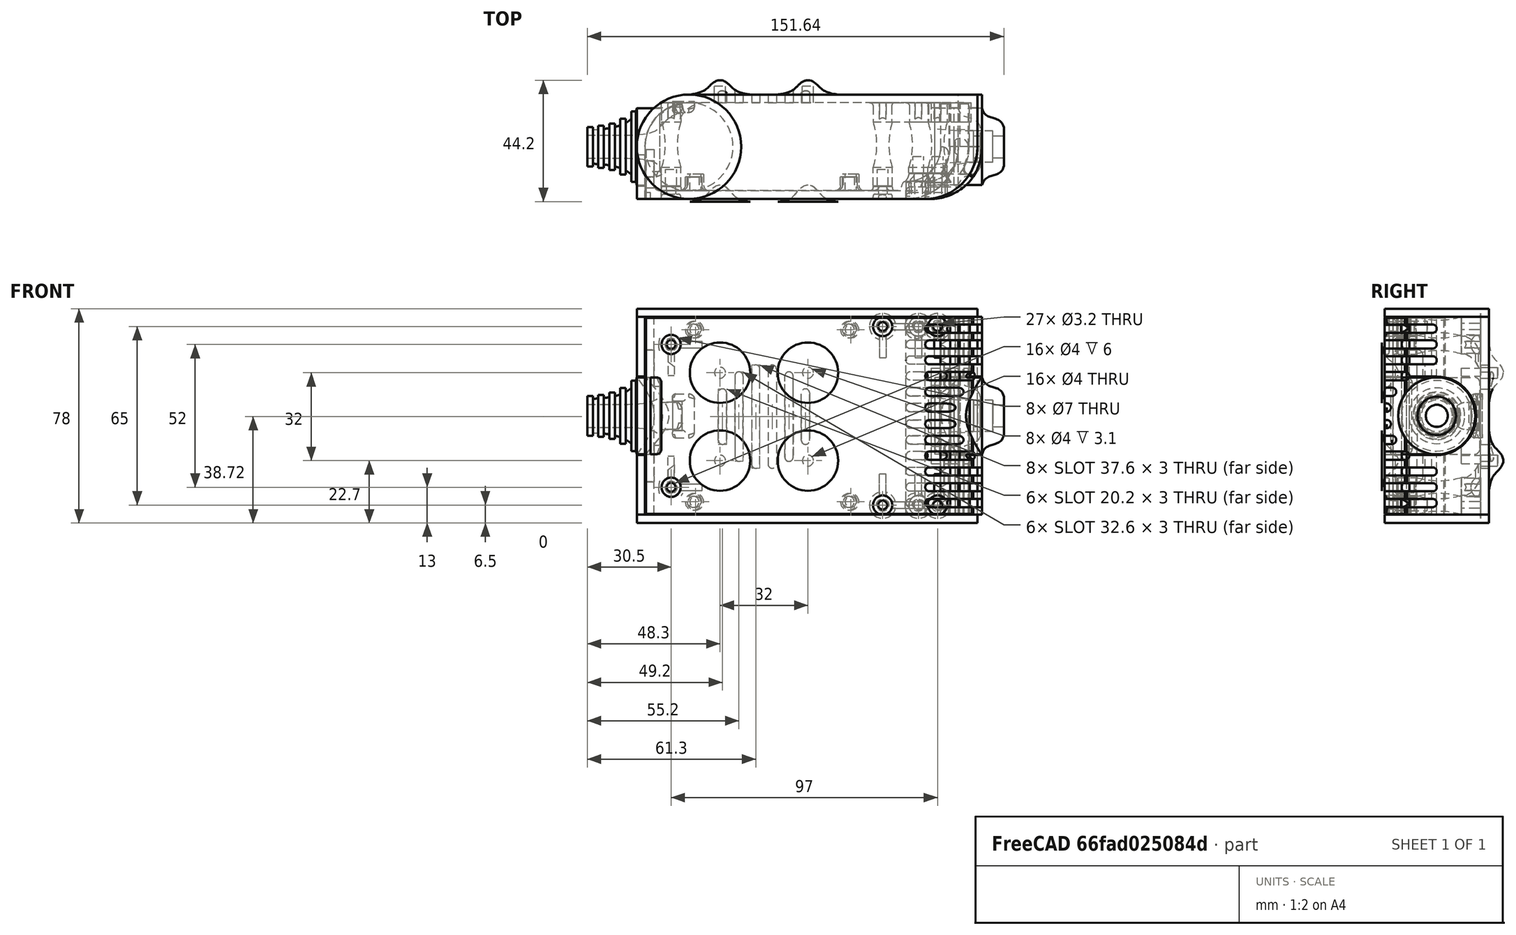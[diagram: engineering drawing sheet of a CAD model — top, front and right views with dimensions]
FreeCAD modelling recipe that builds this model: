
FCSTD DOCUMENT  (FreeCAD 0.19R0.19.2)
Label: enclosure_171FCStd
License: All rights reserved
LicenseURL: http://en.wikipedia.org/wiki/All_rights_reserved
objects: Part::Revolution×146, Part::MultiFuse×140, Part::Feature×140, Sketcher::SketchObject×78, Part::Cut×66, Part::Cylinder×66, Part::Extrusion×63, Part::Fillet×56, Part::Box×36, App::MeasureDistance×4
note: 791 computed .brp shape members not serialized (recipe doc carries the construction recipe); baked Part::Feature solids carry a one-line shape summary decoded from their .brp

FEATURE [Sketcher::SketchObject] Sketch  label="topSketch"
  FullyConstrained = true
  sketch-geometry (20):
    g0: LineSegment StartX=5.21097e-06 StartY=3 StartZ=0 EndX=5.21097e-06 EndY=19 EndZ=0
    g1: ArcOfCircle CenterX=19 CenterY=19 CenterZ=0 NormalX=0 NormalY=0 NormalZ=1 AngleXU=0 Radius=19 StartAngle=1.5708 EndAngle=3.14159
    g2: ArcOfCircle CenterX=19 CenterY=19 CenterZ=0 NormalX=0 NormalY=0 NormalZ=1 AngleXU=0 Radius=16 StartAngle=1.5708 EndAngle=3.14159
    g3: LineSegment StartX=114 StartY=35 StartZ=0 EndX=19 EndY=35 EndZ=0
    g4: LineSegment StartX=5.21097e-06 StartY=3 StartZ=0 EndX=5.21097e-06 EndY=0 EndZ=0
    g5: LineSegment StartX=3 StartY=0 StartZ=0 EndX=5.21097e-06 EndY=0 EndZ=0
    g6: LineSegment StartX=3 StartY=19 StartZ=0 EndX=3 EndY=0 EndZ=0
    g7: LineSegment StartX=19 StartY=38 StartZ=0 EndX=124 EndY=38 EndZ=0
    g8: Circle CenterX=119 CenterY=35 CenterZ=0 NormalX=0 NormalY=0 NormalZ=1 AngleXU=0 Radius=1
    g9: Circle CenterX=121 CenterY=35 CenterZ=0 NormalX=0 NormalY=0 NormalZ=1 AngleXU=0 Radius=1
    g10: Circle CenterX=121 CenterY=33 CenterZ=0 NormalX=0 NormalY=0 NormalZ=1 AngleXU=0 Radius=1
    g11: BSplineCurve PolesCount=3 KnotsCount=2 Degree=2 IsPeriodic=0
    g12: GeomPoint X=119 Y=35 Z=0
    g13: GeomPoint X=121 Y=33 Z=0
    g14: LineSegment StartX=119 StartY=35 StartZ=0 EndX=114 EndY=35 EndZ=0
    g15: ArcOfCircle CenterX=105 CenterY=19 CenterZ=0 NormalX=0 NormalY=0 NormalZ=1 AngleXU=0 Radius=19 StartAngle=5.7297 EndAngle=6.28319
    g16: ArcOfCircle CenterX=105 CenterY=19 CenterZ=0 NormalX=0 NormalY=0 NormalZ=1 AngleXU=0 Radius=16 StartAngle=5.60905 EndAngle=6.28319
    g17: LineSegment StartX=121 StartY=33 StartZ=0 EndX=121 EndY=19 EndZ=0
    g18: LineSegment StartX=124 StartY=38 StartZ=0 EndX=124 EndY=19 EndZ=0
    g19: LineSegment StartX=117.5 StartY=9.01251 StartZ=0 EndX=121.163 EndY=9.0125 EndZ=0
  constraints (46):
    c: Vertical(g0)
    c: Block(g0)
    c: Coincident(g1,g0)
    c: Block(g1)
    c: Coincident(g2,g1)
    c: Block(g2)
    c: Coincident(g3,g2)
    c: Horizontal(g3)
    c: Tangent(g3,g2)
    c: Coincident(g4,g0)
    c: Distance(g4) = 3
    c: Vertical(g4)
    c: Coincident(g5,g4)
    c: Horizontal(g5)
    c: Coincident(g6,g2)
    c: Coincident(g6,g5)
    c: Vertical(g6)
    c: Horizontal(g7)
    c: Distance(g7) = 105
    c: Coincident(g7,g1)
    c: Block(g3)
    c: Weight(g8) = 1
    c: Equal(g8,g9)
    c: Equal(g8,g10)
    c: InternalAlignment(g8,g11)
    c: InternalAlignment(g9,g11)
    c: InternalAlignment(g10,g11)
    c: InternalAlignment(g12,g11)
    c: InternalAlignment(g13,g11)
    c: Block(g11)
    c: Coincident(g14,g11)
    c: Coincident(g14,g3)
    c: Horizontal(g14)
    c: Block(g15)
    c: Coincident(g16,g15)
    c: Block(g16)
    c: Coincident(g17,g11)
    c: Coincident(g17,g16)
    c: Vertical(g17)
    c: Distance(g17) = 14
    c: Coincident(g18,g7)
    c: Coincident(g18,g15)
    c: Vertical(g18)
    c: Distance(g18) = 19
    c: Coincident(g19,g16)
    c: Coincident(g19,g15)
FEATURE [Sketcher::SketchObject] Sketch001  label="bottomSketch"
  FullyConstrained = true
  sketch-geometry (32):
    g0: LineSegment StartX=3.3 StartY=-6.03275e-07 StartZ=0 EndX=98 EndY=-6.03275e-07 EndZ=0
    g1: ArcOfCircle CenterX=98 CenterY=19 CenterZ=0 NormalX=0 NormalY=0 NormalZ=1 AngleXU=0 Radius=19 StartAngle=4.71239 EndAngle=5.71103
    g2: LineSegment StartX=6.3 StartY=8 StartZ=0 EndX=3.3 EndY=8 EndZ=0
    g3: LineSegment StartX=3.3 StartY=8 StartZ=0 EndX=3.3 EndY=-6.03275e-07 EndZ=0
    g4: ArcOfCircle CenterX=8.3 CenterY=5 CenterZ=0 NormalX=0 NormalY=0 NormalZ=1 AngleXU=0 Radius=2 StartAngle=3.14159 EndAngle=4.71239
    g5: LineSegment StartX=6.3 StartY=8 StartZ=0 EndX=6.3 EndY=5 EndZ=0
    g6: ArcOfCircle CenterX=98 CenterY=19 CenterZ=0 NormalX=0 NormalY=0 NormalZ=1 AngleXU=0 Radius=12.7 StartAngle=4.71239 EndAngle=6.28319
    g7: LineSegment StartX=94.7 StartY=3 StartZ=0 EndX=8.3 EndY=3 EndZ=0
    g8-g12: Circle x5 (B-spline internal-alignment scaffolding for g13; pole/knot coordinates omitted)
    g13: BSplineCurve PolesCount=5 KnotsCount=3 Degree=3 IsPeriodic=0
    g14: GeomPoint X=98 Y=6.3 Z=0
    g15: GeomPoint X=96.3938 Y=4.71946 Z=0
    g16: GeomPoint X=94.7 Y=3 Z=0
    g17-g23: Circle x7 (B-spline internal-alignment scaffolding for g24; pole/knot coordinates omitted)
    g24: BSplineCurve PolesCount=7 KnotsCount=5 Degree=3 IsPeriodic=0
    g25-g29: GeomPoint x5 (B-spline internal-alignment scaffolding for g24; pole/knot coordinates omitted)
    g30: ArcOfCircle CenterX=98 CenterY=19 CenterZ=0 NormalX=0 NormalY=0 NormalZ=1 AngleXU=0 Radius=15.7 StartAngle=5.81226 EndAngle=6.28319
    g31: LineSegment StartX=110.7 StartY=19 StartZ=0 EndX=113.7 EndY=19 EndZ=0
  constraints (41):
    c: Horizontal(g0)
    c: Coincident(g1,g0)
    c: Block(g1)
    c: Horizontal(g2)
    c: Distance(g2) = 3
    c: Coincident(g3,g2)
    c: Vertical(g3)
    c: Coincident(g3,g0)
    c: Block(g4)
    c: Block(g2)
    c: Coincident(g5,g2)
    c: Coincident(g5,g4)
    c: Vertical(g5)
    c: Coincident(g6,g1)
    c: Block(g6)
    c: Coincident(g7,g4)
    c: Horizontal(g7)
    c: Block(g0)
    c: Block(g7)
    c: Block(g3)
    c: Coincident(g13,g6)
    c: Weight(g8) = 1
    c: Equal(g8, g9-g12) x4
    c: Coincident(g13,g7)
    c: InternalAlignment(g8-g12 -> g13) x5
    c: InternalAlignment(g14,g13)
    c: InternalAlignment(g15,g13)
    c: InternalAlignment(g16,g13)
    c: Block(g13)
    c: Weight(g17) = 1
    c: Equal(g17, g18-g23) x6
    c: Coincident(g24,g1)
    c: InternalAlignment(g17-g23 -> g24) x7
    c: InternalAlignment(g25-g29 -> g24) x5
    c: Block(g24)
    c: Coincident(g30,g24)
    c: Coincident(g31,g6)
    c: Coincident(g31,g30)
    c: Horizontal(g31)
    c: Block(g31)
    c: Block(g30)
FEATURE [Part::Extrusion] Extrude  label="top"
  Base = -> Sketch
  Dir = (0,0,1)
  DirMode = 2
  FaceMakerClass = Part::FaceMakerBullseye
  LengthFwd = 72
  LengthRev = 0
  Solid = true
  Symmetric = false
FEATURE [Part::Extrusion] Extrude001  label="bottom"
  Base = -> Sketch001
  Dir = (0,0,1)
  DirMode = 2
  FaceMakerClass = Part::FaceMakerBullseye
  LengthFwd = 71.4
  LengthRev = 0
  Placement = pos=(0,0,0.3) rot=(0,0,1;0rad)
  Solid = true
  Symmetric = false
FEATURE [Sketcher::SketchObject] Sketch002  label="topSketch001"
  FullyConstrained = true
  sketch-geometry (6):
    g0: ArcOfCircle CenterX=19 CenterY=19 CenterZ=0 NormalX=0 NormalY=0 NormalZ=1 AngleXU=0 Radius=19 StartAngle=1.5708 EndAngle=3.14159
    g1: LineSegment StartX=5.22862e-06 StartY=19 StartZ=0 EndX=5.22862e-06 EndY=1.19904e-11 EndZ=0
    g2: LineSegment StartX=19 StartY=38 StartZ=0 EndX=124 EndY=38 EndZ=0
    g3: LineSegment StartX=5.22862e-06 StartY=1.19904e-11 StartZ=0 EndX=105 EndY=1.19904e-11 EndZ=0
    g4: ArcOfCircle CenterX=105 CenterY=19 CenterZ=0 NormalX=0 NormalY=0 NormalZ=1 AngleXU=0 Radius=19 StartAngle=4.71239 EndAngle=6.28319
    g5: LineSegment StartX=124 StartY=38 StartZ=0 EndX=124 EndY=19 EndZ=0
  constraints (16):
    c: Block(g0)
    c: Coincident(g1,g0)
    c: Vertical(g1)
    c: Horizontal(g2)
    c: Distance(g2) = 105
    c: Coincident(g2,g0)
    c: Distance(g1) = 19
    c: Coincident(g3,g1)
    c: Horizontal(g3)
    c: Distance(g3) = 105
    c: Block(g4)
    c: Coincident(g4,g3)
    c: Coincident(g5,g2)
    c: Coincident(g5,g4)
    c: Vertical(g5)
    c: Distance(g5) = 19
FEATURE [Part::Extrusion] Extrude002  label="sideA"
  Base = -> Sketch002
  Dir = (0,0,1)
  DirMode = 2
  FaceMakerClass = Part::FaceMakerBullseye
  LengthFwd = 3
  LengthRev = 0
  Placement = pos=(0,0,-3) rot=(0,0,1;0rad)
  Solid = true
  Symmetric = false
FEATURE [Sketcher::SketchObject] Sketch003  label="topSketch002"
  FullyConstrained = true
  sketch-geometry (6):
    g0: LineSegment StartX=19 StartY=38 StartZ=0 EndX=117 EndY=38 EndZ=0
    g1: ArcOfCircle CenterX=19 CenterY=19 CenterZ=0 NormalX=0 NormalY=0 NormalZ=1 AngleXU=0 Radius=19 StartAngle=1.5708 EndAngle=3.14159
    g2: LineSegment StartX=117 StartY=38 StartZ=0 EndX=117 EndY=19 EndZ=0
    g3: LineSegment StartX=98 StartY=1.0161e-12 StartZ=0 EndX=5.22862e-06 EndY=1.0161e-12 EndZ=0
    g4: LineSegment StartX=5.22862e-06 StartY=19 StartZ=0 EndX=5.22862e-06 EndY=1.0161e-12 EndZ=0
    g5: ArcOfCircle CenterX=98 CenterY=19 CenterZ=0 NormalX=0 NormalY=0 NormalZ=1 AngleXU=0 Radius=19 StartAngle=4.71239 EndAngle=6.28319
  constraints (16):
    c: Horizontal(g0)
    c: Distance(g0) = 98
    c: Coincident(g1,g0)
    c: Block(g1)
    c: Coincident(g2,g0)
    c: Vertical(g2)
    c: Distance(g2) = 19
    c: Horizontal(g3)
    c: Coincident(g4,g1)
    c: Vertical(g4)
    c: Coincident(g3,g4)
    c: Block(g3)
    c: Coincident(g5,g2)
    c: Coincident(g5,g3)
    c: Block(g0)
    c: Block(g5)
FEATURE [Sketcher::SketchObject] Sketch004
  FullyConstrained = true
  MapMode = 3
  Placement = pos=(0,0,0) rot=(1,0,0;1.5708rad)
  Support = -> [Extrude]
  sketch-geometry (8):
    g0: Circle CenterX=80.351 CenterY=-67.6202 CenterZ=0 NormalX=0 NormalY=0 NormalZ=1 AngleXU=0 Radius=2
    g1: Circle CenterX=80.351 CenterY=-67.6202 CenterZ=0 NormalX=0 NormalY=0 NormalZ=1 AngleXU=0 Radius=3
    g2: Circle CenterX=80.351 CenterY=-4.92017 CenterZ=0 NormalX=0 NormalY=0 NormalZ=1 AngleXU=0 Radius=2
    g3: Circle CenterX=80.351 CenterY=-4.92017 CenterZ=0 NormalX=0 NormalY=0 NormalZ=1 AngleXU=0 Radius=3
    g4: Circle CenterX=23.851 CenterY=-4.92017 CenterZ=0 NormalX=0 NormalY=0 NormalZ=1 AngleXU=0 Radius=2
    g5: Circle CenterX=23.851 CenterY=-4.92017 CenterZ=0 NormalX=0 NormalY=0 NormalZ=1 AngleXU=0 Radius=3
    g6: Circle CenterX=23.851 CenterY=-67.6202 CenterZ=0 NormalX=0 NormalY=0 NormalZ=1 AngleXU=0 Radius=2
    g7: Circle CenterX=23.851 CenterY=-67.6202 CenterZ=0 NormalX=0 NormalY=0 NormalZ=1 AngleXU=0 Radius=3
  constraints (8):
    c: Block(g3)
    c: Block(g2)
    c: Block(g1)
    c: Block(g0)
    c: Block(g6)
    c: Block(g7)
    c: Block(g4)
    c: Block(g5)
FEATURE [Part::Extrusion] Extrude004
  Base = -> Sketch004
  Dir = (0,-1,2e-16)
  DirMode = 2
  FaceMakerClass = Part::FaceMakerBullseye
  LengthFwd = 6
  LengthRev = 0
  Placement = pos=(0,9,0) rot=(0,0,1;0rad)
  Solid = true
  Symmetric = false
FEATURE [Sketcher::SketchObject] Sketch005
  FullyConstrained = true
  MapMode = 3
  Placement = pos=(0,0,0) rot=(1,0,0;1.5708rad)
  Support = -> [Extrude]
  sketch-geometry (8):
    g0: Circle CenterX=80.351 CenterY=-67.6202 CenterZ=0 NormalX=0 NormalY=0 NormalZ=1 AngleXU=0 Radius=3
    g1: Circle CenterX=80.351 CenterY=-4.92017 CenterZ=0 NormalX=0 NormalY=0 NormalZ=1 AngleXU=0 Radius=3
    g2: Circle CenterX=23.851 CenterY=-4.92017 CenterZ=0 NormalX=0 NormalY=0 NormalZ=1 AngleXU=0 Radius=3
    g3: Circle CenterX=23.851 CenterY=-67.6202 CenterZ=0 NormalX=0 NormalY=0 NormalZ=1 AngleXU=0 Radius=3
    g4: Circle CenterX=23.851 CenterY=-67.6202 CenterZ=0 NormalX=0 NormalY=0 NormalZ=1 AngleXU=0 Radius=5
    g5: Circle CenterX=80.351 CenterY=-67.6202 CenterZ=0 NormalX=0 NormalY=0 NormalZ=1 AngleXU=0 Radius=5
    g6: Circle CenterX=23.851 CenterY=-4.92017 CenterZ=0 NormalX=0 NormalY=0 NormalZ=1 AngleXU=0 Radius=5
    g7: Circle CenterX=80.351 CenterY=-4.92017 CenterZ=0 NormalX=0 NormalY=0 NormalZ=1 AngleXU=0 Radius=5
  constraints (8):
    c: Block(g1)
    c: Block(g0)
    c: Block(g3)
    c: Block(g2)
    c: Block(g5)
    c: Block(g4)
    c: Block(g6)
    c: Block(g7)
FEATURE [Part::Extrusion] Extrude005
  Base = -> Sketch005
  Dir = (0,-1,2e-16)
  DirMode = 2
  FaceMakerClass = Part::FaceMakerBullseye
  LengthFwd = 2
  LengthRev = 0
  Solid = true
  Symmetric = false
FEATURE [Sketcher::SketchObject] Sketch006
  FullyConstrained = true
  MapMode = 3
  Placement = pos=(0,0,0) rot=(1,0,0;1.5708rad)
  sketch-geometry (8):
    g0: Circle CenterX=80.351 CenterY=-67.6202 CenterZ=0 NormalX=0 NormalY=0 NormalZ=1 AngleXU=0 Radius=3
    g1: Circle CenterX=80.351 CenterY=-4.92017 CenterZ=0 NormalX=0 NormalY=0 NormalZ=1 AngleXU=0 Radius=3
    g2: Circle CenterX=23.851 CenterY=-4.92017 CenterZ=0 NormalX=0 NormalY=0 NormalZ=1 AngleXU=0 Radius=3
    g3: Circle CenterX=23.851 CenterY=-67.6202 CenterZ=0 NormalX=0 NormalY=0 NormalZ=1 AngleXU=0 Radius=3
    g4: Circle CenterX=23.851 CenterY=-67.6202 CenterZ=0 NormalX=0 NormalY=0 NormalZ=1 AngleXU=0 Radius=5
    g5: Circle CenterX=80.351 CenterY=-67.6202 CenterZ=0 NormalX=0 NormalY=0 NormalZ=1 AngleXU=0 Radius=5
    g6: Circle CenterX=23.851 CenterY=-4.92017 CenterZ=0 NormalX=0 NormalY=0 NormalZ=1 AngleXU=0 Radius=5
    g7: Circle CenterX=80.351 CenterY=-4.92017 CenterZ=0 NormalX=0 NormalY=0 NormalZ=1 AngleXU=0 Radius=5
  constraints (8):
    c: Block(g1)
    c: Block(g0)
    c: Block(g3)
    c: Block(g2)
    c: Block(g5)
    c: Block(g4)
    c: Block(g6)
    c: Block(g7)
FEATURE [Part::Extrusion] Extrude007
  Base = -> Sketch006
  Dir = (0,-1,2e-16)
  DirMode = 2
  FaceMakerClass = Part::FaceMakerBullseye
  LengthFwd = 2
  LengthRev = 0
  Solid = true
  Symmetric = false
FEATURE [Part::Fillet] Fillet
  Base = -> Extrude007
  Edges = 4 edges r=1.99: [Edge6,Edge12,Edge18,Edge24]
FEATURE [Part::Cut] Cut
  Base = -> Extrude005
  Placement = pos=(0,5,0) rot=(0,0,1;0rad)
  Tool = -> Fillet
FEATURE [Part::MultiFuse] Fusion  label="pCBScrews"
  Placement = pos=(-2.5,0,72.3) rot=(0,0,1;0rad)
  Shapes = -> [Extrude004,Cut]
FEATURE [App::MeasureDistance] Distance  label="Distance: 0.69 mm"
  Distance = 0.685967
  P1 = (24.0138,2.9647,0.3)
  P2 = (23.8901,3,-0.373787)
FEATURE [App::MeasureDistance] Distance001  label="Distance: 0.53 mm"
  Distance = 0.533607
  P1 = (80.2939,3,72.2334)
  P2 = (80.281,2.99661,71.7)
FEATURE [Part::Fillet] Fillet001
  Base = -> Extrude001
  Edges = 1 edges r=2.4: [Edge17]
FEATURE [Part::Fillet] Fillet002  label="bottom001"
  Base = -> Fillet001
  Edges = 1 edges r=2.4: [Edge36]
FEATURE [Part::Fillet] Fillet003  label="top001"
  Base = -> Extrude
  Edges = 1 edges r=2: [Edge1]
FEATURE [Sketcher::SketchObject] Sketch007
  FullyConstrained = true
  sketch-geometry (16):
    g0: LineSegment StartX=4 StartY=0 StartZ=0 EndX=4 EndY=2.4 EndZ=0
    g1: LineSegment StartX=4 StartY=2.4 StartZ=0 EndX=7 EndY=2.4 EndZ=0
    g2: LineSegment StartX=4 StartY=0 StartZ=0 EndX=5.7 EndY=0 EndZ=0
    g3: LineSegment StartX=5.7 StartY=0 StartZ=0 EndX=5.7 EndY=-5.6 EndZ=0
    g4-g8: Circle x5 (B-spline internal-alignment scaffolding for g9; pole/knot coordinates omitted)
    g9: BSplineCurve PolesCount=5 KnotsCount=3 Degree=3 IsPeriodic=0
    g10: GeomPoint X=7 Y=2.4 Z=0
    g11: GeomPoint X=10.4582 Y=-1.55472 Z=0
    g12: GeomPoint X=14 Y=-5.6 Z=0
    g13: LineSegment StartX=14 StartY=-5.6 StartZ=0 EndX=14 EndY=-14.1 EndZ=0
    g14: LineSegment StartX=14 StartY=-14.1 StartZ=0 EndX=6.5 EndY=-14.1 EndZ=0
    g15: LineSegment StartX=5.7 StartY=-5.6 StartZ=0 EndX=6.5 EndY=-14.1 EndZ=0
  constraints (28):
    c: Distance(g0) = 2.4
    c: Vertical(g0)
    c: Block(g0)
    c: Coincident(g1,g0)
    c: Horizontal(g1)
    c: Distance(g1) = 3
    c: Coincident(g2,g0)
    c: Horizontal(g2)
    c: Distance(g2) = 1.7
    c: Coincident(g3,g2)
    c: Vertical(g3)
    c: Distance(g3) = 5.6
    c: Coincident(g9,g1)
    c: Weight(g4) = 1
    c: Equal(g4, g5-g8) x4
    c: InternalAlignment(g4-g8 -> g9) x5
    c: InternalAlignment(g10,g9)
    c: InternalAlignment(g11,g9)
    c: InternalAlignment(g12,g9)
    c: Block(g9)
    c: Coincident(g13,g9)
    c: Vertical(g13)
    c: Distance(g13) = 8.5
    c: Coincident(g14,g13)
    c: Horizontal(g14)
    c: Distance(g14) = 7.5
    c: Coincident(g15,g3)
    c: Coincident(g15,g14)
FEATURE [Part::Feature] Face
  shape: bbox 10 x 16.5 x 2e-07 mm, 1 faces, 0 solids (baked)
FEATURE [Part::Revolution] Revolve  label="plugHousing"
  Angle = 360
  Axis = (0,1,0)
  Base = (0,0,0)
  FaceMakerClass = Part::FaceMakerBullseye
  Placement = pos=(0,0,36.15) rot=(0,0,1;0rad)
  Solid = false
  Source = -> Face
  Symmetric = false
FEATURE [Part::Feature] Face001
  shape: bbox 10 x 16.5 x 2e-07 mm, 1 faces, 0 solids (baked)
FEATURE [Part::Revolution] Revolve001  label="plugHousing001"
  Angle = 360
  Axis = (0,1,0)
  Base = (0,0,0)
  FaceMakerClass = Part::FaceMakerBullseye
  Placement = pos=(0,0,36.15) rot=(0,0,1;0rad)
  Solid = false
  Source = -> Face001
  Symmetric = false
FEATURE [Part::MultiFuse] Fusion001  label="plugHousing002"
  Placement = pos=(0,0,0) rot=(0,0,1;1.5708rad)
  Shapes = -> [Revolve001,Revolve]
FEATURE [Part::Feature] Face002
  shape: bbox 10 x 16.5 x 2e-07 mm, 1 faces, 0 solids (baked)
FEATURE [Part::Revolution] Revolve003  label="plugHousing005"
  Angle = 360
  Axis = (0,1,0)
  Base = (0,0,0)
  FaceMakerClass = Part::FaceMakerBullseye
  Placement = pos=(0,0,36.15) rot=(0,0,1;0rad)
  Solid = false
  Source = -> Face002
  Symmetric = false
FEATURE [Part::Feature] Face003
  shape: bbox 10 x 16.5 x 2e-07 mm, 1 faces, 0 solids (baked)
FEATURE [Part::Revolution] Revolve002  label="plugHousing003"
  Angle = 360
  Axis = (0,1,0)
  Base = (0,0,0)
  FaceMakerClass = Part::FaceMakerBullseye
  Placement = pos=(0,0,36.15) rot=(0,0,1;0rad)
  Solid = false
  Source = -> Face003
  Symmetric = false
FEATURE [Part::MultiFuse] Fusion002  label="plugHousing004"
  Placement = pos=(0,0,0) rot=(0,0,1;1.5708rad)
  Shapes = -> [Revolve002,Revolve003]
FEATURE [Part::MultiFuse] Fusion003  label="plugHousing006"
  Placement = pos=(0,19,0) rot=(0,0,1;3.14159rad)
  Shapes = -> [Fusion002,Fusion001]
FEATURE [Part::Feature] Face004
  shape: bbox 10 x 16.5 x 2e-07 mm, 1 faces, 0 solids (baked)
FEATURE [Part::Revolution] Revolve006  label="plugHousing010"
  Angle = 360
  Axis = (0,1,0)
  Base = (0,0,0)
  FaceMakerClass = Part::FaceMakerBullseye
  Placement = pos=(0,0,36.15) rot=(0,0,1;0rad)
  Solid = false
  Source = -> Face004
  Symmetric = false
FEATURE [Part::Feature] Face005
  shape: bbox 10 x 16.5 x 2e-07 mm, 1 faces, 0 solids (baked)
FEATURE [Part::Revolution] Revolve007  label="plugHousing011"
  Angle = 360
  Axis = (0,1,0)
  Base = (0,0,0)
  FaceMakerClass = Part::FaceMakerBullseye
  Placement = pos=(0,0,36.15) rot=(0,0,1;0rad)
  Solid = false
  Source = -> Face005
  Symmetric = false
FEATURE [Part::Feature] Face006
  shape: bbox 10 x 16.5 x 2e-07 mm, 1 faces, 0 solids (baked)
FEATURE [Part::Revolution] Revolve004  label="plugHousing007"
  Angle = 360
  Axis = (0,1,0)
  Base = (0,0,0)
  FaceMakerClass = Part::FaceMakerBullseye
  Placement = pos=(0,0,36.15) rot=(0,0,1;0rad)
  Solid = false
  Source = -> Face006
  Symmetric = false
FEATURE [Part::MultiFuse] Fusion004  label="plugHousing009"
  Placement = pos=(0,0,0) rot=(0,0,1;1.5708rad)
  Shapes = -> [Revolve004,Revolve007]
FEATURE [Part::Feature] Face007
  shape: bbox 10 x 16.5 x 2e-07 mm, 1 faces, 0 solids (baked)
FEATURE [Part::Revolution] Revolve005  label="plugHousing008"
  Angle = 360
  Axis = (0,1,0)
  Base = (0,0,0)
  FaceMakerClass = Part::FaceMakerBullseye
  Placement = pos=(0,0,36.15) rot=(0,0,1;0rad)
  Solid = false
  Source = -> Face007
  Symmetric = false
FEATURE [Part::MultiFuse] Fusion005  label="plugHousing012"
  Placement = pos=(0,0,0) rot=(0,0,1;1.5708rad)
  Shapes = -> [Revolve006,Revolve005]
FEATURE [Part::MultiFuse] Fusion006  label="plugHousing013"
  Placement = pos=(0,19,0) rot=(0,0,1;3.14159rad)
  Shapes = -> [Fusion005,Fusion004]
FEATURE [Part::MultiFuse] Fusion007  label="plugHousing014"
  Placement = pos=(122.621,0,-0.15) rot=(0,0,1;0rad)
  Shapes = -> [Fusion003,Fusion006]
FEATURE [Part::Cylinder] Cylinder002
  Angle = 360
  AttacherType = Attacher::AttachEngine3D
  Height = 20
  Placement = pos=(0,0,36.15) rot=(0,0,1;0rad)
  Radius = 4
FEATURE [Part::Cylinder] Cylinder003
  Angle = 360
  AttacherType = Attacher::AttachEngine3D
  Height = 10
  Placement = pos=(0,0,36.15) rot=(0,0,1;0rad)
  Radius = 4
FEATURE [Part::MultiFuse] Fusion009  label="removeToCreateHoleForPlugHousing"
  Placement = pos=(70,19,36.15) rot=(0,1,0;1.5708rad)
  Shapes = -> [Cylinder002,Cylinder003]
FEATURE [Part::Cylinder] Cylinder004
  Angle = 360
  AttacherType = Attacher::AttachEngine3D
  Height = 20
  Placement = pos=(0,0,36.15) rot=(0,0,1;0rad)
  Radius = 4
FEATURE [Part::Cylinder] Cylinder005
  Angle = 360
  AttacherType = Attacher::AttachEngine3D
  Height = 10
  Placement = pos=(0,0,36.15) rot=(0,0,1;0rad)
  Radius = 4
FEATURE [Part::MultiFuse] Fusion010  label="removeToCreateHoleForPlugHousing001"
  Placement = pos=(70,19,36.15) rot=(0,1,0;1.5708rad)
  Shapes = -> [Cylinder004,Cylinder005]
FEATURE [Part::Cut] Cut001
  Base = -> Fillet003
  Tool = -> Fusion010
FEATURE [Part::Cut] Cut002  label="Bottom"
  Base = -> Fillet002
  Tool = -> Fusion009
FEATURE [Part::Feature] Face008
  shape: bbox 10 x 16.5 x 2e-07 mm, 1 faces, 0 solids (baked)
FEATURE [Part::Revolution] Revolve011  label="plugHousing021"
  Angle = 360
  Axis = (0,1,0)
  Base = (0,0,0)
  FaceMakerClass = Part::FaceMakerBullseye
  Placement = pos=(0,0,36.15) rot=(0,0,1;0rad)
  Solid = false
  Source = -> Face008
  Symmetric = false
FEATURE [Part::Feature] Face009
  shape: bbox 10 x 16.5 x 2e-07 mm, 1 faces, 0 solids (baked)
FEATURE [Part::Revolution] Revolve012  label="plugHousing022"
  Angle = 360
  Axis = (0,1,0)
  Base = (0,0,0)
  FaceMakerClass = Part::FaceMakerBullseye
  Placement = pos=(0,0,36.15) rot=(0,0,1;0rad)
  Solid = false
  Source = -> Face009
  Symmetric = false
FEATURE [Part::Feature] Face010 .. Face013  x4 (patterned run collapsed; names and placements below)
  shape: bbox 10 x 16.5 x 2e-07 mm, 1 faces, 0 solids (baked)
FEATURE [Part::Revolution] Revolve015  label="plugHousing027"
  Angle = 360
  Axis = (0,1,0)
  Base = (0,0,0)
  FaceMakerClass = Part::FaceMakerBullseye
  Placement = pos=(0,0,36.15) rot=(0,0,1;0rad)
  Solid = false
  Source = -> Face013
  Symmetric = false
FEATURE [Part::Feature] Face014
  shape: bbox 10 x 16.5 x 2e-07 mm, 1 faces, 0 solids (baked)
FEATURE [Part::Feature] Face015
  shape: bbox 10 x 16.5 x 2e-07 mm, 1 faces, 0 solids (baked)
FEATURE [Part::Feature] Face016
  shape: bbox 10 x 16.5 x 2e-07 mm, 1 faces, 0 solids (baked)
FEATURE [Part::Revolution] Revolve019  label="plugHousing033"
  Angle = 360
  Axis = (0,1,0)
  Base = (0,0,0)
  FaceMakerClass = Part::FaceMakerBullseye
  Placement = pos=(0,0,36.15) rot=(0,0,1;0rad)
  Solid = false
  Source = -> Face016
  Symmetric = false
FEATURE [Part::Feature] Face017
  shape: bbox 10 x 16.5 x 2e-07 mm, 1 faces, 0 solids (baked)
FEATURE [Part::Revolution] Revolve020  label="plugHousing034"
  Angle = 360
  Axis = (0,1,0)
  Base = (0,0,0)
  FaceMakerClass = Part::FaceMakerBullseye
  Placement = pos=(0,0,36.15) rot=(0,0,1;0rad)
  Solid = false
  Source = -> Face017
  Symmetric = false
FEATURE [Part::Feature] Face018
  shape: bbox 10 x 16.5 x 2e-07 mm, 1 faces, 0 solids (baked)
FEATURE [Part::Revolution] Revolve016  label="plugHousing030"
  Angle = 360
  Axis = (0,1,0)
  Base = (0,0,0)
  FaceMakerClass = Part::FaceMakerBullseye
  Placement = pos=(0,0,36.15) rot=(0,0,1;0rad)
  Solid = false
  Source = -> Face018
  Symmetric = false
FEATURE [Part::MultiFuse] Fusion020  label="plugHousing038"
  Placement = pos=(0,0,0) rot=(0,0,1;1.5708rad)
  Shapes = -> [Revolve016,Revolve020]
FEATURE [Part::Feature] Face019
  shape: bbox 10 x 16.5 x 2e-07 mm, 1 faces, 0 solids (baked)
FEATURE [Part::Feature] Face020
  shape: bbox 10 x 16.5 x 2e-07 mm, 1 faces, 0 solids (baked)
FEATURE [Part::Revolution] Revolve017  label="plugHousing031"
  Angle = 360
  Axis = (0,1,0)
  Base = (0,0,0)
  FaceMakerClass = Part::FaceMakerBullseye
  Placement = pos=(0,0,36.15) rot=(0,0,1;0rad)
  Solid = false
  Source = -> Face020
  Symmetric = false
FEATURE [Part::MultiFuse] Fusion021  label="plugHousing039"
  Placement = pos=(0,0,0) rot=(0,0,1;1.5708rad)
  Shapes = -> [Revolve019,Revolve017]
FEATURE [Part::MultiFuse] Fusion023  label="plugHousing041"
  Placement = pos=(0,19,0) rot=(0,0,1;3.14159rad)
  Shapes = -> [Fusion021,Fusion020]
FEATURE [Part::Revolution] Revolve022  label="plugHousing043"
  Angle = 360
  Axis = (0,1,0)
  Base = (0,0,0)
  FaceMakerClass = Part::FaceMakerBullseye
  Placement = pos=(0,0,36.15) rot=(0,0,1;0rad)
  Solid = false
  Source = -> Face019
  Symmetric = false
FEATURE [Part::Feature] Face021
  shape: bbox 10 x 16.5 x 2e-07 mm, 1 faces, 0 solids (baked)
FEATURE [Part::Revolution] Revolve023  label="plugHousing044"
  Angle = 360
  Axis = (0,1,0)
  Base = (0,0,0)
  FaceMakerClass = Part::FaceMakerBullseye
  Placement = pos=(0,0,36.15) rot=(0,0,1;0rad)
  Solid = false
  Source = -> Face021
  Symmetric = false
FEATURE [Part::Feature] Face022
  shape: bbox 10 x 16.5 x 2e-07 mm, 1 faces, 0 solids (baked)
FEATURE [Part::Revolution] Revolve018  label="plugHousing032"
  Angle = 360
  Axis = (0,1,0)
  Base = (0,0,0)
  FaceMakerClass = Part::FaceMakerBullseye
  Placement = pos=(0,0,36.15) rot=(0,0,1;0rad)
  Solid = false
  Source = -> Face022
  Symmetric = false
FEATURE [Part::MultiFuse] Fusion022  label="plugHousing040"
  Placement = pos=(0,0,0) rot=(0,0,1;1.5708rad)
  Shapes = -> [Revolve018,Revolve023]
FEATURE [Part::Feature] Face023
  shape: bbox 10 x 16.5 x 2e-07 mm, 1 faces, 0 solids (baked)
FEATURE [Part::Revolution] Revolve021  label="plugHousing035"
  Angle = 360
  Axis = (0,1,0)
  Base = (0,0,0)
  FaceMakerClass = Part::FaceMakerBullseye
  Placement = pos=(0,0,36.15) rot=(0,0,1;0rad)
  Solid = false
  Source = -> Face023
  Symmetric = false
FEATURE [Part::MultiFuse] Fusion018  label="plugHousing036"
  Placement = pos=(0,0,0) rot=(0,0,1;1.5708rad)
  Shapes = -> [Revolve022,Revolve021]
FEATURE [Part::MultiFuse] Fusion019  label="plugHousing037"
  Placement = pos=(0,19,0) rot=(0,0,1;3.14159rad)
  Shapes = -> [Fusion018,Fusion022]
FEATURE [Part::MultiFuse] Fusion024  label="plugHousing042"
  Placement = pos=(122.621,0,-0.15) rot=(0,0,1;0rad)
  Shapes = -> [Fusion023,Fusion019]
FEATURE [Part::Cylinder] Cylinder006
  Angle = 360
  AttacherType = Attacher::AttachEngine3D
  Height = 20
  Placement = pos=(0,0,36.15) rot=(0,0,1;0rad)
  Radius = 14.3
FEATURE [Part::Cylinder] Cylinder007
  Angle = 360
  AttacherType = Attacher::AttachEngine3D
  Height = 10
  Placement = pos=(0,0,36.15) rot=(0,0,1;0rad)
  Radius = 4
FEATURE [Part::MultiFuse] Fusion026  label="removeToCreteHoleForPlugHousing"
  Placement = pos=(70,19,36) rot=(0,1,0;1.5708rad)
  Shapes = -> [Cylinder006,Cylinder007]
FEATURE [Part::Box] Box001  label="Cube001"
  AttacherType = Attacher::AttachEngine3D
  Height = 28
  Length = 3
  Placement = pos=(110.7,19,22) rot=(0,0,1;0rad)
  Width = 15.7
FEATURE [Part::Cut] Cut003  label="top002"
  Base = -> Cut001
  Tool = -> Fusion007
FEATURE [Part::Revolution] Revolve008  label="plugHousing015"
  Angle = 360
  Axis = (0,1,0)
  Base = (0,0,0)
  FaceMakerClass = Part::FaceMakerBullseye
  Placement = pos=(0,0,36.15) rot=(0,0,1;0rad)
  Solid = false
  Source = -> Face010
  Symmetric = false
FEATURE [Part::MultiFuse] Fusion013  label="plugHousing020"
  Placement = pos=(0,0,0) rot=(0,0,1;1.5708rad)
  Shapes = -> [Revolve008,Revolve012]
FEATURE [Part::Cut] Cut004  label="top003"
  Base = -> Cut003
  Placement = pos=(1,0,0) rot=(0,0,1;0rad)
  Tool = -> Fusion026
FEATURE [Part::Cylinder] Cylinder008
  Angle = 360
  AttacherType = Attacher::AttachEngine3D
  Height = 20
  Placement = pos=(0,0,36.15) rot=(0,0,1;0rad)
  Radius = 10.3
FEATURE [Part::Cylinder] Cylinder009
  Angle = 360
  AttacherType = Attacher::AttachEngine3D
  Height = 10
  Placement = pos=(0,0,36.15) rot=(0,0,1;0rad)
  Radius = 4
FEATURE [Part::MultiFuse] Fusion027  label="removeToCreteHoleForPlugHousing001"
  Placement = pos=(70,19,36) rot=(0,1,0;1.5708rad)
  Shapes = -> [Cylinder008,Cylinder009]
FEATURE [Part::Cut] Cut005  label="plugHousingTab"
  Base = -> Box001
  Tool = -> Fusion027
FEATURE [Part::MultiFuse] Fusion028  label="plugHousing045"
  Shapes = -> [Fusion024,Cut005]
FEATURE [Part::Box] Box002  label="Cube002"
  AttacherType = Attacher::AttachEngine3D
  Height = 28.8
  Length = 3
  Placement = pos=(107.3,28,21.6) rot=(0,0,1;0rad)
  Width = 7
FEATURE [Part::Box] Box003  label="Cube003"
  AttacherType = Attacher::AttachEngine3D
  Height = 3
  Length = 6.4
  Placement = pos=(107.3,28,18.6) rot=(0,0,1;0rad)
  Width = 7
FEATURE [Part::Box] Box004  label="Cube004"
  AttacherType = Attacher::AttachEngine3D
  Height = 3
  Length = 6.4
  Placement = pos=(107.3,28,50.4) rot=(0,0,1;0rad)
  Width = 7
FEATURE [Part::MultiFuse] Fusion029  label="plugHousingBracketHolder"
  Shapes = -> [Box004,Box002,Box003]
FEATURE [Part::Cylinder] Cylinder010
  Angle = 360
  AttacherType = Attacher::AttachEngine3D
  Height = 20
  Placement = pos=(0,0,36.15) rot=(0,0,1;0rad)
  Radius = 14.3
FEATURE [Part::Cylinder] Cylinder011
  Angle = 360
  AttacherType = Attacher::AttachEngine3D
  Height = 10
  Placement = pos=(0,0,36.15) rot=(0,0,1;0rad)
  Radius = 4
FEATURE [Part::MultiFuse] Fusion030  label="removeToCreteHoleForPlugHousing002"
  Placement = pos=(70,19,36) rot=(0,1,0;1.5708rad)
  Shapes = -> [Cylinder010,Cylinder011]
FEATURE [Part::Cut] Cut006  label="plugHousingBracketHolder001"
  Base = -> Fusion029
  Tool = -> Fusion030
FEATURE [Part::Cylinder] Cylinder012
  Angle = 360
  AttacherType = Attacher::AttachEngine3D
  Height = 20
  Placement = pos=(0,0,36.15) rot=(0,0,1;0rad)
  Radius = 7
FEATURE [Part::Cylinder] Cylinder013
  Angle = 360
  AttacherType = Attacher::AttachEngine3D
  Height = 10
  Placement = pos=(0,0,36.15) rot=(0,0,1;0rad)
  Radius = 4
FEATURE [Part::MultiFuse] Fusion032  label="removeToCreteHoleForPlugHousing003"
  Placement = pos=(70,19,36) rot=(0,1,0;1.5708rad)
  Shapes = -> [Cylinder012,Cylinder013]
FEATURE [Part::Cut] Cut007  label="bottom002"
  Base = -> Cut002
  Tool = -> Fusion032
FEATURE [Sketcher::SketchObject] Sketch008
  FullyConstrained = true
  sketch-geometry (54):
    g0: LineSegment StartX=-4.2 StartY=0 StartZ=0 EndX=-6.2 EndY=0 EndZ=0
    g1: LineSegment StartX=-14 StartY=-18 StartZ=0 EndX=-14 EndY=-26.5 EndZ=0
    g2: LineSegment StartX=-4.2 StartY=0 StartZ=0 EndX=-4.2 EndY=-13.4877 EndZ=0
    g3: Circle CenterX=-4.2 CenterY=-13.4877 CenterZ=0 NormalX=0 NormalY=0 NormalZ=1 AngleXU=0 Radius=1
    g4: Circle CenterX=-4.2 CenterY=-26.5 CenterZ=0 NormalX=0 NormalY=0 NormalZ=1 AngleXU=0 Radius=1
    g5: Circle CenterX=-8.2 CenterY=-26.5 CenterZ=0 NormalX=0 NormalY=0 NormalZ=1 AngleXU=0 Radius=1
    g6: BSplineCurve PolesCount=3 KnotsCount=2 Degree=2 IsPeriodic=0
    g7: GeomPoint X=-4.2 Y=-13.4877 Z=0
    g8: GeomPoint X=-8.2 Y=-26.5 Z=0
    g9: LineSegment StartX=-14 StartY=-26.5 StartZ=0 EndX=-8.2 EndY=-26.5 EndZ=0
    g10: LineSegment StartX=-10.15 StartY=-12 StartZ=0 EndX=-10.15 EndY=-14 EndZ=0
    g11: LineSegment StartX=-12.8401 StartY=-16 StartZ=0 EndX=-10.1571 EndY=-16 EndZ=0
    g12: LineSegment StartX=-10.15 StartY=-14 StartZ=0 EndX=-8.70761 EndY=-14 EndZ=0
    g13: LineSegment StartX=-12.8401 StartY=-16 StartZ=0 EndX=-12.8401 EndY=-17.6958 EndZ=0
    g14: LineSegment StartX=-10.15 StartY=-12 StartZ=0 EndX=-7.79258 EndY=-12 EndZ=0
    g15: Circle CenterX=-6.2215 CenterY=-2 CenterZ=0 NormalX=0 NormalY=0 NormalZ=1 AngleXU=0 Radius=1
    g16: Circle CenterX=-6.22762 CenterY=-2.58724 CenterZ=0 NormalX=0 NormalY=0 NormalZ=1 AngleXU=0 Radius=1
    g17: Circle CenterX=-6.32538 CenterY=-4 CenterZ=0 NormalX=0 NormalY=0 NormalZ=1 AngleXU=0 Radius=1
    g18: BSplineCurve PolesCount=3 KnotsCount=2 Degree=2 IsPeriodic=0
    g19: GeomPoint X=-6.2215 Y=-2 Z=0
    g20: GeomPoint X=-6.32538 Y=-4 Z=0
    g21: Circle CenterX=-6.48644 CenterY=-5.99526 CenterZ=0 NormalX=0 NormalY=0 NormalZ=1 AngleXU=0 Radius=1
    g22: Circle CenterX=-6.58486 CenterY=-6.99526 CenterZ=0 NormalX=0 NormalY=0 NormalZ=1 AngleXU=0 Radius=1
    g23: Circle CenterX=-6.77343 CenterY=-8 CenterZ=0 NormalX=0 NormalY=0 NormalZ=1 AngleXU=0 Radius=1
    g24: BSplineCurve PolesCount=3 KnotsCount=2 Degree=2 IsPeriodic=0
    g25: GeomPoint X=-6.48644 Y=-5.99526 Z=0
    g26: GeomPoint X=-6.77343 Y=-8 Z=0
    g27: Circle CenterX=-7.19003 CenterY=-10 CenterZ=0 NormalX=0 NormalY=0 NormalZ=1 AngleXU=0 Radius=1
    g28: Circle CenterX=-7.44407 CenterY=-11.0915 CenterZ=0 NormalX=0 NormalY=0 NormalZ=1 AngleXU=0 Radius=1
    g29: Circle CenterX=-7.79258 CenterY=-12 CenterZ=0 NormalX=0 NormalY=0 NormalZ=1 AngleXU=0 Radius=1
    g30: BSplineCurve PolesCount=3 KnotsCount=2 Degree=2 IsPeriodic=0
    g31: GeomPoint X=-7.19003 Y=-10 Z=0
    g32: GeomPoint X=-7.79258 Y=-12 Z=0
    g33: Circle CenterX=-8.70761 CenterY=-14 CenterZ=0 NormalX=0 NormalY=0 NormalZ=1 AngleXU=0 Radius=1
    g34: Circle CenterX=-9.33087 CenterY=-15.1837 CenterZ=0 NormalX=0 NormalY=0 NormalZ=1 AngleXU=0 Radius=1
    g35: Circle CenterX=-10.1571 CenterY=-16 CenterZ=0 NormalX=0 NormalY=0 NormalZ=1 AngleXU=0 Radius=1
    g36: BSplineCurve PolesCount=3 KnotsCount=2 Degree=2 IsPeriodic=0
    g37: GeomPoint X=-8.70761 Y=-14 Z=0
    g38: GeomPoint X=-10.1571 Y=-16 Z=0
    g39: Circle CenterX=-12.8401 CenterY=-17.6958 CenterZ=0 NormalX=0 NormalY=0 NormalZ=1 AngleXU=0 Radius=1
    g40: Circle CenterX=-13.3521 CenterY=-17.9027 CenterZ=0 NormalX=0 NormalY=0 NormalZ=1 AngleXU=0 Radius=1
    g41: Circle CenterX=-14 CenterY=-18 CenterZ=0 NormalX=0 NormalY=0 NormalZ=1 AngleXU=0 Radius=1
    g42: BSplineCurve PolesCount=3 KnotsCount=2 Degree=2 IsPeriodic=0
    g43: GeomPoint X=-12.8401 Y=-17.6958 Z=0
    g44: GeomPoint X=-14 Y=-18 Z=0
    g45: LineSegment StartX=-6.2 StartY=0 StartZ=0 EndX=-7.2 EndY=0 EndZ=0
    g46: LineSegment StartX=-7.2 StartY=0 StartZ=0 EndX=-7.2 EndY=-2 EndZ=0
    g47: LineSegment StartX=-7.2 StartY=-2 StartZ=0 EndX=-6.2215 EndY=-2 EndZ=0
    g48: LineSegment StartX=-6.32538 StartY=-4 StartZ=0 EndX=-7.65538 EndY=-4 EndZ=0
    g49: LineSegment StartX=-7.65538 StartY=-4 StartZ=0 EndX=-7.65538 EndY=-5.99526 EndZ=0
    g50: LineSegment StartX=-7.65538 StartY=-5.99526 StartZ=0 EndX=-6.48644 EndY=-5.99526 EndZ=0
    g51: LineSegment StartX=-6.77343 StartY=-8 StartZ=0 EndX=-8.43343 EndY=-8 EndZ=0
    g52: LineSegment StartX=-8.43343 StartY=-8 StartZ=0 EndX=-8.43343 EndY=-10 EndZ=0
    g53: LineSegment StartX=-8.43343 StartY=-10 StartZ=0 EndX=-7.19003 EndY=-10 EndZ=0
  constraints (112):
    c: Horizontal(g0)
    c: Distance(g0) = 2
    c: Block(g0)
    c: Vertical(g1)
    c: Coincident(g2,g0)
    c: Vertical(g2)
    c: Block(g2)
    c: Coincident(g6,g2)
    c: Weight(g3) = 1
    c: Equal(g3,g4)
    c: Equal(g3,g5)
    c: InternalAlignment(g3,g6)
    c: InternalAlignment(g4,g6)
    c: InternalAlignment(g5,g6)
    c: InternalAlignment(g7,g6)
    c: InternalAlignment(g8,g6)
    c: Block(g6)
    c: Coincident(g9,g1)
    c: Coincident(g9,g6)
    c: Horizontal(g9)
    c: Vertical(g10)
    c: Block(g10)
    c: Horizontal(g11)
    c: Block(g11)
    c: Coincident(g12,g10)
    c: Horizontal(g12)
    c: Block(g12)
    c: Coincident(g13,g11)
    c: Vertical(g13)
    c: Block(g13)
    c: Coincident(g14,g10)
    c: Horizontal(g14)
    c: Block(g14)
    c: Block(g9)
    c: Block(g1)
    c: Weight(g15) = 1
    c: Equal(g15,g16)
    c: Equal(g15,g17)
    c: InternalAlignment(g15,g18)
    c: InternalAlignment(g16,g18)
    c: InternalAlignment(g17,g18)
    c: InternalAlignment(g19,g18)
    c: InternalAlignment(g20,g18)
    c: Weight(g21) = 1
    c: Equal(g21,g22)
    c: Equal(g21,g23)
    c: InternalAlignment(g21,g24)
    c: InternalAlignment(g22,g24)
    c: InternalAlignment(g23,g24)
    c: InternalAlignment(g25,g24)
    c: InternalAlignment(g26,g24)
    c: Weight(g27) = 1
    c: Equal(g27,g28)
    c: Equal(g27,g29)
    c: Coincident(g30,g14)
    c: InternalAlignment(g27,g30)
    c: InternalAlignment(g28,g30)
    c: InternalAlignment(g29,g30)
    c: InternalAlignment(g31,g30)
    c: InternalAlignment(g32,g30)
    c: Coincident(g36,g12)
    c: Weight(g33) = 1
    c: Equal(g33,g34)
    c: Equal(g33,g35)
    c: Coincident(g36,g11)
    c: InternalAlignment(g33,g36)
    c: InternalAlignment(g34,g36)
    c: InternalAlignment(g35,g36)
    c: InternalAlignment(g37,g36)
    c: InternalAlignment(g38,g36)
    c: Coincident(g42,g13)
    c: Weight(g39) = 1
    c: Equal(g39,g40)
    c: Equal(g39,g41)
    c: Coincident(g42,g1)
    c: InternalAlignment(g39,g42)
    c: InternalAlignment(g40,g42)
    c: InternalAlignment(g41,g42)
    c: InternalAlignment(g43,g42)
    c: InternalAlignment(g44,g42)
    c: Block(g18)
    c: Block(g24)
    c: Block(g30)
    c: Block(g36)
    c: Block(g42)
    c: Horizontal(g45)
    c: Coincident(g45,g0)
    c: Vertical(g46)
    c: Coincident(g46,g45)
    c: Coincident(g47,g46)
    c: Coincident(g47,g18)
    c: Horizontal(g47)
    c: Block(g46)
    c: Coincident(g48,g18)
    c: Horizontal(g48)
    c: Distance(g48) = 1.33
    c: Vertical(g49)
    c: Coincident(g49,g48)
    c: Coincident(g50,g49)
    c: Coincident(g50,g24)
    c: Horizontal(g50)
    c: Tangent(g50,g22)
    c: Horizontal(g51)
    c: Coincident(g51,g24)
    c: Block(g51)
    c: Vertical(g52)
    c: Block(g52)
    c: Coincident(g52,g51)
    c: Coincident(g53,g52)
    c: Coincident(g53,g30)
    c: Horizontal(g53)
    c: Distance(g1) = 8.5
FEATURE [Part::Feature] Face024
  shape: bbox 9.8 x 26.5 x 2e-07 mm, 1 faces, 0 solids (baked)
FEATURE [Part::Revolution] Revolve024
  Angle = 360
  Axis = (0,1,0)
  Base = (0,0,0)
  FaceMakerClass = Part::FaceMakerBullseye
  Placement = pos=(0,0,0) rot=(0,0,1;1.5708rad)
  Solid = false
  Source = -> Face024
  Symmetric = false
FEATURE [Part::Feature] Face025
  shape: bbox 9.8 x 26.5 x 2e-07 mm, 1 faces, 0 solids (baked)
FEATURE [Part::Revolution] Revolve025
  Angle = 360
  Axis = (0,1,0)
  Base = (0,0,0)
  FaceMakerClass = Part::FaceMakerBullseye
  Placement = pos=(0,0,0) rot=(0,0,1;1.5708rad)
  Solid = false
  Source = -> Face025
  Symmetric = false
FEATURE [Part::MultiFuse] Fusion033
  Placement = pos=(-18,19,36) rot=(0,0,1;0rad)
  Shapes = -> [Revolve025,Revolve024]
FEATURE [Part::Cylinder] Cylinder014
  Angle = 360
  AttacherType = Attacher::AttachEngine3D
  Height = 20
  Placement = pos=(0,0,36.15) rot=(0,0,1;0rad)
  Radius = 14.3
FEATURE [Part::Cylinder] Cylinder015
  Angle = 360
  AttacherType = Attacher::AttachEngine3D
  Height = 10
  Placement = pos=(0,0,36.15) rot=(0,0,1;0rad)
  Radius = 4
FEATURE [Part::MultiFuse] Fusion034  label="removeToCreteHoleForPlugHousing004"
  Placement = pos=(-42,19,36) rot=(0,1,0;1.5708rad)
  Shapes = -> [Cylinder014,Cylinder015]
FEATURE [Part::Cut] Cut008  label="top004"
  Base = -> Cut004
  Placement = pos=(-1,0,0) rot=(0,0,1;0rad)
  Tool = -> Fusion034
FEATURE [Part::Box] Box005  label="Cube005"
  AttacherType = Attacher::AttachEngine3D
  Height = 28
  Length = 3
  Placement = pos=(110.7,19,22) rot=(0,0,1;0rad)
  Width = 15.7
FEATURE [Part::Cylinder] Cylinder016
  Angle = 360
  AttacherType = Attacher::AttachEngine3D
  Height = 10
  Placement = pos=(0,0,36.15) rot=(0,0,1;0rad)
  Radius = 4
FEATURE [Part::Cylinder] Cylinder017
  Angle = 360
  AttacherType = Attacher::AttachEngine3D
  Height = 20
  Placement = pos=(0,0,36.15) rot=(0,0,1;0rad)
  Radius = 10.3
FEATURE [Part::MultiFuse] Fusion035  label="removeToCreteHoleForPlugHousing005"
  Placement = pos=(70,19,36) rot=(0,1,0;1.5708rad)
  Shapes = -> [Cylinder017,Cylinder016]
FEATURE [Part::Cut] Cut009  label="plugHousingTab001"
  Base = -> Box005
  Placement = pos=(-107.4,-14,0) rot=(0,0,1;0rad)
  Tool = -> Fusion035
FEATURE [Part::Box] Box006  label="Cube006"
  AttacherType = Attacher::AttachEngine3D
  Height = 28
  Length = 3
  Placement = pos=(110.7,19,22) rot=(0,0,1;0rad)
  Width = 15.7
FEATURE [Part::Cylinder] Cylinder018
  Angle = 360
  AttacherType = Attacher::AttachEngine3D
  Height = 10
  Placement = pos=(0,0,36.15) rot=(0,0,1;0rad)
  Radius = 4
FEATURE [Part::Cylinder] Cylinder019
  Angle = 360
  AttacherType = Attacher::AttachEngine3D
  Height = 20
  Placement = pos=(0,0,36.15) rot=(0,0,1;0rad)
  Radius = 10.3
FEATURE [Part::MultiFuse] Fusion036  label="removeToCreteHoleForPlugHousing006"
  Placement = pos=(70,19,36) rot=(0,1,0;1.5708rad)
  Shapes = -> [Cylinder019,Cylinder018]
FEATURE [Part::Cut] Cut010  label="plugHousingTab002"
  Base = -> Box006
  Placement = pos=(-107.4,-14,0) rot=(0,0,1;0rad)
  Tool = -> Fusion036
FEATURE [Part::MultiFuse] Fusion037
  Placement = pos=(9.6,23,0) rot=(0,0,1;3.14159rad)
  Shapes = -> [Cut009,Cut010]
FEATURE [Part::Box] Box  label="Cube"
  AttacherType = Attacher::AttachEngine3D
  Height = 10
  Length = 3
  Placement = pos=(3.3,4,12) rot=(0,0,1;0rad)
  Width = 10
FEATURE [Part::Fillet] Fillet004
  Base = -> Fusion028
  Edges = 1 edges r=2: [Edge25]
FEATURE [Part::Fillet] Fillet005  label="plugHousing046"
  Base = -> Fillet004
  Edges = 1 edges r=2: [Edge8]
FEATURE [Part::Fillet] Fillet006
  Base = -> Box
  Edges = 1 edges r=2: [Edge11]
FEATURE [Part::Box] Box007  label="Cube007"
  AttacherType = Attacher::AttachEngine3D
  Height = 10
  Length = 3
  Placement = pos=(3.3,4,50) rot=(0,0,1;0rad)
  Width = 10
FEATURE [Part::Fillet] Fillet007
  Base = -> Box007
  Edges = 1 edges r=2: [Edge12]
FEATURE [Part::Box] Box008  label="Cube008"
  AttacherType = Attacher::AttachEngine3D
  Height = 28
  Length = 4
  Placement = pos=(5,0,22) rot=(0,0,1;0rad)
  Width = 10
FEATURE [Part::Fillet] Fillet008
  Base = -> Box008
  Edges = 1 edges r=1: [Edge7]
FEATURE [Part::Fillet] Fillet009
  Base = -> Fillet008
  Edges = 1 edges r=2: [Edge5]
FEATURE [Part::Fillet] Fillet010
  Base = -> Fillet009
  Edges = 1 edges r=2: [Edge2]
FEATURE [Sketcher::SketchObject] Sketch009  label="topSketch003"
  FullyConstrained = true
  sketch-geometry (4):
    g0: LineSegment StartX=16.8446 StartY=31.512 StartZ=0 EndX=16.3251 EndY=34.4666 EndZ=0
    g1: ArcOfCircle CenterX=19 CenterY=19.2524 CenterZ=0 NormalX=0 NormalY=0 NormalZ=1 AngleXU=0 Radius=15.4476 StartAngle=1.74483 EndAngle=2.72717
    g2: ArcOfCircle CenterX=19 CenterY=19.2524 CenterZ=0 NormalX=0 NormalY=0 NormalZ=1 AngleXU=0 Radius=12.4476 StartAngle=1.74483 EndAngle=2.73189
    g3: LineSegment StartX=4.86004 StartY=25.4725 StartZ=0 EndX=7.58253 EndY=24.2107 EndZ=0
  constraints (7):
    c: Block(g0)
    c: Coincident(g1,g0)
    c: Coincident(g2,g0)
    c: Coincident(g3,g1)
    c: Coincident(g3,g2)
    c: Block(g1)
    c: Block(g2)
FEATURE [Part::Extrusion] Extrude008
  Base = -> Sketch009
  Dir = (0,0,1)
  DirMode = 2
  FaceMakerClass = Part::FaceMakerBullseye
  LengthFwd = 10
  LengthRev = 0
  Placement = pos=(0,0,31) rot=(0,0,1;0rad)
  Solid = true
  Symmetric = false
FEATURE [Part::Cylinder] Cylinder020
  Angle = 360
  AttacherType = Attacher::AttachEngine3D
  Height = 20
  Placement = pos=(0,0,36.15) rot=(0,0,1;0rad)
  Radius = 8.2
FEATURE [Part::Cylinder] Cylinder021
  Angle = 360
  AttacherType = Attacher::AttachEngine3D
  Height = 10
  Placement = pos=(0,0,36.15) rot=(0,0,1;0rad)
  Radius = 4
FEATURE [Part::MultiFuse] Fusion038  label="removeToCreteHoleForPlugHousing007"
  Placement = pos=(-42,19,36) rot=(0,1,0;1.5708rad)
  Shapes = -> [Cylinder020,Cylinder021]
FEATURE [Part::Cut] Cut011
  Base = -> Extrude008
  Tool = -> Fusion038
FEATURE [Part::Fillet] Fillet011
  Base = -> Cut011
  Edges = 1 edges r=2: [Edge1]
FEATURE [Part::Fillet] Fillet012
  Base = -> Fillet011
  Edges = 1 edges r=2.5: [Edge1]
FEATURE [Part::Fillet] Fillet013
  Base = -> Fillet012
  Edges = 1 edges r=2.5: [Edge2]
FEATURE [Part::Box] Box010  label="Cube010"
  AttacherType = Attacher::AttachEngine3D
  Height = 16
  Length = 8
  Placement = pos=(12.7,31.52,28) rot=(0,0,1;0rad)
  Width = 4
FEATURE [Sketcher::SketchObject] Sketch010  label="topSketch004"
  FullyConstrained = true
  sketch-geometry (4):
    g0: LineSegment StartX=16.8446 StartY=31.512 StartZ=0 EndX=16.3251 EndY=34.4666 EndZ=0
    g1: ArcOfCircle CenterX=19 CenterY=19.2524 CenterZ=0 NormalX=0 NormalY=0 NormalZ=1 AngleXU=0 Radius=15.4476 StartAngle=1.74483 EndAngle=2.72717
    g2: ArcOfCircle CenterX=19 CenterY=19.2524 CenterZ=0 NormalX=0 NormalY=0 NormalZ=1 AngleXU=0 Radius=12.4476 StartAngle=1.74483 EndAngle=2.73189
    g3: LineSegment StartX=4.86004 StartY=25.4725 StartZ=0 EndX=7.58253 EndY=24.2107 EndZ=0
  constraints (7):
    c: Block(g0)
    c: Coincident(g1,g0)
    c: Coincident(g2,g0)
    c: Coincident(g3,g1)
    c: Coincident(g3,g2)
    c: Block(g1)
    c: Block(g2)
FEATURE [Part::Cylinder] Cylinder022
  Angle = 360
  AttacherType = Attacher::AttachEngine3D
  Height = 10
  Placement = pos=(0,0,36.15) rot=(0,0,1;0rad)
  Radius = 4
FEATURE [Sketcher::SketchObject] Sketch011  label="topSketch005"
  FullyConstrained = true
  sketch-geometry (4):
    g0: LineSegment StartX=16.8446 StartY=31.512 StartZ=0 EndX=16.3251 EndY=34.4666 EndZ=0
    g1: ArcOfCircle CenterX=19 CenterY=19.2524 CenterZ=0 NormalX=0 NormalY=0 NormalZ=1 AngleXU=0 Radius=15.4476 StartAngle=1.74483 EndAngle=2.72717
    g2: ArcOfCircle CenterX=19 CenterY=19.2524 CenterZ=0 NormalX=0 NormalY=0 NormalZ=1 AngleXU=0 Radius=12.4476 StartAngle=1.74483 EndAngle=2.73189
    g3: LineSegment StartX=4.86004 StartY=25.4725 StartZ=0 EndX=7.58253 EndY=24.2107 EndZ=0
  constraints (7):
    c: Block(g0)
    c: Coincident(g1,g0)
    c: Coincident(g2,g0)
    c: Coincident(g3,g1)
    c: Coincident(g3,g2)
    c: Block(g1)
    c: Block(g2)
FEATURE [Part::Extrusion] Extrude010
  Base = -> Sketch011
  Dir = (0,0,1)
  DirMode = 2
  FaceMakerClass = Part::FaceMakerBullseye
  LengthFwd = 10.6
  LengthRev = 0
  Placement = pos=(0,0,31) rot=(0,0,1;0rad)
  Solid = true
  Symmetric = false
FEATURE [Part::Cylinder] Cylinder023
  Angle = 360
  AttacherType = Attacher::AttachEngine3D
  Height = 20
  Placement = pos=(0,0,36.15) rot=(0,0,1;0rad)
  Radius = 8.2
FEATURE [Part::MultiFuse] Fusion039  label="removeToCreteHoleForPlugHousing008"
  Placement = pos=(-42,19,36) rot=(0,1,0;1.5708rad)
  Shapes = -> [Cylinder023,Cylinder022]
FEATURE [Part::Cut] Cut012
  Base = -> Extrude010
  Placement = pos=(0,0,-0.3) rot=(0,0,1;0rad)
  Tool = -> Fusion039
FEATURE [Part::Cut] Cut013
  Base = -> Box010
  Tool = -> Cut012
FEATURE [Part::Fillet] Fillet014
  Base = -> Cut013
  Edges = 1 edges r=0.7: [Edge13]
FEATURE [Part::Fillet] Fillet015
  Base = -> Fillet014
  Edges = 1 edges r=0.7: [Edge13]
FEATURE [Part::Fillet] Fillet016
  Base = -> Fillet015
  Edges = 1 edges r=0.7: [Edge16]
FEATURE [Part::Fillet] Fillet017
  Base = -> Fillet016
  Edges = 1 edges r=0.7: [Edge11]
FEATURE [Part::Fillet] Fillet018
  Base = -> Fillet017
  Edges = 1 edges r=0.7: [Edge10]
FEATURE [Part::Fillet] Fillet019
  Base = -> Fillet018
  Edges = 1 edges r=1.2: [Edge5]
FEATURE [Part::Fillet] Fillet020
  Base = -> Fillet019
  Edges = 1 edges r=1.2: [Edge12]
FEATURE [Part::Fillet] Fillet021
  Base = -> Fillet020
  Edges = 1 edges r=2: [Edge1]
  Placement = pos=(0.3,0,0) rot=(0,0,1;0rad)
FEATURE [Part::MultiFuse] Fusion040  label="top005"
  Shapes = -> [Cut008,Fillet021]
FEATURE [Part::MultiFuse] Fusion041  label="wireHolder"
  Shapes = -> [Fusion033,Fillet013]
FEATURE [Part::MultiFuse] Fusion042
  Shapes = -> [Fillet007,Fusion041]
FEATURE [Part::MultiFuse] Fusion043  label="wireHolder001"
  Shapes = -> [Fusion042,Fillet010]
FEATURE [Part::MultiFuse] Fusion044  label="wireHolder002"
  Shapes = -> [Fillet006,Fusion037,Fusion043]
FEATURE [Part::Feature] Face026
  shape: bbox 11 x 6 x 2e-07 mm, 1 faces, 0 solids (baked)
FEATURE [Part::Revolution] Revolve026
  Angle = 360
  Axis = (0,1,0)
  Base = (0,0,0)
  FaceMakerClass = Part::FaceMakerBullseye
  Placement = pos=(30.3,-1,19.7) rot=(0,0,1;0rad)
  Solid = false
  Source = -> Face026
  Symmetric = false
FEATURE [Sketcher::SketchObject] Sketch013  label="topSketch006"
  FullyConstrained = true
  sketch-geometry (13):
    g0: LineSegment StartX=117 StartY=19 StartZ=0 EndX=117 EndY=38 EndZ=0
    g1: ArcOfCircle CenterX=98 CenterY=19 CenterZ=0 NormalX=0 NormalY=0 NormalZ=1 AngleXU=0 Radius=19 StartAngle=5.7297 EndAngle=6.28319
    g2: LineSegment StartX=0 StartY=3 StartZ=0 EndX=0 EndY=19 EndZ=0
    g3: LineSegment StartX=19 StartY=38 StartZ=0 EndX=117 EndY=38 EndZ=0
    g4: ArcOfCircle CenterX=19 CenterY=19 CenterZ=0 NormalX=0 NormalY=0 NormalZ=1 AngleXU=0 Radius=19 StartAngle=1.5708 EndAngle=3.14159
    g5: ArcOfCircle CenterX=19 CenterY=19 CenterZ=0 NormalX=0 NormalY=0 NormalZ=1 AngleXU=0 Radius=16 StartAngle=1.5708 EndAngle=3.14159
    g6: ArcOfCircle CenterX=98 CenterY=19 CenterZ=0 NormalX=0 NormalY=0 NormalZ=1 AngleXU=0 Radius=16 StartAngle=5.60905 EndAngle=6.28319
    g7: LineSegment StartX=114 StartY=19 StartZ=0 EndX=114 EndY=35 EndZ=0
    g8: LineSegment StartX=110.5 StartY=9.01251 StartZ=0 EndX=114.163 EndY=9.01251 EndZ=0
    g9: LineSegment StartX=114 StartY=35 StartZ=0 EndX=19 EndY=35 EndZ=0
    g10: LineSegment StartX=0 StartY=3 StartZ=0 EndX=0 EndY=0 EndZ=0
    g11: LineSegment StartX=3 StartY=0 StartZ=0 EndX=0 EndY=0 EndZ=0
    g12: LineSegment StartX=3 StartY=19 StartZ=0 EndX=3 EndY=0 EndZ=0
  constraints (33):
    c: Vertical(g0)
    c: Distance(g0) = 19
    c: Block(g0)
    c: Coincident(g1,g0)
    c: Block(g1)
    c: Vertical(g2)
    c: Block(g2)
    c: Coincident(g3,g0)
    c: Horizontal(g3)
    c: Distance(g3) = 98
    c: Coincident(g4,g3)
    c: Coincident(g4,g2)
    c: Block(g4)
    c: Coincident(g5,g4)
    c: Coincident(g6,g1)
    c: Block(g6)
    c: Block(g5)
    c: Coincident(g7,g6)
    c: Vertical(g7)
    c: Coincident(g8,g6)
    c: Coincident(g8,g1)
    c: Coincident(g9,g7)
    c: Coincident(g9,g5)
    c: Horizontal(g9)
    c: Tangent(g9,g5)
    c: Coincident(g10,g2)
    c: Distance(g10) = 3
    c: Vertical(g10)
    c: Coincident(g11,g10)
    c: Horizontal(g11)
    c: Coincident(g12,g5)
    c: Coincident(g12,g11)
    c: Vertical(g12)
FEATURE [Part::Extrusion] Extrude011  label="top006"
  Base = -> Sketch013
  Dir = (0,0,1)
  DirMode = 2
  FaceMakerClass = Part::FaceMakerBullseye
  LengthFwd = 72
  LengthRev = 0
  Solid = true
  Symmetric = false
FEATURE [Sketcher::SketchObject] Sketch014
  FullyConstrained = true
  MapMode = 3
  Placement = pos=(0,0,0) rot=(1,0,0;1.5708rad)
  Support = -> [Extrude011]
  sketch-geometry (8):
    g0: Circle CenterX=80.351 CenterY=-67.6202 CenterZ=0 NormalX=0 NormalY=0 NormalZ=1 AngleXU=0 Radius=2
    g1: Circle CenterX=80.351 CenterY=-67.6202 CenterZ=0 NormalX=0 NormalY=0 NormalZ=1 AngleXU=0 Radius=3
    g2: Circle CenterX=80.351 CenterY=-4.92017 CenterZ=0 NormalX=0 NormalY=0 NormalZ=1 AngleXU=0 Radius=2
    g3: Circle CenterX=80.351 CenterY=-4.92017 CenterZ=0 NormalX=0 NormalY=0 NormalZ=1 AngleXU=0 Radius=3
    g4: Circle CenterX=23.851 CenterY=-4.92017 CenterZ=0 NormalX=0 NormalY=0 NormalZ=1 AngleXU=0 Radius=2
    g5: Circle CenterX=23.851 CenterY=-4.92017 CenterZ=0 NormalX=0 NormalY=0 NormalZ=1 AngleXU=0 Radius=3
    g6: Circle CenterX=23.851 CenterY=-67.6202 CenterZ=0 NormalX=0 NormalY=0 NormalZ=1 AngleXU=0 Radius=2
    g7: Circle CenterX=23.851 CenterY=-67.6202 CenterZ=0 NormalX=0 NormalY=0 NormalZ=1 AngleXU=0 Radius=3
  constraints (8):
    c: Block(g3)
    c: Block(g2)
    c: Block(g1)
    c: Block(g0)
    c: Block(g6)
    c: Block(g7)
    c: Block(g4)
    c: Block(g5)
FEATURE [Part::Feature] Face027
  shape: bbox 11 x 6 x 2e-07 mm, 1 faces, 0 solids (baked)
FEATURE [Part::Revolution] Revolve027
  Angle = 360
  Axis = (0,1,0)
  Base = (0,0,0)
  FaceMakerClass = Part::FaceMakerBullseye
  Placement = pos=(30.3,-1,51.7) rot=(0,0,1;0rad)
  Solid = false
  Source = -> Face027
  Symmetric = false
FEATURE [Part::Feature] Face028
  shape: bbox 11 x 6 x 2e-07 mm, 1 faces, 0 solids (baked)
FEATURE [Part::Revolution] Revolve028
  Angle = 360
  Axis = (0,1,0)
  Base = (0,0,0)
  FaceMakerClass = Part::FaceMakerBullseye
  Placement = pos=(62.3,-1,19.7) rot=(0,0,1;0rad)
  Solid = false
  Source = -> Face028
  Symmetric = false
FEATURE [Part::Feature] Face029
  shape: bbox 11 x 6 x 2e-07 mm, 1 faces, 0 solids (baked)
FEATURE [Part::Revolution] Revolve029
  Angle = 360
  Axis = (0,1,0)
  Base = (0,0,0)
  FaceMakerClass = Part::FaceMakerBullseye
  Placement = pos=(62.3,-1,51.7) rot=(0,0,1;0rad)
  Solid = false
  Source = -> Face029
  Symmetric = false
FEATURE [Part::Feature] Wire
  shape: bbox 11 x 5.2 x 2e-07 mm, 0 faces, 0 solids (baked)
FEATURE [Part::Revolution] Revolve030
  Angle = 360
  Axis = (0,1,0)
  Base = (0,0,0)
  FaceMakerClass = Part::FaceMakerBullseye
  Placement = pos=(30.3,38,19.7) rot=(0,0,1;0rad)
  Solid = true
  Source = -> Wire
  Symmetric = false
FEATURE [Part::Feature] Wire001
  shape: bbox 11 x 5.2 x 2e-07 mm, 0 faces, 0 solids (baked)
FEATURE [Part::Revolution] Revolve031
  Angle = 360
  Axis = (0,1,0)
  Base = (0,0,0)
  FaceMakerClass = Part::FaceMakerBullseye
  Placement = pos=(30.3,38,51.7) rot=(0,0,1;0rad)
  Solid = true
  Source = -> Wire001
  Symmetric = false
FEATURE [Part::Feature] Wire002
  shape: bbox 11 x 5.2 x 2e-07 mm, 0 faces, 0 solids (baked)
FEATURE [Part::Revolution] Revolve032
  Angle = 360
  Axis = (0,1,0)
  Base = (0,0,0)
  FaceMakerClass = Part::FaceMakerBullseye
  Placement = pos=(62.3,38,51.7) rot=(0,0,1;0rad)
  Solid = true
  Source = -> Wire002
  Symmetric = false
FEATURE [Part::Feature] Wire003
  shape: bbox 11 x 5.2 x 2e-07 mm, 0 faces, 0 solids (baked)
FEATURE [Part::Revolution] Revolve033
  Angle = 360
  Axis = (0,1,0)
  Base = (0,0,0)
  FaceMakerClass = Part::FaceMakerBullseye
  Placement = pos=(62.3,38,19.7) rot=(0,0,1;0rad)
  Solid = true
  Source = -> Wire003
  Symmetric = false
FEATURE [Part::MultiFuse] Fusion045  label="altRandScrewHousing"
  Shapes = -> [Revolve029,Revolve027,Revolve028,Revolve026]
FEATURE [Part::MultiFuse] Fusion046  label="fanScrewHousing"
  Shapes = -> [Revolve033,Revolve032,Revolve031,Revolve030]
FEATURE [Sketcher::SketchObject] Sketch015
  FullyConstrained = true
  sketch-geometry (17):
    g0: Circle CenterX=-3.5 CenterY=23.5 CenterZ=0 NormalX=0 NormalY=0 NormalZ=1 AngleXU=0 Radius=1
    g1: Circle CenterX=-1 CenterY=15.25 CenterZ=0 NormalX=0 NormalY=0 NormalZ=1 AngleXU=0 Radius=1
    g2: Circle CenterX=-3.5 CenterY=7 CenterZ=0 NormalX=0 NormalY=0 NormalZ=1 AngleXU=0 Radius=1
    g3: BSplineCurve PolesCount=3 KnotsCount=2 Degree=2 IsPeriodic=0
    g4: GeomPoint X=-3.5 Y=23.5 Z=0
    g5: GeomPoint X=-3.5 Y=7 Z=0
    g6: Circle CenterX=-4.8 CenterY=30.5 CenterZ=0 NormalX=0 NormalY=0 NormalZ=1 AngleXU=0 Radius=1
    g7: Circle CenterX=-3.5 CenterY=30.5 CenterZ=0 NormalX=0 NormalY=0 NormalZ=1 AngleXU=0 Radius=1
    g8: Circle CenterX=-3.5 CenterY=29.2 CenterZ=0 NormalX=0 NormalY=0 NormalZ=1 AngleXU=0 Radius=1
    g9: BSplineCurve PolesCount=3 KnotsCount=2 Degree=2 IsPeriodic=0
    g10: GeomPoint X=-4.8 Y=30.5 Z=0
    g11: GeomPoint X=-3.5 Y=29.2 Z=0
    g12: LineSegment StartX=-3.5 StartY=29.2 StartZ=0 EndX=-3.5 EndY=23.5 EndZ=0
    g13: LineSegment StartX=-4.8 StartY=30.5 StartZ=0 EndX=0 EndY=30.5 EndZ=0
    g14: LineSegment StartX=-3.5 StartY=0.3 StartZ=0 EndX=0 EndY=0.3 EndZ=0
    g15: LineSegment StartX=-3.5 StartY=0.3 StartZ=0 EndX=-3.5 EndY=7 EndZ=0
    g16: LineSegment StartX=0 StartY=0.3 StartZ=0 EndX=0 EndY=30.5 EndZ=0
  constraints (33):
    c: Weight(g0) = 1
    c: Equal(g0,g1)
    c: Equal(g0,g2)
    c: InternalAlignment(g0,g3)
    c: InternalAlignment(g1,g3)
    c: InternalAlignment(g2,g3)
    c: InternalAlignment(g4,g3)
    c: InternalAlignment(g5,g3)
    c: Block(g3)
    c: Weight(g6) = 1
    c: Equal(g6,g7)
    c: Equal(g6,g8)
    c: InternalAlignment(g6,g9)
    c: InternalAlignment(g7,g9)
    c: InternalAlignment(g8,g9)
    c: InternalAlignment(g10,g9)
    c: InternalAlignment(g11,g9)
    c: Block(g9)
    c: Coincident(g12,g9)
    c: Coincident(g12,g3)
    c: Vertical(g12)
    c: Coincident(g13,g9)
    c: Horizontal(g13)
    c: Distance(g13) = 4.8
    c: Horizontal(g14)
    c: Block(g14)
    c: Coincident(g15,g14)
    c: Coincident(g15,g3)
    c: Vertical(g15)
    c: Coincident(g16,g14)
    c: Coincident(g16,g13)
    c: Vertical(g16)
    c: Tangent(g16,g1)
FEATURE [Sketcher::SketchObject] Sketch016
  FullyConstrained = true
  sketch-geometry (16):
    g0: Circle CenterX=-3.5 CenterY=23.5 CenterZ=0 NormalX=0 NormalY=0 NormalZ=1 AngleXU=0 Radius=1
    g1: Circle CenterX=-1 CenterY=15.25 CenterZ=0 NormalX=0 NormalY=0 NormalZ=1 AngleXU=0 Radius=1
    g2: Circle CenterX=-3.5 CenterY=7 CenterZ=0 NormalX=0 NormalY=0 NormalZ=1 AngleXU=0 Radius=1
    g3: BSplineCurve PolesCount=3 KnotsCount=2 Degree=2 IsPeriodic=0
    g4: GeomPoint X=-3.5 Y=23.5 Z=0
    g5: GeomPoint X=-3.5 Y=7 Z=0
    g6: LineSegment StartX=-3.5 StartY=28.2 StartZ=0 EndX=-3.5 EndY=23.5 EndZ=0
    g7: LineSegment StartX=0 StartY=29.5 StartZ=0 EndX=0 EndY=30 EndZ=0
    g8: LineSegment StartX=-3.5 StartY=28.2 StartZ=0 EndX=-3.5 EndY=30 EndZ=0
    g9: LineSegment StartX=0 StartY=30 StartZ=0 EndX=0 EndY=30.5 EndZ=0
    g10: LineSegment StartX=0 StartY=30.5 StartZ=0 EndX=-3.5 EndY=30.5 EndZ=0
    g11: LineSegment StartX=-3.5 StartY=30.5 StartZ=0 EndX=-3.5 EndY=30 EndZ=0
    g12: LineSegment StartX=0 StartY=29.5 StartZ=0 EndX=0 EndY=5 EndZ=0
    g13: LineSegment StartX=-3.5 StartY=0.3 StartZ=0 EndX=-3.5 EndY=7 EndZ=0
    g14: LineSegment StartX=-3.5 StartY=0.3 StartZ=0 EndX=0 EndY=0.3 EndZ=0
    g15: LineSegment StartX=0 StartY=5 StartZ=0 EndX=0 EndY=0.3 EndZ=0
  constraints (39):
    c: Weight(g0) = 1
    c: Equal(g0,g1)
    c: Equal(g0,g2)
    c: InternalAlignment(g0,g3)
    c: InternalAlignment(g1,g3)
    c: InternalAlignment(g2,g3)
    c: InternalAlignment(g4,g3)
    c: InternalAlignment(g5,g3)
    c: Block(g3)
    c: Coincident(g6,g3)
    c: Vertical(g6)
    c: Vertical(g7)
    c: Distance(g7) = 0.5
    c: Coincident(g8,g6)
    c: Vertical(g8)
    c: Block(g6)
    c: Block(g7)
    c: Vertical(g9)
    c: Equal(g7,g9) = 0.5
    c: Block(g9)
    c: Coincident(g9,g7)
    c: Horizontal(g10)
    c: Coincident(g10,g9)
    c: Coincident(g11,g10)
    c: Coincident(g11,g8)
    c: Vertical(g11)
    c: Block(g11)
    c: Coincident(g12,g7)
    c: Vertical(g12)
    c: Coincident(g13,g3)
    c: Vertical(g13)
    c: Distance(g13) = 6.7
    c: Coincident(g14,g13)
    c: Horizontal(g14)
    c: Block(g14)
    c: Coincident(g15,g12)
    c: Coincident(g15,g14)
    c: Vertical(g15)
    c: Block(g15)
FEATURE [Sketcher::SketchObject] Sketch017
  FullyConstrained = true
  sketch-geometry (11):
    g0: LineSegment StartX=-3.5 StartY=1e-16 StartZ=0 EndX=-1.6 EndY=1e-16 EndZ=0
    g1: LineSegment StartX=-1.6 StartY=1e-16 StartZ=0 EndX=-1.6 EndY=1.5 EndZ=0
    g2: LineSegment StartX=-3.5 StartY=1.5 StartZ=0 EndX=-1.6 EndY=1.5 EndZ=0
    g3: LineSegment StartX=-3.5 StartY=1e-16 StartZ=0 EndX=-4.8 EndY=1e-16 EndZ=0
    g4: Circle CenterX=-3.5 CenterY=1.3 CenterZ=0 NormalX=0 NormalY=0 NormalZ=1 AngleXU=0 Radius=1
    g5: Circle CenterX=-3.5 CenterY=1e-16 CenterZ=0 NormalX=0 NormalY=0 NormalZ=1 AngleXU=0 Radius=1
    g6: Circle CenterX=-4.8 CenterY=1e-16 CenterZ=0 NormalX=0 NormalY=0 NormalZ=1 AngleXU=0 Radius=1
    g7: BSplineCurve PolesCount=3 KnotsCount=2 Degree=2 IsPeriodic=0
    g8: GeomPoint X=-3.5 Y=1.3 Z=0
    g9: GeomPoint X=-4.8 Y=1e-16 Z=0
    g10: LineSegment StartX=-3.5 StartY=1.3 StartZ=0 EndX=-3.5 EndY=1.5 EndZ=0
  constraints (24):
    c: Horizontal(g0)
    c: Distance(g0) = 1.9
    c: Block(g0)
    c: Coincident(g1,g0)
    c: Vertical(g1)
    c: Coincident(g2,g1)
    c: Horizontal(g2)
    c: Coincident(g3,g0)
    c: Horizontal(g3)
    c: Distance(g3) = 1.3
    c: Weight(g4) = 1
    c: Equal(g4,g5)
    c: Coincident(g5,g0)
    c: Equal(g4,g6)
    c: Coincident(g7,g3)
    c: InternalAlignment(g4,g7)
    c: InternalAlignment(g5,g7)
    c: InternalAlignment(g6,g7)
    c: InternalAlignment(g8,g7)
    c: InternalAlignment(g9,g7)
    c: Coincident(g10,g7)
    c: Coincident(g10,g2)
    c: Vertical(g10)
    c: Block(g10)
FEATURE [Part::Feature] Face035
  shape: bbox 3.2 x 1.5 x 2e-07 mm, 1 faces, 0 solids (baked)
FEATURE [Part::Revolution] Revolve039  label="backCaseScrewRetainer"
  Angle = 360
  Axis = (0,1,0)
  Base = (0,0,0)
  FaceMakerClass = Part::FaceMakerBullseye
  Placement = pos=(12.5,3,62) rot=(0,0,1;0rad)
  Solid = false
  Source = -> Face035
  Symmetric = false
FEATURE [Part::Feature] Face036
  shape: bbox 3.2 x 1.5 x 2e-07 mm, 1 faces, 0 solids (baked)
FEATURE [Part::Feature] Face039
  shape: bbox 4.8 x 30.2 x 2e-07 mm, 1 faces, 0 solids (baked)
FEATURE [Part::Revolution] Revolve043  label="frontCaseScrewPost002"
  Angle = 360
  Axis = (0,1,0)
  Base = (0,0,0)
  FaceMakerClass = Part::FaceMakerBullseye
  Placement = pos=(89.5,4.5,3.5) rot=(0,0,1;0rad)
  Solid = false
  Source = -> Face039
  Symmetric = false
FEATURE [Part::Feature] Face042
  shape: bbox 4.8 x 30.2 x 2e-07 mm, 1 faces, 0 solids (baked)
FEATURE [Part::Revolution] Revolve046  label="frontCaseScrewPost003"
  Angle = 360
  Axis = (0,1,0)
  Base = (0,0,0)
  FaceMakerClass = Part::FaceMakerBullseye
  Placement = pos=(89.5,4.5,68.5) rot=(0,0,1;0rad)
  Solid = false
  Source = -> Face042
  Symmetric = false
FEATURE [Part::Feature] Face043
  shape: bbox 3.2 x 1.5 x 2e-07 mm, 1 faces, 0 solids (baked)
FEATURE [Part::Revolution] Revolve047  label="frontCaseScrewRetainer002"
  Angle = 360
  Axis = (0,1,0)
  Base = (0,0,0)
  FaceMakerClass = Part::FaceMakerBullseye
  Placement = pos=(89.5,3,68.5) rot=(0,0,1;0rad)
  Solid = false
  Source = -> Face043
  Symmetric = false
FEATURE [Part::Feature] Face044
  shape: bbox 3.2 x 1.5 x 2e-07 mm, 1 faces, 0 solids (baked)
FEATURE [Part::Revolution] Revolve048  label="frontCaseScrewRetainer003"
  Angle = 360
  Axis = (0,1,0)
  Base = (0,0,0)
  FaceMakerClass = Part::FaceMakerBullseye
  Placement = pos=(89.5,3,3.5) rot=(0,0,1;0rad)
  Solid = false
  Source = -> Face044
  Symmetric = false
FEATURE [App::MeasureDistance] Distance002  label="Distance: 1.67 mm"
  Distance = 1.66921
  P1 = (99.2361,4.7524,71.7)
  P2 = (99.2347,6.42161,71.7)
FEATURE [Sketcher::SketchObject] Sketch018
  FullyConstrained = true
  sketch-geometry (7):
    g0: LineSegment StartX=0 StartY=0 StartZ=0 EndX=0 EndY=6 EndZ=0
    g1: Circle CenterX=0 CenterY=0 CenterZ=0 NormalX=0 NormalY=0 NormalZ=1 AngleXU=0 Radius=1
    g2: Circle CenterX=8 CenterY=6 CenterZ=0 NormalX=0 NormalY=0 NormalZ=1 AngleXU=0 Radius=1
    g3: BSplineCurve PolesCount=3 KnotsCount=2 Degree=2 IsPeriodic=0
    g4: GeomPoint X=0 Y=0 Z=0
    g5: GeomPoint X=8 Y=6 Z=0
    g6: LineSegment StartX=0 StartY=6 StartZ=0 EndX=8 EndY=6 EndZ=0
  constraints (14):
    c: Coincident(g0,g-1)
    c: Distance(g0) = 6
    c: Vertical(g0)
    c: Coincident(g3,g0)
    c: Weight(g1) = 1
    c: Equal(g1,g2)
    c: InternalAlignment(g1,g3)
    c: InternalAlignment(g2,g3)
    c: InternalAlignment(g4,g3)
    c: InternalAlignment(g5,g3)
    c: Block(g3)
    c: Coincident(g6,g0)
    c: Coincident(g6,g3)
    c: Horizontal(g6)
FEATURE [Part::Extrusion] Extrude012  label="caseScrewPillarBracket"
  Base = -> Sketch018
  Dir = (0,0,1)
  DirMode = 2
  FaceMakerClass = Part::FaceMakerBullseye
  LengthFwd = 2.4
  LengthRev = 0
  Placement = pos=(15.76,29,8.8) rot=(0,1,0;0rad)
  Solid = true
  Symmetric = false
FEATURE [Sketcher::SketchObject] Sketch019
  FullyConstrained = true
  sketch-geometry (7):
    g0: LineSegment StartX=0 StartY=0 StartZ=0 EndX=0 EndY=6 EndZ=0
    g1: Circle CenterX=0 CenterY=0 CenterZ=0 NormalX=0 NormalY=0 NormalZ=1 AngleXU=0 Radius=1
    g2: Circle CenterX=8 CenterY=6 CenterZ=0 NormalX=0 NormalY=0 NormalZ=1 AngleXU=0 Radius=1
    g3: BSplineCurve PolesCount=3 KnotsCount=2 Degree=2 IsPeriodic=0
    g4: GeomPoint X=0 Y=0 Z=0
    g5: GeomPoint X=8 Y=6 Z=0
    g6: LineSegment StartX=0 StartY=6 StartZ=0 EndX=8 EndY=6 EndZ=0
  constraints (14):
    c: Coincident(g0,g-1)
    c: Distance(g0) = 6
    c: Vertical(g0)
    c: Coincident(g3,g0)
    c: Weight(g1) = 1
    c: Equal(g1,g2)
    c: InternalAlignment(g1,g3)
    c: InternalAlignment(g2,g3)
    c: InternalAlignment(g4,g3)
    c: InternalAlignment(g5,g3)
    c: Block(g3)
    c: Coincident(g6,g0)
    c: Coincident(g6,g3)
    c: Horizontal(g6)
FEATURE [Part::Extrusion] Extrude013  label="caseScrewPillarBracket001"
  Base = -> Sketch019
  Dir = (0,0,1)
  DirMode = 2
  FaceMakerClass = Part::FaceMakerBullseye
  LengthFwd = 2.4
  LengthRev = 0
  Placement = pos=(15.76,29,60.8) rot=(0,0,1;0rad)
  Solid = true
  Symmetric = false
FEATURE [Sketcher::SketchObject] Sketch020
  FullyConstrained = true
  sketch-geometry (7):
    g0: LineSegment StartX=0 StartY=0 StartZ=0 EndX=0 EndY=6 EndZ=0
    g1: Circle CenterX=0 CenterY=0 CenterZ=0 NormalX=0 NormalY=0 NormalZ=1 AngleXU=0 Radius=1
    g2: Circle CenterX=8 CenterY=6 CenterZ=0 NormalX=0 NormalY=0 NormalZ=1 AngleXU=0 Radius=1
    g3: BSplineCurve PolesCount=3 KnotsCount=2 Degree=2 IsPeriodic=0
    g4: GeomPoint X=0 Y=0 Z=0
    g5: GeomPoint X=8 Y=6 Z=0
    g6: LineSegment StartX=0 StartY=6 StartZ=0 EndX=8 EndY=6 EndZ=0
  constraints (14):
    c: Coincident(g0,g-1)
    c: Distance(g0) = 6
    c: Vertical(g0)
    c: Coincident(g3,g0)
    c: Weight(g1) = 1
    c: Equal(g1,g2)
    c: InternalAlignment(g1,g3)
    c: InternalAlignment(g2,g3)
    c: InternalAlignment(g4,g3)
    c: InternalAlignment(g5,g3)
    c: Block(g3)
    c: Coincident(g6,g0)
    c: Coincident(g6,g3)
    c: Horizontal(g6)
FEATURE [Part::Extrusion] Extrude014  label="caseScrewPillarBracket002"
  Base = -> Sketch020
  Dir = (0,0,1)
  DirMode = 2
  FaceMakerClass = Part::FaceMakerBullseye
  LengthFwd = 2.4
  LengthRev = 0
  Placement = pos=(13.7,29,13.26) rot=(0,-1,0;1.5708rad)
  Solid = true
  Symmetric = false
FEATURE [Sketcher::SketchObject] Sketch021
  FullyConstrained = true
  sketch-geometry (7):
    g0: LineSegment StartX=0 StartY=0 StartZ=0 EndX=0 EndY=6 EndZ=0
    g1: Circle CenterX=0 CenterY=0 CenterZ=0 NormalX=0 NormalY=0 NormalZ=1 AngleXU=0 Radius=1
    g2: Circle CenterX=8 CenterY=6 CenterZ=0 NormalX=0 NormalY=0 NormalZ=1 AngleXU=0 Radius=1
    g3: BSplineCurve PolesCount=3 KnotsCount=2 Degree=2 IsPeriodic=0
    g4: GeomPoint X=0 Y=0 Z=0
    g5: GeomPoint X=8 Y=6 Z=0
    g6: LineSegment StartX=0 StartY=6 StartZ=0 EndX=8 EndY=6 EndZ=0
  constraints (14):
    c: Coincident(g0,g-1)
    c: Distance(g0) = 6
    c: Vertical(g0)
    c: Coincident(g3,g0)
    c: Weight(g1) = 1
    c: Equal(g1,g2)
    c: InternalAlignment(g1,g3)
    c: InternalAlignment(g2,g3)
    c: InternalAlignment(g4,g3)
    c: InternalAlignment(g5,g3)
    c: Block(g3)
    c: Coincident(g6,g0)
    c: Coincident(g6,g3)
    c: Horizontal(g6)
FEATURE [Part::Extrusion] Extrude015  label="caseScrewPillarBracket003"
  Base = -> Sketch021
  Dir = (0,0,1)
  DirMode = 2
  FaceMakerClass = Part::FaceMakerBullseye
  LengthFwd = 2.4
  LengthRev = 0
  Placement = pos=(11.3,29,58.74) rot=(0,1,0;1.5708rad)
  Solid = true
  Symmetric = false
FEATURE [Sketcher::SketchObject] Sketch022
  FullyConstrained = true
  sketch-geometry (7):
    g0: LineSegment StartX=0 StartY=0 StartZ=0 EndX=0 EndY=6 EndZ=0
    g1: Circle CenterX=0 CenterY=0 CenterZ=0 NormalX=0 NormalY=0 NormalZ=1 AngleXU=0 Radius=1
    g2: Circle CenterX=8 CenterY=6 CenterZ=0 NormalX=0 NormalY=0 NormalZ=1 AngleXU=0 Radius=1
    g3: BSplineCurve PolesCount=3 KnotsCount=2 Degree=2 IsPeriodic=0
    g4: GeomPoint X=0 Y=0 Z=0
    g5: GeomPoint X=8 Y=6 Z=0
    g6: LineSegment StartX=0 StartY=6 StartZ=0 EndX=8 EndY=6 EndZ=0
  constraints (14):
    c: Coincident(g0,g-1)
    c: Distance(g0) = 6
    c: Vertical(g0)
    c: Coincident(g3,g0)
    c: Weight(g1) = 1
    c: Equal(g1,g2)
    c: InternalAlignment(g1,g3)
    c: InternalAlignment(g2,g3)
    c: InternalAlignment(g4,g3)
    c: InternalAlignment(g5,g3)
    c: Block(g3)
    c: Coincident(g6,g0)
    c: Coincident(g6,g3)
    c: Horizontal(g6)
FEATURE [Part::Extrusion] Extrude016  label="caseScrewPillarBracket004"
  Base = -> Sketch022
  Dir = (0,0,1)
  DirMode = 2
  FaceMakerClass = Part::FaceMakerBullseye
  LengthFwd = 2.4
  LengthRev = 0
  Placement = pos=(88.3,29,65.23) rot=(0,1,0;1.5708rad)
  Solid = true
  Symmetric = false
FEATURE [Sketcher::SketchObject] Sketch023
  FullyConstrained = true
  sketch-geometry (7):
    g0: LineSegment StartX=0 StartY=0 StartZ=0 EndX=0 EndY=6 EndZ=0
    g1: Circle CenterX=0 CenterY=0 CenterZ=0 NormalX=0 NormalY=0 NormalZ=1 AngleXU=0 Radius=1
    g2: Circle CenterX=8 CenterY=6 CenterZ=0 NormalX=0 NormalY=0 NormalZ=1 AngleXU=0 Radius=1
    g3: BSplineCurve PolesCount=3 KnotsCount=2 Degree=2 IsPeriodic=0
    g4: GeomPoint X=0 Y=0 Z=0
    g5: GeomPoint X=8 Y=6 Z=0
    g6: LineSegment StartX=0 StartY=6 StartZ=0 EndX=8 EndY=6 EndZ=0
  constraints (14):
    c: Coincident(g0,g-1)
    c: Distance(g0) = 6
    c: Vertical(g0)
    c: Coincident(g3,g0)
    c: Weight(g1) = 1
    c: Equal(g1,g2)
    c: InternalAlignment(g1,g3)
    c: InternalAlignment(g2,g3)
    c: InternalAlignment(g4,g3)
    c: InternalAlignment(g5,g3)
    c: Block(g3)
    c: Coincident(g6,g0)
    c: Coincident(g6,g3)
    c: Horizontal(g6)
FEATURE [Part::Extrusion] Extrude017  label="caseScrewPillarBracket005"
  Base = -> Sketch023
  Dir = (0,0,1)
  DirMode = 2
  FaceMakerClass = Part::FaceMakerBullseye
  LengthFwd = 2.4
  LengthRev = 0
  Placement = pos=(90.7,29,6.77) rot=(0,-1,0;1.5708rad)
  Solid = true
  Symmetric = false
FEATURE [Sketcher::SketchObject] Sketch024
  FullyConstrained = true
  sketch-geometry (7):
    g0: LineSegment StartX=0 StartY=0 StartZ=0 EndX=0 EndY=6 EndZ=0
    g1: Circle CenterX=0 CenterY=0 CenterZ=0 NormalX=0 NormalY=0 NormalZ=1 AngleXU=0 Radius=1
    g2: Circle CenterX=8 CenterY=6 CenterZ=0 NormalX=0 NormalY=0 NormalZ=1 AngleXU=0 Radius=1
    g3: BSplineCurve PolesCount=3 KnotsCount=2 Degree=2 IsPeriodic=0
    g4: GeomPoint X=0 Y=0 Z=0
    g5: GeomPoint X=8 Y=6 Z=0
    g6: LineSegment StartX=0 StartY=6 StartZ=0 EndX=8 EndY=6 EndZ=0
  constraints (14):
    c: Coincident(g0,g-1)
    c: Distance(g0) = 6
    c: Vertical(g0)
    c: Coincident(g3,g0)
    c: Weight(g1) = 1
    c: Equal(g1,g2)
    c: InternalAlignment(g1,g3)
    c: InternalAlignment(g2,g3)
    c: InternalAlignment(g4,g3)
    c: InternalAlignment(g5,g3)
    c: Block(g3)
    c: Coincident(g6,g0)
    c: Coincident(g6,g3)
    c: Horizontal(g6)
FEATURE [Part::Extrusion] Extrude018  label="caseScrewPillarBracket006"
  Base = -> Sketch024
  Dir = (0,0,1)
  DirMode = 2
  FaceMakerClass = Part::FaceMakerBullseye
  LengthFwd = 2.4
  LengthRev = 0
  Placement = pos=(103.7,29,6.77) rot=(0,-1,0;1.5708rad)
  Solid = true
  Symmetric = false
FEATURE [Sketcher::SketchObject] Sketch025
  FullyConstrained = true
  sketch-geometry (7):
    g0: LineSegment StartX=0 StartY=0 StartZ=0 EndX=0 EndY=6 EndZ=0
    g1: Circle CenterX=0 CenterY=0 CenterZ=0 NormalX=0 NormalY=0 NormalZ=1 AngleXU=0 Radius=1
    g2: Circle CenterX=8 CenterY=6 CenterZ=0 NormalX=0 NormalY=0 NormalZ=1 AngleXU=0 Radius=1
    g3: BSplineCurve PolesCount=3 KnotsCount=2 Degree=2 IsPeriodic=0
    g4: GeomPoint X=0 Y=0 Z=0
    g5: GeomPoint X=8 Y=6 Z=0
    g6: LineSegment StartX=0 StartY=6 StartZ=0 EndX=8 EndY=6 EndZ=0
  constraints (14):
    c: Coincident(g0,g-1)
    c: Distance(g0) = 6
    c: Vertical(g0)
    c: Coincident(g3,g0)
    c: Weight(g1) = 1
    c: Equal(g1,g2)
    c: InternalAlignment(g1,g3)
    c: InternalAlignment(g2,g3)
    c: InternalAlignment(g4,g3)
    c: InternalAlignment(g5,g3)
    c: Block(g3)
    c: Coincident(g6,g0)
    c: Coincident(g6,g3)
    c: Horizontal(g6)
FEATURE [Part::Extrusion] Extrude019  label="caseScrewPillarBracket007"
  Base = -> Sketch025
  Dir = (0,0,1)
  DirMode = 2
  FaceMakerClass = Part::FaceMakerBullseye
  LengthFwd = 2.4
  LengthRev = 0
  Placement = pos=(101.3,29,65.23) rot=(0,1,0;1.5708rad)
  Solid = true
  Symmetric = false
FEATURE [Part::Box] Box011  label="frontCaseScrewPillarBracket"
  AttacherType = Attacher::AttachEngine3D
  Height = 2.4
  Length = 16
  Placement = pos=(87,28,2.3) rot=(0,0,1;0rad)
  Width = 7
FEATURE [Part::Box] Box012  label="frontCaseScrewPillarBracket001"
  AttacherType = Attacher::AttachEngine3D
  Height = 2.4
  Length = 16
  Placement = pos=(87,28,67.3) rot=(0,0,1;0rad)
  Width = 7
FEATURE [Sketcher::SketchObject] Sketch026
  FullyConstrained = true
  sketch-geometry (17):
    g0: Circle CenterX=-3.5 CenterY=23.5 CenterZ=0 NormalX=0 NormalY=0 NormalZ=1 AngleXU=0 Radius=1
    g1: Circle CenterX=-1 CenterY=15.25 CenterZ=0 NormalX=0 NormalY=0 NormalZ=1 AngleXU=0 Radius=1
    g2: Circle CenterX=-3.5 CenterY=7 CenterZ=0 NormalX=0 NormalY=0 NormalZ=1 AngleXU=0 Radius=1
    g3: BSplineCurve PolesCount=3 KnotsCount=2 Degree=2 IsPeriodic=0
    g4: GeomPoint X=-3.5 Y=23.5 Z=0
    g5: GeomPoint X=-3.5 Y=7 Z=0
    g6: Circle CenterX=-4.8 CenterY=30.5 CenterZ=0 NormalX=0 NormalY=0 NormalZ=1 AngleXU=0 Radius=1
    g7: Circle CenterX=-3.5 CenterY=30.5 CenterZ=0 NormalX=0 NormalY=0 NormalZ=1 AngleXU=0 Radius=1
    g8: Circle CenterX=-3.5 CenterY=29.2 CenterZ=0 NormalX=0 NormalY=0 NormalZ=1 AngleXU=0 Radius=1
    g9: BSplineCurve PolesCount=3 KnotsCount=2 Degree=2 IsPeriodic=0
    g10: GeomPoint X=-4.8 Y=30.5 Z=0
    g11: GeomPoint X=-3.5 Y=29.2 Z=0
    g12: LineSegment StartX=-3.5 StartY=29.2 StartZ=0 EndX=-3.5 EndY=23.5 EndZ=0
    g13: LineSegment StartX=-4.8 StartY=30.5 StartZ=0 EndX=0 EndY=30.5 EndZ=0
    g14: LineSegment StartX=-3.5 StartY=5 StartZ=0 EndX=-3.5 EndY=7 EndZ=0
    g15: LineSegment StartX=0 StartY=5 StartZ=0 EndX=0 EndY=30.5 EndZ=0
    g16: LineSegment StartX=-3.5 StartY=5 StartZ=0 EndX=0 EndY=5 EndZ=0
  constraints (33):
    c: Weight(g0) = 1
    c: Equal(g0,g1)
    c: Equal(g0,g2)
    c: InternalAlignment(g0,g3)
    c: InternalAlignment(g1,g3)
    c: InternalAlignment(g2,g3)
    c: InternalAlignment(g4,g3)
    c: InternalAlignment(g5,g3)
    c: Block(g3)
    c: Weight(g6) = 1
    c: Equal(g6,g7)
    c: Equal(g6,g8)
    c: InternalAlignment(g6,g9)
    c: InternalAlignment(g7,g9)
    c: InternalAlignment(g8,g9)
    c: InternalAlignment(g10,g9)
    c: InternalAlignment(g11,g9)
    c: Block(g9)
    c: Coincident(g12,g9)
    c: Coincident(g12,g3)
    c: Vertical(g12)
    c: Coincident(g13,g9)
    c: Horizontal(g13)
    c: Distance(g13) = 4.8
    c: Coincident(g14,g3)
    c: Vertical(g14)
    c: Coincident(g15,g13)
    c: Vertical(g15)
    c: Tangent(g15,g1)
    c: Distance(g14) = 2
    c: Coincident(g16,g14)
    c: Horizontal(g16)
    c: Coincident(g15,g16)
FEATURE [Part::Feature] Face050
  shape: bbox 4.8 x 25.5 x 2e-07 mm, 1 faces, 0 solids (baked)
FEATURE [Part::Revolution] Revolve054  label="moreFrontCaseScrewPost001"
  Angle = 360
  Axis = (0,1,0)
  Base = (0,0,0)
  FaceMakerClass = Part::FaceMakerBullseye
  Placement = pos=(102.5,4.5,3.5) rot=(0,0,1;0rad)
  Solid = false
  Source = -> Face050
  Symmetric = false
FEATURE [Part::Feature] Face051
  shape: bbox 4.8 x 25.5 x 2e-07 mm, 1 faces, 0 solids (baked)
FEATURE [Part::Revolution] Revolve055  label="moreFrontCaseScrewPost002"
  Angle = 360
  Axis = (0,1,0)
  Base = (0,0,0)
  FaceMakerClass = Part::FaceMakerBullseye
  Placement = pos=(102.5,4.5,68.5) rot=(0,0,1;0rad)
  Solid = false
  Source = -> Face051
  Symmetric = false
FEATURE [Sketcher::SketchObject] Sketch027
  FullyConstrained = true
  sketch-geometry (10):
    g0: LineSegment StartX=-1.6 StartY=4.7 StartZ=0 EndX=-1.6 EndY=1.7 EndZ=0
    g1: LineSegment StartX=-3.5 StartY=4.7 StartZ=0 EndX=-1.6 EndY=4.7 EndZ=0
    g2: LineSegment StartX=-1.6 StartY=1.7 StartZ=0 EndX=-1.6 EndY=1.5 EndZ=0
    g3: LineSegment StartX=-1.6 StartY=1.5 StartZ=0 EndX=-5.2 EndY=1.5 EndZ=0
    g4: Circle CenterX=-3.5 CenterY=4.7 CenterZ=0 NormalX=0 NormalY=0 NormalZ=1 AngleXU=0 Radius=1
    g5: Circle CenterX=-3.59627 CenterY=2.99743 CenterZ=0 NormalX=0 NormalY=0 NormalZ=1 AngleXU=0 Radius=1
    g6: Circle CenterX=-5.2 CenterY=1.5 CenterZ=0 NormalX=0 NormalY=0 NormalZ=1 AngleXU=0 Radius=1
    g7: BSplineCurve PolesCount=3 KnotsCount=2 Degree=2 IsPeriodic=0
    g8: GeomPoint X=-3.5 Y=4.7 Z=0
    g9: GeomPoint X=-5.2 Y=1.5 Z=0
  constraints (23):
    c: Vertical(g0)
    c: Distance(g0) = 3
    c: Coincident(g1,g0)
    c: Horizontal(g1)
    c: Block(g0)
    c: Block(g1)
    c: Coincident(g2,g0)
    c: Vertical(g2)
    c: Distance(g2) = 0.2
    c: Coincident(g3,g2)
    c: Horizontal(g3)
    c: Block(g3)
    c: Coincident(g7,g1)
    c: Weight(g4) = 1
    c: Equal(g4,g5)
    c: Equal(g4,g6)
    c: Coincident(g7,g3)
    c: InternalAlignment(g4,g7)
    c: InternalAlignment(g5,g7)
    c: InternalAlignment(g6,g7)
    c: InternalAlignment(g8,g7)
    c: InternalAlignment(g9,g7)
    c: Block(g7)
FEATURE [Sketcher::SketchObject] Sketch028
  FullyConstrained = true
  sketch-geometry (18):
    g0: LineSegment StartX=0 StartY=3e-16 StartZ=0 EndX=0 EndY=1.7 EndZ=0
    g1: LineSegment StartX=-3.5 StartY=0 StartZ=0 EndX=-3.5 EndY=0.9 EndZ=0
    g2: Circle CenterX=-2.7 CenterY=1.7 CenterZ=0 NormalX=0 NormalY=0 NormalZ=1 AngleXU=0 Radius=1
    g3: Circle CenterX=-3.5 CenterY=1.7 CenterZ=0 NormalX=0 NormalY=0 NormalZ=1 AngleXU=0 Radius=1
    g4: Circle CenterX=-3.5 CenterY=0.9 CenterZ=0 NormalX=0 NormalY=0 NormalZ=1 AngleXU=0 Radius=1
    g5: BSplineCurve PolesCount=3 KnotsCount=2 Degree=2 IsPeriodic=0
    g6: GeomPoint X=-2.7 Y=1.7 Z=0
    g7: GeomPoint X=-3.5 Y=0.9 Z=0
    g8: LineSegment StartX=-3.5 StartY=0 StartZ=0 EndX=-3.5 EndY=-7 EndZ=0
    g9: LineSegment StartX=0 StartY=3e-16 StartZ=0 EndX=0 EndY=-7 EndZ=0
    g10: LineSegment StartX=-3.5 StartY=-7 StartZ=0 EndX=0 EndY=-7 EndZ=0
    g11: LineSegment StartX=-2.7 StartY=1.7 StartZ=0 EndX=-1.6 EndY=1.7 EndZ=0
    g12: LineSegment StartX=0 StartY=1.7 StartZ=0 EndX=0 EndY=4.5 EndZ=0
    g13: LineSegment StartX=0 StartY=4.5 StartZ=0 EndX=0 EndY=10.8 EndZ=0
    g14: LineSegment StartX=0 StartY=10.8 StartZ=0 EndX=-2 EndY=10.8 EndZ=0
    g15: LineSegment StartX=-1.6 StartY=4.7 StartZ=0 EndX=-1.6 EndY=1.7 EndZ=0
    g16: LineSegment StartX=-1.6 StartY=4.7 StartZ=0 EndX=-2 EndY=4.7 EndZ=0
    g17: LineSegment StartX=-2 StartY=4.7 StartZ=0 EndX=-2 EndY=10.8 EndZ=0
  constraints (44):
    c: Vertical(g0)
    c: Vertical(g1)
    c: Distance(g1) = 0.9
    c: Block(g0)
    c: Distance(g0) = 1.7
    c: Weight(g2) = 1
    c: Equal(g2,g3)
    c: Equal(g2,g4)
    c: Coincident(g5,g1)
    c: InternalAlignment(g2,g5)
    c: InternalAlignment(g3,g5)
    c: InternalAlignment(g4,g5)
    c: InternalAlignment(g6,g5)
    c: InternalAlignment(g7,g5)
    c: Block(g5)
    c: Coincident(g8,g1)
    c: Vertical(g8)
    c: Distance(g8) = 7
    c: Vertical(g9)
    c: Equal(g8,g9) = 7
    c: Coincident(g9,g0)
    c: Coincident(g10,g8)
    c: Coincident(g10,g9)
    c: Horizontal(g10)
    c: Coincident(g11,g5)
    c: Horizontal(g11)
    c: Coincident(g12,g0)
    c: Vertical(g12)
    c: Distance(g12) = 2.8
    c: Coincident(g13,g12)
    c: Vertical(g13)
    c: Distance(g13) = 6.3
    c: Coincident(g14,g13)
    c: Horizontal(g14)
    c: Distance(g14) = 2
    c: Vertical(g15)
    c: Distance(g15) = 3
    c: Block(g11)
    c: Coincident(g15,g11)
    c: Coincident(g16,g15)
    c: Horizontal(g16)
    c: Coincident(g17,g16)
    c: Coincident(g17,g14)
    c: Vertical(g17)
FEATURE [Part::Revolution] Revolve040  label="backCaseScrewRetainer001"
  Angle = 360
  Axis = (0,1,0)
  Base = (0,0,0)
  FaceMakerClass = Part::FaceMakerBullseye
  Placement = pos=(12.5,3,10) rot=(0,0,1;0rad)
  Solid = false
  Source = -> Face036
  Symmetric = false
FEATURE [Part::Feature] Face055
  shape: bbox 3.5 x 30.2 x 2e-07 mm, 1 faces, 0 solids (baked)
FEATURE [Part::Revolution] Revolve059  label="backCaseScrewPost"
  Angle = 360
  Axis = (0,1,0)
  Base = (0,0,0)
  FaceMakerClass = Part::FaceMakerBullseye
  Placement = pos=(12.5,4.5,10) rot=(0,0,1;0rad)
  Solid = false
  Source = -> Face055
  Symmetric = false
FEATURE [Part::Feature] Face056
  shape: bbox 3.5 x 30.2 x 2e-07 mm, 1 faces, 0 solids (baked)
FEATURE [Part::Revolution] Revolve060  label="backCaseScrewPost001"
  Angle = 360
  Axis = (0,1,0)
  Base = (0,0,0)
  FaceMakerClass = Part::FaceMakerBullseye
  Placement = pos=(12.5,4.5,62) rot=(0,0,1;0rad)
  Solid = false
  Source = -> Face056
  Symmetric = false
FEATURE [Part::Feature] Face057
  shape: bbox 3.5 x 17.8 x 2e-07 mm, 1 faces, 0 solids (baked)
FEATURE [Part::Revolution] Revolve061  label="removeToCreateScrewAndThreadedInsertHole"
  Angle = 360
  Axis = (0,1,0)
  Base = (0,0,0)
  FaceMakerClass = Part::FaceMakerBullseye
  Placement = pos=(12.5,0,10) rot=(0,0,1;0rad)
  Solid = false
  Source = -> Face057
  Symmetric = false
FEATURE [Part::Feature] Face058
  shape: bbox 3.5 x 17.8 x 2e-07 mm, 1 faces, 0 solids (baked)
FEATURE [Part::Revolution] Revolve062  label="removeToCreateScrewAndThreadedInsertHole001"
  Angle = 360
  Axis = (0,1,0)
  Base = (0,0,0)
  FaceMakerClass = Part::FaceMakerBullseye
  Placement = pos=(12.5,0,62) rot=(0,0,1;0rad)
  Solid = false
  Source = -> Face058
  Symmetric = false
FEATURE [Part::Feature] Face059
  shape: bbox 3.5 x 17.8 x 2e-07 mm, 1 faces, 0 solids (baked)
FEATURE [Part::Revolution] Revolve063  label="removeToCreateScrewAndThreadedInsertHole002"
  Angle = 360
  Axis = (0,1,0)
  Base = (0,0,0)
  FaceMakerClass = Part::FaceMakerBullseye
  Placement = pos=(89.5,0,68.5) rot=(0,0,1;0rad)
  Solid = false
  Source = -> Face059
  Symmetric = false
FEATURE [Part::Feature] Face060
  shape: bbox 3.5 x 17.8 x 2e-07 mm, 1 faces, 0 solids (baked)
FEATURE [Part::Revolution] Revolve064  label="removeToCreateScrewAndThreadedInsertHole003"
  Angle = 360
  Axis = (0,1,0)
  Base = (0,0,0)
  FaceMakerClass = Part::FaceMakerBullseye
  Placement = pos=(89.5,0,3.5) rot=(0,0,1;0rad)
  Solid = false
  Source = -> Face060
  Symmetric = false
FEATURE [Part::Feature] Face061
  shape: bbox 3.5 x 17.8 x 2e-07 mm, 1 faces, 0 solids (baked)
FEATURE [Part::Revolution] Revolve065  label="removeToCreateScrewAndThreadedInsertHole004"
  Angle = 360
  Axis = (0,1,0)
  Base = (0,0,0)
  FaceMakerClass = Part::FaceMakerBullseye
  Placement = pos=(102.5,4.7,3.5) rot=(0,0,1;0rad)
  Solid = false
  Source = -> Face061
  Symmetric = false
FEATURE [Part::Feature] Face062
  shape: bbox 3.5 x 17.8 x 2e-07 mm, 1 faces, 0 solids (baked)
FEATURE [Part::Revolution] Revolve066  label="removeToCreateScrewAndThreadedInsertHole005"
  Angle = 360
  Axis = (0,1,0)
  Base = (0,0,0)
  FaceMakerClass = Part::FaceMakerBullseye
  Placement = pos=(102.5,4.7,68.5) rot=(0,0,1;0rad)
  Solid = false
  Source = -> Face062
  Symmetric = false
FEATURE [Part::MultiFuse] Fusion047  label="makeHoles"
  Shapes = -> [Revolve066,Revolve065,Revolve064,Revolve063,Revolve062,Revolve061]
FEATURE [Part::Feature] Face063
  shape: bbox 3.6 x 3.2 x 2e-07 mm, 1 faces, 0 solids (baked)
FEATURE [Part::Revolution] Revolve067  label="moreFrontCaseScrewRetainer002"
  Angle = 360
  Axis = (0,1,0)
  Base = (0,0,0)
  FaceMakerClass = Part::FaceMakerBullseye
  Placement = pos=(102.5,4.5,68.5) rot=(0,0,1;0rad)
  Solid = false
  Source = -> Face063
  Symmetric = false
FEATURE [Part::Feature] Face064
  shape: bbox 3.6 x 3.2 x 2e-07 mm, 1 faces, 0 solids (baked)
FEATURE [Part::Revolution] Revolve068  label="moreFrontCaseScrewRetainer003"
  Angle = 360
  Axis = (0,1,0)
  Base = (0,0,0)
  FaceMakerClass = Part::FaceMakerBullseye
  Placement = pos=(102.5,4.5,3.5) rot=(0,0,1;0rad)
  Solid = false
  Source = -> Face064
  Symmetric = false
FEATURE [Part::Feature] Face065
  shape: bbox 3.5 x 17.8 x 2e-07 mm, 1 faces, 0 solids (baked)
FEATURE [Part::Revolution] Revolve069  label="removeToCreateScrewAndThreadedInsertHole006"
  Angle = 360
  Axis = (0,1,0)
  Base = (0,0,0)
  FaceMakerClass = Part::FaceMakerBullseye
  Placement = pos=(12.5,0,10) rot=(0,0,1;0rad)
  Solid = false
  Source = -> Face065
  Symmetric = false
FEATURE [Part::Feature] Face066
  shape: bbox 3.5 x 17.8 x 2e-07 mm, 1 faces, 0 solids (baked)
FEATURE [Part::Revolution] Revolve070  label="removeToCreateScrewAndThreadedInsertHole007"
  Angle = 360
  Axis = (0,1,0)
  Base = (0,0,0)
  FaceMakerClass = Part::FaceMakerBullseye
  Placement = pos=(12.5,0,62) rot=(0,0,1;0rad)
  Solid = false
  Source = -> Face066
  Symmetric = false
FEATURE [Part::Feature] Face067
  shape: bbox 3.5 x 17.8 x 2e-07 mm, 1 faces, 0 solids (baked)
FEATURE [Part::Revolution] Revolve071  label="removeToCreateScrewAndThreadedInsertHole008"
  Angle = 360
  Axis = (0,1,0)
  Base = (0,0,0)
  FaceMakerClass = Part::FaceMakerBullseye
  Placement = pos=(89.5,0,68.5) rot=(0,0,1;0rad)
  Solid = false
  Source = -> Face067
  Symmetric = false
FEATURE [Part::Feature] Face068
  shape: bbox 3.5 x 17.8 x 2e-07 mm, 1 faces, 0 solids (baked)
FEATURE [Part::Revolution] Revolve072  label="removeToCreateScrewAndThreadedInsertHole009"
  Angle = 360
  Axis = (0,1,0)
  Base = (0,0,0)
  FaceMakerClass = Part::FaceMakerBullseye
  Placement = pos=(89.5,0,3.5) rot=(0,0,1;0rad)
  Solid = false
  Source = -> Face068
  Symmetric = false
FEATURE [Part::Feature] Face069
  shape: bbox 3.5 x 17.8 x 2e-07 mm, 1 faces, 0 solids (baked)
FEATURE [Part::Feature] Face070
  shape: bbox 3.5 x 17.8 x 2e-07 mm, 1 faces, 0 solids (baked)
FEATURE [Part::Revolution] Revolve073  label="removeToCreateScrewAndThreadedInsertHole010"
  Angle = 360
  Axis = (0,1,0)
  Base = (0,0,0)
  FaceMakerClass = Part::FaceMakerBullseye
  Placement = pos=(102.5,4.7,3.5) rot=(0,0,1;0rad)
  Solid = false
  Source = -> Face069
  Symmetric = false
FEATURE [Part::Revolution] Revolve074  label="removeToCreateScrewAndThreadedInsertHole011"
  Angle = 360
  Axis = (0,1,0)
  Base = (0,0,0)
  FaceMakerClass = Part::FaceMakerBullseye
  Placement = pos=(102.5,4.7,68.5) rot=(0,0,1;0rad)
  Solid = false
  Source = -> Face070
  Symmetric = false
FEATURE [Part::MultiFuse] Fusion048  label="makeHoles001"
  Shapes = -> [Revolve074,Revolve073,Revolve072,Revolve071,Revolve070,Revolve069]
FEATURE [Part::MultiFuse] Fusion049  label="caseScrewRetainers"
  Shapes = -> [Revolve067,Revolve068,Revolve048,Revolve047,Revolve039,Revolve040]
FEATURE [Part::Cut] Cut015  label="caseScrewRetainers001"
  Base = -> Fusion049
  Tool = -> Fusion048
FEATURE [Part::MultiFuse] Fusion050  label="casePillars"
  Shapes = -> [Revolve055,Revolve054,Revolve043,Revolve046,Revolve059,Revolve060]
FEATURE [Part::Feature] Face071 .. Face076  x6 (patterned run collapsed; names and placements below)
  shape: bbox 3.5 x 17.8 x 2e-07 mm, 1 faces, 0 solids (baked)
FEATURE [Part::Revolution] Revolve075  label="removeToCreateScrewAndThreadedInsertHole012"
  Angle = 360
  Axis = (0,1,0)
  Base = (0,0,0)
  FaceMakerClass = Part::FaceMakerBullseye
  Placement = pos=(12.5,0,10) rot=(0,0,1;0rad)
  Solid = false
  Source = -> Face071
  Symmetric = false
FEATURE [Part::Revolution] Revolve076  label="removeToCreateScrewAndThreadedInsertHole013"
  Angle = 360
  Axis = (0,1,0)
  Base = (0,0,0)
  FaceMakerClass = Part::FaceMakerBullseye
  Placement = pos=(12.5,0,62) rot=(0,0,1;0rad)
  Solid = false
  Source = -> Face072
  Symmetric = false
FEATURE [Part::Revolution] Revolve077  label="removeToCreateScrewAndThreadedInsertHole014"
  Angle = 360
  Axis = (0,1,0)
  Base = (0,0,0)
  FaceMakerClass = Part::FaceMakerBullseye
  Placement = pos=(89.5,0,68.5) rot=(0,0,1;0rad)
  Solid = false
  Source = -> Face073
  Symmetric = false
FEATURE [Part::Revolution] Revolve078  label="removeToCreateScrewAndThreadedInsertHole015"
  Angle = 360
  Axis = (0,1,0)
  Base = (0,0,0)
  FaceMakerClass = Part::FaceMakerBullseye
  Placement = pos=(89.5,0,3.5) rot=(0,0,1;0rad)
  Solid = false
  Source = -> Face074
  Symmetric = false
FEATURE [Part::Revolution] Revolve079  label="removeToCreateScrewAndThreadedInsertHole016"
  Angle = 360
  Axis = (0,1,0)
  Base = (0,0,0)
  FaceMakerClass = Part::FaceMakerBullseye
  Placement = pos=(102.5,4.7,3.5) rot=(0,0,1;0rad)
  Solid = false
  Source = -> Face075
  Symmetric = false
FEATURE [Part::Revolution] Revolve080  label="removeToCreateScrewAndThreadedInsertHole017"
  Angle = 360
  Axis = (0,1,0)
  Base = (0,0,0)
  FaceMakerClass = Part::FaceMakerBullseye
  Placement = pos=(102.5,4.7,68.5) rot=(0,0,1;0rad)
  Solid = false
  Source = -> Face076
  Symmetric = false
FEATURE [Part::MultiFuse] Fusion051  label="makeHoles002"
  Shapes = -> [Revolve080,Revolve079,Revolve078,Revolve077,Revolve076,Revolve075]
FEATURE [Part::Cut] Cut016  label="caesPillars"
  Base = -> Fusion050
  Tool = -> Fusion051
FEATURE [Part::Revolution] Revolve009  label="plugHousing016"
  Angle = 360
  Axis = (0,1,0)
  Base = (0,0,0)
  FaceMakerClass = Part::FaceMakerBullseye
  Placement = pos=(0,0,36.15) rot=(0,0,1;0rad)
  Solid = false
  Source = -> Face012
  Symmetric = false
FEATURE [Part::MultiFuse] Fusion014  label="plugHousing023"
  Placement = pos=(0,0,0) rot=(0,0,1;1.5708rad)
  Shapes = -> [Revolve011,Revolve009]
FEATURE [Part::Revolution] Revolve010  label="plugHousing017"
  Angle = 360
  Axis = (0,1,0)
  Base = (0,0,0)
  FaceMakerClass = Part::FaceMakerBullseye
  Placement = pos=(0,0,36.15) rot=(0,0,1;0rad)
  Solid = false
  Source = -> Face014
  Symmetric = false
FEATURE [Part::MultiFuse] Fusion015  label="plugHousing024"
  Placement = pos=(0,0,0) rot=(0,0,1;1.5708rad)
  Shapes = -> [Revolve010,Revolve015]
FEATURE [Part::Revolution] Revolve014  label="plugHousing026"
  Angle = 360
  Axis = (0,1,0)
  Base = (0,0,0)
  FaceMakerClass = Part::FaceMakerBullseye
  Placement = pos=(0,0,36.15) rot=(0,0,1;0rad)
  Solid = false
  Source = -> Face011
  Symmetric = false
FEATURE [Part::Revolution] Revolve013  label="plugHousing025"
  Angle = 360
  Axis = (0,1,0)
  Base = (0,0,0)
  FaceMakerClass = Part::FaceMakerBullseye
  Placement = pos=(0,0,36.15) rot=(0,0,1;0rad)
  Solid = false
  Source = -> Face015
  Symmetric = false
FEATURE [Part::MultiFuse] Fusion016  label="plugHousing028"
  Placement = pos=(0,19,0) rot=(0,0,1;3.14159rad)
  Shapes = -> [Fusion014,Fusion013]
FEATURE [Part::MultiFuse] Fusion011  label="plugHousing018"
  Placement = pos=(0,0,0) rot=(0,0,1;1.5708rad)
  Shapes = -> [Revolve014,Revolve013]
FEATURE [Part::MultiFuse] Fusion012  label="plugHousing019"
  Placement = pos=(0,19,0) rot=(0,0,1;3.14159rad)
  Shapes = -> [Fusion011,Fusion015]
FEATURE [Part::MultiFuse] Fusion017  label="plugHousing029"
  Placement = pos=(122.621,0,-0.15) rot=(0,0,1;0rad)
  Shapes = -> [Fusion016,Fusion012]
FEATURE [Part::MultiFuse] Fusion052  label="casePillarRetainers"
  Shapes = -> [Extrude012,Extrude013,Extrude014,Extrude015,Extrude016,Extrude017,Extrude018,Extrude019,Box011,Box012]
FEATURE [Part::Feature] Face077
  shape: bbox 3.5 x 17.8 x 2e-07 mm, 1 faces, 0 solids (baked)
FEATURE [Part::Revolution] Revolve081  label="removeToCreateScrewAndThreadedInsertHole018"
  Angle = 360
  Axis = (0,1,0)
  Base = (0,0,0)
  FaceMakerClass = Part::FaceMakerBullseye
  Placement = pos=(62.3,30.3,19.7) rot=(0,0,1;0rad)
  Solid = false
  Source = -> Face077
  Symmetric = false
FEATURE [Part::Feature] Face078
  shape: bbox 3.5 x 17.8 x 2e-07 mm, 1 faces, 0 solids (baked)
FEATURE [Part::Revolution] Revolve082  label="removeToCreateScrewAndThreadedInsertHole019"
  Angle = 360
  Axis = (0,1,0)
  Base = (0,0,0)
  FaceMakerClass = Part::FaceMakerBullseye
  Placement = pos=(62.3,30.3,51.7) rot=(0,0,1;0rad)
  Solid = false
  Source = -> Face078
  Symmetric = false
FEATURE [Part::Feature] Face079
  shape: bbox 3.5 x 17.8 x 2e-07 mm, 1 faces, 0 solids (baked)
FEATURE [Part::Revolution] Revolve083  label="removeToCreateScrewAndThreadedInsertHole020"
  Angle = 360
  Axis = (0,1,0)
  Base = (0,0,0)
  FaceMakerClass = Part::FaceMakerBullseye
  Placement = pos=(30.3,30.3,19.7) rot=(0,0,1;0rad)
  Solid = false
  Source = -> Face079
  Symmetric = false
FEATURE [Part::Feature] Face080
  shape: bbox 3.5 x 17.8 x 2e-07 mm, 1 faces, 0 solids (baked)
FEATURE [Part::Revolution] Revolve084  label="removeToCreateScrewAndThreadedInsertHole021"
  Angle = 360
  Axis = (0,1,0)
  Base = (0,0,0)
  FaceMakerClass = Part::FaceMakerBullseye
  Placement = pos=(30.3,30.3,51.7) rot=(0,0,1;0rad)
  Solid = false
  Source = -> Face080
  Symmetric = false
FEATURE [Part::MultiFuse] Fusion053  label="createThreadedInsertHolesForFan"
  Shapes = -> [Revolve081,Revolve082,Revolve083,Revolve084]
FEATURE [Part::Cut] Cut017  label="fanScrewHousing001"
  Base = -> Fusion046
  Tool = -> Fusion053
FEATURE [Part::Feature] Face081
  shape: bbox 3.5 x 17.8 x 2e-07 mm, 1 faces, 0 solids (baked)
FEATURE [Part::Revolution] Revolve085  label="removeToCreateScrewAndThreadedInsertHole022"
  Angle = 360
  Axis = (0,1,0)
  Base = (0,0,0)
  FaceMakerClass = Part::FaceMakerBullseye
  Placement = pos=(62.3,30.3,19.7) rot=(0,0,1;0rad)
  Solid = false
  Source = -> Face081
  Symmetric = false
FEATURE [Part::Feature] Face082
  shape: bbox 3.5 x 17.8 x 2e-07 mm, 1 faces, 0 solids (baked)
FEATURE [Part::Revolution] Revolve086  label="removeToCreateScrewAndThreadedInsertHole023"
  Angle = 360
  Axis = (0,1,0)
  Base = (0,0,0)
  FaceMakerClass = Part::FaceMakerBullseye
  Placement = pos=(62.3,30.3,51.7) rot=(0,0,1;0rad)
  Solid = false
  Source = -> Face082
  Symmetric = false
FEATURE [Part::Feature] Face083
  shape: bbox 3.5 x 17.8 x 2e-07 mm, 1 faces, 0 solids (baked)
FEATURE [Part::Revolution] Revolve087  label="removeToCreateScrewAndThreadedInsertHole024"
  Angle = 360
  Axis = (0,1,0)
  Base = (0,0,0)
  FaceMakerClass = Part::FaceMakerBullseye
  Placement = pos=(30.3,30.3,19.7) rot=(0,0,1;0rad)
  Solid = false
  Source = -> Face083
  Symmetric = false
FEATURE [Part::Feature] Face084
  shape: bbox 3.5 x 17.8 x 2e-07 mm, 1 faces, 0 solids (baked)
FEATURE [Part::Revolution] Revolve088  label="removeToCreateScrewAndThreadedInsertHole025"
  Angle = 360
  Axis = (0,1,0)
  Base = (0,0,0)
  FaceMakerClass = Part::FaceMakerBullseye
  Placement = pos=(30.3,30.3,51.7) rot=(0,0,1;0rad)
  Solid = false
  Source = -> Face084
  Symmetric = false
FEATURE [Part::MultiFuse] Fusion054  label="createThreadedInsertHolesForFan001"
  Shapes = -> [Revolve085,Revolve086,Revolve087,Revolve088]
FEATURE [Part::Cut] Cut018  label="top007"
  Base = -> Fusion040
  Tool = -> Fusion054
FEATURE [Sketcher::SketchObject] Sketch029
  FullyConstrained = false
  Placement = pos=(0,0,0) rot=(1,0,0;1.5708rad)
  sketch-geometry (24):
    g0: ArcOfCircle CenterX=-4 CenterY=-10.5 CenterZ=0 NormalX=0 NormalY=0 NormalZ=1 AngleXU=0 Radius=1.5 StartAngle=6e-16 EndAngle=3.14159
    g1: ArcOfCircle CenterX=-34.2 CenterY=-10.5 CenterZ=0 NormalX=0 NormalY=0 NormalZ=1 AngleXU=0 Radius=1.5 StartAngle=0 EndAngle=3.14159
    g2: ArcOfCircle CenterX=-34.2 CenterY=-27.7 CenterZ=0 NormalX=0 NormalY=0 NormalZ=1 AngleXU=0 Radius=1.5 StartAngle=3.14159 EndAngle=6.28319
    g3: ArcOfCircle CenterX=-4 CenterY=-27.7 CenterZ=0 NormalX=0 NormalY=0 NormalZ=1 AngleXU=0 Radius=1.5 StartAngle=3.1416 EndAngle=6.28319
    g4: ArcOfCircle CenterX=-10 CenterY=-4.3 CenterZ=0 NormalX=0 NormalY=0 NormalZ=1 AngleXU=0 Radius=1.5 StartAngle=2e-16 EndAngle=3.14159
    g5: ArcOfCircle CenterX=-16.1 CenterY=-1.8 CenterZ=0 NormalX=0 NormalY=0 NormalZ=1 AngleXU=0 Radius=1.5 StartAngle=5e-16 EndAngle=3.14159
    g6: ArcOfCircle CenterX=-22.1 CenterY=-1.8 CenterZ=0 NormalX=0 NormalY=0 NormalZ=1 AngleXU=0 Radius=1.5 StartAngle=5e-16 EndAngle=3.14159
    g7: ArcOfCircle CenterX=-28.2 CenterY=-4.3 CenterZ=0 NormalX=0 NormalY=0 NormalZ=1 AngleXU=0 Radius=1.5 StartAngle=2e-16 EndAngle=3.14159
    g8: ArcOfCircle CenterX=-10 CenterY=-33.9 CenterZ=0 NormalX=0 NormalY=0 NormalZ=1 AngleXU=0 Radius=1.5 StartAngle=3.14159 EndAngle=6.28319
    g9: ArcOfCircle CenterX=-16.1 CenterY=-36.4 CenterZ=0 NormalX=0 NormalY=0 NormalZ=1 AngleXU=0 Radius=1.5 StartAngle=3.14159 EndAngle=6.28319
    g10: ArcOfCircle CenterX=-22.1 CenterY=-36.4 CenterZ=0 NormalX=0 NormalY=0 NormalZ=1 AngleXU=0 Radius=1.5 StartAngle=3.14159 EndAngle=6.28319
    g11: ArcOfCircle CenterX=-28.2 CenterY=-33.9 CenterZ=0 NormalX=0 NormalY=0 NormalZ=1 AngleXU=0 Radius=1.5 StartAngle=3.14159 EndAngle=6.28319
    g12: LineSegment StartX=-35.7 StartY=-10.5 StartZ=0 EndX=-35.7 EndY=-27.7 EndZ=0
    g13: LineSegment StartX=-32.7 StartY=-10.5 StartZ=0 EndX=-32.7 EndY=-27.7 EndZ=0
    g14: LineSegment StartX=-29.7 StartY=-33.9 StartZ=0 EndX=-29.7 EndY=-4.3 EndZ=0
    g15: LineSegment StartX=-26.7 StartY=-33.9 StartZ=0 EndX=-26.7 EndY=-4.3 EndZ=0
    g16: LineSegment StartX=-2.5 StartY=-10.5 StartZ=0 EndX=-2.5 EndY=-27.7 EndZ=0
    g17: LineSegment StartX=-8.5 StartY=-4.3 StartZ=0 EndX=-8.5 EndY=-33.9 EndZ=0
    g18: LineSegment StartX=-5.5 StartY=-10.5 StartZ=0 EndX=-5.5 EndY=-27.7 EndZ=0
    g19: LineSegment StartX=-11.5 StartY=-4.3 StartZ=0 EndX=-11.5 EndY=-33.9 EndZ=0
    g20: LineSegment StartX=-14.6 StartY=-1.8 StartZ=0 EndX=-14.6 EndY=-36.4 EndZ=0
    g21: LineSegment StartX=-17.6 StartY=-1.8 StartZ=0 EndX=-17.6 EndY=-36.4 EndZ=0
    g22: LineSegment StartX=-20.6 StartY=-36.4 StartZ=0 EndX=-20.6 EndY=-1.8 EndZ=0
    g23: LineSegment StartX=-23.6 StartY=-1.8 StartZ=0 EndX=-23.6 EndY=-36.4 EndZ=0
  constraints (48):
    c: Block(g0)
    c: Block(g1)
    c: Block(g2)
    c: Block(g3)
    c: Block(g4)
    c: Block(g5)
    c: Block(g6)
    c: Block(g7)
    c: Block(g8)
    c: Block(g9)
    c: Block(g10)
    c: Block(g11)
    c: Coincident(g12,g1)
    c: Coincident(g12,g2)
    c: Vertical(g12)
    c: Coincident(g13,g1)
    c: Coincident(g13,g2)
    c: Vertical(g13)
    c: Coincident(g14,g11)
    c: Coincident(g14,g7)
    c: Vertical(g14)
    c: Coincident(g15,g11)
    c: Coincident(g15,g7)
    c: Vertical(g15)
    c: Coincident(g16,g0)
    c: Coincident(g16,g3)
    c: Vertical(g16)
    c: Coincident(g17,g4)
    c: Coincident(g17,g8)
    c: Vertical(g17)
    c: Coincident(g18,g0)
    c: Coincident(g18,g3)
    c: Vertical(g18)
    c: Coincident(g19,g4)
    c: Coincident(g19,g8)
    c: Vertical(g19)
    c: Coincident(g20,g5)
    c: Coincident(g20,g9)
    c: Vertical(g20)
    c: Coincident(g21,g5)
    c: Coincident(g21,g9)
    c: Vertical(g21)
    c: Coincident(g22,g10)
    c: Coincident(g22,g6)
    c: Vertical(g22)
    c: Coincident(g23,g6)
    c: Coincident(g23,g10)
    c: Vertical(g23)
FEATURE [Part::Extrusion] Extrude020  label="removeToCreateFanGrillHoles"
  Base = -> Sketch029
  Dir = (0,-1,6e-16)
  DirMode = 2
  FaceMakerClass = Part::FaceMakerBullseye
  LengthFwd = 10
  LengthRev = 0
  Placement = pos=(65.4,44,54.82) rot=(0,0,1;0rad)
  Solid = true
  Symmetric = false
FEATURE [Part::MultiFuse] Fusion055  label="top008"
  Shapes = -> [Cut017,Cut018]
FEATURE [Part::Cut] Cut019  label="top009"
  Base = -> Fusion055
  Tool = -> Extrude020
FEATURE [App::MeasureDistance] Distance003  label="Distance: 71.95 mm"
  Distance = 71.9513
  P1 = (117,38,72)
  P2 = (117,38,0.0487319)
FEATURE [Sketcher::SketchObject] Sketch030
  FullyConstrained = true
  Placement = pos=(117,19,0) rot=(0.57735,0.57735,0.57735;2.0944rad)
  sketch-geometry (48):
    g0: LineSegment StartX=-49.19 StartY=69.25 StartZ=0 EndX=-49.19 EndY=66.25 EndZ=0
    g1: LineSegment StartX=-49.19 StartY=63.5 StartZ=0 EndX=-49.19 EndY=60.5 EndZ=0
    g2: LineSegment StartX=-49.19 StartY=57.75 StartZ=0 EndX=-49.19 EndY=54.75 EndZ=0
    g3: LineSegment StartX=-49.19 StartY=52 StartZ=0 EndX=-49.19 EndY=49 EndZ=0
    g4: LineSegment StartX=-49.19 StartY=46.25 StartZ=0 EndX=-49.19 EndY=43.25 EndZ=0
    g5: LineSegment StartX=-49.19 StartY=40.5 StartZ=0 EndX=-49.19 EndY=37.5 EndZ=0
    g6: LineSegment StartX=-49.19 StartY=34.5 StartZ=0 EndX=-49.19 EndY=31.5 EndZ=0
    g7: LineSegment StartX=-49.19 StartY=28.75 StartZ=0 EndX=-49.19 EndY=25.75 EndZ=0
    g8: LineSegment StartX=-49.19 StartY=23 StartZ=0 EndX=-49.19 EndY=20 EndZ=0
    g9: LineSegment StartX=-49.19 StartY=17.25 StartZ=0 EndX=-49.19 EndY=14.25 EndZ=0
    g10: LineSegment StartX=-49.19 StartY=11.5 StartZ=0 EndX=-49.19 EndY=8.5 EndZ=0
    g11: LineSegment StartX=-49.19 StartY=5.75 StartZ=0 EndX=-49.19 EndY=2.75 EndZ=0
    g12: ArcOfCircle CenterX=-1.5 CenterY=67.75 CenterZ=0 NormalX=0 NormalY=0 NormalZ=1 AngleXU=0 Radius=1.5 StartAngle=4.71239 EndAngle=7.85398
    g13: ArcOfCircle CenterX=-1.5 CenterY=62 CenterZ=0 NormalX=0 NormalY=0 NormalZ=1 AngleXU=0 Radius=1.5 StartAngle=4.71239 EndAngle=7.85398
    g14: ArcOfCircle CenterX=-1.5 CenterY=56.25 CenterZ=0 NormalX=0 NormalY=0 NormalZ=1 AngleXU=0 Radius=1.5 StartAngle=4.71239 EndAngle=7.85398
    g15: ArcOfCircle CenterX=-11.49 CenterY=50.5 CenterZ=0 NormalX=0 NormalY=0 NormalZ=1 AngleXU=0 Radius=1.5 StartAngle=4.71239 EndAngle=7.85398
    g16: ArcOfCircle CenterX=-16.28 CenterY=44.75 CenterZ=0 NormalX=0 NormalY=0 NormalZ=1 AngleXU=0 Radius=1.5 StartAngle=4.71239 EndAngle=7.85398
    g17: ArcOfCircle CenterX=-18.2337 CenterY=39 CenterZ=0 NormalX=0 NormalY=0 NormalZ=1 AngleXU=0 Radius=1.5 StartAngle=4.71485 EndAngle=7.85398
    g18: ArcOfCircle CenterX=-16.2837 CenterY=27.25 CenterZ=0 NormalX=0 NormalY=0 NormalZ=1 AngleXU=0 Radius=1.5 StartAngle=4.71485 EndAngle=7.85398
    g19: ArcOfCircle CenterX=-18.2337 CenterY=33 CenterZ=0 NormalX=0 NormalY=0 NormalZ=1 AngleXU=0 Radius=1.5 StartAngle=4.71485 EndAngle=7.85398
    g20: ArcOfCircle CenterX=-11.49 CenterY=21.5 CenterZ=0 NormalX=0 NormalY=0 NormalZ=1 AngleXU=0 Radius=1.5 StartAngle=4.71239 EndAngle=7.85398
    g21: ArcOfCircle CenterX=-1.5 CenterY=4.25 CenterZ=0 NormalX=0 NormalY=0 NormalZ=1 AngleXU=0 Radius=1.5 StartAngle=4.71239 EndAngle=7.85398
    g22: ArcOfCircle CenterX=-1.5 CenterY=10 CenterZ=0 NormalX=0 NormalY=0 NormalZ=1 AngleXU=0 Radius=1.5 StartAngle=4.71239 EndAngle=7.85398
    g23: ArcOfCircle CenterX=-1.5 CenterY=15.75 CenterZ=0 NormalX=0 NormalY=0 NormalZ=1 AngleXU=0 Radius=1.5 StartAngle=4.71239 EndAngle=7.85398
    g24: LineSegment StartX=-49.19 StartY=69.25 StartZ=0 EndX=-1.5 EndY=69.25 EndZ=0
    g25: LineSegment StartX=-49.19 StartY=66.25 StartZ=0 EndX=-1.5 EndY=66.25 EndZ=0
    g26: LineSegment StartX=-49.19 StartY=63.5 StartZ=0 EndX=-1.5 EndY=63.5 EndZ=0
    g27: LineSegment StartX=-49.19 StartY=60.5 StartZ=0 EndX=-1.5 EndY=60.5 EndZ=0
    g28: LineSegment StartX=-49.19 StartY=57.75 StartZ=0 EndX=-1.5 EndY=57.75 EndZ=0
    g29: LineSegment StartX=-49.19 StartY=54.75 StartZ=0 EndX=-1.5 EndY=54.75 EndZ=0
    g30: LineSegment StartX=-49.19 StartY=52 StartZ=0 EndX=-11.49 EndY=52 EndZ=0
    g31: LineSegment StartX=-49.19 StartY=49 StartZ=0 EndX=-11.49 EndY=49 EndZ=0
    g32: LineSegment StartX=-49.19 StartY=46.25 StartZ=0 EndX=-16.28 EndY=46.25 EndZ=0
    g33: LineSegment StartX=-49.19 StartY=43.25 StartZ=0 EndX=-16.28 EndY=43.25 EndZ=0
    g34: LineSegment StartX=-49.19 StartY=40.5 StartZ=0 EndX=-18.2337 EndY=40.5 EndZ=0
    g35: LineSegment StartX=-49.19 StartY=37.5 StartZ=0 EndX=-18.23 EndY=37.5 EndZ=0
    g36: LineSegment StartX=-49.19 StartY=34.5 StartZ=0 EndX=-18.2337 EndY=34.5 EndZ=0
    g37: LineSegment StartX=-49.19 StartY=31.5 StartZ=0 EndX=-18.23 EndY=31.5 EndZ=0
    g38: LineSegment StartX=-49.19 StartY=28.75 StartZ=0 EndX=-16.2837 EndY=28.75 EndZ=0
    g39: LineSegment StartX=-49.19 StartY=25.75 StartZ=0 EndX=-16.28 EndY=25.75 EndZ=0
    g40: LineSegment StartX=-49.19 StartY=23 StartZ=0 EndX=-11.49 EndY=23 EndZ=0
    g41: LineSegment StartX=-49.19 StartY=20 StartZ=0 EndX=-11.49 EndY=20 EndZ=0
    g42: LineSegment StartX=-49.19 StartY=17.25 StartZ=0 EndX=-1.5 EndY=17.25 EndZ=0
    g43: LineSegment StartX=-49.19 StartY=14.25 StartZ=0 EndX=-1.5 EndY=14.25 EndZ=0
    g44: LineSegment StartX=-49.19 StartY=11.5 StartZ=0 EndX=-1.5 EndY=11.5 EndZ=0
    g45: LineSegment StartX=-49.19 StartY=8.5 StartZ=0 EndX=-1.5 EndY=8.5 EndZ=0
    g46: LineSegment StartX=-49.19 StartY=5.75 StartZ=0 EndX=-1.5 EndY=5.75 EndZ=0
    g47: LineSegment StartX=-49.19 StartY=2.75 StartZ=0 EndX=-1.5 EndY=2.75 EndZ=0
  constraints (120):
    c: Vertical(g0)
    c: Distance(g0) = 3
    c: Block(g0)
    c: Vertical(g1)
    c: Distance(g1) = 3
    c: Vertical(g2)
    c: Equal(g0,g2) = 3
    c: Block(g2)
    c: Vertical(g3)
    c: Equal(g1,g3) = 3
    c: Vertical(g4)
    c: Equal(g0,g4) = 3
    c: Block(g4)
    c: Vertical(g5)
    c: Equal(g1,g5) = 3
    c: Vertical(g6)
    c: Equal(g0,g6) = 3
    c: Block(g6)
    c: Vertical(g7)
    c: Equal(g1,g7) = 3
    c: Vertical(g8)
    c: Equal(g0,g8) = 3
    c: Block(g8)
    c: Vertical(g9)
    c: Equal(g1,g9) = 3
    c: Vertical(g10)
    c: Equal(g0,g10) = 3
    c: Block(g10)
    c: Vertical(g11)
    c: Equal(g1,g11) = 3
    c: Block(g12)
    c: Block(g13)
    c: Block(g14)
    c: Block(g15)
    c: Block(g16)
    c: Block(g17)
    c: Block(g18)
    c: Block(g19)
    c: Block(g20)
    c: Block(g21)
    c: Block(g22)
    c: Block(g23)
    c: Block(g11)
    c: Block(g9)
    c: Block(g7)
    c: Block(g5)
    c: Block(g3)
    c: Block(g1)
    c: Coincident(g24,g0)
    c: Coincident(g24,g12)
    c: Horizontal(g24)
    c: Coincident(g25,g0)
    c: Coincident(g25,g12)
    c: Horizontal(g25)
    c: Coincident(g26,g1)
    c: Coincident(g26,g13)
    c: Horizontal(g26)
    c: Coincident(g27,g1)
    c: Coincident(g27,g13)
    c: Horizontal(g27)
    c: Coincident(g28,g2)
    c: Coincident(g28,g14)
    c: Horizontal(g28)
    c: Coincident(g29,g2)
    c: Coincident(g29,g14)
    c: Horizontal(g29)
    c: Coincident(g30,g3)
    c: Coincident(g30,g15)
    c: Horizontal(g30)
    c: Coincident(g31,g3)
    c: Coincident(g31,g15)
    c: Horizontal(g31)
    c: Coincident(g32,g4)
    c: Coincident(g32,g16)
    c: Horizontal(g32)
    c: Coincident(g33,g4)
    c: Coincident(g33,g16)
    c: Horizontal(g33)
    c: Coincident(g34,g5)
    c: Coincident(g34,g17)
    c: Horizontal(g34)
    c: Coincident(g35,g5)
    c: Coincident(g35,g17)
    c: Horizontal(g35)
    c: Coincident(g36,g6)
    c: Coincident(g36,g19)
    c: Horizontal(g36)
    c: Coincident(g37,g6)
    c: Coincident(g37,g19)
    c: Horizontal(g37)
    c: Coincident(g38,g7)
    c: Coincident(g38,g18)
    c: Horizontal(g38)
    c: Coincident(g39,g7)
    c: Coincident(g39,g18)
    c: Horizontal(g39)
    c: Coincident(g40,g8)
    c: Coincident(g40,g20)
    c: Horizontal(g40)
    c: Coincident(g41,g8)
    c: Coincident(g41,g20)
    c: Horizontal(g41)
    c: Coincident(g42,g9)
    c: Coincident(g42,g23)
    c: Horizontal(g42)
    c: Coincident(g43,g9)
    c: Coincident(g43,g23)
    c: Horizontal(g43)
    c: Coincident(g44,g10)
    c: Coincident(g44,g22)
    c: Horizontal(g44)
    c: Coincident(g45,g10)
    c: Coincident(g45,g22)
    c: Horizontal(g45)
    c: Coincident(g46,g11)
    c: Coincident(g46,g21)
    c: Horizontal(g46)
    c: Coincident(g47,g11)
    c: Coincident(g47,g21)
    c: Horizontal(g47)
FEATURE [Sketcher::SketchObject] Sketch031
  FullyConstrained = true
  Placement = pos=(117,19,0) rot=(0.57735,0.57735,0.57735;2.0944rad)
  sketch-geometry (24):
    g0: ArcOfCircle CenterX=-49.19 CenterY=67.75 CenterZ=0 NormalX=0 NormalY=0 NormalZ=1 AngleXU=0 Radius=1.5 StartAngle=1.5708 EndAngle=4.71239
    g1: ArcOfCircle CenterX=-49.19 CenterY=62 CenterZ=0 NormalX=0 NormalY=0 NormalZ=1 AngleXU=0 Radius=1.5 StartAngle=1.5708 EndAngle=4.71239
    g2: ArcOfCircle CenterX=-49.19 CenterY=56.25 CenterZ=0 NormalX=0 NormalY=0 NormalZ=1 AngleXU=0 Radius=1.5 StartAngle=1.5708 EndAngle=4.71239
    g3: ArcOfCircle CenterX=-49.19 CenterY=50.5 CenterZ=0 NormalX=0 NormalY=0 NormalZ=1 AngleXU=0 Radius=1.5 StartAngle=1.5708 EndAngle=4.71239
    g4: ArcOfCircle CenterX=-49.19 CenterY=44.75 CenterZ=0 NormalX=0 NormalY=0 NormalZ=1 AngleXU=0 Radius=1.5 StartAngle=1.5708 EndAngle=4.71239
    g5: ArcOfCircle CenterX=-49.19 CenterY=39 CenterZ=0 NormalX=0 NormalY=0 NormalZ=1 AngleXU=0 Radius=1.5 StartAngle=1.5708 EndAngle=4.71239
    g6: ArcOfCircle CenterX=-49.19 CenterY=33 CenterZ=0 NormalX=0 NormalY=0 NormalZ=1 AngleXU=0 Radius=1.5 StartAngle=1.5708 EndAngle=4.71239
    g7: ArcOfCircle CenterX=-49.19 CenterY=27.25 CenterZ=0 NormalX=0 NormalY=0 NormalZ=1 AngleXU=0 Radius=1.5 StartAngle=1.5708 EndAngle=4.71239
    g8: ArcOfCircle CenterX=-49.19 CenterY=21.5 CenterZ=0 NormalX=0 NormalY=0 NormalZ=1 AngleXU=0 Radius=1.5 StartAngle=1.5708 EndAngle=4.71239
    g9: ArcOfCircle CenterX=-49.19 CenterY=15.75 CenterZ=0 NormalX=0 NormalY=0 NormalZ=1 AngleXU=0 Radius=1.5 StartAngle=1.5708 EndAngle=4.71239
    g10: ArcOfCircle CenterX=-49.19 CenterY=10 CenterZ=0 NormalX=0 NormalY=0 NormalZ=1 AngleXU=0 Radius=1.5 StartAngle=1.5708 EndAngle=4.71239
    g11: ArcOfCircle CenterX=-49.19 CenterY=4.25 CenterZ=0 NormalX=0 NormalY=0 NormalZ=1 AngleXU=0 Radius=1.5 StartAngle=1.5708 EndAngle=4.71239
    g12: LineSegment StartX=-49.19 StartY=69.25 StartZ=0 EndX=-49.19 EndY=66.25 EndZ=0
    g13: LineSegment StartX=-49.19 StartY=63.5 StartZ=0 EndX=-49.19 EndY=60.5 EndZ=0
    g14: LineSegment StartX=-49.19 StartY=57.75 StartZ=0 EndX=-49.19 EndY=54.75 EndZ=0
    g15: LineSegment StartX=-49.19 StartY=52 StartZ=0 EndX=-49.19 EndY=49 EndZ=0
    g16: LineSegment StartX=-49.19 StartY=46.25 StartZ=0 EndX=-49.19 EndY=43.25 EndZ=0
    g17: LineSegment StartX=-49.19 StartY=40.5 StartZ=0 EndX=-49.19 EndY=37.5 EndZ=0
    g18: LineSegment StartX=-49.19 StartY=34.5 StartZ=0 EndX=-49.19 EndY=31.5 EndZ=0
    g19: LineSegment StartX=-49.19 StartY=28.75 StartZ=0 EndX=-49.19 EndY=25.75 EndZ=0
    g20: LineSegment StartX=-49.19 StartY=23 StartZ=0 EndX=-49.19 EndY=20 EndZ=0
    g21: LineSegment StartX=-49.19 StartY=17.25 StartZ=0 EndX=-49.19 EndY=14.25 EndZ=0
    g22: LineSegment StartX=-49.19 StartY=11.5 StartZ=0 EndX=-49.19 EndY=8.5 EndZ=0
    g23: LineSegment StartX=-49.19 StartY=5.75 StartZ=0 EndX=-49.19 EndY=2.75 EndZ=0
  constraints (48):
    c: Block(g0)
    c: Block(g1)
    c: Block(g2)
    c: Block(g3)
    c: Block(g4)
    c: Block(g5)
    c: Block(g6)
    c: Block(g7)
    c: Block(g8)
    c: Block(g9)
    c: Block(g10)
    c: Block(g11)
    c: Coincident(g12,g0)
    c: Coincident(g12,g0)
    c: Vertical(g12)
    c: Vertical(g13)
    c: Coincident(g13,g1)
    c: Vertical(g14)
    c: Coincident(g14,g2)
    c: Vertical(g15)
    c: Coincident(g15,g3)
    c: Vertical(g16)
    c: Coincident(g16,g4)
    c: Vertical(g17)
    c: Coincident(g17,g5)
    c: Vertical(g18)
    c: Coincident(g18,g6)
    c: Vertical(g19)
    c: Coincident(g19,g7)
    c: Vertical(g20)
    c: Coincident(g20,g8)
    c: Vertical(g21)
    c: Coincident(g21,g9)
    c: Vertical(g22)
    c: Coincident(g22,g10)
    c: Vertical(g23)
    c: Coincident(g23,g11)
    c: Block(g23)
    c: Block(g22)
    c: Block(g21)
    c: Block(g20)
    c: Block(g13)
    c: Block(g14)
    c: Block(g15)
    c: Block(g16)
    c: Block(g17)
    c: Block(g18)
    c: Block(g19)
FEATURE [Part::Extrusion] Extrude022
  Base = -> Sketch030
  Dir = (1,-2e-16,2e-16)
  DirMode = 2
  FaceMakerClass = Part::FaceMakerBullseye
  LengthFwd = 19
  LengthRev = 0
  Placement = pos=(-19,0,0) rot=(0,0,1;0rad)
  Solid = true
  Symmetric = false
FEATURE [Part::Fillet] Fillet022
  Base = -> Extrude022
  Edges = 24 edges r=1.49: [Edge6,Edge11,Edge18,Edge23,Edge30,Edge35,Edge42,Edge47,Edge54,Edge59,Edge66,Edge71,Edge78,Edge83,Edge90,Edge95,Edge102,Edge107,Edge114,Edge119,Edge126,Edge131,Edge138,Edge143]
FEATURE [Part::Cut] Cut020  label="top010"
  Base = -> Cut019
  Tool = -> Fillet022
FEATURE [Sketcher::SketchObject] Sketch032
  FullyConstrained = true
  Placement = pos=(117,19,0) rot=(0.57735,0.57735,0.57735;2.0944rad)
  sketch-geometry (48):
    g0: LineSegment StartX=-49.19 StartY=69.25 StartZ=0 EndX=-49.19 EndY=66.25 EndZ=0
    g1: LineSegment StartX=-49.19 StartY=63.5 StartZ=0 EndX=-49.19 EndY=60.5 EndZ=0
    g2: LineSegment StartX=-49.19 StartY=57.75 StartZ=0 EndX=-49.19 EndY=54.75 EndZ=0
    g3: LineSegment StartX=-49.19 StartY=52 StartZ=0 EndX=-49.19 EndY=49 EndZ=0
    g4: LineSegment StartX=-49.19 StartY=46.25 StartZ=0 EndX=-49.19 EndY=43.25 EndZ=0
    g5: LineSegment StartX=-49.19 StartY=40.5 StartZ=0 EndX=-49.19 EndY=37.5 EndZ=0
    g6: LineSegment StartX=-49.19 StartY=34.5 StartZ=0 EndX=-49.19 EndY=31.5 EndZ=0
    g7: LineSegment StartX=-49.19 StartY=28.75 StartZ=0 EndX=-49.19 EndY=25.75 EndZ=0
    g8: LineSegment StartX=-49.19 StartY=23 StartZ=0 EndX=-49.19 EndY=20 EndZ=0
    g9: LineSegment StartX=-49.19 StartY=17.25 StartZ=0 EndX=-49.19 EndY=14.25 EndZ=0
    g10: LineSegment StartX=-49.19 StartY=11.5 StartZ=0 EndX=-49.19 EndY=8.5 EndZ=0
    g11: LineSegment StartX=-49.19 StartY=5.75 StartZ=0 EndX=-49.19 EndY=2.75 EndZ=0
    g12: ArcOfCircle CenterX=-1.5 CenterY=67.75 CenterZ=0 NormalX=0 NormalY=0 NormalZ=1 AngleXU=0 Radius=1.5 StartAngle=4.71239 EndAngle=7.85398
    g13: ArcOfCircle CenterX=-1.5 CenterY=62 CenterZ=0 NormalX=0 NormalY=0 NormalZ=1 AngleXU=0 Radius=1.5 StartAngle=4.71239 EndAngle=7.85398
    g14: ArcOfCircle CenterX=-1.5 CenterY=56.25 CenterZ=0 NormalX=0 NormalY=0 NormalZ=1 AngleXU=0 Radius=1.5 StartAngle=4.71239 EndAngle=7.85398
    g15: ArcOfCircle CenterX=-11.49 CenterY=50.5 CenterZ=0 NormalX=0 NormalY=0 NormalZ=1 AngleXU=0 Radius=1.5 StartAngle=4.71239 EndAngle=7.85398
    g16: ArcOfCircle CenterX=-16.28 CenterY=44.75 CenterZ=0 NormalX=0 NormalY=0 NormalZ=1 AngleXU=0 Radius=1.5 StartAngle=4.71239 EndAngle=7.85398
    g17: ArcOfCircle CenterX=-18.2337 CenterY=39 CenterZ=0 NormalX=0 NormalY=0 NormalZ=1 AngleXU=0 Radius=1.5 StartAngle=4.71485 EndAngle=7.85398
    g18: ArcOfCircle CenterX=-16.2837 CenterY=27.25 CenterZ=0 NormalX=0 NormalY=0 NormalZ=1 AngleXU=0 Radius=1.5 StartAngle=4.71485 EndAngle=7.85398
    g19: ArcOfCircle CenterX=-18.2337 CenterY=33 CenterZ=0 NormalX=0 NormalY=0 NormalZ=1 AngleXU=0 Radius=1.5 StartAngle=4.71485 EndAngle=7.85398
    g20: ArcOfCircle CenterX=-11.49 CenterY=21.5 CenterZ=0 NormalX=0 NormalY=0 NormalZ=1 AngleXU=0 Radius=1.5 StartAngle=4.71239 EndAngle=7.85398
    g21: ArcOfCircle CenterX=-1.5 CenterY=4.25 CenterZ=0 NormalX=0 NormalY=0 NormalZ=1 AngleXU=0 Radius=1.5 StartAngle=4.71239 EndAngle=7.85398
    g22: ArcOfCircle CenterX=-1.5 CenterY=10 CenterZ=0 NormalX=0 NormalY=0 NormalZ=1 AngleXU=0 Radius=1.5 StartAngle=4.71239 EndAngle=7.85398
    g23: ArcOfCircle CenterX=-1.5 CenterY=15.75 CenterZ=0 NormalX=0 NormalY=0 NormalZ=1 AngleXU=0 Radius=1.5 StartAngle=4.71239 EndAngle=7.85398
    g24: LineSegment StartX=-49.19 StartY=69.25 StartZ=0 EndX=-1.5 EndY=69.25 EndZ=0
    g25: LineSegment StartX=-49.19 StartY=66.25 StartZ=0 EndX=-1.5 EndY=66.25 EndZ=0
    g26: LineSegment StartX=-49.19 StartY=63.5 StartZ=0 EndX=-1.5 EndY=63.5 EndZ=0
    g27: LineSegment StartX=-49.19 StartY=60.5 StartZ=0 EndX=-1.5 EndY=60.5 EndZ=0
    g28: LineSegment StartX=-49.19 StartY=57.75 StartZ=0 EndX=-1.5 EndY=57.75 EndZ=0
    g29: LineSegment StartX=-49.19 StartY=54.75 StartZ=0 EndX=-1.5 EndY=54.75 EndZ=0
    g30: LineSegment StartX=-49.19 StartY=52 StartZ=0 EndX=-11.49 EndY=52 EndZ=0
    g31: LineSegment StartX=-49.19 StartY=49 StartZ=0 EndX=-11.49 EndY=49 EndZ=0
    g32: LineSegment StartX=-49.19 StartY=46.25 StartZ=0 EndX=-16.28 EndY=46.25 EndZ=0
    g33: LineSegment StartX=-49.19 StartY=43.25 StartZ=0 EndX=-16.28 EndY=43.25 EndZ=0
    g34: LineSegment StartX=-49.19 StartY=40.5 StartZ=0 EndX=-18.2337 EndY=40.5 EndZ=0
    g35: LineSegment StartX=-49.19 StartY=37.5 StartZ=0 EndX=-18.23 EndY=37.5 EndZ=0
    g36: LineSegment StartX=-49.19 StartY=34.5 StartZ=0 EndX=-18.2337 EndY=34.5 EndZ=0
    g37: LineSegment StartX=-49.19 StartY=31.5 StartZ=0 EndX=-18.23 EndY=31.5 EndZ=0
    g38: LineSegment StartX=-49.19 StartY=28.75 StartZ=0 EndX=-16.2837 EndY=28.75 EndZ=0
    g39: LineSegment StartX=-49.19 StartY=25.75 StartZ=0 EndX=-16.28 EndY=25.75 EndZ=0
    g40: LineSegment StartX=-49.19 StartY=23 StartZ=0 EndX=-11.49 EndY=23 EndZ=0
    g41: LineSegment StartX=-49.19 StartY=20 StartZ=0 EndX=-11.49 EndY=20 EndZ=0
    g42: LineSegment StartX=-49.19 StartY=17.25 StartZ=0 EndX=-1.5 EndY=17.25 EndZ=0
    g43: LineSegment StartX=-49.19 StartY=14.25 StartZ=0 EndX=-1.5 EndY=14.25 EndZ=0
    g44: LineSegment StartX=-49.19 StartY=11.5 StartZ=0 EndX=-1.5 EndY=11.5 EndZ=0
    g45: LineSegment StartX=-49.19 StartY=8.5 StartZ=0 EndX=-1.5 EndY=8.5 EndZ=0
    g46: LineSegment StartX=-49.19 StartY=5.75 StartZ=0 EndX=-1.5 EndY=5.75 EndZ=0
    g47: LineSegment StartX=-49.19 StartY=2.75 StartZ=0 EndX=-1.5 EndY=2.75 EndZ=0
  constraints (120):
    c: Vertical(g0)
    c: Distance(g0) = 3
    c: Block(g0)
    c: Vertical(g1)
    c: Distance(g1) = 3
    c: Vertical(g2)
    c: Equal(g0,g2) = 3
    c: Block(g2)
    c: Vertical(g3)
    c: Equal(g1,g3) = 3
    c: Vertical(g4)
    c: Equal(g0,g4) = 3
    c: Block(g4)
    c: Vertical(g5)
    c: Equal(g1,g5) = 3
    c: Vertical(g6)
    c: Equal(g0,g6) = 3
    c: Block(g6)
    c: Vertical(g7)
    c: Equal(g1,g7) = 3
    c: Vertical(g8)
    c: Equal(g0,g8) = 3
    c: Block(g8)
    c: Vertical(g9)
    c: Equal(g1,g9) = 3
    c: Vertical(g10)
    c: Equal(g0,g10) = 3
    c: Block(g10)
    c: Vertical(g11)
    c: Equal(g1,g11) = 3
    c: Block(g12)
    c: Block(g13)
    c: Block(g14)
    c: Block(g15)
    c: Block(g16)
    c: Block(g17)
    c: Block(g18)
    c: Block(g19)
    c: Block(g20)
    c: Block(g21)
    c: Block(g22)
    c: Block(g23)
    c: Block(g11)
    c: Block(g9)
    c: Block(g7)
    c: Block(g5)
    c: Block(g3)
    c: Block(g1)
    c: Coincident(g24,g0)
    c: Coincident(g24,g12)
    c: Horizontal(g24)
    c: Coincident(g25,g0)
    c: Coincident(g25,g12)
    c: Horizontal(g25)
    c: Coincident(g26,g1)
    c: Coincident(g26,g13)
    c: Horizontal(g26)
    c: Coincident(g27,g1)
    c: Coincident(g27,g13)
    c: Horizontal(g27)
    c: Coincident(g28,g2)
    c: Coincident(g28,g14)
    c: Horizontal(g28)
    c: Coincident(g29,g2)
    c: Coincident(g29,g14)
    c: Horizontal(g29)
    c: Coincident(g30,g3)
    c: Coincident(g30,g15)
    c: Horizontal(g30)
    c: Coincident(g31,g3)
    c: Coincident(g31,g15)
    c: Horizontal(g31)
    c: Coincident(g32,g4)
    c: Coincident(g32,g16)
    c: Horizontal(g32)
    c: Coincident(g33,g4)
    c: Coincident(g33,g16)
    c: Horizontal(g33)
    c: Coincident(g34,g5)
    c: Coincident(g34,g17)
    c: Horizontal(g34)
    c: Coincident(g35,g5)
    c: Coincident(g35,g17)
    c: Horizontal(g35)
    c: Coincident(g36,g6)
    c: Coincident(g36,g19)
    c: Horizontal(g36)
    c: Coincident(g37,g6)
    c: Coincident(g37,g19)
    c: Horizontal(g37)
    c: Coincident(g38,g7)
    c: Coincident(g38,g18)
    c: Horizontal(g38)
    c: Coincident(g39,g7)
    c: Coincident(g39,g18)
    c: Horizontal(g39)
    c: Coincident(g40,g8)
    c: Coincident(g40,g20)
    c: Horizontal(g40)
    c: Coincident(g41,g8)
    c: Coincident(g41,g20)
    c: Horizontal(g41)
    c: Coincident(g42,g9)
    c: Coincident(g42,g23)
    c: Horizontal(g42)
    c: Coincident(g43,g9)
    c: Coincident(g43,g23)
    c: Horizontal(g43)
    c: Coincident(g44,g10)
    c: Coincident(g44,g22)
    c: Horizontal(g44)
    c: Coincident(g45,g10)
    c: Coincident(g45,g22)
    c: Horizontal(g45)
    c: Coincident(g46,g11)
    c: Coincident(g46,g21)
    c: Horizontal(g46)
    c: Coincident(g47,g11)
    c: Coincident(g47,g21)
    c: Horizontal(g47)
FEATURE [Part::Extrusion] Extrude023
  Base = -> Sketch032
  Dir = (1,-2e-16,2e-16)
  DirMode = 2
  FaceMakerClass = Part::FaceMakerBullseye
  LengthFwd = 19
  LengthRev = 0
  Placement = pos=(-19,0,0) rot=(0,0,1;0rad)
  Solid = true
  Symmetric = false
FEATURE [Part::Fillet] Fillet023
  Base = -> Extrude023
  Edges = <same value as first occurrence — deduplicated (x6 in doc)>
  Placement = pos=(0,0.05,0) rot=(0,0,1;0rad)
FEATURE [Part::Cut] Cut014  label="bottom003"
  Base = -> Cut007
  Tool = -> Fusion047
FEATURE [Part::Cut] Cut021  label="bottom004"
  Base = -> Cut014
  Tool = -> Fillet023
FEATURE [Sketcher::SketchObject] Sketch033
  FullyConstrained = true
  Placement = pos=(117,19,0) rot=(0.57735,0.57735,0.57735;2.0944rad)
  sketch-geometry (8):
    g0: LineSegment StartX=-49.19 StartY=69.25 StartZ=0 EndX=-49.19 EndY=66.25 EndZ=0
    g1: LineSegment StartX=-49.19 StartY=5.75 StartZ=0 EndX=-49.19 EndY=2.75 EndZ=0
    g2: ArcOfCircle CenterX=-1.5 CenterY=67.75 CenterZ=0 NormalX=0 NormalY=0 NormalZ=1 AngleXU=0 Radius=1.5 StartAngle=4.71239 EndAngle=7.85398
    g3: ArcOfCircle CenterX=-1.5 CenterY=4.25 CenterZ=0 NormalX=0 NormalY=0 NormalZ=1 AngleXU=0 Radius=1.5 StartAngle=4.71239 EndAngle=7.85398
    g4: LineSegment StartX=-49.19 StartY=69.25 StartZ=0 EndX=-1.5 EndY=69.25 EndZ=0
    g5: LineSegment StartX=-49.19 StartY=66.25 StartZ=0 EndX=-1.5 EndY=66.25 EndZ=0
    g6: LineSegment StartX=-49.19 StartY=5.75 StartZ=0 EndX=-1.5 EndY=5.75 EndZ=0
    g7: LineSegment StartX=-49.19 StartY=2.75 StartZ=0 EndX=-1.5 EndY=2.75 EndZ=0
  constraints (19):
    c: Vertical(g0)
    c: Distance(g0) = 3
    c: Block(g0)
    c: Vertical(g1)
    c: Block(g2)
    c: Block(g3)
    c: Block(g1)
    c: Coincident(g4,g0)
    c: Coincident(g4,g2)
    c: Horizontal(g4)
    c: Coincident(g5,g0)
    c: Coincident(g5,g2)
    c: Horizontal(g5)
    c: Coincident(g6,g1)
    c: Coincident(g6,g3)
    c: Horizontal(g6)
    c: Coincident(g7,g1)
    c: Coincident(g7,g3)
    c: Horizontal(g7)
FEATURE [Sketcher::SketchObject] Sketch034
  FullyConstrained = true
  Placement = pos=(117,19,0) rot=(0.57735,0.57735,0.57735;2.0944rad)
  sketch-geometry (8):
    g0: LineSegment StartX=-49.19 StartY=63.5 StartZ=0 EndX=-49.19 EndY=60.5 EndZ=0
    g1: LineSegment StartX=-49.19 StartY=11.5 StartZ=0 EndX=-49.19 EndY=8.5 EndZ=0
    g2: ArcOfCircle CenterX=-1.5 CenterY=62 CenterZ=0 NormalX=0 NormalY=0 NormalZ=1 AngleXU=0 Radius=1.5 StartAngle=4.71239 EndAngle=7.85398
    g3: ArcOfCircle CenterX=-1.5 CenterY=10 CenterZ=0 NormalX=0 NormalY=0 NormalZ=1 AngleXU=0 Radius=1.5 StartAngle=4.71239 EndAngle=7.85398
    g4: LineSegment StartX=-49.19 StartY=63.5 StartZ=0 EndX=-1.5 EndY=63.5 EndZ=0
    g5: LineSegment StartX=-49.19 StartY=60.5 StartZ=0 EndX=-1.5 EndY=60.5 EndZ=0
    g6: LineSegment StartX=-49.19 StartY=11.5 StartZ=0 EndX=-1.5 EndY=11.5 EndZ=0
    g7: LineSegment StartX=-49.19 StartY=8.5 StartZ=0 EndX=-1.5 EndY=8.5 EndZ=0
  constraints (19):
    c: Vertical(g0)
    c: Distance(g0) = 3
    c: Vertical(g1)
    c: Block(g1)
    c: Block(g2)
    c: Block(g3)
    c: Block(g0)
    c: Coincident(g4,g0)
    c: Coincident(g4,g2)
    c: Horizontal(g4)
    c: Coincident(g5,g0)
    c: Coincident(g5,g2)
    c: Horizontal(g5)
    c: Coincident(g6,g1)
    c: Coincident(g6,g3)
    c: Horizontal(g6)
    c: Coincident(g7,g1)
    c: Coincident(g7,g3)
    c: Horizontal(g7)
FEATURE [Part::Extrusion] Extrude024
  Base = -> Sketch033
  Dir = (1,0,0)
  DirMode = 2
  FaceMakerClass = Part::FaceMakerBullseye
  LengthFwd = 10
  LengthRev = 0
  Solid = true
  Symmetric = false
FEATURE [Part::Extrusion] Extrude025
  Base = -> Sketch034
  Dir = (1,0,0)
  DirMode = 2
  FaceMakerClass = Part::FaceMakerBullseye
  LengthFwd = 10
  LengthRev = 0
  Solid = true
  Symmetric = false
FEATURE [Part::Fillet] Fillet024  label="removeFromtMoreFrontCaseScrewRetainers"
  Base = -> Extrude024
  Edges = 4 edges r=1.49: [Edge6,Edge11,Edge18,Edge23]
  Placement = pos=(-11,0,0) rot=(0,0,1;0rad)
FEATURE [Part::Fillet] Fillet025  label="removeFromtMoreFrontCaseScrewRetainers001"
  Base = -> Extrude025
  Edges = 4 edges r=1.49: [Edge6,Edge11,Edge18,Edge23]
  Placement = pos=(-19,0,0) rot=(0,0,1;0rad)
FEATURE [Part::Cut] Cut022
  Base = -> Cut015
  Tool = -> Fillet025
FEATURE [Part::Cut] Cut023  label="screwRetainers"
  Base = -> Cut022
  Tool = -> Fillet024
FEATURE [Part::MultiFuse] Fusion056  label="bottom005"
  Shapes = -> [Fusion044,Cut021]
FEATURE [Part::MultiFuse] Fusion057  label="casePillars001"
  Shapes = -> [Cut016,Fusion052]
FEATURE [Part::MultiFuse] Fusion058  label="bottom006"
  Shapes = -> [Fusion056,Cut023]
FEATURE [Part::MultiFuse] Fusion059  label="bottom007"
  Shapes = -> [Fusion058,Fillet005]
FEATURE [Part::MultiFuse] Fusion060  label="bottom008"
  Shapes = -> [Fusion059,Fusion]
FEATURE [Part::MultiFuse] Fusion061  label="top011"
  Shapes = -> [Cut006,Cut020]
FEATURE [Part::MultiFuse] Fusion062  label="top012"
  Shapes = -> [Fusion057,Fusion061]
FEATURE [Sketcher::SketchObject] Sketch035  label="topSketch007"
  FullyConstrained = true
  sketch-geometry (6):
    g0: LineSegment StartX=19 StartY=38 StartZ=0 EndX=117 EndY=38 EndZ=0
    g1: ArcOfCircle CenterX=19 CenterY=19 CenterZ=0 NormalX=0 NormalY=0 NormalZ=1 AngleXU=0 Radius=19 StartAngle=1.5708 EndAngle=3.14159
    g2: LineSegment StartX=117 StartY=38 StartZ=0 EndX=117 EndY=19 EndZ=0
    g3: LineSegment StartX=98 StartY=1.0161e-12 StartZ=0 EndX=5.22862e-06 EndY=1.0161e-12 EndZ=0
    g4: LineSegment StartX=5.22862e-06 StartY=19 StartZ=0 EndX=5.22862e-06 EndY=1.0161e-12 EndZ=0
    g5: ArcOfCircle CenterX=98 CenterY=19 CenterZ=0 NormalX=0 NormalY=0 NormalZ=1 AngleXU=0 Radius=19 StartAngle=4.71239 EndAngle=6.28319
  constraints (16):
    c: Horizontal(g0)
    c: Distance(g0) = 98
    c: Coincident(g1,g0)
    c: Block(g1)
    c: Coincident(g2,g0)
    c: Vertical(g2)
    c: Distance(g2) = 19
    c: Horizontal(g3)
    c: Coincident(g4,g1)
    c: Vertical(g4)
    c: Coincident(g3,g4)
    c: Block(g3)
    c: Coincident(g5,g2)
    c: Coincident(g5,g3)
    c: Block(g0)
    c: Block(g5)
FEATURE [Part::Extrusion] Extrude026  label="sideA001"
  Base = -> Sketch035
  Dir = (0,0,1)
  DirMode = 2
  FaceMakerClass = Part::FaceMakerBullseye
  LengthFwd = 3
  LengthRev = 0
  Placement = pos=(0,0,-2.7) rot=(0,0,1;0rad)
  Solid = true
  Symmetric = false
FEATURE [Sketcher::SketchObject] Sketch036  label="topSketch008"
  FullyConstrained = true
  sketch-geometry (6):
    g0: LineSegment StartX=19 StartY=38 StartZ=0 EndX=117 EndY=38 EndZ=0
    g1: ArcOfCircle CenterX=19 CenterY=19 CenterZ=0 NormalX=0 NormalY=0 NormalZ=1 AngleXU=0 Radius=19 StartAngle=1.5708 EndAngle=3.14159
    g2: LineSegment StartX=117 StartY=38 StartZ=0 EndX=117 EndY=19 EndZ=0
    g3: LineSegment StartX=98 StartY=1.0161e-12 StartZ=0 EndX=5.22862e-06 EndY=1.0161e-12 EndZ=0
    g4: LineSegment StartX=5.22862e-06 StartY=19 StartZ=0 EndX=5.22862e-06 EndY=1.0161e-12 EndZ=0
    g5: ArcOfCircle CenterX=98 CenterY=19 CenterZ=0 NormalX=0 NormalY=0 NormalZ=1 AngleXU=0 Radius=19 StartAngle=4.71239 EndAngle=6.28319
  constraints (16):
    c: Horizontal(g0)
    c: Distance(g0) = 98
    c: Coincident(g1,g0)
    c: Block(g1)
    c: Coincident(g2,g0)
    c: Vertical(g2)
    c: Distance(g2) = 19
    c: Horizontal(g3)
    c: Coincident(g4,g1)
    c: Vertical(g4)
    c: Coincident(g3,g4)
    c: Block(g3)
    c: Coincident(g5,g2)
    c: Coincident(g5,g3)
    c: Block(g0)
    c: Block(g5)
FEATURE [Part::Extrusion] Extrude027  label="sideB001"
  Base = -> Sketch036
  Dir = (0,0,1)
  DirMode = 2
  FaceMakerClass = Part::FaceMakerBullseye
  LengthFwd = 3
  LengthRev = 0
  Placement = pos=(0,0,71.7) rot=(0,0,1;0rad)
  Solid = true
  Symmetric = false
FEATURE [Part::MultiFuse] Fusion064  label="removeFromBottom"
  Shapes = -> [Extrude026,Extrude027]
FEATURE [Part::Cut] Cut024  label="bottom009"
  Base = -> Fusion060
  Tool = -> Fusion064
FEATURE [Sketcher::SketchObject] Sketch037  label="topSketch009"
  FullyConstrained = true
  sketch-geometry (6):
    g0: ArcOfCircle CenterX=19 CenterY=19 CenterZ=0 NormalX=0 NormalY=0 NormalZ=1 AngleXU=0 Radius=19 StartAngle=1.5708 EndAngle=3.14159
    g1: LineSegment StartX=5.22862e-06 StartY=19 StartZ=0 EndX=5.22862e-06 EndY=1.19904e-11 EndZ=0
    g2: LineSegment StartX=19 StartY=38 StartZ=0 EndX=124 EndY=38 EndZ=0
    g3: LineSegment StartX=5.22862e-06 StartY=1.19904e-11 StartZ=0 EndX=105 EndY=1.19904e-11 EndZ=0
    g4: ArcOfCircle CenterX=105 CenterY=19 CenterZ=0 NormalX=0 NormalY=0 NormalZ=1 AngleXU=0 Radius=19 StartAngle=4.71239 EndAngle=6.28319
    g5: LineSegment StartX=124 StartY=38 StartZ=0 EndX=124 EndY=19 EndZ=0
  constraints (16):
    c: Block(g0)
    c: Coincident(g1,g0)
    c: Vertical(g1)
    c: Horizontal(g2)
    c: Distance(g2) = 105
    c: Coincident(g2,g0)
    c: Distance(g1) = 19
    c: Coincident(g3,g1)
    c: Horizontal(g3)
    c: Distance(g3) = 105
    c: Block(g4)
    c: Coincident(g4,g3)
    c: Coincident(g5,g2)
    c: Coincident(g5,g4)
    c: Vertical(g5)
    c: Distance(g5) = 19
FEATURE [Part::Extrusion] Extrude028  label="sideB"
  Base = -> Sketch037
  Dir = (0,0,1)
  DirMode = 2
  FaceMakerClass = Part::FaceMakerBullseye
  LengthFwd = 3
  LengthRev = 0
  Placement = pos=(0,0,72) rot=(0,0,1;0rad)
  Solid = true
  Symmetric = false
FEATURE [Sketcher::SketchObject] Sketch038  label="topSketch010"
  FullyConstrained = true
  sketch-geometry (22):
    g0: LineSegment StartX=5.21097e-06 StartY=3 StartZ=0 EndX=5.21097e-06 EndY=19 EndZ=0
    g1: ArcOfCircle CenterX=19 CenterY=19 CenterZ=0 NormalX=0 NormalY=0 NormalZ=1 AngleXU=0 Radius=19 StartAngle=1.5708 EndAngle=3.14159
    g2: ArcOfCircle CenterX=19 CenterY=19 CenterZ=0 NormalX=0 NormalY=0 NormalZ=1 AngleXU=0 Radius=16 StartAngle=1.5708 EndAngle=3.14159
    g3: LineSegment StartX=114 StartY=35 StartZ=0 EndX=19 EndY=35 EndZ=0
    g4: LineSegment StartX=5.21097e-06 StartY=3 StartZ=0 EndX=5.21097e-06 EndY=0 EndZ=0
    g5: LineSegment StartX=3 StartY=0 StartZ=0 EndX=5.21097e-06 EndY=0 EndZ=0
    g6: LineSegment StartX=3 StartY=19 StartZ=0 EndX=3 EndY=0 EndZ=0
    g7: LineSegment StartX=19 StartY=38 StartZ=0 EndX=124 EndY=38 EndZ=0
    g8: Circle CenterX=119 CenterY=35 CenterZ=0 NormalX=0 NormalY=0 NormalZ=1 AngleXU=0 Radius=1
    g9: Circle CenterX=121 CenterY=35 CenterZ=0 NormalX=0 NormalY=0 NormalZ=1 AngleXU=0 Radius=1
    g10: Circle CenterX=121 CenterY=33 CenterZ=0 NormalX=0 NormalY=0 NormalZ=1 AngleXU=0 Radius=1
    g11: BSplineCurve PolesCount=3 KnotsCount=2 Degree=2 IsPeriodic=0
    g12: GeomPoint X=119 Y=35 Z=0
    g13: GeomPoint X=121 Y=33 Z=0
    g14: LineSegment StartX=119 StartY=35 StartZ=0 EndX=114 EndY=35 EndZ=0
    g15: ArcOfCircle CenterX=105 CenterY=19 CenterZ=0 NormalX=0 NormalY=0 NormalZ=1 AngleXU=0 Radius=16 StartAngle=5.60905 EndAngle=6.28319
    g16: LineSegment StartX=121 StartY=33 StartZ=0 EndX=121 EndY=19 EndZ=0
    g17: LineSegment StartX=117.5 StartY=9.01251 StartZ=0 EndX=121.163 EndY=9.0125 EndZ=0
    g18: ArcOfCircle CenterX=105 CenterY=19 CenterZ=0 NormalX=0 NormalY=0 NormalZ=1 AngleXU=0 Radius=20.6155 StartAngle=5.7297 EndAngle=6.28319
    g19: LineSegment StartX=121.163 StartY=9.0125 StartZ=0 EndX=122.538 EndY=8.16329 EndZ=0
    g20: LineSegment StartX=124 StartY=38 StartZ=0 EndX=125.616 EndY=38 EndZ=0
    g21: LineSegment StartX=125.616 StartY=19 StartZ=0 EndX=125.616 EndY=38 EndZ=0
  constraints (49):
    c: Vertical(g0)
    c: Block(g0)
    c: Coincident(g1,g0)
    c: Block(g1)
    c: Coincident(g2,g1)
    c: Block(g2)
    c: Coincident(g3,g2)
    c: Horizontal(g3)
    c: Tangent(g3,g2)
    c: Coincident(g4,g0)
    c: Distance(g4) = 3
    c: Vertical(g4)
    c: Coincident(g5,g4)
    c: Horizontal(g5)
    c: Coincident(g6,g2)
    c: Coincident(g6,g5)
    c: Vertical(g6)
    c: Horizontal(g7)
    c: Distance(g7) = 105
    c: Coincident(g7,g1)
    c: Block(g3)
    c: Weight(g8) = 1
    c: Equal(g8,g9)
    c: Equal(g8,g10)
    c: InternalAlignment(g8,g11)
    c: InternalAlignment(g9,g11)
    c: InternalAlignment(g10,g11)
    c: InternalAlignment(g12,g11)
    c: InternalAlignment(g13,g11)
    c: Block(g11)
    c: Coincident(g14,g11)
    c: Coincident(g14,g3)
    c: Horizontal(g14)
    c: Block(g15)
    c: Coincident(g16,g11)
    c: Coincident(g16,g15)
    c: Vertical(g16)
    c: Distance(g16) = 14
    c: Coincident(g17,g15)
    c: Block(g18)
    c: Coincident(g19,g18)
    c: Coincident(g20,g7)
    c: Horizontal(g20)
    c: Vertical(g21)
    c: Coincident(g20,g21)
    c: Block(g20)
    c: Block(g21)
    c: Block(g19)
    c: Block(g17)
FEATURE [Part::Extrusion] Extrude029
  Base = -> Sketch038
  Dir = (0,0,1)
  DirMode = 2
  FaceMakerClass = Part::FaceMakerBullseye
  LengthFwd = 72
  LengthRev = 0
  Solid = true
  Symmetric = false
FEATURE [Part::Feature] Face085
  shape: bbox 4.8 x 25.5 x 2e-07 mm, 1 faces, 0 solids (baked)
FEATURE [Part::Revolution] Revolve089  label="moreFrontCaseScrewPost003"
  Angle = 360
  Axis = (0,1,0)
  Base = (0,0,0)
  FaceMakerClass = Part::FaceMakerBullseye
  Placement = pos=(109.5,4.5,3.5) rot=(0,0,1;0rad)
  Solid = false
  Source = -> Face085
  Symmetric = false
FEATURE [Part::Feature] Face086
  shape: bbox 4.8 x 25.5 x 2e-07 mm, 1 faces, 0 solids (baked)
FEATURE [Part::Revolution] Revolve090  label="moreFrontCaseScrewPost004"
  Angle = 360
  Axis = (0,1,0)
  Base = (0,0,0)
  FaceMakerClass = Part::FaceMakerBullseye
  Placement = pos=(109.5,4.5,68.5) rot=(0,0,1;0rad)
  Solid = false
  Source = -> Face086
  Symmetric = false
FEATURE [Part::Fillet] Fillet026  label="top013"
  Base = -> Extrude029
  Edges = 1 edges r=2: [Edge35]
FEATURE [Sketcher::SketchObject] Sketch039
  FullyConstrained = true
  sketch-geometry (7):
    g0: LineSegment StartX=0 StartY=0 StartZ=0 EndX=0 EndY=6 EndZ=0
    g1: Circle CenterX=0 CenterY=0 CenterZ=0 NormalX=0 NormalY=0 NormalZ=1 AngleXU=0 Radius=1
    g2: Circle CenterX=8 CenterY=6 CenterZ=0 NormalX=0 NormalY=0 NormalZ=1 AngleXU=0 Radius=1
    g3: BSplineCurve PolesCount=3 KnotsCount=2 Degree=2 IsPeriodic=0
    g4: GeomPoint X=0 Y=0 Z=0
    g5: GeomPoint X=8 Y=6 Z=0
    g6: LineSegment StartX=0 StartY=6 StartZ=0 EndX=8 EndY=6 EndZ=0
  constraints (14):
    c: Coincident(g0,g-1)
    c: Distance(g0) = 6
    c: Vertical(g0)
    c: Coincident(g3,g0)
    c: Weight(g1) = 1
    c: Equal(g1,g2)
    c: InternalAlignment(g1,g3)
    c: InternalAlignment(g2,g3)
    c: InternalAlignment(g4,g3)
    c: InternalAlignment(g5,g3)
    c: Block(g3)
    c: Coincident(g6,g0)
    c: Coincident(g6,g3)
    c: Horizontal(g6)
FEATURE [Sketcher::SketchObject] Sketch040
  FullyConstrained = true
  sketch-geometry (7):
    g0: LineSegment StartX=0 StartY=0 StartZ=0 EndX=0 EndY=6 EndZ=0
    g1: Circle CenterX=0 CenterY=0 CenterZ=0 NormalX=0 NormalY=0 NormalZ=1 AngleXU=0 Radius=1
    g2: Circle CenterX=8 CenterY=6 CenterZ=0 NormalX=0 NormalY=0 NormalZ=1 AngleXU=0 Radius=1
    g3: BSplineCurve PolesCount=3 KnotsCount=2 Degree=2 IsPeriodic=0
    g4: GeomPoint X=0 Y=0 Z=0
    g5: GeomPoint X=8 Y=6 Z=0
    g6: LineSegment StartX=0 StartY=6 StartZ=0 EndX=8 EndY=6 EndZ=0
  constraints (14):
    c: Coincident(g0,g-1)
    c: Distance(g0) = 6
    c: Vertical(g0)
    c: Coincident(g3,g0)
    c: Weight(g1) = 1
    c: Equal(g1,g2)
    c: InternalAlignment(g1,g3)
    c: InternalAlignment(g2,g3)
    c: InternalAlignment(g4,g3)
    c: InternalAlignment(g5,g3)
    c: Block(g3)
    c: Coincident(g6,g0)
    c: Coincident(g6,g3)
    c: Horizontal(g6)
FEATURE [Sketcher::SketchObject] Sketch041
  FullyConstrained = true
  sketch-geometry (7):
    g0: LineSegment StartX=0 StartY=0 StartZ=0 EndX=0 EndY=6 EndZ=0
    g1: Circle CenterX=0 CenterY=0 CenterZ=0 NormalX=0 NormalY=0 NormalZ=1 AngleXU=0 Radius=1
    g2: Circle CenterX=8 CenterY=6 CenterZ=0 NormalX=0 NormalY=0 NormalZ=1 AngleXU=0 Radius=1
    g3: BSplineCurve PolesCount=3 KnotsCount=2 Degree=2 IsPeriodic=0
    g4: GeomPoint X=0 Y=0 Z=0
    g5: GeomPoint X=8 Y=6 Z=0
    g6: LineSegment StartX=0 StartY=6 StartZ=0 EndX=8 EndY=6 EndZ=0
  constraints (14):
    c: Coincident(g0,g-1)
    c: Distance(g0) = 6
    c: Vertical(g0)
    c: Coincident(g3,g0)
    c: Weight(g1) = 1
    c: Equal(g1,g2)
    c: InternalAlignment(g1,g3)
    c: InternalAlignment(g2,g3)
    c: InternalAlignment(g4,g3)
    c: InternalAlignment(g5,g3)
    c: Block(g3)
    c: Coincident(g6,g0)
    c: Coincident(g6,g3)
    c: Horizontal(g6)
FEATURE [Sketcher::SketchObject] Sketch042
  FullyConstrained = true
  sketch-geometry (7):
    g0: LineSegment StartX=0 StartY=0 StartZ=0 EndX=0 EndY=6 EndZ=0
    g1: Circle CenterX=0 CenterY=0 CenterZ=0 NormalX=0 NormalY=0 NormalZ=1 AngleXU=0 Radius=1
    g2: Circle CenterX=8 CenterY=6 CenterZ=0 NormalX=0 NormalY=0 NormalZ=1 AngleXU=0 Radius=1
    g3: BSplineCurve PolesCount=3 KnotsCount=2 Degree=2 IsPeriodic=0
    g4: GeomPoint X=0 Y=0 Z=0
    g5: GeomPoint X=8 Y=6 Z=0
    g6: LineSegment StartX=0 StartY=6 StartZ=0 EndX=8 EndY=6 EndZ=0
  constraints (14):
    c: Coincident(g0,g-1)
    c: Distance(g0) = 6
    c: Vertical(g0)
    c: Coincident(g3,g0)
    c: Weight(g1) = 1
    c: Equal(g1,g2)
    c: InternalAlignment(g1,g3)
    c: InternalAlignment(g2,g3)
    c: InternalAlignment(g4,g3)
    c: InternalAlignment(g5,g3)
    c: Block(g3)
    c: Coincident(g6,g0)
    c: Coincident(g6,g3)
    c: Horizontal(g6)
FEATURE [Part::Extrusion] Extrude030  label="caseScrewPillarBracket008"
  Base = -> Sketch039
  Dir = (0,0,1)
  DirMode = 2
  FaceMakerClass = Part::FaceMakerBullseye
  LengthFwd = 2.4
  LengthRev = 0
  Placement = pos=(15.76,29,8.8) rot=(0,1,0;0rad)
  Solid = true
  Symmetric = false
FEATURE [Part::Extrusion] Extrude031  label="caseScrewPillarBracket009"
  Base = -> Sketch040
  Dir = (0,0,1)
  DirMode = 2
  FaceMakerClass = Part::FaceMakerBullseye
  LengthFwd = 2.4
  LengthRev = 0
  Placement = pos=(15.76,29,60.8) rot=(0,0,1;0rad)
  Solid = true
  Symmetric = false
FEATURE [Part::Extrusion] Extrude032  label="caseScrewPillarBracket010"
  Base = -> Sketch041
  Dir = (0,0,1)
  DirMode = 2
  FaceMakerClass = Part::FaceMakerBullseye
  LengthFwd = 2.4
  LengthRev = 0
  Placement = pos=(13.7,29,13.26) rot=(0,-1,0;1.5708rad)
  Solid = true
  Symmetric = false
FEATURE [Part::Extrusion] Extrude033  label="caseScrewPillarBracket011"
  Base = -> Sketch042
  Dir = (0,0,1)
  DirMode = 2
  FaceMakerClass = Part::FaceMakerBullseye
  LengthFwd = 2.4
  LengthRev = 0
  Placement = pos=(11.3,29,58.74) rot=(0,1,0;1.5708rad)
  Solid = true
  Symmetric = false
FEATURE [Sketcher::SketchObject] Sketch043
  FullyConstrained = true
  sketch-geometry (7):
    g0: LineSegment StartX=0 StartY=0 StartZ=0 EndX=0 EndY=6 EndZ=0
    g1: Circle CenterX=0 CenterY=0 CenterZ=0 NormalX=0 NormalY=0 NormalZ=1 AngleXU=0 Radius=1
    g2: Circle CenterX=8 CenterY=6 CenterZ=0 NormalX=0 NormalY=0 NormalZ=1 AngleXU=0 Radius=1
    g3: BSplineCurve PolesCount=3 KnotsCount=2 Degree=2 IsPeriodic=0
    g4: GeomPoint X=0 Y=0 Z=0
    g5: GeomPoint X=8 Y=6 Z=0
    g6: LineSegment StartX=0 StartY=6 StartZ=0 EndX=8 EndY=6 EndZ=0
  constraints (14):
    c: Coincident(g0,g-1)
    c: Distance(g0) = 6
    c: Vertical(g0)
    c: Coincident(g3,g0)
    c: Weight(g1) = 1
    c: Equal(g1,g2)
    c: InternalAlignment(g1,g3)
    c: InternalAlignment(g2,g3)
    c: InternalAlignment(g4,g3)
    c: InternalAlignment(g5,g3)
    c: Block(g3)
    c: Coincident(g6,g0)
    c: Coincident(g6,g3)
    c: Horizontal(g6)
FEATURE [Part::Extrusion] Extrude034  label="caseScrewPillarBracket012"
  Base = -> Sketch043
  Dir = (0,0,1)
  DirMode = 2
  FaceMakerClass = Part::FaceMakerBullseye
  LengthFwd = 2.4
  LengthRev = 0
  Placement = pos=(88.3,29,65.23) rot=(0,1,0;1.5708rad)
  Solid = true
  Symmetric = false
FEATURE [Sketcher::SketchObject] Sketch044
  FullyConstrained = true
  sketch-geometry (7):
    g0: LineSegment StartX=0 StartY=0 StartZ=0 EndX=0 EndY=6 EndZ=0
    g1: Circle CenterX=0 CenterY=0 CenterZ=0 NormalX=0 NormalY=0 NormalZ=1 AngleXU=0 Radius=1
    g2: Circle CenterX=8 CenterY=6 CenterZ=0 NormalX=0 NormalY=0 NormalZ=1 AngleXU=0 Radius=1
    g3: BSplineCurve PolesCount=3 KnotsCount=2 Degree=2 IsPeriodic=0
    g4: GeomPoint X=0 Y=0 Z=0
    g5: GeomPoint X=8 Y=6 Z=0
    g6: LineSegment StartX=0 StartY=6 StartZ=0 EndX=8 EndY=6 EndZ=0
  constraints (14):
    c: Coincident(g0,g-1)
    c: Distance(g0) = 6
    c: Vertical(g0)
    c: Coincident(g3,g0)
    c: Weight(g1) = 1
    c: Equal(g1,g2)
    c: InternalAlignment(g1,g3)
    c: InternalAlignment(g2,g3)
    c: InternalAlignment(g4,g3)
    c: InternalAlignment(g5,g3)
    c: Block(g3)
    c: Coincident(g6,g0)
    c: Coincident(g6,g3)
    c: Horizontal(g6)
FEATURE [Part::Extrusion] Extrude035  label="caseScrewPillarBracket013"
  Base = -> Sketch044
  Dir = (0,0,1)
  DirMode = 2
  FaceMakerClass = Part::FaceMakerBullseye
  LengthFwd = 2.4
  LengthRev = 0
  Placement = pos=(90.7,29,6.77) rot=(0,-1,0;1.5708rad)
  Solid = true
  Symmetric = false
FEATURE [Sketcher::SketchObject] Sketch045
  FullyConstrained = true
  sketch-geometry (7):
    g0: LineSegment StartX=0 StartY=0 StartZ=0 EndX=0 EndY=6 EndZ=0
    g1: Circle CenterX=0 CenterY=0 CenterZ=0 NormalX=0 NormalY=0 NormalZ=1 AngleXU=0 Radius=1
    g2: Circle CenterX=8 CenterY=6 CenterZ=0 NormalX=0 NormalY=0 NormalZ=1 AngleXU=0 Radius=1
    g3: BSplineCurve PolesCount=3 KnotsCount=2 Degree=2 IsPeriodic=0
    g4: GeomPoint X=0 Y=0 Z=0
    g5: GeomPoint X=8 Y=6 Z=0
    g6: LineSegment StartX=0 StartY=6 StartZ=0 EndX=8 EndY=6 EndZ=0
  constraints (14):
    c: Coincident(g0,g-1)
    c: Distance(g0) = 6
    c: Vertical(g0)
    c: Coincident(g3,g0)
    c: Weight(g1) = 1
    c: Equal(g1,g2)
    c: InternalAlignment(g1,g3)
    c: InternalAlignment(g2,g3)
    c: InternalAlignment(g4,g3)
    c: InternalAlignment(g5,g3)
    c: Block(g3)
    c: Coincident(g6,g0)
    c: Coincident(g6,g3)
    c: Horizontal(g6)
FEATURE [Sketcher::SketchObject] Sketch046
  FullyConstrained = true
  sketch-geometry (7):
    g0: LineSegment StartX=0 StartY=0 StartZ=0 EndX=0 EndY=6 EndZ=0
    g1: Circle CenterX=0 CenterY=0 CenterZ=0 NormalX=0 NormalY=0 NormalZ=1 AngleXU=0 Radius=1
    g2: Circle CenterX=8 CenterY=6 CenterZ=0 NormalX=0 NormalY=0 NormalZ=1 AngleXU=0 Radius=1
    g3: BSplineCurve PolesCount=3 KnotsCount=2 Degree=2 IsPeriodic=0
    g4: GeomPoint X=0 Y=0 Z=0
    g5: GeomPoint X=8 Y=6 Z=0
    g6: LineSegment StartX=0 StartY=6 StartZ=0 EndX=8 EndY=6 EndZ=0
  constraints (14):
    c: Coincident(g0,g-1)
    c: Distance(g0) = 6
    c: Vertical(g0)
    c: Coincident(g3,g0)
    c: Weight(g1) = 1
    c: Equal(g1,g2)
    c: InternalAlignment(g1,g3)
    c: InternalAlignment(g2,g3)
    c: InternalAlignment(g4,g3)
    c: InternalAlignment(g5,g3)
    c: Block(g3)
    c: Coincident(g6,g0)
    c: Coincident(g6,g3)
    c: Horizontal(g6)
FEATURE [Part::Extrusion] Extrude036  label="caseScrewPillarBracket014"
  Base = -> Sketch045
  Dir = (0,0,1)
  DirMode = 2
  FaceMakerClass = Part::FaceMakerBullseye
  LengthFwd = 2.4
  LengthRev = 0
  Placement = pos=(110.7,29,6.77) rot=(0,-1,0;1.5708rad)
  Solid = true
  Symmetric = false
FEATURE [Part::Extrusion] Extrude037  label="caseScrewPillarBracket015"
  Base = -> Sketch046
  Dir = (0,0,1)
  DirMode = 2
  FaceMakerClass = Part::FaceMakerBullseye
  LengthFwd = 2.4
  LengthRev = 0
  Placement = pos=(108.3,29,65.23) rot=(0,1,0;1.5708rad)
  Solid = true
  Symmetric = false
FEATURE [Part::Box] Box013  label="frontCaseScrewPillarBracket002"
  AttacherType = Attacher::AttachEngine3D
  Height = 2.4
  Length = 22
  Placement = pos=(87,28,2.3) rot=(0,0,1;0rad)
  Width = 7
FEATURE [Part::Box] Box014  label="frontCaseScrewPillarBracket003"
  AttacherType = Attacher::AttachEngine3D
  Height = 2.4
  Length = 22
  Placement = pos=(87,28,67.3) rot=(0,0,1;0rad)
  Width = 7
FEATURE [Part::Feature] Face087
  shape: bbox 4.8 x 30.2 x 2e-07 mm, 1 faces, 0 solids (baked)
FEATURE [Part::Revolution] Revolve091  label="frontCaseScrewPost004"
  Angle = 360
  Axis = (0,1,0)
  Base = (0,0,0)
  FaceMakerClass = Part::FaceMakerBullseye
  Placement = pos=(89.5,4.5,3.5) rot=(0,0,1;0rad)
  Solid = false
  Source = -> Face087
  Symmetric = false
FEATURE [Part::Feature] Face088
  shape: bbox 4.8 x 30.2 x 2e-07 mm, 1 faces, 0 solids (baked)
FEATURE [Part::Revolution] Revolve092  label="frontCaseScrewPost005"
  Angle = 360
  Axis = (0,1,0)
  Base = (0,0,0)
  FaceMakerClass = Part::FaceMakerBullseye
  Placement = pos=(89.5,4.5,68.5) rot=(0,0,1;0rad)
  Solid = false
  Source = -> Face088
  Symmetric = false
FEATURE [Part::Feature] Face089
  shape: bbox 3.5 x 30.2 x 2e-07 mm, 1 faces, 0 solids (baked)
FEATURE [Part::Revolution] Revolve093  label="backCaseScrewPost002"
  Angle = 360
  Axis = (0,1,0)
  Base = (0,0,0)
  FaceMakerClass = Part::FaceMakerBullseye
  Placement = pos=(12.5,4.5,10) rot=(0,0,1;0rad)
  Solid = false
  Source = -> Face089
  Symmetric = false
FEATURE [Part::Feature] Face090
  shape: bbox 3.5 x 30.2 x 2e-07 mm, 1 faces, 0 solids (baked)
FEATURE [Part::Revolution] Revolve094  label="backCaseScrewPost003"
  Angle = 360
  Axis = (0,1,0)
  Base = (0,0,0)
  FaceMakerClass = Part::FaceMakerBullseye
  Placement = pos=(12.5,4.5,62) rot=(0,0,1;0rad)
  Solid = false
  Source = -> Face090
  Symmetric = false
FEATURE [Part::Box] Box015  label="Cube011"
  AttacherType = Attacher::AttachEngine3D
  Height = 28.8
  Length = 3
  Placement = pos=(107.3,28,21.6) rot=(0,0,1;0rad)
  Width = 7
FEATURE [Part::Box] Box016  label="Cube012"
  AttacherType = Attacher::AttachEngine3D
  Height = 3
  Length = 7.4
  Placement = pos=(107.3,28,18.6) rot=(0,0,1;0rad)
  Width = 7
FEATURE [Part::Box] Box017  label="Cube013"
  AttacherType = Attacher::AttachEngine3D
  Height = 3
  Length = 7.4
  Placement = pos=(107.3,28,50.4) rot=(0,0,1;0rad)
  Width = 7
FEATURE [Part::Cylinder] Cylinder024
  Angle = 360
  AttacherType = Attacher::AttachEngine3D
  Height = 20
  Placement = pos=(0,0,36.15) rot=(0,0,1;0rad)
  Radius = 14.3
FEATURE [Part::Cylinder] Cylinder025
  Angle = 360
  AttacherType = Attacher::AttachEngine3D
  Height = 10
  Placement = pos=(0,0,36.15) rot=(0,0,1;0rad)
  Radius = 4
FEATURE [Part::MultiFuse] Fusion066  label="removeToCreteHoleForPlugHousing009"
  Placement = pos=(70,19,36) rot=(0,1,0;1.5708rad)
  Shapes = -> [Cylinder024,Cylinder025]
FEATURE [Part::MultiFuse] Fusion065  label="plugHousingBracketHolder002"
  Shapes = -> [Box017,Box015,Box016]
FEATURE [Part::Cut] Cut025  label="plugHousingBracketHolder003"
  Base = -> Fusion065
  Placement = pos=(7,0,0) rot=(0,0,1;0rad)
  Tool = -> Fusion066
FEATURE [Sketcher::SketchObject] Sketch047
  FullyConstrained = false
  Placement = pos=(0,0,0) rot=(1,0,0;1.5708rad)
  sketch-geometry (24):
    g0: ArcOfCircle CenterX=-4 CenterY=-10.5 CenterZ=0 NormalX=0 NormalY=0 NormalZ=1 AngleXU=0 Radius=1.5 StartAngle=6e-16 EndAngle=3.14159
    g1: ArcOfCircle CenterX=-34.2 CenterY=-10.5 CenterZ=0 NormalX=0 NormalY=0 NormalZ=1 AngleXU=0 Radius=1.5 StartAngle=0 EndAngle=3.14159
    g2: ArcOfCircle CenterX=-34.2 CenterY=-27.7 CenterZ=0 NormalX=0 NormalY=0 NormalZ=1 AngleXU=0 Radius=1.5 StartAngle=3.14159 EndAngle=6.28319
    g3: ArcOfCircle CenterX=-4 CenterY=-27.7 CenterZ=0 NormalX=0 NormalY=0 NormalZ=1 AngleXU=0 Radius=1.5 StartAngle=3.1416 EndAngle=6.28319
    g4: ArcOfCircle CenterX=-10 CenterY=-4.3 CenterZ=0 NormalX=0 NormalY=0 NormalZ=1 AngleXU=0 Radius=1.5 StartAngle=2e-16 EndAngle=3.14159
    g5: ArcOfCircle CenterX=-16.1 CenterY=-1.8 CenterZ=0 NormalX=0 NormalY=0 NormalZ=1 AngleXU=0 Radius=1.5 StartAngle=5e-16 EndAngle=3.14159
    g6: ArcOfCircle CenterX=-22.1 CenterY=-1.8 CenterZ=0 NormalX=0 NormalY=0 NormalZ=1 AngleXU=0 Radius=1.5 StartAngle=5e-16 EndAngle=3.14159
    g7: ArcOfCircle CenterX=-28.2 CenterY=-4.3 CenterZ=0 NormalX=0 NormalY=0 NormalZ=1 AngleXU=0 Radius=1.5 StartAngle=2e-16 EndAngle=3.14159
    g8: ArcOfCircle CenterX=-10 CenterY=-33.9 CenterZ=0 NormalX=0 NormalY=0 NormalZ=1 AngleXU=0 Radius=1.5 StartAngle=3.14159 EndAngle=6.28319
    g9: ArcOfCircle CenterX=-16.1 CenterY=-36.4 CenterZ=0 NormalX=0 NormalY=0 NormalZ=1 AngleXU=0 Radius=1.5 StartAngle=3.14159 EndAngle=6.28319
    g10: ArcOfCircle CenterX=-22.1 CenterY=-36.4 CenterZ=0 NormalX=0 NormalY=0 NormalZ=1 AngleXU=0 Radius=1.5 StartAngle=3.14159 EndAngle=6.28319
    g11: ArcOfCircle CenterX=-28.2 CenterY=-33.9 CenterZ=0 NormalX=0 NormalY=0 NormalZ=1 AngleXU=0 Radius=1.5 StartAngle=3.14159 EndAngle=6.28319
    g12: LineSegment StartX=-35.7 StartY=-10.5 StartZ=0 EndX=-35.7 EndY=-27.7 EndZ=0
    g13: LineSegment StartX=-32.7 StartY=-10.5 StartZ=0 EndX=-32.7 EndY=-27.7 EndZ=0
    g14: LineSegment StartX=-29.7 StartY=-33.9 StartZ=0 EndX=-29.7 EndY=-4.3 EndZ=0
    g15: LineSegment StartX=-26.7 StartY=-33.9 StartZ=0 EndX=-26.7 EndY=-4.3 EndZ=0
    g16: LineSegment StartX=-2.5 StartY=-10.5 StartZ=0 EndX=-2.5 EndY=-27.7 EndZ=0
    g17: LineSegment StartX=-8.5 StartY=-4.3 StartZ=0 EndX=-8.5 EndY=-33.9 EndZ=0
    g18: LineSegment StartX=-5.5 StartY=-10.5 StartZ=0 EndX=-5.5 EndY=-27.7 EndZ=0
    g19: LineSegment StartX=-11.5 StartY=-4.3 StartZ=0 EndX=-11.5 EndY=-33.9 EndZ=0
    g20: LineSegment StartX=-14.6 StartY=-1.8 StartZ=0 EndX=-14.6 EndY=-36.4 EndZ=0
    g21: LineSegment StartX=-17.6 StartY=-1.8 StartZ=0 EndX=-17.6 EndY=-36.4 EndZ=0
    g22: LineSegment StartX=-20.6 StartY=-36.4 StartZ=0 EndX=-20.6 EndY=-1.8 EndZ=0
    g23: LineSegment StartX=-23.6 StartY=-1.8 StartZ=0 EndX=-23.6 EndY=-36.4 EndZ=0
  constraints (48):
    c: Block(g0)
    c: Block(g1)
    c: Block(g2)
    c: Block(g3)
    c: Block(g4)
    c: Block(g5)
    c: Block(g6)
    c: Block(g7)
    c: Block(g8)
    c: Block(g9)
    c: Block(g10)
    c: Block(g11)
    c: Coincident(g12,g1)
    c: Coincident(g12,g2)
    c: Vertical(g12)
    c: Coincident(g13,g1)
    c: Coincident(g13,g2)
    c: Vertical(g13)
    c: Coincident(g14,g11)
    c: Coincident(g14,g7)
    c: Vertical(g14)
    c: Coincident(g15,g11)
    c: Coincident(g15,g7)
    c: Vertical(g15)
    c: Coincident(g16,g0)
    c: Coincident(g16,g3)
    c: Vertical(g16)
    c: Coincident(g17,g4)
    c: Coincident(g17,g8)
    c: Vertical(g17)
    c: Coincident(g18,g0)
    c: Coincident(g18,g3)
    c: Vertical(g18)
    c: Coincident(g19,g4)
    c: Coincident(g19,g8)
    c: Vertical(g19)
    c: Coincident(g20,g5)
    c: Coincident(g20,g9)
    c: Vertical(g20)
    c: Coincident(g21,g5)
    c: Coincident(g21,g9)
    c: Vertical(g21)
    c: Coincident(g22,g10)
    c: Coincident(g22,g6)
    c: Vertical(g22)
    c: Coincident(g23,g6)
    c: Coincident(g23,g10)
    c: Vertical(g23)
FEATURE [Part::Extrusion] Extrude038  label="removeToCreateFanGrillHoles001"
  Base = -> Sketch047
  Dir = (0,-1,6e-16)
  DirMode = 2
  FaceMakerClass = Part::FaceMakerBullseye
  LengthFwd = 10
  LengthRev = 0
  Placement = pos=(65.4,44,54.82) rot=(0,0,1;0rad)
  Solid = true
  Symmetric = false
FEATURE [Part::Feature] Wire004
  shape: bbox 11 x 5.2 x 2e-07 mm, 0 faces, 0 solids (baked)
FEATURE [Part::Revolution] Revolve095
  Angle = 360
  Axis = (0,1,0)
  Base = (0,0,0)
  FaceMakerClass = Part::FaceMakerBullseye
  Placement = pos=(30.3,38,19.7) rot=(0,0,1;0rad)
  Solid = true
  Source = -> Wire004
  Symmetric = false
FEATURE [Part::Feature] Wire005
  shape: bbox 11 x 5.2 x 2e-07 mm, 0 faces, 0 solids (baked)
FEATURE [Part::Revolution] Revolve096
  Angle = 360
  Axis = (0,1,0)
  Base = (0,0,0)
  FaceMakerClass = Part::FaceMakerBullseye
  Placement = pos=(30.3,38,51.7) rot=(0,0,1;0rad)
  Solid = true
  Source = -> Wire005
  Symmetric = false
FEATURE [Part::Feature] Wire006
  shape: bbox 11 x 5.2 x 2e-07 mm, 0 faces, 0 solids (baked)
FEATURE [Part::Revolution] Revolve097
  Angle = 360
  Axis = (0,1,0)
  Base = (0,0,0)
  FaceMakerClass = Part::FaceMakerBullseye
  Placement = pos=(62.3,38,51.7) rot=(0,0,1;0rad)
  Solid = true
  Source = -> Wire006
  Symmetric = false
FEATURE [Part::Feature] Wire007
  shape: bbox 11 x 5.2 x 2e-07 mm, 0 faces, 0 solids (baked)
FEATURE [Part::Revolution] Revolve098
  Angle = 360
  Axis = (0,1,0)
  Base = (0,0,0)
  FaceMakerClass = Part::FaceMakerBullseye
  Placement = pos=(62.3,38,19.7) rot=(0,0,1;0rad)
  Solid = true
  Source = -> Wire007
  Symmetric = false
FEATURE [Part::MultiFuse] Fusion067  label="fanScrewHousing002"
  Shapes = -> [Revolve098,Revolve097,Revolve096,Revolve095]
FEATURE [Part::Feature] Face091 .. Face094  x4 (patterned run collapsed; names and placements below)
  shape: bbox 3.5 x 17.8 x 2e-07 mm, 1 faces, 0 solids (baked)
FEATURE [Part::Revolution] Revolve099  label="removeToCreateScrewAndThreadedInsertHole026"
  Angle = 360
  Axis = (0,1,0)
  Base = (0,0,0)
  FaceMakerClass = Part::FaceMakerBullseye
  Placement = pos=(62.3,30.3,19.7) rot=(0,0,1;0rad)
  Solid = false
  Source = -> Face091
  Symmetric = false
FEATURE [Part::Revolution] Revolve100  label="removeToCreateScrewAndThreadedInsertHole027"
  Angle = 360
  Axis = (0,1,0)
  Base = (0,0,0)
  FaceMakerClass = Part::FaceMakerBullseye
  Placement = pos=(62.3,30.3,51.7) rot=(0,0,1;0rad)
  Solid = false
  Source = -> Face092
  Symmetric = false
FEATURE [Part::Revolution] Revolve101  label="removeToCreateScrewAndThreadedInsertHole028"
  Angle = 360
  Axis = (0,1,0)
  Base = (0,0,0)
  FaceMakerClass = Part::FaceMakerBullseye
  Placement = pos=(30.3,30.3,19.7) rot=(0,0,1;0rad)
  Solid = false
  Source = -> Face093
  Symmetric = false
FEATURE [Part::Revolution] Revolve102  label="removeToCreateScrewAndThreadedInsertHole029"
  Angle = 360
  Axis = (0,1,0)
  Base = (0,0,0)
  FaceMakerClass = Part::FaceMakerBullseye
  Placement = pos=(30.3,30.3,51.7) rot=(0,0,1;0rad)
  Solid = false
  Source = -> Face094
  Symmetric = false
FEATURE [Part::MultiFuse] Fusion068  label="createThreadedInsertHolesForFan002"
  Shapes = -> [Revolve099,Revolve100,Revolve101,Revolve102]
FEATURE [Part::Cut] Cut026  label="fanScrewHousing003"
  Base = -> Fusion067
  Tool = -> Fusion068
FEATURE [Sketcher::SketchObject] Sketch048
  FullyConstrained = false
  Placement = pos=(0,0,0) rot=(1,0,0;1.5708rad)
  sketch-geometry (24):
    g0: ArcOfCircle CenterX=-4 CenterY=-10.5 CenterZ=0 NormalX=0 NormalY=0 NormalZ=1 AngleXU=0 Radius=1.5 StartAngle=6e-16 EndAngle=3.14159
    g1: ArcOfCircle CenterX=-34.2 CenterY=-10.5 CenterZ=0 NormalX=0 NormalY=0 NormalZ=1 AngleXU=0 Radius=1.5 StartAngle=0 EndAngle=3.14159
    g2: ArcOfCircle CenterX=-34.2 CenterY=-27.7 CenterZ=0 NormalX=0 NormalY=0 NormalZ=1 AngleXU=0 Radius=1.5 StartAngle=3.14159 EndAngle=6.28319
    g3: ArcOfCircle CenterX=-4 CenterY=-27.7 CenterZ=0 NormalX=0 NormalY=0 NormalZ=1 AngleXU=0 Radius=1.5 StartAngle=3.1416 EndAngle=6.28319
    g4: ArcOfCircle CenterX=-10 CenterY=-4.3 CenterZ=0 NormalX=0 NormalY=0 NormalZ=1 AngleXU=0 Radius=1.5 StartAngle=2e-16 EndAngle=3.14159
    g5: ArcOfCircle CenterX=-16.1 CenterY=-1.8 CenterZ=0 NormalX=0 NormalY=0 NormalZ=1 AngleXU=0 Radius=1.5 StartAngle=5e-16 EndAngle=3.14159
    g6: ArcOfCircle CenterX=-22.1 CenterY=-1.8 CenterZ=0 NormalX=0 NormalY=0 NormalZ=1 AngleXU=0 Radius=1.5 StartAngle=5e-16 EndAngle=3.14159
    g7: ArcOfCircle CenterX=-28.2 CenterY=-4.3 CenterZ=0 NormalX=0 NormalY=0 NormalZ=1 AngleXU=0 Radius=1.5 StartAngle=2e-16 EndAngle=3.14159
    g8: ArcOfCircle CenterX=-10 CenterY=-33.9 CenterZ=0 NormalX=0 NormalY=0 NormalZ=1 AngleXU=0 Radius=1.5 StartAngle=3.14159 EndAngle=6.28319
    g9: ArcOfCircle CenterX=-16.1 CenterY=-36.4 CenterZ=0 NormalX=0 NormalY=0 NormalZ=1 AngleXU=0 Radius=1.5 StartAngle=3.14159 EndAngle=6.28319
    g10: ArcOfCircle CenterX=-22.1 CenterY=-36.4 CenterZ=0 NormalX=0 NormalY=0 NormalZ=1 AngleXU=0 Radius=1.5 StartAngle=3.14159 EndAngle=6.28319
    g11: ArcOfCircle CenterX=-28.2 CenterY=-33.9 CenterZ=0 NormalX=0 NormalY=0 NormalZ=1 AngleXU=0 Radius=1.5 StartAngle=3.14159 EndAngle=6.28319
    g12: LineSegment StartX=-35.7 StartY=-10.5 StartZ=0 EndX=-35.7 EndY=-27.7 EndZ=0
    g13: LineSegment StartX=-32.7 StartY=-10.5 StartZ=0 EndX=-32.7 EndY=-27.7 EndZ=0
    g14: LineSegment StartX=-29.7 StartY=-33.9 StartZ=0 EndX=-29.7 EndY=-4.3 EndZ=0
    g15: LineSegment StartX=-26.7 StartY=-33.9 StartZ=0 EndX=-26.7 EndY=-4.3 EndZ=0
    g16: LineSegment StartX=-2.5 StartY=-10.5 StartZ=0 EndX=-2.5 EndY=-27.7 EndZ=0
    g17: LineSegment StartX=-8.5 StartY=-4.3 StartZ=0 EndX=-8.5 EndY=-33.9 EndZ=0
    g18: LineSegment StartX=-5.5 StartY=-10.5 StartZ=0 EndX=-5.5 EndY=-27.7 EndZ=0
    g19: LineSegment StartX=-11.5 StartY=-4.3 StartZ=0 EndX=-11.5 EndY=-33.9 EndZ=0
    g20: LineSegment StartX=-14.6 StartY=-1.8 StartZ=0 EndX=-14.6 EndY=-36.4 EndZ=0
    g21: LineSegment StartX=-17.6 StartY=-1.8 StartZ=0 EndX=-17.6 EndY=-36.4 EndZ=0
    g22: LineSegment StartX=-20.6 StartY=-36.4 StartZ=0 EndX=-20.6 EndY=-1.8 EndZ=0
    g23: LineSegment StartX=-23.6 StartY=-1.8 StartZ=0 EndX=-23.6 EndY=-36.4 EndZ=0
  constraints (48):
    c: Block(g0)
    c: Block(g1)
    c: Block(g2)
    c: Block(g3)
    c: Block(g4)
    c: Block(g5)
    c: Block(g6)
    c: Block(g7)
    c: Block(g8)
    c: Block(g9)
    c: Block(g10)
    c: Block(g11)
    c: Coincident(g12,g1)
    c: Coincident(g12,g2)
    c: Vertical(g12)
    c: Coincident(g13,g1)
    c: Coincident(g13,g2)
    c: Vertical(g13)
    c: Coincident(g14,g11)
    c: Coincident(g14,g7)
    c: Vertical(g14)
    c: Coincident(g15,g11)
    c: Coincident(g15,g7)
    c: Vertical(g15)
    c: Coincident(g16,g0)
    c: Coincident(g16,g3)
    c: Vertical(g16)
    c: Coincident(g17,g4)
    c: Coincident(g17,g8)
    c: Vertical(g17)
    c: Coincident(g18,g0)
    c: Coincident(g18,g3)
    c: Vertical(g18)
    c: Coincident(g19,g4)
    c: Coincident(g19,g8)
    c: Vertical(g19)
    c: Coincident(g20,g5)
    c: Coincident(g20,g9)
    c: Vertical(g20)
    c: Coincident(g21,g5)
    c: Coincident(g21,g9)
    c: Vertical(g21)
    c: Coincident(g22,g10)
    c: Coincident(g22,g6)
    c: Vertical(g22)
    c: Coincident(g23,g6)
    c: Coincident(g23,g10)
    c: Vertical(g23)
FEATURE [Part::Extrusion] Extrude039  label="removeToCreateFanGrillHoles002"
  Base = -> Sketch048
  Dir = (0,-1,6e-16)
  DirMode = 2
  FaceMakerClass = Part::FaceMakerBullseye
  LengthFwd = 10
  LengthRev = 0
  Placement = pos=(65.4,44,54.82) rot=(0,0,1;0rad)
  Solid = true
  Symmetric = false
FEATURE [Part::Cut] Cut027  label="fanScrewHousing004"
  Base = -> Cut026
  Tool = -> Extrude038
FEATURE [Part::Cut] Cut028  label="top014"
  Base = -> Fillet026
  Tool = -> Extrude039
FEATURE [Part::Feature] Face095 .. Face098  x4 (patterned run collapsed; names and placements below)
  shape: bbox 3.5 x 17.8 x 2e-07 mm, 1 faces, 0 solids (baked)
FEATURE [Part::Revolution] Revolve103  label="removeToCreateScrewAndThreadedInsertHole030"
  Angle = 360
  Axis = (0,1,0)
  Base = (0,0,0)
  FaceMakerClass = Part::FaceMakerBullseye
  Placement = pos=(62.3,30.3,19.7) rot=(0,0,1;0rad)
  Solid = false
  Source = -> Face095
  Symmetric = false
FEATURE [Part::Revolution] Revolve104  label="removeToCreateScrewAndThreadedInsertHole031"
  Angle = 360
  Axis = (0,1,0)
  Base = (0,0,0)
  FaceMakerClass = Part::FaceMakerBullseye
  Placement = pos=(62.3,30.3,51.7) rot=(0,0,1;0rad)
  Solid = false
  Source = -> Face096
  Symmetric = false
FEATURE [Part::Revolution] Revolve105  label="removeToCreateScrewAndThreadedInsertHole032"
  Angle = 360
  Axis = (0,1,0)
  Base = (0,0,0)
  FaceMakerClass = Part::FaceMakerBullseye
  Placement = pos=(30.3,30.3,19.7) rot=(0,0,1;0rad)
  Solid = false
  Source = -> Face097
  Symmetric = false
FEATURE [Part::Revolution] Revolve106  label="removeToCreateScrewAndThreadedInsertHole033"
  Angle = 360
  Axis = (0,1,0)
  Base = (0,0,0)
  FaceMakerClass = Part::FaceMakerBullseye
  Placement = pos=(30.3,30.3,51.7) rot=(0,0,1;0rad)
  Solid = false
  Source = -> Face098
  Symmetric = false
FEATURE [Part::MultiFuse] Fusion069  label="createThreadedInsertHolesForFan003"
  Shapes = -> [Revolve103,Revolve104,Revolve105,Revolve106]
FEATURE [Part::Cut] Cut029  label="top015"
  Base = -> Cut028
  Tool = -> Fusion054
FEATURE [Part::Cut] Cut030  label="fanScrewHousing005"
  Base = -> Cut027
  Tool = -> Fusion069
FEATURE [Part::Cylinder] Cylinder026  label="removeToCreteHoleForPlugHousing010"
  Angle = 360
  AttacherType = Attacher::AttachEngine3D
  Height = 20
  Placement = pos=(-2,19,36) rot=(0,1,0;1.5708rad)
  Radius = 14.3
FEATURE [Part::Box] Box018  label="removeToCreteHoleForPlugHousing011"
  AttacherType = Attacher::AttachEngine3D
  Height = 28.6
  Length = 10
  Placement = pos=(-2,0,21.7) rot=(0,0,1;0rad)
  Width = 19
FEATURE [Part::Box] Box019  label="wireHolderBottomCaseBit"
  AttacherType = Attacher::AttachEngine3D
  Height = 28
  Length = 3
  Placement = pos=(0,0,22) rot=(0,0,1;0rad)
  Width = 21
FEATURE [Part::Cylinder] Cylinder027  label="removeToCreteHoleForPlugHousing012"
  Angle = 360
  AttacherType = Attacher::AttachEngine3D
  Height = 20
  Placement = pos=(-2,19,36) rot=(0,1,0;1.5708rad)
  Radius = 14.3
FEATURE [Part::Cut] Cut031  label="wireHolderBottomCaseBit001"
  Base = -> Box019
  Tool = -> Cylinder027
FEATURE [Part::MultiFuse] Fusion070  label="removeToCreteHoleForPlugHousing013"
  Shapes = -> [Box018,Cylinder026]
FEATURE [Part::Cut] Cut032  label="top016"
  Base = -> Cut029
  Tool = -> Fusion070
FEATURE [Part::Cylinder] Cylinder028
  Angle = 360
  AttacherType = Attacher::AttachEngine3D
  Height = 20
  Placement = pos=(0,0,36.15) rot=(0,0,1;0rad)
  Radius = 14.3
FEATURE [Part::Cylinder] Cylinder029
  Angle = 360
  AttacherType = Attacher::AttachEngine3D
  Height = 10
  Placement = pos=(0,0,36.15) rot=(0,0,1;0rad)
  Radius = 4
FEATURE [Part::MultiFuse] Fusion071  label="removeToCreteHoleForPlugHousing014"
  Placement = pos=(70,19,36) rot=(0,1,0;1.5708rad)
  Shapes = -> [Cylinder028,Cylinder029]
FEATURE [Sketcher::SketchObject] Sketch049  label="topSketch011"
  FullyConstrained = true
  sketch-geometry (4):
    g0: ArcOfCircle CenterX=105 CenterY=19 CenterZ=0 NormalX=0 NormalY=0 NormalZ=1 AngleXU=0 Radius=20.6155 StartAngle=5.54125 EndAngle=6.28319
    g1: ArcOfCircle CenterX=105 CenterY=19 CenterZ=0 NormalX=0 NormalY=0 NormalZ=1 AngleXU=0 Radius=13 StartAngle=5.54125 EndAngle=6.28319
    g2: LineSegment StartX=118 StartY=19 StartZ=0 EndX=125.616 EndY=19 EndZ=0
    g3: LineSegment StartX=114.583 StartY=10.2157 StartZ=0 EndX=120.197 EndY=5.06982 EndZ=0
  constraints (7):
    c: Block(g0)
    c: Block(g1)
    c: Coincident(g2,g1)
    c: Coincident(g2,g0)
    c: Horizontal(g2)
    c: Coincident(g3,g1)
    c: Coincident(g3,g0)
FEATURE [Part::Box] Box020  label="removeToCreteHoleForPlugHousing015"
  AttacherType = Attacher::AttachEngine3D
  Height = 28.6
  Length = 20
  Placement = pos=(106.15,0,21.7) rot=(0,0,1;0rad)
  Width = 19
FEATURE [Part::MultiFuse] Fusion072  label="removeToCreteHoleForPlugHousing016"
  Shapes = -> [Box020,Fusion071]
FEATURE [Part::Cut] Cut033  label="removeToCreteHoleForPlugHousing017"
  Base = -> Cut032
  Tool = -> Fusion072
FEATURE [Part::Cylinder] Cylinder030
  Angle = 360
  AttacherType = Attacher::AttachEngine3D
  Height = 20
  Placement = pos=(0,0,36.15) rot=(0,0,1;0rad)
  Radius = 14.3
FEATURE [Part::Cylinder] Cylinder031
  Angle = 360
  AttacherType = Attacher::AttachEngine3D
  Height = 10
  Placement = pos=(0,0,36.15) rot=(0,0,1;0rad)
  Radius = 4
FEATURE [Part::Box] Box021  label="removeToCreteHoleForPlugHousing019"
  AttacherType = Attacher::AttachEngine3D
  Height = 28.6
  Length = 20
  Placement = pos=(106.15,0,21.7) rot=(0,0,1;0rad)
  Width = 19
FEATURE [Part::MultiFuse] Fusion074  label="removeToCreteHoleForPlugHousing020"
  Placement = pos=(70,19,36) rot=(0,1,0;1.5708rad)
  Shapes = -> [Cylinder030,Cylinder031]
FEATURE [Part::MultiFuse] Fusion073  label="removeToCreteHoleForPlugHousing018"
  Placement = pos=(0,0,28.3) rot=(0,0,1;0rad)
  Shapes = -> [Box021,Fusion074]
FEATURE [Part::Cylinder] Cylinder032
  Angle = 360
  AttacherType = Attacher::AttachEngine3D
  Height = 20
  Placement = pos=(0,0,36.15) rot=(0,0,1;0rad)
  Radius = 14.3
FEATURE [Part::Cylinder] Cylinder033
  Angle = 360
  AttacherType = Attacher::AttachEngine3D
  Height = 10
  Placement = pos=(0,0,36.15) rot=(0,0,1;0rad)
  Radius = 4
FEATURE [Part::Box] Box022  label="removeToCreteHoleForPlugHousing021"
  AttacherType = Attacher::AttachEngine3D
  Height = 28.6
  Length = 20
  Placement = pos=(106.15,0,21.7) rot=(0,0,1;0rad)
  Width = 19
FEATURE [Part::MultiFuse] Fusion076  label="removeToCreteHoleForPlugHousing023"
  Placement = pos=(70,19,36) rot=(0,1,0;1.5708rad)
  Shapes = -> [Cylinder032,Cylinder033]
FEATURE [Part::MultiFuse] Fusion075  label="removeToCreteHoleForPlugHousing022"
  Placement = pos=(0,0,-28.3) rot=(0,0,1;0rad)
  Shapes = -> [Box022,Fusion076]
FEATURE [Part::MultiFuse] Fusion077  label="removeToCreatePlugHousingBottomBit"
  Shapes = -> [Fusion075,Fusion073]
FEATURE [Part::Cylinder] Cylinder034
  Angle = 360
  AttacherType = Attacher::AttachEngine3D
  Height = 20
  Placement = pos=(0,0,36.15) rot=(0,0,1;0rad)
  Radius = 14
FEATURE [Part::Cylinder] Cylinder035
  Angle = 360
  AttacherType = Attacher::AttachEngine3D
  Height = 10
  Placement = pos=(0,0,36.15) rot=(0,0,1;0rad)
  Radius = 4
FEATURE [Part::MultiFuse] Fusion078  label="removeToCreteHoleForPlugHousing024"
  Placement = pos=(70,19,36) rot=(0,1,0;1.5708rad)
  Shapes = -> [Cylinder034,Cylinder035]
FEATURE [Part::MultiFuse] Fusion079  label="removeToCreatePlugHousingBottomBit001"
  Shapes = -> [Fusion078,Fusion077]
FEATURE [Part::Extrusion] Extrude040  label="bottomPlugHousingBit"
  Base = -> Sketch049
  Dir = (0,0,1)
  DirMode = 2
  FaceMakerClass = Part::FaceMakerBullseye
  LengthFwd = 72
  LengthRev = 0
  Solid = true
  Symmetric = false
FEATURE [Part::Cut] Cut034  label="bottomPlugHousingBit001"
  Base = -> Extrude040
  Placement = pos=(-0.09,0,0) rot=(0,0,1;0rad)
  Tool = -> Fusion079
FEATURE [Part::Box] Box023  label="Cube014"
  AttacherType = Attacher::AttachEngine3D
  Height = 16
  Length = 8
  Placement = pos=(12.7,31.52,28) rot=(0,0,1;0rad)
  Width = 4
FEATURE [Part::Cylinder] Cylinder036
  Angle = 360
  AttacherType = Attacher::AttachEngine3D
  Height = 10
  Placement = pos=(0,0,36.15) rot=(0,0,1;0rad)
  Radius = 4
FEATURE [Part::Cylinder] Cylinder037
  Angle = 360
  AttacherType = Attacher::AttachEngine3D
  Height = 20
  Placement = pos=(0,0,36.15) rot=(0,0,1;0rad)
  Radius = 8.2
FEATURE [Part::MultiFuse] Fusion080  label="removeToCreteHoleForPlugHousing025"
  Placement = pos=(-42,19,36) rot=(0,1,0;1.5708rad)
  Shapes = -> [Cylinder037,Cylinder036]
FEATURE [Sketcher::SketchObject] Sketch050  label="topSketch012"
  FullyConstrained = true
  sketch-geometry (4):
    g0: LineSegment StartX=16.8446 StartY=31.512 StartZ=0 EndX=16.3251 EndY=34.4666 EndZ=0
    g1: ArcOfCircle CenterX=19 CenterY=19.2524 CenterZ=0 NormalX=0 NormalY=0 NormalZ=1 AngleXU=0 Radius=15.4476 StartAngle=1.74483 EndAngle=2.72717
    g2: ArcOfCircle CenterX=19 CenterY=19.2524 CenterZ=0 NormalX=0 NormalY=0 NormalZ=1 AngleXU=0 Radius=12.4476 StartAngle=1.74483 EndAngle=2.73189
    g3: LineSegment StartX=4.86004 StartY=25.4725 StartZ=0 EndX=7.58253 EndY=24.2107 EndZ=0
  constraints (7):
    c: Block(g0)
    c: Coincident(g1,g0)
    c: Coincident(g2,g0)
    c: Coincident(g3,g1)
    c: Coincident(g3,g2)
    c: Block(g1)
    c: Block(g2)
FEATURE [Part::Extrusion] Extrude041
  Base = -> Sketch050
  Dir = (0,0,1)
  DirMode = 2
  FaceMakerClass = Part::FaceMakerBullseye
  LengthFwd = 10.6
  LengthRev = 0
  Placement = pos=(0,0,31) rot=(0,0,1;0rad)
  Solid = true
  Symmetric = false
FEATURE [Part::Cut] Cut035
  Base = -> Extrude041
  Placement = pos=(0,0,-0.3) rot=(0,0,1;0rad)
  Tool = -> Fusion080
FEATURE [Part::Cut] Cut036
  Base = -> Box023
  Tool = -> Cut035
FEATURE [Part::Fillet] Fillet027
  Base = -> Cut036
  Edges = 1 edges r=0.7: [Edge13]
FEATURE [Part::Fillet] Fillet028
  Base = -> Fillet027
  Edges = 1 edges r=0.7: [Edge13]
FEATURE [Part::Fillet] Fillet029
  Base = -> Fillet028
  Edges = 1 edges r=0.7: [Edge16]
FEATURE [Part::Fillet] Fillet030
  Base = -> Fillet029
  Edges = 1 edges r=0.7: [Edge11]
FEATURE [Part::Fillet] Fillet031
  Base = -> Fillet030
  Edges = 1 edges r=0.7: [Edge10]
FEATURE [Part::Fillet] Fillet032
  Base = -> Fillet031
  Edges = 1 edges r=1.2: [Edge5]
FEATURE [Part::Fillet] Fillet033
  Base = -> Fillet032
  Edges = 1 edges r=1.2: [Edge12]
FEATURE [Part::Fillet] Fillet034  label="wireHousingRetainer"
  Base = -> Fillet033
  Edges = 1 edges r=2: [Edge1]
  Placement = pos=(0.3,0,0) rot=(0,0,1;0rad)
FEATURE [Part::Feature] Face099
  shape: bbox 3.5 x 17.8 x 2e-07 mm, 1 faces, 0 solids (baked)
FEATURE [Part::Revolution] Revolve107  label="removeToCreateScrewAndThreadedInsertHole034"
  Angle = 360
  Axis = (0,1,0)
  Base = (0,0,0)
  FaceMakerClass = Part::FaceMakerBullseye
  Placement = pos=(12.5,0,10) rot=(0,0,1;0rad)
  Solid = false
  Source = -> Face099
  Symmetric = false
FEATURE [Part::Feature] Face100
  shape: bbox 3.5 x 17.8 x 2e-07 mm, 1 faces, 0 solids (baked)
FEATURE [Part::Revolution] Revolve108  label="removeToCreateScrewAndThreadedInsertHole035"
  Angle = 360
  Axis = (0,1,0)
  Base = (0,0,0)
  FaceMakerClass = Part::FaceMakerBullseye
  Placement = pos=(12.5,0,62) rot=(0,0,1;0rad)
  Solid = false
  Source = -> Face100
  Symmetric = false
FEATURE [Part::Feature] Face101
  shape: bbox 3.5 x 17.8 x 2e-07 mm, 1 faces, 0 solids (baked)
FEATURE [Part::Revolution] Revolve109  label="removeToCreateScrewAndThreadedInsertHole036"
  Angle = 360
  Axis = (0,1,0)
  Base = (0,0,0)
  FaceMakerClass = Part::FaceMakerBullseye
  Placement = pos=(89.5,0,68.5) rot=(0,0,1;0rad)
  Solid = false
  Source = -> Face101
  Symmetric = false
FEATURE [Part::Feature] Face102
  shape: bbox 3.5 x 17.8 x 2e-07 mm, 1 faces, 0 solids (baked)
FEATURE [Part::Revolution] Revolve110  label="removeToCreateScrewAndThreadedInsertHole037"
  Angle = 360
  Axis = (0,1,0)
  Base = (0,0,0)
  FaceMakerClass = Part::FaceMakerBullseye
  Placement = pos=(89.5,0,3.5) rot=(0,0,1;0rad)
  Solid = false
  Source = -> Face102
  Symmetric = false
FEATURE [Part::Feature] Face103
  shape: bbox 3.5 x 17.8 x 2e-07 mm, 1 faces, 0 solids (baked)
FEATURE [Part::Revolution] Revolve111  label="removeToCreateScrewAndThreadedInsertHole038"
  Angle = 360
  Axis = (0,1,0)
  Base = (0,0,0)
  FaceMakerClass = Part::FaceMakerBullseye
  Placement = pos=(109.5,4.7,3.5) rot=(0,0,1;0rad)
  Solid = false
  Source = -> Face103
  Symmetric = false
FEATURE [Part::Feature] Face104
  shape: bbox 3.5 x 17.8 x 2e-07 mm, 1 faces, 0 solids (baked)
FEATURE [Part::Revolution] Revolve112  label="removeToCreateScrewAndThreadedInsertHole039"
  Angle = 360
  Axis = (0,1,0)
  Base = (0,0,0)
  FaceMakerClass = Part::FaceMakerBullseye
  Placement = pos=(109.5,4.7,68.5) rot=(0,0,1;0rad)
  Solid = false
  Source = -> Face104
  Symmetric = false
FEATURE [Part::MultiFuse] Fusion081  label="removeToCreateScrewAndThreadedInsertHole040"
  Shapes = -> [Revolve107,Revolve108,Revolve109,Revolve110,Revolve111,Revolve112]
FEATURE [Part::MultiFuse] Fusion082  label="casePillars002"
  Shapes = -> [Revolve094,Revolve092,Revolve090,Revolve089,Revolve091,Revolve093]
FEATURE [Part::Cut] Cut037  label="casePillars003"
  Base = -> Fusion082
  Tool = -> Fusion081
FEATURE [Sketcher::SketchObject] Sketch051
  FullyConstrained = true
  Placement = pos=(117,19,0) rot=(0.57735,0.57735,0.57735;2.0944rad)
  sketch-geometry (48):
    g0: LineSegment StartX=-49.19 StartY=69.25 StartZ=0 EndX=-49.19 EndY=66.25 EndZ=0
    g1: LineSegment StartX=-49.19 StartY=63.5 StartZ=0 EndX=-49.19 EndY=60.5 EndZ=0
    g2: LineSegment StartX=-49.19 StartY=57.75 StartZ=0 EndX=-49.19 EndY=54.75 EndZ=0
    g3: LineSegment StartX=-49.19 StartY=52 StartZ=0 EndX=-49.19 EndY=49 EndZ=0
    g4: LineSegment StartX=-49.19 StartY=46.25 StartZ=0 EndX=-49.19 EndY=43.25 EndZ=0
    g5: LineSegment StartX=-49.19 StartY=40.5 StartZ=0 EndX=-49.19 EndY=37.5 EndZ=0
    g6: LineSegment StartX=-49.19 StartY=34.5 StartZ=0 EndX=-49.19 EndY=31.5 EndZ=0
    g7: LineSegment StartX=-49.19 StartY=28.75 StartZ=0 EndX=-49.19 EndY=25.75 EndZ=0
    g8: LineSegment StartX=-49.19 StartY=23 StartZ=0 EndX=-49.19 EndY=20 EndZ=0
    g9: LineSegment StartX=-49.19 StartY=17.25 StartZ=0 EndX=-49.19 EndY=14.25 EndZ=0
    g10: LineSegment StartX=-49.19 StartY=11.5 StartZ=0 EndX=-49.19 EndY=8.5 EndZ=0
    g11: LineSegment StartX=-49.19 StartY=5.75 StartZ=0 EndX=-49.19 EndY=2.75 EndZ=0
    g12: ArcOfCircle CenterX=-1.5 CenterY=67.75 CenterZ=0 NormalX=0 NormalY=0 NormalZ=1 AngleXU=0 Radius=1.5 StartAngle=4.71239 EndAngle=7.85398
    g13: ArcOfCircle CenterX=-1.5 CenterY=62 CenterZ=0 NormalX=0 NormalY=0 NormalZ=1 AngleXU=0 Radius=1.5 StartAngle=4.71239 EndAngle=7.85398
    g14: ArcOfCircle CenterX=-1.5 CenterY=56.25 CenterZ=0 NormalX=0 NormalY=0 NormalZ=1 AngleXU=0 Radius=1.5 StartAngle=4.71239 EndAngle=7.85398
    g15: ArcOfCircle CenterX=-11.49 CenterY=50.5 CenterZ=0 NormalX=0 NormalY=0 NormalZ=1 AngleXU=0 Radius=1.5 StartAngle=4.71239 EndAngle=7.85398
    g16: ArcOfCircle CenterX=-16.28 CenterY=44.75 CenterZ=0 NormalX=0 NormalY=0 NormalZ=1 AngleXU=0 Radius=1.5 StartAngle=4.71239 EndAngle=7.85398
    g17: ArcOfCircle CenterX=-18.2337 CenterY=39 CenterZ=0 NormalX=0 NormalY=0 NormalZ=1 AngleXU=0 Radius=1.5 StartAngle=4.71485 EndAngle=7.85398
    g18: ArcOfCircle CenterX=-16.2837 CenterY=27.25 CenterZ=0 NormalX=0 NormalY=0 NormalZ=1 AngleXU=0 Radius=1.5 StartAngle=4.71485 EndAngle=7.85398
    g19: ArcOfCircle CenterX=-18.2337 CenterY=33 CenterZ=0 NormalX=0 NormalY=0 NormalZ=1 AngleXU=0 Radius=1.5 StartAngle=4.71485 EndAngle=7.85398
    g20: ArcOfCircle CenterX=-11.49 CenterY=21.5 CenterZ=0 NormalX=0 NormalY=0 NormalZ=1 AngleXU=0 Radius=1.5 StartAngle=4.71239 EndAngle=7.85398
    g21: ArcOfCircle CenterX=-1.5 CenterY=4.25 CenterZ=0 NormalX=0 NormalY=0 NormalZ=1 AngleXU=0 Radius=1.5 StartAngle=4.71239 EndAngle=7.85398
    g22: ArcOfCircle CenterX=-1.5 CenterY=10 CenterZ=0 NormalX=0 NormalY=0 NormalZ=1 AngleXU=0 Radius=1.5 StartAngle=4.71239 EndAngle=7.85398
    g23: ArcOfCircle CenterX=-1.5 CenterY=15.75 CenterZ=0 NormalX=0 NormalY=0 NormalZ=1 AngleXU=0 Radius=1.5 StartAngle=4.71239 EndAngle=7.85398
    g24: LineSegment StartX=-49.19 StartY=69.25 StartZ=0 EndX=-1.5 EndY=69.25 EndZ=0
    g25: LineSegment StartX=-49.19 StartY=66.25 StartZ=0 EndX=-1.5 EndY=66.25 EndZ=0
    g26: LineSegment StartX=-49.19 StartY=63.5 StartZ=0 EndX=-1.5 EndY=63.5 EndZ=0
    g27: LineSegment StartX=-49.19 StartY=60.5 StartZ=0 EndX=-1.5 EndY=60.5 EndZ=0
    g28: LineSegment StartX=-49.19 StartY=57.75 StartZ=0 EndX=-1.5 EndY=57.75 EndZ=0
    g29: LineSegment StartX=-49.19 StartY=54.75 StartZ=0 EndX=-1.5 EndY=54.75 EndZ=0
    g30: LineSegment StartX=-49.19 StartY=52 StartZ=0 EndX=-11.49 EndY=52 EndZ=0
    g31: LineSegment StartX=-49.19 StartY=49 StartZ=0 EndX=-11.49 EndY=49 EndZ=0
    g32: LineSegment StartX=-49.19 StartY=46.25 StartZ=0 EndX=-16.28 EndY=46.25 EndZ=0
    g33: LineSegment StartX=-49.19 StartY=43.25 StartZ=0 EndX=-16.28 EndY=43.25 EndZ=0
    g34: LineSegment StartX=-49.19 StartY=40.5 StartZ=0 EndX=-18.2337 EndY=40.5 EndZ=0
    g35: LineSegment StartX=-49.19 StartY=37.5 StartZ=0 EndX=-18.23 EndY=37.5 EndZ=0
    g36: LineSegment StartX=-49.19 StartY=34.5 StartZ=0 EndX=-18.2337 EndY=34.5 EndZ=0
    g37: LineSegment StartX=-49.19 StartY=31.5 StartZ=0 EndX=-18.23 EndY=31.5 EndZ=0
    g38: LineSegment StartX=-49.19 StartY=28.75 StartZ=0 EndX=-16.2837 EndY=28.75 EndZ=0
    g39: LineSegment StartX=-49.19 StartY=25.75 StartZ=0 EndX=-16.28 EndY=25.75 EndZ=0
    g40: LineSegment StartX=-49.19 StartY=23 StartZ=0 EndX=-11.49 EndY=23 EndZ=0
    g41: LineSegment StartX=-49.19 StartY=20 StartZ=0 EndX=-11.49 EndY=20 EndZ=0
    g42: LineSegment StartX=-49.19 StartY=17.25 StartZ=0 EndX=-1.5 EndY=17.25 EndZ=0
    g43: LineSegment StartX=-49.19 StartY=14.25 StartZ=0 EndX=-1.5 EndY=14.25 EndZ=0
    g44: LineSegment StartX=-49.19 StartY=11.5 StartZ=0 EndX=-1.5 EndY=11.5 EndZ=0
    g45: LineSegment StartX=-49.19 StartY=8.5 StartZ=0 EndX=-1.5 EndY=8.5 EndZ=0
    g46: LineSegment StartX=-49.19 StartY=5.75 StartZ=0 EndX=-1.5 EndY=5.75 EndZ=0
    g47: LineSegment StartX=-49.19 StartY=2.75 StartZ=0 EndX=-1.5 EndY=2.75 EndZ=0
  constraints (120):
    c: Vertical(g0)
    c: Distance(g0) = 3
    c: Block(g0)
    c: Vertical(g1)
    c: Distance(g1) = 3
    c: Vertical(g2)
    c: Equal(g0,g2) = 3
    c: Block(g2)
    c: Vertical(g3)
    c: Equal(g1,g3) = 3
    c: Vertical(g4)
    c: Equal(g0,g4) = 3
    c: Block(g4)
    c: Vertical(g5)
    c: Equal(g1,g5) = 3
    c: Vertical(g6)
    c: Equal(g0,g6) = 3
    c: Block(g6)
    c: Vertical(g7)
    c: Equal(g1,g7) = 3
    c: Vertical(g8)
    c: Equal(g0,g8) = 3
    c: Block(g8)
    c: Vertical(g9)
    c: Equal(g1,g9) = 3
    c: Vertical(g10)
    c: Equal(g0,g10) = 3
    c: Block(g10)
    c: Vertical(g11)
    c: Equal(g1,g11) = 3
    c: Block(g12)
    c: Block(g13)
    c: Block(g14)
    c: Block(g15)
    c: Block(g16)
    c: Block(g17)
    c: Block(g18)
    c: Block(g19)
    c: Block(g20)
    c: Block(g21)
    c: Block(g22)
    c: Block(g23)
    c: Block(g11)
    c: Block(g9)
    c: Block(g7)
    c: Block(g5)
    c: Block(g3)
    c: Block(g1)
    c: Coincident(g24,g0)
    c: Coincident(g24,g12)
    c: Horizontal(g24)
    c: Coincident(g25,g0)
    c: Coincident(g25,g12)
    c: Horizontal(g25)
    c: Coincident(g26,g1)
    c: Coincident(g26,g13)
    c: Horizontal(g26)
    c: Coincident(g27,g1)
    c: Coincident(g27,g13)
    c: Horizontal(g27)
    c: Coincident(g28,g2)
    c: Coincident(g28,g14)
    c: Horizontal(g28)
    c: Coincident(g29,g2)
    c: Coincident(g29,g14)
    c: Horizontal(g29)
    c: Coincident(g30,g3)
    c: Coincident(g30,g15)
    c: Horizontal(g30)
    c: Coincident(g31,g3)
    c: Coincident(g31,g15)
    c: Horizontal(g31)
    c: Coincident(g32,g4)
    c: Coincident(g32,g16)
    c: Horizontal(g32)
    c: Coincident(g33,g4)
    c: Coincident(g33,g16)
    c: Horizontal(g33)
    c: Coincident(g34,g5)
    c: Coincident(g34,g17)
    c: Horizontal(g34)
    c: Coincident(g35,g5)
    c: Coincident(g35,g17)
    c: Horizontal(g35)
    c: Coincident(g36,g6)
    c: Coincident(g36,g19)
    c: Horizontal(g36)
    c: Coincident(g37,g6)
    c: Coincident(g37,g19)
    c: Horizontal(g37)
    c: Coincident(g38,g7)
    c: Coincident(g38,g18)
    c: Horizontal(g38)
    c: Coincident(g39,g7)
    c: Coincident(g39,g18)
    c: Horizontal(g39)
    c: Coincident(g40,g8)
    c: Coincident(g40,g20)
    c: Horizontal(g40)
    c: Coincident(g41,g8)
    c: Coincident(g41,g20)
    c: Horizontal(g41)
    c: Coincident(g42,g9)
    c: Coincident(g42,g23)
    c: Horizontal(g42)
    c: Coincident(g43,g9)
    c: Coincident(g43,g23)
    c: Horizontal(g43)
    c: Coincident(g44,g10)
    c: Coincident(g44,g22)
    c: Horizontal(g44)
    c: Coincident(g45,g10)
    c: Coincident(g45,g22)
    c: Horizontal(g45)
    c: Coincident(g46,g11)
    c: Coincident(g46,g21)
    c: Horizontal(g46)
    c: Coincident(g47,g11)
    c: Coincident(g47,g21)
    c: Horizontal(g47)
FEATURE [Part::Extrusion] Extrude042
  Base = -> Sketch051
  Dir = (1,-2e-16,2e-16)
  DirMode = 2
  FaceMakerClass = Part::FaceMakerBullseye
  LengthFwd = 19
  LengthRev = 0
  Placement = pos=(-19,0,0) rot=(0,0,1;0rad)
  Solid = true
  Symmetric = false
FEATURE [Part::Fillet] Fillet035  label="removeToCreateVentalationHoles"
  Base = -> Extrude042
  Edges = <same value as first occurrence — deduplicated (x6 in doc)>
  Placement = pos=(7,0,0) rot=(0,0,1;0rad)
FEATURE [Part::Cut] Cut038  label="top017"
  Base = -> Cut033
  Tool = -> Fillet035
FEATURE [Sketcher::SketchObject] Sketch052  label="bottomSketch001"
  FullyConstrained = true
  sketch-geometry (45):
    g0: LineSegment StartX=6.29999 StartY=8 StartZ=0 EndX=3.29999 EndY=8 EndZ=0
    g1: LineSegment StartX=3.29999 StartY=8 StartZ=0 EndX=3.29999 EndY=-6.03275e-07 EndZ=0
    g2: ArcOfCircle CenterX=8.29999 CenterY=5 CenterZ=0 NormalX=0 NormalY=0 NormalZ=1 AngleXU=0 Radius=2 StartAngle=3.14159 EndAngle=4.71239
    g3: LineSegment StartX=6.29999 StartY=8 StartZ=0 EndX=6.29999 EndY=5 EndZ=0
    g4: ArcOfCircle CenterX=105 CenterY=19 CenterZ=0 NormalX=0 NormalY=0 NormalZ=1 AngleXU=0 Radius=12.7 StartAngle=4.71239 EndAngle=5.94289
    g5-g11: Circle x7 (B-spline internal-alignment scaffolding for g12; pole/knot coordinates omitted)
    g12: BSplineCurve PolesCount=7 KnotsCount=5 Degree=3 IsPeriodic=0
    g13-g17: GeomPoint x5 (B-spline internal-alignment scaffolding for g12; pole/knot coordinates omitted)
    g18: ArcOfCircle CenterX=105 CenterY=19 CenterZ=0 NormalX=0 NormalY=0 NormalZ=1 AngleXU=0 Radius=15.7 StartAngle=5.81226 EndAngle=6.28319
    g19: BSplineCurve PolesCount=5 KnotsCount=3 Degree=3 IsPeriodic=0
    g20: LineSegment StartX=8.29999 StartY=3 StartZ=0 EndX=101.7 EndY=3 EndZ=0
    g21: LineSegment StartX=3.29999 StartY=-6.03275e-07 StartZ=0 EndX=105 EndY=-6.03275e-07 EndZ=0
    g22: LineSegment StartX=120.974 StartY=8.71251 StartZ=0 EndX=122.332 EndY=7.83778 EndZ=0
    g23: LineSegment StartX=105 StartY=-6.03274e-07 StartZ=0 EndX=113 EndY=-6.03274e-07 EndZ=0
    g24: ArcOfCircle CenterX=105 CenterY=19 CenterZ=0 NormalX=0 NormalY=0 NormalZ=1 AngleXU=0 Radius=20.6155 StartAngle=5.11091 EndAngle=5.71103
    g25: ArcOfCircle CenterX=117.7 CenterY=19 CenterZ=0 NormalX=0 NormalY=0 NormalZ=1 AngleXU=0 Radius=3 StartAngle=1.2e-15 EndAngle=2.10468
    g26: Circle CenterX=116.345 CenterY=16.3232 CenterZ=0 NormalX=0 NormalY=0 NormalZ=1 AngleXU=0 Radius=1
    g27: Circle CenterX=117.24 CenterY=15.7584 CenterZ=0 NormalX=0 NormalY=0 NormalZ=1 AngleXU=0 Radius=1
    g28: Circle CenterX=116.972 CenterY=14.7612 CenterZ=0 NormalX=0 NormalY=0 NormalZ=1 AngleXU=0 Radius=1
    g29: BSplineCurve PolesCount=3 KnotsCount=2 Degree=2 IsPeriodic=0
    g30: GeomPoint X=116.345 Y=16.3232 Z=0
    g31: GeomPoint X=116.972 Y=14.7612 Z=0
    g32: Circle CenterX=115.828 CenterY=17.157 CenterZ=0 NormalX=0 NormalY=0 NormalZ=1 AngleXU=0 Radius=1
    g33: Circle CenterX=115.841 CenterY=16.639 CenterZ=0 NormalX=0 NormalY=0 NormalZ=1 AngleXU=0 Radius=1
    g34: Circle CenterX=116.345 CenterY=16.3232 CenterZ=0 NormalX=0 NormalY=0 NormalZ=1 AngleXU=0 Radius=1
    g35: BSplineCurve PolesCount=3 KnotsCount=2 Degree=2 IsPeriodic=0
    g36: GeomPoint X=115.828 Y=17.157 Z=0
    g37: GeomPoint X=116.345 Y=16.3232 Z=0
    g38: LineSegment StartX=115.828 StartY=17.157 StartZ=0 EndX=115.828 EndY=20.8307 EndZ=0
    g39: Circle CenterX=115.828 CenterY=20.8307 CenterZ=0 NormalX=0 NormalY=0 NormalZ=1 AngleXU=0 Radius=1
    g40: Circle CenterX=115.831 CenterY=21.3396 CenterZ=0 NormalX=0 NormalY=0 NormalZ=1 AngleXU=0 Radius=1
    g41: Circle CenterX=116.173 CenterY=21.5825 CenterZ=0 NormalX=0 NormalY=0 NormalZ=1 AngleXU=0 Radius=1
    g42: BSplineCurve PolesCount=3 KnotsCount=2 Degree=2 IsPeriodic=0
    g43: GeomPoint X=115.828 Y=20.8307 Z=0
    g44: GeomPoint X=116.173 Y=21.5825 Z=0
  constraints (70):
    c: Horizontal(g0)
    c: Distance(g0) = 3
    c: Coincident(g1,g0)
    c: Vertical(g1)
    c: Block(g2)
    c: Block(g0)
    c: Coincident(g3,g0)
    c: Coincident(g3,g2)
    c: Vertical(g3)
    c: Block(g1)
    c: Block(g4)
    c: Coincident(g19,g4)
    c: Block(g19)
    c: Equal(g5, g6-g11) x6
    c: InternalAlignment(g5-g11 -> g12) x7
    c: InternalAlignment(g13-g17 -> g12) x5
    c: Block(g12)
    c: Coincident(g18,g12)
    c: Block(g18)
    c: Coincident(g20,g2)
    c: Coincident(g20,g19)
    c: Horizontal(g20)
    c: Distance(g20) = 93.4
    c: Coincident(g21,g1)
    c: Horizontal(g21)
    c: Distance(g21) = 101.7
    c: Horizontal(g23)
    c: Distance(g23) = 8
    c: Coincident(g24,g23)
    c: Block(g23)
    c: Coincident(g22,g24)
    c: Block(g24)
    c: Block(g22)
    c: Distance(g22) = 1.61553
    c: Coincident(g25,g18)
    c: Block(g25)
    c: Weight(g26) = 1
    c: Equal(g26,g27)
    c: Equal(g26,g28)
    c: Coincident(g29,g4)
    c: InternalAlignment(g26,g29)
    c: InternalAlignment(g27,g29)
    c: InternalAlignment(g28,g29)
    c: InternalAlignment(g30,g29)
    c: InternalAlignment(g31,g29)
    c: Block(g29)
    c: Weight(g32) = 1
    c: Equal(g32,g33)
    c: Equal(g32,g34)
    c: Coincident(g35,g29)
    c: InternalAlignment(g32,g35)
    c: InternalAlignment(g33,g35)
    c: InternalAlignment(g34,g35)
    c: InternalAlignment(g36,g35)
    c: InternalAlignment(g37,g35)
    c: Block(g35)
    c: Coincident(g38,g35)
    c: Vertical(g38)
    c: Block(g38)
    c: Coincident(g42,g38)
    c: Weight(g39) = 1
    c: Equal(g39,g40)
    c: Equal(g39,g41)
    c: Coincident(g42,g25)
    c: InternalAlignment(g39,g42)
    c: InternalAlignment(g40,g42)
    c: InternalAlignment(g41,g42)
    c: InternalAlignment(g43,g42)
    c: InternalAlignment(g44,g42)
    c: Block(g42)
FEATURE [Part::Extrusion] Extrude043  label="bottom010"
  Base = -> Sketch052
  Dir = (0,0,1)
  DirMode = 2
  FaceMakerClass = Part::FaceMakerBullseye
  LengthFwd = 71.4
  LengthRev = 0
  Placement = pos=(0,0,0.3) rot=(0,0,1;0rad)
  Solid = true
  Symmetric = false
FEATURE [Sketcher::SketchObject] Sketch053  label="topSketch013"
  FullyConstrained = true
  sketch-geometry (22):
    g0: LineSegment StartX=5.21097e-06 StartY=3 StartZ=0 EndX=5.21097e-06 EndY=19 EndZ=0
    g1: ArcOfCircle CenterX=19 CenterY=19 CenterZ=0 NormalX=0 NormalY=0 NormalZ=1 AngleXU=0 Radius=19 StartAngle=1.5708 EndAngle=3.14159
    g2: ArcOfCircle CenterX=19 CenterY=19 CenterZ=0 NormalX=0 NormalY=0 NormalZ=1 AngleXU=0 Radius=16 StartAngle=1.5708 EndAngle=3.14159
    g3: LineSegment StartX=114 StartY=35 StartZ=0 EndX=19 EndY=35 EndZ=0
    g4: LineSegment StartX=5.21097e-06 StartY=3 StartZ=0 EndX=5.21097e-06 EndY=0 EndZ=0
    g5: LineSegment StartX=3 StartY=0 StartZ=0 EndX=5.21097e-06 EndY=0 EndZ=0
    g6: LineSegment StartX=3 StartY=19 StartZ=0 EndX=3 EndY=0 EndZ=0
    g7: LineSegment StartX=19 StartY=38 StartZ=0 EndX=124 EndY=38 EndZ=0
    g8: Circle CenterX=119 CenterY=35 CenterZ=0 NormalX=0 NormalY=0 NormalZ=1 AngleXU=0 Radius=1
    g9: Circle CenterX=121 CenterY=35 CenterZ=0 NormalX=0 NormalY=0 NormalZ=1 AngleXU=0 Radius=1
    g10: Circle CenterX=121 CenterY=33 CenterZ=0 NormalX=0 NormalY=0 NormalZ=1 AngleXU=0 Radius=1
    g11: BSplineCurve PolesCount=3 KnotsCount=2 Degree=2 IsPeriodic=0
    g12: GeomPoint X=119 Y=35 Z=0
    g13: GeomPoint X=121 Y=33 Z=0
    g14: LineSegment StartX=119 StartY=35 StartZ=0 EndX=114 EndY=35 EndZ=0
    g15: ArcOfCircle CenterX=105 CenterY=19 CenterZ=0 NormalX=0 NormalY=0 NormalZ=1 AngleXU=0 Radius=16 StartAngle=5.60905 EndAngle=6.28319
    g16: LineSegment StartX=121 StartY=33 StartZ=0 EndX=121 EndY=19 EndZ=0
    g17: LineSegment StartX=117.5 StartY=9.01251 StartZ=0 EndX=121.163 EndY=9.0125 EndZ=0
    g18: ArcOfCircle CenterX=105 CenterY=19 CenterZ=0 NormalX=0 NormalY=0 NormalZ=1 AngleXU=0 Radius=20.6155 StartAngle=5.7297 EndAngle=6.28319
    g19: LineSegment StartX=121.163 StartY=9.0125 StartZ=0 EndX=122.538 EndY=8.16329 EndZ=0
    g20: LineSegment StartX=124 StartY=38 StartZ=0 EndX=125.616 EndY=38 EndZ=0
    g21: LineSegment StartX=125.616 StartY=19 StartZ=0 EndX=125.616 EndY=38 EndZ=0
  constraints (50):
    c: Vertical(g0)
    c: Block(g0)
    c: Coincident(g1,g0)
    c: Block(g1)
    c: Coincident(g2,g1)
    c: Block(g2)
    c: Coincident(g3,g2)
    c: Horizontal(g3)
    c: Tangent(g3,g2)
    c: Coincident(g4,g0)
    c: Distance(g4) = 3
    c: Vertical(g4)
    c: Coincident(g5,g4)
    c: Horizontal(g5)
    c: Coincident(g6,g2)
    c: Coincident(g6,g5)
    c: Vertical(g6)
    c: Horizontal(g7)
    c: Distance(g7) = 105
    c: Coincident(g7,g1)
    c: Block(g3)
    c: Weight(g8) = 1
    c: Equal(g8,g9)
    c: Equal(g8,g10)
    c: InternalAlignment(g8,g11)
    c: InternalAlignment(g9,g11)
    c: InternalAlignment(g10,g11)
    c: InternalAlignment(g12,g11)
    c: InternalAlignment(g13,g11)
    c: Block(g11)
    c: Coincident(g14,g11)
    c: Coincident(g14,g3)
    c: Horizontal(g14)
    c: Block(g15)
    c: Coincident(g16,g11)
    c: Coincident(g16,g15)
    c: Vertical(g16)
    c: Distance(g16) = 14
    c: Coincident(g17,g15)
    c: Block(g18)
    c: Coincident(g19,g18)
    c: Coincident(g20,g7)
    c: Horizontal(g20)
    c: Vertical(g21)
    c: Coincident(g20,g21)
    c: Block(g20)
    c: Block(g21)
    c: Block(g19)
    c: Block(g17)
    c: Distance(g20) = 1.61553
FEATURE [Part::Extrusion] Extrude044
  Base = -> Sketch053
  Dir = (0,0,1)
  DirMode = 2
  FaceMakerClass = Part::FaceMakerBullseye
  LengthFwd = 72
  LengthRev = 0
  Solid = true
  Symmetric = false
FEATURE [Part::Fillet] Fillet036  label="top018"
  Base = -> Extrude044
  Edges = 1 edges r=2: [Edge41]
FEATURE [Sketcher::SketchObject] Sketch054
  FullyConstrained = false
  Placement = pos=(0,0,0) rot=(1,0,0;1.5708rad)
  sketch-geometry (24):
    g0: ArcOfCircle CenterX=-4 CenterY=-10.5 CenterZ=0 NormalX=0 NormalY=0 NormalZ=1 AngleXU=0 Radius=1.5 StartAngle=6e-16 EndAngle=3.14159
    g1: ArcOfCircle CenterX=-34.2 CenterY=-10.5 CenterZ=0 NormalX=0 NormalY=0 NormalZ=1 AngleXU=0 Radius=1.5 StartAngle=0 EndAngle=3.14159
    g2: ArcOfCircle CenterX=-34.2 CenterY=-27.7 CenterZ=0 NormalX=0 NormalY=0 NormalZ=1 AngleXU=0 Radius=1.5 StartAngle=3.14159 EndAngle=6.28319
    g3: ArcOfCircle CenterX=-4 CenterY=-27.7 CenterZ=0 NormalX=0 NormalY=0 NormalZ=1 AngleXU=0 Radius=1.5 StartAngle=3.1416 EndAngle=6.28319
    g4: ArcOfCircle CenterX=-10 CenterY=-4.3 CenterZ=0 NormalX=0 NormalY=0 NormalZ=1 AngleXU=0 Radius=1.5 StartAngle=2e-16 EndAngle=3.14159
    g5: ArcOfCircle CenterX=-16.1 CenterY=-1.8 CenterZ=0 NormalX=0 NormalY=0 NormalZ=1 AngleXU=0 Radius=1.5 StartAngle=5e-16 EndAngle=3.14159
    g6: ArcOfCircle CenterX=-22.1 CenterY=-1.8 CenterZ=0 NormalX=0 NormalY=0 NormalZ=1 AngleXU=0 Radius=1.5 StartAngle=5e-16 EndAngle=3.14159
    g7: ArcOfCircle CenterX=-28.2 CenterY=-4.3 CenterZ=0 NormalX=0 NormalY=0 NormalZ=1 AngleXU=0 Radius=1.5 StartAngle=2e-16 EndAngle=3.14159
    g8: ArcOfCircle CenterX=-10 CenterY=-33.9 CenterZ=0 NormalX=0 NormalY=0 NormalZ=1 AngleXU=0 Radius=1.5 StartAngle=3.14159 EndAngle=6.28319
    g9: ArcOfCircle CenterX=-16.1 CenterY=-36.4 CenterZ=0 NormalX=0 NormalY=0 NormalZ=1 AngleXU=0 Radius=1.5 StartAngle=3.14159 EndAngle=6.28319
    g10: ArcOfCircle CenterX=-22.1 CenterY=-36.4 CenterZ=0 NormalX=0 NormalY=0 NormalZ=1 AngleXU=0 Radius=1.5 StartAngle=3.14159 EndAngle=6.28319
    g11: ArcOfCircle CenterX=-28.2 CenterY=-33.9 CenterZ=0 NormalX=0 NormalY=0 NormalZ=1 AngleXU=0 Radius=1.5 StartAngle=3.14159 EndAngle=6.28319
    g12: LineSegment StartX=-35.7 StartY=-10.5 StartZ=0 EndX=-35.7 EndY=-27.7 EndZ=0
    g13: LineSegment StartX=-32.7 StartY=-10.5 StartZ=0 EndX=-32.7 EndY=-27.7 EndZ=0
    g14: LineSegment StartX=-29.7 StartY=-33.9 StartZ=0 EndX=-29.7 EndY=-4.3 EndZ=0
    g15: LineSegment StartX=-26.7 StartY=-33.9 StartZ=0 EndX=-26.7 EndY=-4.3 EndZ=0
    g16: LineSegment StartX=-2.5 StartY=-10.5 StartZ=0 EndX=-2.5 EndY=-27.7 EndZ=0
    g17: LineSegment StartX=-8.5 StartY=-4.3 StartZ=0 EndX=-8.5 EndY=-33.9 EndZ=0
    g18: LineSegment StartX=-5.5 StartY=-10.5 StartZ=0 EndX=-5.5 EndY=-27.7 EndZ=0
    g19: LineSegment StartX=-11.5 StartY=-4.3 StartZ=0 EndX=-11.5 EndY=-33.9 EndZ=0
    g20: LineSegment StartX=-14.6 StartY=-1.8 StartZ=0 EndX=-14.6 EndY=-36.4 EndZ=0
    g21: LineSegment StartX=-17.6 StartY=-1.8 StartZ=0 EndX=-17.6 EndY=-36.4 EndZ=0
    g22: LineSegment StartX=-20.6 StartY=-36.4 StartZ=0 EndX=-20.6 EndY=-1.8 EndZ=0
    g23: LineSegment StartX=-23.6 StartY=-1.8 StartZ=0 EndX=-23.6 EndY=-36.4 EndZ=0
  constraints (48):
    c: Block(g0)
    c: Block(g1)
    c: Block(g2)
    c: Block(g3)
    c: Block(g4)
    c: Block(g5)
    c: Block(g6)
    c: Block(g7)
    c: Block(g8)
    c: Block(g9)
    c: Block(g10)
    c: Block(g11)
    c: Coincident(g12,g1)
    c: Coincident(g12,g2)
    c: Vertical(g12)
    c: Coincident(g13,g1)
    c: Coincident(g13,g2)
    c: Vertical(g13)
    c: Coincident(g14,g11)
    c: Coincident(g14,g7)
    c: Vertical(g14)
    c: Coincident(g15,g11)
    c: Coincident(g15,g7)
    c: Vertical(g15)
    c: Coincident(g16,g0)
    c: Coincident(g16,g3)
    c: Vertical(g16)
    c: Coincident(g17,g4)
    c: Coincident(g17,g8)
    c: Vertical(g17)
    c: Coincident(g18,g0)
    c: Coincident(g18,g3)
    c: Vertical(g18)
    c: Coincident(g19,g4)
    c: Coincident(g19,g8)
    c: Vertical(g19)
    c: Coincident(g20,g5)
    c: Coincident(g20,g9)
    c: Vertical(g20)
    c: Coincident(g21,g5)
    c: Coincident(g21,g9)
    c: Vertical(g21)
    c: Coincident(g22,g10)
    c: Coincident(g22,g6)
    c: Vertical(g22)
    c: Coincident(g23,g6)
    c: Coincident(g23,g10)
    c: Vertical(g23)
FEATURE [Part::Extrusion] Extrude045  label="removeToCreateFanGrillHoles003"
  Base = -> Sketch054
  Dir = (0,-1,6e-16)
  DirMode = 2
  FaceMakerClass = Part::FaceMakerBullseye
  LengthFwd = 10
  LengthRev = 0
  Placement = pos=(65.4,44,54.82) rot=(0,0,1;0rad)
  Solid = true
  Symmetric = false
FEATURE [Part::Feature] Face105 .. Face108  x4 (patterned run collapsed; names and placements below)
  shape: bbox 3.5 x 17.8 x 2e-07 mm, 1 faces, 0 solids (baked)
FEATURE [Part::Revolution] Revolve113  label="removeToCreateScrewAndThreadedInsertHole041"
  Angle = 360
  Axis = (0,1,0)
  Base = (0,0,0)
  FaceMakerClass = Part::FaceMakerBullseye
  Placement = pos=(62.3,30.3,19.7) rot=(0,0,1;0rad)
  Solid = false
  Source = -> Face105
  Symmetric = false
FEATURE [Part::Revolution] Revolve114  label="removeToCreateScrewAndThreadedInsertHole042"
  Angle = 360
  Axis = (0,1,0)
  Base = (0,0,0)
  FaceMakerClass = Part::FaceMakerBullseye
  Placement = pos=(62.3,30.3,51.7) rot=(0,0,1;0rad)
  Solid = false
  Source = -> Face106
  Symmetric = false
FEATURE [Part::Revolution] Revolve115  label="removeToCreateScrewAndThreadedInsertHole043"
  Angle = 360
  Axis = (0,1,0)
  Base = (0,0,0)
  FaceMakerClass = Part::FaceMakerBullseye
  Placement = pos=(30.3,30.3,19.7) rot=(0,0,1;0rad)
  Solid = false
  Source = -> Face107
  Symmetric = false
FEATURE [Part::Revolution] Revolve116  label="removeToCreateScrewAndThreadedInsertHole044"
  Angle = 360
  Axis = (0,1,0)
  Base = (0,0,0)
  FaceMakerClass = Part::FaceMakerBullseye
  Placement = pos=(30.3,30.3,51.7) rot=(0,0,1;0rad)
  Solid = false
  Source = -> Face108
  Symmetric = false
FEATURE [Part::MultiFuse] Fusion083  label="createThreadedInsertHolesForFan004"
  Shapes = -> [Revolve113,Revolve114,Revolve115,Revolve116]
FEATURE [Part::Box] Box024  label="removeToCreteHoleForPlugHousing026"
  AttacherType = Attacher::AttachEngine3D
  Height = 28.6
  Length = 10
  Placement = pos=(-2,0,21.7) rot=(0,0,1;0rad)
  Width = 19
FEATURE [Part::Cylinder] Cylinder038  label="removeToCreteHoleForPlugHousing027"
  Angle = 360
  AttacherType = Attacher::AttachEngine3D
  Height = 20
  Placement = pos=(-2,19,36) rot=(0,1,0;1.5708rad)
  Radius = 14.3
FEATURE [Part::MultiFuse] Fusion084  label="removeToCreteHoleForPlugHousing028"
  Shapes = -> [Box024,Cylinder038]
FEATURE [Part::Cylinder] Cylinder039
  Angle = 360
  AttacherType = Attacher::AttachEngine3D
  Height = 20
  Placement = pos=(0,0,36.15) rot=(0,0,1;0rad)
  Radius = 14.3
FEATURE [Part::Cylinder] Cylinder040
  Angle = 360
  AttacherType = Attacher::AttachEngine3D
  Height = 10
  Placement = pos=(0,0,36.15) rot=(0,0,1;0rad)
  Radius = 4
FEATURE [Part::Box] Box025  label="removeToCreteHoleForPlugHousing030"
  AttacherType = Attacher::AttachEngine3D
  Height = 28.6
  Length = 20
  Placement = pos=(106.15,0,21.7) rot=(0,0,1;0rad)
  Width = 19
FEATURE [Part::MultiFuse] Fusion086  label="removeToCreteHoleForPlugHousing031"
  Placement = pos=(70,19,36) rot=(0,1,0;1.5708rad)
  Shapes = -> [Cylinder039,Cylinder040]
FEATURE [Part::MultiFuse] Fusion085  label="removeToCreteHoleForPlugHousing029"
  Shapes = -> [Box025,Fusion086]
FEATURE [Sketcher::SketchObject] Sketch055
  FullyConstrained = true
  Placement = pos=(117,19,0) rot=(0.57735,0.57735,0.57735;2.0944rad)
  sketch-geometry (48):
    g0: LineSegment StartX=-49.19 StartY=69.25 StartZ=0 EndX=-49.19 EndY=66.25 EndZ=0
    g1: LineSegment StartX=-49.19 StartY=63.5 StartZ=0 EndX=-49.19 EndY=60.5 EndZ=0
    g2: LineSegment StartX=-49.19 StartY=57.75 StartZ=0 EndX=-49.19 EndY=54.75 EndZ=0
    g3: LineSegment StartX=-49.19 StartY=52 StartZ=0 EndX=-49.19 EndY=49 EndZ=0
    g4: LineSegment StartX=-49.19 StartY=46.25 StartZ=0 EndX=-49.19 EndY=43.25 EndZ=0
    g5: LineSegment StartX=-49.19 StartY=40.5 StartZ=0 EndX=-49.19 EndY=37.5 EndZ=0
    g6: LineSegment StartX=-49.19 StartY=34.5 StartZ=0 EndX=-49.19 EndY=31.5 EndZ=0
    g7: LineSegment StartX=-49.19 StartY=28.75 StartZ=0 EndX=-49.19 EndY=25.75 EndZ=0
    g8: LineSegment StartX=-49.19 StartY=23 StartZ=0 EndX=-49.19 EndY=20 EndZ=0
    g9: LineSegment StartX=-49.19 StartY=17.25 StartZ=0 EndX=-49.19 EndY=14.25 EndZ=0
    g10: LineSegment StartX=-49.19 StartY=11.5 StartZ=0 EndX=-49.19 EndY=8.5 EndZ=0
    g11: LineSegment StartX=-49.19 StartY=5.75 StartZ=0 EndX=-49.19 EndY=2.75 EndZ=0
    g12: ArcOfCircle CenterX=-1.5 CenterY=67.75 CenterZ=0 NormalX=0 NormalY=0 NormalZ=1 AngleXU=0 Radius=1.5 StartAngle=4.71239 EndAngle=7.85398
    g13: ArcOfCircle CenterX=-1.5 CenterY=62 CenterZ=0 NormalX=0 NormalY=0 NormalZ=1 AngleXU=0 Radius=1.5 StartAngle=4.71239 EndAngle=7.85398
    g14: ArcOfCircle CenterX=-1.5 CenterY=56.25 CenterZ=0 NormalX=0 NormalY=0 NormalZ=1 AngleXU=0 Radius=1.5 StartAngle=4.71239 EndAngle=7.85398
    g15: ArcOfCircle CenterX=-11.49 CenterY=50.5 CenterZ=0 NormalX=0 NormalY=0 NormalZ=1 AngleXU=0 Radius=1.5 StartAngle=4.71239 EndAngle=7.85398
    g16: ArcOfCircle CenterX=-16.28 CenterY=44.75 CenterZ=0 NormalX=0 NormalY=0 NormalZ=1 AngleXU=0 Radius=1.5 StartAngle=4.71239 EndAngle=7.85398
    g17: ArcOfCircle CenterX=-18.2337 CenterY=39 CenterZ=0 NormalX=0 NormalY=0 NormalZ=1 AngleXU=0 Radius=1.5 StartAngle=4.71485 EndAngle=7.85398
    g18: ArcOfCircle CenterX=-16.2837 CenterY=27.25 CenterZ=0 NormalX=0 NormalY=0 NormalZ=1 AngleXU=0 Radius=1.5 StartAngle=4.71485 EndAngle=7.85398
    g19: ArcOfCircle CenterX=-18.2337 CenterY=33 CenterZ=0 NormalX=0 NormalY=0 NormalZ=1 AngleXU=0 Radius=1.5 StartAngle=4.71485 EndAngle=7.85398
    g20: ArcOfCircle CenterX=-11.49 CenterY=21.5 CenterZ=0 NormalX=0 NormalY=0 NormalZ=1 AngleXU=0 Radius=1.5 StartAngle=4.71239 EndAngle=7.85398
    g21: ArcOfCircle CenterX=-1.5 CenterY=4.25 CenterZ=0 NormalX=0 NormalY=0 NormalZ=1 AngleXU=0 Radius=1.5 StartAngle=4.71239 EndAngle=7.85398
    g22: ArcOfCircle CenterX=-1.5 CenterY=10 CenterZ=0 NormalX=0 NormalY=0 NormalZ=1 AngleXU=0 Radius=1.5 StartAngle=4.71239 EndAngle=7.85398
    g23: ArcOfCircle CenterX=-1.5 CenterY=15.75 CenterZ=0 NormalX=0 NormalY=0 NormalZ=1 AngleXU=0 Radius=1.5 StartAngle=4.71239 EndAngle=7.85398
    g24: LineSegment StartX=-49.19 StartY=69.25 StartZ=0 EndX=-1.5 EndY=69.25 EndZ=0
    g25: LineSegment StartX=-49.19 StartY=66.25 StartZ=0 EndX=-1.5 EndY=66.25 EndZ=0
    g26: LineSegment StartX=-49.19 StartY=63.5 StartZ=0 EndX=-1.5 EndY=63.5 EndZ=0
    g27: LineSegment StartX=-49.19 StartY=60.5 StartZ=0 EndX=-1.5 EndY=60.5 EndZ=0
    g28: LineSegment StartX=-49.19 StartY=57.75 StartZ=0 EndX=-1.5 EndY=57.75 EndZ=0
    g29: LineSegment StartX=-49.19 StartY=54.75 StartZ=0 EndX=-1.5 EndY=54.75 EndZ=0
    g30: LineSegment StartX=-49.19 StartY=52 StartZ=0 EndX=-11.49 EndY=52 EndZ=0
    g31: LineSegment StartX=-49.19 StartY=49 StartZ=0 EndX=-11.49 EndY=49 EndZ=0
    g32: LineSegment StartX=-49.19 StartY=46.25 StartZ=0 EndX=-16.28 EndY=46.25 EndZ=0
    g33: LineSegment StartX=-49.19 StartY=43.25 StartZ=0 EndX=-16.28 EndY=43.25 EndZ=0
    g34: LineSegment StartX=-49.19 StartY=40.5 StartZ=0 EndX=-18.2337 EndY=40.5 EndZ=0
    g35: LineSegment StartX=-49.19 StartY=37.5 StartZ=0 EndX=-18.23 EndY=37.5 EndZ=0
    g36: LineSegment StartX=-49.19 StartY=34.5 StartZ=0 EndX=-18.2337 EndY=34.5 EndZ=0
    g37: LineSegment StartX=-49.19 StartY=31.5 StartZ=0 EndX=-18.23 EndY=31.5 EndZ=0
    g38: LineSegment StartX=-49.19 StartY=28.75 StartZ=0 EndX=-16.2837 EndY=28.75 EndZ=0
    g39: LineSegment StartX=-49.19 StartY=25.75 StartZ=0 EndX=-16.28 EndY=25.75 EndZ=0
    g40: LineSegment StartX=-49.19 StartY=23 StartZ=0 EndX=-11.49 EndY=23 EndZ=0
    g41: LineSegment StartX=-49.19 StartY=20 StartZ=0 EndX=-11.49 EndY=20 EndZ=0
    g42: LineSegment StartX=-49.19 StartY=17.25 StartZ=0 EndX=-1.5 EndY=17.25 EndZ=0
    g43: LineSegment StartX=-49.19 StartY=14.25 StartZ=0 EndX=-1.5 EndY=14.25 EndZ=0
    g44: LineSegment StartX=-49.19 StartY=11.5 StartZ=0 EndX=-1.5 EndY=11.5 EndZ=0
    g45: LineSegment StartX=-49.19 StartY=8.5 StartZ=0 EndX=-1.5 EndY=8.5 EndZ=0
    g46: LineSegment StartX=-49.19 StartY=5.75 StartZ=0 EndX=-1.5 EndY=5.75 EndZ=0
    g47: LineSegment StartX=-49.19 StartY=2.75 StartZ=0 EndX=-1.5 EndY=2.75 EndZ=0
  constraints (120):
    c: Vertical(g0)
    c: Distance(g0) = 3
    c: Block(g0)
    c: Vertical(g1)
    c: Distance(g1) = 3
    c: Vertical(g2)
    c: Equal(g0,g2) = 3
    c: Block(g2)
    c: Vertical(g3)
    c: Equal(g1,g3) = 3
    c: Vertical(g4)
    c: Equal(g0,g4) = 3
    c: Block(g4)
    c: Vertical(g5)
    c: Equal(g1,g5) = 3
    c: Vertical(g6)
    c: Equal(g0,g6) = 3
    c: Block(g6)
    c: Vertical(g7)
    c: Equal(g1,g7) = 3
    c: Vertical(g8)
    c: Equal(g0,g8) = 3
    c: Block(g8)
    c: Vertical(g9)
    c: Equal(g1,g9) = 3
    c: Vertical(g10)
    c: Equal(g0,g10) = 3
    c: Block(g10)
    c: Vertical(g11)
    c: Equal(g1,g11) = 3
    c: Block(g12)
    c: Block(g13)
    c: Block(g14)
    c: Block(g15)
    c: Block(g16)
    c: Block(g17)
    c: Block(g18)
    c: Block(g19)
    c: Block(g20)
    c: Block(g21)
    c: Block(g22)
    c: Block(g23)
    c: Block(g11)
    c: Block(g9)
    c: Block(g7)
    c: Block(g5)
    c: Block(g3)
    c: Block(g1)
    c: Coincident(g24,g0)
    c: Coincident(g24,g12)
    c: Horizontal(g24)
    c: Coincident(g25,g0)
    c: Coincident(g25,g12)
    c: Horizontal(g25)
    c: Coincident(g26,g1)
    c: Coincident(g26,g13)
    c: Horizontal(g26)
    c: Coincident(g27,g1)
    c: Coincident(g27,g13)
    c: Horizontal(g27)
    c: Coincident(g28,g2)
    c: Coincident(g28,g14)
    c: Horizontal(g28)
    c: Coincident(g29,g2)
    c: Coincident(g29,g14)
    c: Horizontal(g29)
    c: Coincident(g30,g3)
    c: Coincident(g30,g15)
    c: Horizontal(g30)
    c: Coincident(g31,g3)
    c: Coincident(g31,g15)
    c: Horizontal(g31)
    c: Coincident(g32,g4)
    c: Coincident(g32,g16)
    c: Horizontal(g32)
    c: Coincident(g33,g4)
    c: Coincident(g33,g16)
    c: Horizontal(g33)
    c: Coincident(g34,g5)
    c: Coincident(g34,g17)
    c: Horizontal(g34)
    c: Coincident(g35,g5)
    c: Coincident(g35,g17)
    c: Horizontal(g35)
    c: Coincident(g36,g6)
    c: Coincident(g36,g19)
    c: Horizontal(g36)
    c: Coincident(g37,g6)
    c: Coincident(g37,g19)
    c: Horizontal(g37)
    c: Coincident(g38,g7)
    c: Coincident(g38,g18)
    c: Horizontal(g38)
    c: Coincident(g39,g7)
    c: Coincident(g39,g18)
    c: Horizontal(g39)
    c: Coincident(g40,g8)
    c: Coincident(g40,g20)
    c: Horizontal(g40)
    c: Coincident(g41,g8)
    c: Coincident(g41,g20)
    c: Horizontal(g41)
    c: Coincident(g42,g9)
    c: Coincident(g42,g23)
    c: Horizontal(g42)
    c: Coincident(g43,g9)
    c: Coincident(g43,g23)
    c: Horizontal(g43)
    c: Coincident(g44,g10)
    c: Coincident(g44,g22)
    c: Horizontal(g44)
    c: Coincident(g45,g10)
    c: Coincident(g45,g22)
    c: Horizontal(g45)
    c: Coincident(g46,g11)
    c: Coincident(g46,g21)
    c: Horizontal(g46)
    c: Coincident(g47,g11)
    c: Coincident(g47,g21)
    c: Horizontal(g47)
FEATURE [Part::Extrusion] Extrude046
  Base = -> Sketch055
  Dir = (1,0,0)
  DirMode = 2
  FaceMakerClass = Part::FaceMakerBullseye
  LengthFwd = 23
  LengthRev = 0
  Placement = pos=(-19,0,0) rot=(0,0,1;0rad)
  Solid = true
  Symmetric = false
FEATURE [Part::Fillet] Fillet038  label="removeToCreateVentalationHoles001"
  Base = -> Extrude046
  Edges = <same value as first occurrence — deduplicated (x6 in doc)>
  Placement = pos=(7,0,0) rot=(0,0,1;0rad)
FEATURE [Sketcher::SketchObject] Sketch056  label="topSketch014"
  FullyConstrained = true
  sketch-geometry (22):
    g0: LineSegment StartX=5.21097e-06 StartY=3 StartZ=0 EndX=5.21097e-06 EndY=19 EndZ=0
    g1: ArcOfCircle CenterX=19 CenterY=19 CenterZ=0 NormalX=0 NormalY=0 NormalZ=1 AngleXU=0 Radius=19 StartAngle=1.5708 EndAngle=3.14159
    g2: ArcOfCircle CenterX=19 CenterY=19 CenterZ=0 NormalX=0 NormalY=0 NormalZ=1 AngleXU=0 Radius=16 StartAngle=1.5708 EndAngle=3.14159
    g3: LineSegment StartX=114 StartY=35 StartZ=0 EndX=19 EndY=35 EndZ=0
    g4: LineSegment StartX=5.21097e-06 StartY=3 StartZ=0 EndX=5.21097e-06 EndY=0 EndZ=0
    g5: LineSegment StartX=3 StartY=0 StartZ=0 EndX=5.21097e-06 EndY=0 EndZ=0
    g6: LineSegment StartX=3 StartY=19 StartZ=0 EndX=3 EndY=0 EndZ=0
    g7: LineSegment StartX=19 StartY=38 StartZ=0 EndX=124 EndY=38 EndZ=0
    g8: Circle CenterX=119 CenterY=35 CenterZ=0 NormalX=0 NormalY=0 NormalZ=1 AngleXU=0 Radius=1
    g9: Circle CenterX=121 CenterY=35 CenterZ=0 NormalX=0 NormalY=0 NormalZ=1 AngleXU=0 Radius=1
    g10: Circle CenterX=121 CenterY=33 CenterZ=0 NormalX=0 NormalY=0 NormalZ=1 AngleXU=0 Radius=1
    g11: BSplineCurve PolesCount=3 KnotsCount=2 Degree=2 IsPeriodic=0
    g12: GeomPoint X=119 Y=35 Z=0
    g13: GeomPoint X=121 Y=33 Z=0
    g14: LineSegment StartX=119 StartY=35 StartZ=0 EndX=114 EndY=35 EndZ=0
    g15: ArcOfCircle CenterX=105 CenterY=19 CenterZ=0 NormalX=0 NormalY=0 NormalZ=1 AngleXU=0 Radius=16 StartAngle=5.60905 EndAngle=6.28319
    g16: LineSegment StartX=121 StartY=33 StartZ=0 EndX=121 EndY=19 EndZ=0
    g17: LineSegment StartX=117.5 StartY=9.01251 StartZ=0 EndX=121.163 EndY=9.0125 EndZ=0
    g18: ArcOfCircle CenterX=105 CenterY=19 CenterZ=0 NormalX=0 NormalY=0 NormalZ=1 AngleXU=0 Radius=20.6155 StartAngle=5.7297 EndAngle=6.28319
    g19: LineSegment StartX=121.163 StartY=9.0125 StartZ=0 EndX=122.538 EndY=8.16329 EndZ=0
    g20: LineSegment StartX=124 StartY=38 StartZ=0 EndX=125.616 EndY=38 EndZ=0
    g21: LineSegment StartX=125.616 StartY=19 StartZ=0 EndX=125.616 EndY=38 EndZ=0
  constraints (49):
    c: Vertical(g0)
    c: Block(g0)
    c: Coincident(g1,g0)
    c: Block(g1)
    c: Coincident(g2,g1)
    c: Block(g2)
    c: Coincident(g3,g2)
    c: Horizontal(g3)
    c: Tangent(g3,g2)
    c: Coincident(g4,g0)
    c: Distance(g4) = 3
    c: Vertical(g4)
    c: Coincident(g5,g4)
    c: Horizontal(g5)
    c: Coincident(g6,g2)
    c: Coincident(g6,g5)
    c: Vertical(g6)
    c: Horizontal(g7)
    c: Distance(g7) = 105
    c: Coincident(g7,g1)
    c: Block(g3)
    c: Weight(g8) = 1
    c: Equal(g8,g9)
    c: Equal(g8,g10)
    c: InternalAlignment(g8,g11)
    c: InternalAlignment(g9,g11)
    c: InternalAlignment(g10,g11)
    c: InternalAlignment(g12,g11)
    c: InternalAlignment(g13,g11)
    c: Block(g11)
    c: Coincident(g14,g11)
    c: Coincident(g14,g3)
    c: Horizontal(g14)
    c: Block(g15)
    c: Coincident(g16,g11)
    c: Coincident(g16,g15)
    c: Vertical(g16)
    c: Distance(g16) = 14
    c: Coincident(g17,g15)
    c: Block(g18)
    c: Coincident(g19,g18)
    c: Coincident(g20,g7)
    c: Horizontal(g20)
    c: Vertical(g21)
    c: Coincident(g20,g21)
    c: Block(g20)
    c: Block(g21)
    c: Block(g19)
    c: Block(g17)
FEATURE [Part::Box] Box026  label="removeToCreteHoleForPlugHousing032"
  AttacherType = Attacher::AttachEngine3D
  Height = 28.6
  Length = 10
  Placement = pos=(-2,0,21.7) rot=(0,0,1;0rad)
  Width = 19
FEATURE [Part::Feature] Face109 .. Face112  x4 (patterned run collapsed; names and placements below)
  shape: bbox 3.5 x 17.8 x 2e-07 mm, 1 faces, 0 solids (baked)
FEATURE [Part::Revolution] Revolve117  label="removeToCreateScrewAndThreadedInsertHole045"
  Angle = 360
  Axis = (0,1,0)
  Base = (0,0,0)
  FaceMakerClass = Part::FaceMakerBullseye
  Placement = pos=(62.3,30.3,19.7) rot=(0,0,1;0rad)
  Solid = false
  Source = -> Face109
  Symmetric = false
FEATURE [Part::Revolution] Revolve118  label="removeToCreateScrewAndThreadedInsertHole046"
  Angle = 360
  Axis = (0,1,0)
  Base = (0,0,0)
  FaceMakerClass = Part::FaceMakerBullseye
  Placement = pos=(62.3,30.3,51.7) rot=(0,0,1;0rad)
  Solid = false
  Source = -> Face110
  Symmetric = false
FEATURE [Part::Revolution] Revolve119  label="removeToCreateScrewAndThreadedInsertHole047"
  Angle = 360
  Axis = (0,1,0)
  Base = (0,0,0)
  FaceMakerClass = Part::FaceMakerBullseye
  Placement = pos=(30.3,30.3,19.7) rot=(0,0,1;0rad)
  Solid = false
  Source = -> Face111
  Symmetric = false
FEATURE [Part::Revolution] Revolve120  label="removeToCreateScrewAndThreadedInsertHole048"
  Angle = 360
  Axis = (0,1,0)
  Base = (0,0,0)
  FaceMakerClass = Part::FaceMakerBullseye
  Placement = pos=(30.3,30.3,51.7) rot=(0,0,1;0rad)
  Solid = false
  Source = -> Face112
  Symmetric = false
FEATURE [Part::MultiFuse] Fusion087  label="createThreadedInsertHolesForFan005"
  Shapes = -> [Revolve117,Revolve118,Revolve119,Revolve120]
FEATURE [Part::Extrusion] Extrude047
  Base = -> Sketch056
  Dir = (0,0,1)
  DirMode = 2
  FaceMakerClass = Part::FaceMakerBullseye
  LengthFwd = 72
  LengthRev = 0
  Solid = true
  Symmetric = false
FEATURE [Part::Fillet] Fillet039  label="top019"
  Base = -> Extrude047
  Edges = 1 edges r=2: [Edge35]
FEATURE [Sketcher::SketchObject] Sketch057
  FullyConstrained = false
  Placement = pos=(0,0,0) rot=(1,0,0;1.5708rad)
  sketch-geometry (24):
    g0: ArcOfCircle CenterX=-4 CenterY=-10.5 CenterZ=0 NormalX=0 NormalY=0 NormalZ=1 AngleXU=0 Radius=1.5 StartAngle=6e-16 EndAngle=3.14159
    g1: ArcOfCircle CenterX=-34.2 CenterY=-10.5 CenterZ=0 NormalX=0 NormalY=0 NormalZ=1 AngleXU=0 Radius=1.5 StartAngle=0 EndAngle=3.14159
    g2: ArcOfCircle CenterX=-34.2 CenterY=-27.7 CenterZ=0 NormalX=0 NormalY=0 NormalZ=1 AngleXU=0 Radius=1.5 StartAngle=3.14159 EndAngle=6.28319
    g3: ArcOfCircle CenterX=-4 CenterY=-27.7 CenterZ=0 NormalX=0 NormalY=0 NormalZ=1 AngleXU=0 Radius=1.5 StartAngle=3.1416 EndAngle=6.28319
    g4: ArcOfCircle CenterX=-10 CenterY=-4.3 CenterZ=0 NormalX=0 NormalY=0 NormalZ=1 AngleXU=0 Radius=1.5 StartAngle=2e-16 EndAngle=3.14159
    g5: ArcOfCircle CenterX=-16.1 CenterY=-1.8 CenterZ=0 NormalX=0 NormalY=0 NormalZ=1 AngleXU=0 Radius=1.5 StartAngle=5e-16 EndAngle=3.14159
    g6: ArcOfCircle CenterX=-22.1 CenterY=-1.8 CenterZ=0 NormalX=0 NormalY=0 NormalZ=1 AngleXU=0 Radius=1.5 StartAngle=5e-16 EndAngle=3.14159
    g7: ArcOfCircle CenterX=-28.2 CenterY=-4.3 CenterZ=0 NormalX=0 NormalY=0 NormalZ=1 AngleXU=0 Radius=1.5 StartAngle=2e-16 EndAngle=3.14159
    g8: ArcOfCircle CenterX=-10 CenterY=-33.9 CenterZ=0 NormalX=0 NormalY=0 NormalZ=1 AngleXU=0 Radius=1.5 StartAngle=3.14159 EndAngle=6.28319
    g9: ArcOfCircle CenterX=-16.1 CenterY=-36.4 CenterZ=0 NormalX=0 NormalY=0 NormalZ=1 AngleXU=0 Radius=1.5 StartAngle=3.14159 EndAngle=6.28319
    g10: ArcOfCircle CenterX=-22.1 CenterY=-36.4 CenterZ=0 NormalX=0 NormalY=0 NormalZ=1 AngleXU=0 Radius=1.5 StartAngle=3.14159 EndAngle=6.28319
    g11: ArcOfCircle CenterX=-28.2 CenterY=-33.9 CenterZ=0 NormalX=0 NormalY=0 NormalZ=1 AngleXU=0 Radius=1.5 StartAngle=3.14159 EndAngle=6.28319
    g12: LineSegment StartX=-35.7 StartY=-10.5 StartZ=0 EndX=-35.7 EndY=-27.7 EndZ=0
    g13: LineSegment StartX=-32.7 StartY=-10.5 StartZ=0 EndX=-32.7 EndY=-27.7 EndZ=0
    g14: LineSegment StartX=-29.7 StartY=-33.9 StartZ=0 EndX=-29.7 EndY=-4.3 EndZ=0
    g15: LineSegment StartX=-26.7 StartY=-33.9 StartZ=0 EndX=-26.7 EndY=-4.3 EndZ=0
    g16: LineSegment StartX=-2.5 StartY=-10.5 StartZ=0 EndX=-2.5 EndY=-27.7 EndZ=0
    g17: LineSegment StartX=-8.5 StartY=-4.3 StartZ=0 EndX=-8.5 EndY=-33.9 EndZ=0
    g18: LineSegment StartX=-5.5 StartY=-10.5 StartZ=0 EndX=-5.5 EndY=-27.7 EndZ=0
    g19: LineSegment StartX=-11.5 StartY=-4.3 StartZ=0 EndX=-11.5 EndY=-33.9 EndZ=0
    g20: LineSegment StartX=-14.6 StartY=-1.8 StartZ=0 EndX=-14.6 EndY=-36.4 EndZ=0
    g21: LineSegment StartX=-17.6 StartY=-1.8 StartZ=0 EndX=-17.6 EndY=-36.4 EndZ=0
    g22: LineSegment StartX=-20.6 StartY=-36.4 StartZ=0 EndX=-20.6 EndY=-1.8 EndZ=0
    g23: LineSegment StartX=-23.6 StartY=-1.8 StartZ=0 EndX=-23.6 EndY=-36.4 EndZ=0
  constraints (48):
    c: Block(g0)
    c: Block(g1)
    c: Block(g2)
    c: Block(g3)
    c: Block(g4)
    c: Block(g5)
    c: Block(g6)
    c: Block(g7)
    c: Block(g8)
    c: Block(g9)
    c: Block(g10)
    c: Block(g11)
    c: Coincident(g12,g1)
    c: Coincident(g12,g2)
    c: Vertical(g12)
    c: Coincident(g13,g1)
    c: Coincident(g13,g2)
    c: Vertical(g13)
    c: Coincident(g14,g11)
    c: Coincident(g14,g7)
    c: Vertical(g14)
    c: Coincident(g15,g11)
    c: Coincident(g15,g7)
    c: Vertical(g15)
    c: Coincident(g16,g0)
    c: Coincident(g16,g3)
    c: Vertical(g16)
    c: Coincident(g17,g4)
    c: Coincident(g17,g8)
    c: Vertical(g17)
    c: Coincident(g18,g0)
    c: Coincident(g18,g3)
    c: Vertical(g18)
    c: Coincident(g19,g4)
    c: Coincident(g19,g8)
    c: Vertical(g19)
    c: Coincident(g20,g5)
    c: Coincident(g20,g9)
    c: Vertical(g20)
    c: Coincident(g21,g5)
    c: Coincident(g21,g9)
    c: Vertical(g21)
    c: Coincident(g22,g10)
    c: Coincident(g22,g6)
    c: Vertical(g22)
    c: Coincident(g23,g6)
    c: Coincident(g23,g10)
    c: Vertical(g23)
FEATURE [Part::Extrusion] Extrude048  label="removeToCreateFanGrillHoles004"
  Base = -> Sketch057
  Dir = (0,-1,6e-16)
  DirMode = 2
  FaceMakerClass = Part::FaceMakerBullseye
  LengthFwd = 10
  LengthRev = 0
  Placement = pos=(65.4,44,54.82) rot=(0,0,1;0rad)
  Solid = true
  Symmetric = false
FEATURE [Part::Cut] Cut040  label="top021"
  Base = -> Fillet039
  Tool = -> Extrude048
FEATURE [Part::Cylinder] Cylinder041  label="removeToCreteHoleForPlugHousing034"
  Angle = 360
  AttacherType = Attacher::AttachEngine3D
  Height = 20
  Placement = pos=(-2,19,36) rot=(0,1,0;1.5708rad)
  Radius = 14.3
FEATURE [Part::MultiFuse] Fusion089  label="removeToCreteHoleForPlugHousing035"
  Shapes = -> [Box026,Cylinder041]
FEATURE [Part::Cylinder] Cylinder042
  Angle = 360
  AttacherType = Attacher::AttachEngine3D
  Height = 20
  Placement = pos=(0,0,36.15) rot=(0,0,1;0rad)
  Radius = 14.3
FEATURE [Part::Cylinder] Cylinder043
  Angle = 360
  AttacherType = Attacher::AttachEngine3D
  Height = 10
  Placement = pos=(0,0,36.15) rot=(0,0,1;0rad)
  Radius = 4
FEATURE [Part::Box] Box027  label="removeToCreteHoleForPlugHousing036"
  AttacherType = Attacher::AttachEngine3D
  Height = 28.6
  Length = 20
  Placement = pos=(106.15,0,21.7) rot=(0,0,1;0rad)
  Width = 19
FEATURE [Part::Cut] Cut041  label="top022"
  Base = -> Cut040
  Tool = -> Fusion087
FEATURE [Part::Cut] Cut039  label="top020"
  Base = -> Cut041
  Tool = -> Fusion089
FEATURE [Part::MultiFuse] Fusion090  label="removeToCreteHoleForPlugHousing037"
  Placement = pos=(70,19,36) rot=(0,1,0;1.5708rad)
  Shapes = -> [Cylinder042,Cylinder043]
FEATURE [Part::MultiFuse] Fusion088  label="removeToCreteHoleForPlugHousing033"
  Shapes = -> [Box027,Fusion090]
FEATURE [Part::Cut] Cut042  label="removeToCreteHoleForPlugHousing038"
  Base = -> Cut039
  Tool = -> Fusion088
FEATURE [Part::MultiFuse] Fusion091  label="removeFromTop"
  Shapes = -> [Fillet038,Fusion085,Fusion084,Fusion083,Extrude045]
FEATURE [Part::Cut] Cut043  label="REAL TOP ====="
  Base = -> Fillet036
  Tool = -> Fusion091
FEATURE [Part::MultiFuse] Fusion092  label="caseScrewPillarBracket016"
  Shapes = -> [Extrude030,Extrude031,Extrude032,Extrude033,Extrude034,Extrude035,Extrude036,Extrude037,Box013,Box014]
FEATURE [Sketcher::SketchObject] Sketch058  label="topSketch015"
  FullyConstrained = true
  sketch-geometry (20):
    g0: LineSegment StartX=5.21097e-06 StartY=3 StartZ=0 EndX=5.21097e-06 EndY=19 EndZ=0
    g1: ArcOfCircle CenterX=19 CenterY=19 CenterZ=0 NormalX=0 NormalY=0 NormalZ=1 AngleXU=0 Radius=19 StartAngle=1.5708 EndAngle=3.14159
    g2: ArcOfCircle CenterX=19 CenterY=19 CenterZ=0 NormalX=0 NormalY=0 NormalZ=1 AngleXU=0 Radius=16 StartAngle=1.5708 EndAngle=3.14159
    g3: LineSegment StartX=114 StartY=35 StartZ=0 EndX=19 EndY=35 EndZ=0
    g4: LineSegment StartX=5.21097e-06 StartY=3 StartZ=0 EndX=5.21097e-06 EndY=0 EndZ=0
    g5: LineSegment StartX=3 StartY=0 StartZ=0 EndX=5.21097e-06 EndY=0 EndZ=0
    g6: LineSegment StartX=3 StartY=19 StartZ=0 EndX=3 EndY=0 EndZ=0
    g7: LineSegment StartX=19 StartY=38 StartZ=0 EndX=124 EndY=38 EndZ=0
    g8: Circle CenterX=119 CenterY=35 CenterZ=0 NormalX=0 NormalY=0 NormalZ=1 AngleXU=0 Radius=1
    g9: Circle CenterX=121 CenterY=35 CenterZ=0 NormalX=0 NormalY=0 NormalZ=1 AngleXU=0 Radius=1
    g10: Circle CenterX=121 CenterY=33 CenterZ=0 NormalX=0 NormalY=0 NormalZ=1 AngleXU=0 Radius=1
    g11: BSplineCurve PolesCount=3 KnotsCount=2 Degree=2 IsPeriodic=0
    g12: GeomPoint X=119 Y=35 Z=0
    g13: GeomPoint X=121 Y=33 Z=0
    g14: LineSegment StartX=119 StartY=35 StartZ=0 EndX=114 EndY=35 EndZ=0
    g15: ArcOfCircle CenterX=105 CenterY=19 CenterZ=0 NormalX=0 NormalY=0 NormalZ=1 AngleXU=0 Radius=19 StartAngle=5.7297 EndAngle=6.28319
    g16: ArcOfCircle CenterX=105 CenterY=19 CenterZ=0 NormalX=0 NormalY=0 NormalZ=1 AngleXU=0 Radius=16 StartAngle=5.60905 EndAngle=6.28319
    g17: LineSegment StartX=121 StartY=33 StartZ=0 EndX=121 EndY=19 EndZ=0
    g18: LineSegment StartX=124 StartY=38 StartZ=0 EndX=124 EndY=19 EndZ=0
    g19: LineSegment StartX=117.5 StartY=9.01251 StartZ=0 EndX=121.163 EndY=9.0125 EndZ=0
  constraints (46):
    c: Vertical(g0)
    c: Block(g0)
    c: Coincident(g1,g0)
    c: Block(g1)
    c: Coincident(g2,g1)
    c: Block(g2)
    c: Coincident(g3,g2)
    c: Horizontal(g3)
    c: Tangent(g3,g2)
    c: Coincident(g4,g0)
    c: Distance(g4) = 3
    c: Vertical(g4)
    c: Coincident(g5,g4)
    c: Horizontal(g5)
    c: Coincident(g6,g2)
    c: Coincident(g6,g5)
    c: Vertical(g6)
    c: Horizontal(g7)
    c: Distance(g7) = 105
    c: Coincident(g7,g1)
    c: Block(g3)
    c: Weight(g8) = 1
    c: Equal(g8,g9)
    c: Equal(g8,g10)
    c: InternalAlignment(g8,g11)
    c: InternalAlignment(g9,g11)
    c: InternalAlignment(g10,g11)
    c: InternalAlignment(g12,g11)
    c: InternalAlignment(g13,g11)
    c: Block(g11)
    c: Coincident(g14,g11)
    c: Coincident(g14,g3)
    c: Horizontal(g14)
    c: Block(g15)
    c: Coincident(g16,g15)
    c: Block(g16)
    c: Coincident(g17,g11)
    c: Coincident(g17,g16)
    c: Vertical(g17)
    c: Distance(g17) = 14
    c: Coincident(g18,g7)
    c: Coincident(g18,g15)
    c: Vertical(g18)
    c: Distance(g18) = 19
    c: Coincident(g19,g16)
    c: Coincident(g19,g15)
FEATURE [Part::Extrusion] Extrude049  label="top023"
  Base = -> Sketch058
  Dir = (0,0,1)
  DirMode = 2
  FaceMakerClass = Part::FaceMakerBullseye
  LengthFwd = 72
  LengthRev = 0
  Solid = true
  Symmetric = false
FEATURE [Sketcher::SketchObject] Sketch059
  FullyConstrained = true
  MapMode = 3
  Placement = pos=(0,0,0) rot=(1,0,0;1.5708rad)
  Support = -> [Extrude049]
  sketch-geometry (8):
    g0: Circle CenterX=80.351 CenterY=-67.6202 CenterZ=0 NormalX=0 NormalY=0 NormalZ=1 AngleXU=0 Radius=2
    g1: Circle CenterX=80.351 CenterY=-67.6202 CenterZ=0 NormalX=0 NormalY=0 NormalZ=1 AngleXU=0 Radius=3
    g2: Circle CenterX=80.351 CenterY=-4.92017 CenterZ=0 NormalX=0 NormalY=0 NormalZ=1 AngleXU=0 Radius=2
    g3: Circle CenterX=80.351 CenterY=-4.92017 CenterZ=0 NormalX=0 NormalY=0 NormalZ=1 AngleXU=0 Radius=3
    g4: Circle CenterX=23.851 CenterY=-4.92017 CenterZ=0 NormalX=0 NormalY=0 NormalZ=1 AngleXU=0 Radius=2
    g5: Circle CenterX=23.851 CenterY=-4.92017 CenterZ=0 NormalX=0 NormalY=0 NormalZ=1 AngleXU=0 Radius=3
    g6: Circle CenterX=23.851 CenterY=-67.6202 CenterZ=0 NormalX=0 NormalY=0 NormalZ=1 AngleXU=0 Radius=2
    g7: Circle CenterX=23.851 CenterY=-67.6202 CenterZ=0 NormalX=0 NormalY=0 NormalZ=1 AngleXU=0 Radius=3
  constraints (8):
    c: Block(g3)
    c: Block(g2)
    c: Block(g1)
    c: Block(g0)
    c: Block(g6)
    c: Block(g7)
    c: Block(g4)
    c: Block(g5)
FEATURE [Sketcher::SketchObject] Sketch060
  FullyConstrained = true
  MapMode = 3
  Placement = pos=(0,0,0) rot=(1,0,0;1.5708rad)
  Support = -> [Extrude049]
  sketch-geometry (8):
    g0: Circle CenterX=80.351 CenterY=-67.6202 CenterZ=0 NormalX=0 NormalY=0 NormalZ=1 AngleXU=0 Radius=3
    g1: Circle CenterX=80.351 CenterY=-4.92017 CenterZ=0 NormalX=0 NormalY=0 NormalZ=1 AngleXU=0 Radius=3
    g2: Circle CenterX=23.851 CenterY=-4.92017 CenterZ=0 NormalX=0 NormalY=0 NormalZ=1 AngleXU=0 Radius=3
    g3: Circle CenterX=23.851 CenterY=-67.6202 CenterZ=0 NormalX=0 NormalY=0 NormalZ=1 AngleXU=0 Radius=3
    g4: Circle CenterX=23.851 CenterY=-67.6202 CenterZ=0 NormalX=0 NormalY=0 NormalZ=1 AngleXU=0 Radius=5
    g5: Circle CenterX=80.351 CenterY=-67.6202 CenterZ=0 NormalX=0 NormalY=0 NormalZ=1 AngleXU=0 Radius=5
    g6: Circle CenterX=23.851 CenterY=-4.92017 CenterZ=0 NormalX=0 NormalY=0 NormalZ=1 AngleXU=0 Radius=5
    g7: Circle CenterX=80.351 CenterY=-4.92017 CenterZ=0 NormalX=0 NormalY=0 NormalZ=1 AngleXU=0 Radius=5
  constraints (8):
    c: Block(g1)
    c: Block(g0)
    c: Block(g3)
    c: Block(g2)
    c: Block(g5)
    c: Block(g4)
    c: Block(g6)
    c: Block(g7)
FEATURE [Sketcher::SketchObject] Sketch061
  FullyConstrained = true
  MapMode = 3
  Placement = pos=(0,0,0) rot=(1,0,0;1.5708rad)
  sketch-geometry (8):
    g0: Circle CenterX=80.351 CenterY=-67.6202 CenterZ=0 NormalX=0 NormalY=0 NormalZ=1 AngleXU=0 Radius=3
    g1: Circle CenterX=80.351 CenterY=-4.92017 CenterZ=0 NormalX=0 NormalY=0 NormalZ=1 AngleXU=0 Radius=3
    g2: Circle CenterX=23.851 CenterY=-4.92017 CenterZ=0 NormalX=0 NormalY=0 NormalZ=1 AngleXU=0 Radius=3
    g3: Circle CenterX=23.851 CenterY=-67.6202 CenterZ=0 NormalX=0 NormalY=0 NormalZ=1 AngleXU=0 Radius=3
    g4: Circle CenterX=23.851 CenterY=-67.6202 CenterZ=0 NormalX=0 NormalY=0 NormalZ=1 AngleXU=0 Radius=5
    g5: Circle CenterX=80.351 CenterY=-67.6202 CenterZ=0 NormalX=0 NormalY=0 NormalZ=1 AngleXU=0 Radius=5
    g6: Circle CenterX=23.851 CenterY=-4.92017 CenterZ=0 NormalX=0 NormalY=0 NormalZ=1 AngleXU=0 Radius=5
    g7: Circle CenterX=80.351 CenterY=-4.92017 CenterZ=0 NormalX=0 NormalY=0 NormalZ=1 AngleXU=0 Radius=5
  constraints (8):
    c: Block(g1)
    c: Block(g0)
    c: Block(g3)
    c: Block(g2)
    c: Block(g5)
    c: Block(g4)
    c: Block(g6)
    c: Block(g7)
FEATURE [Sketcher::SketchObject] Sketch062  label="topSketch016"
  FullyConstrained = true
  sketch-geometry (20):
    g0: LineSegment StartX=5.21097e-06 StartY=3 StartZ=0 EndX=5.21097e-06 EndY=19 EndZ=0
    g1: ArcOfCircle CenterX=19 CenterY=19 CenterZ=0 NormalX=0 NormalY=0 NormalZ=1 AngleXU=0 Radius=19 StartAngle=1.5708 EndAngle=3.14159
    g2: ArcOfCircle CenterX=19 CenterY=19 CenterZ=0 NormalX=0 NormalY=0 NormalZ=1 AngleXU=0 Radius=16 StartAngle=1.5708 EndAngle=3.14159
    g3: LineSegment StartX=114 StartY=35 StartZ=0 EndX=19 EndY=35 EndZ=0
    g4: LineSegment StartX=5.21097e-06 StartY=3 StartZ=0 EndX=5.21097e-06 EndY=0 EndZ=0
    g5: LineSegment StartX=3 StartY=0 StartZ=0 EndX=5.21097e-06 EndY=0 EndZ=0
    g6: LineSegment StartX=3 StartY=19 StartZ=0 EndX=3 EndY=0 EndZ=0
    g7: LineSegment StartX=19 StartY=38 StartZ=0 EndX=124 EndY=38 EndZ=0
    g8: Circle CenterX=119 CenterY=35 CenterZ=0 NormalX=0 NormalY=0 NormalZ=1 AngleXU=0 Radius=1
    g9: Circle CenterX=121 CenterY=35 CenterZ=0 NormalX=0 NormalY=0 NormalZ=1 AngleXU=0 Radius=1
    g10: Circle CenterX=121 CenterY=33 CenterZ=0 NormalX=0 NormalY=0 NormalZ=1 AngleXU=0 Radius=1
    g11: BSplineCurve PolesCount=3 KnotsCount=2 Degree=2 IsPeriodic=0
    g12: GeomPoint X=119 Y=35 Z=0
    g13: GeomPoint X=121 Y=33 Z=0
    g14: LineSegment StartX=119 StartY=35 StartZ=0 EndX=114 EndY=35 EndZ=0
    g15: ArcOfCircle CenterX=105 CenterY=19 CenterZ=0 NormalX=0 NormalY=0 NormalZ=1 AngleXU=0 Radius=19 StartAngle=5.7297 EndAngle=6.28319
    g16: ArcOfCircle CenterX=105 CenterY=19 CenterZ=0 NormalX=0 NormalY=0 NormalZ=1 AngleXU=0 Radius=16 StartAngle=5.60905 EndAngle=6.28319
    g17: LineSegment StartX=121 StartY=33 StartZ=0 EndX=121 EndY=19 EndZ=0
    g18: LineSegment StartX=124 StartY=38 StartZ=0 EndX=124 EndY=19 EndZ=0
    g19: LineSegment StartX=117.5 StartY=9.01251 StartZ=0 EndX=121.163 EndY=9.0125 EndZ=0
  constraints (46):
    c: Vertical(g0)
    c: Block(g0)
    c: Coincident(g1,g0)
    c: Block(g1)
    c: Coincident(g2,g1)
    c: Block(g2)
    c: Coincident(g3,g2)
    c: Horizontal(g3)
    c: Tangent(g3,g2)
    c: Coincident(g4,g0)
    c: Distance(g4) = 3
    c: Vertical(g4)
    c: Coincident(g5,g4)
    c: Horizontal(g5)
    c: Coincident(g6,g2)
    c: Coincident(g6,g5)
    c: Vertical(g6)
    c: Horizontal(g7)
    c: Distance(g7) = 105
    c: Coincident(g7,g1)
    c: Block(g3)
    c: Weight(g8) = 1
    c: Equal(g8,g9)
    c: Equal(g8,g10)
    c: InternalAlignment(g8,g11)
    c: InternalAlignment(g9,g11)
    c: InternalAlignment(g10,g11)
    c: InternalAlignment(g12,g11)
    c: InternalAlignment(g13,g11)
    c: Block(g11)
    c: Coincident(g14,g11)
    c: Coincident(g14,g3)
    c: Horizontal(g14)
    c: Block(g15)
    c: Coincident(g16,g15)
    c: Block(g16)
    c: Coincident(g17,g11)
    c: Coincident(g17,g16)
    c: Vertical(g17)
    c: Distance(g17) = 14
    c: Coincident(g18,g7)
    c: Coincident(g18,g15)
    c: Vertical(g18)
    c: Distance(g18) = 19
    c: Coincident(g19,g16)
    c: Coincident(g19,g15)
FEATURE [Part::Extrusion] Extrude053  label="top024"
  Base = -> Sketch062
  Dir = (0,0,1)
  DirMode = 2
  FaceMakerClass = Part::FaceMakerBullseye
  LengthFwd = 72
  LengthRev = 0
  Solid = true
  Symmetric = false
FEATURE [Sketcher::SketchObject] Sketch063
  FullyConstrained = true
  MapMode = 3
  Placement = pos=(0,0,0) rot=(1,0,0;1.5708rad)
  Support = -> [Extrude053]
  sketch-geometry (8):
    g0: Circle CenterX=80.351 CenterY=-67.6202 CenterZ=0 NormalX=0 NormalY=0 NormalZ=1 AngleXU=0 Radius=2
    g1: Circle CenterX=80.351 CenterY=-67.6202 CenterZ=0 NormalX=0 NormalY=0 NormalZ=1 AngleXU=0 Radius=3
    g2: Circle CenterX=80.351 CenterY=-4.92017 CenterZ=0 NormalX=0 NormalY=0 NormalZ=1 AngleXU=0 Radius=2
    g3: Circle CenterX=80.351 CenterY=-4.92017 CenterZ=0 NormalX=0 NormalY=0 NormalZ=1 AngleXU=0 Radius=3
    g4: Circle CenterX=23.851 CenterY=-4.92017 CenterZ=0 NormalX=0 NormalY=0 NormalZ=1 AngleXU=0 Radius=2
    g5: Circle CenterX=23.851 CenterY=-4.92017 CenterZ=0 NormalX=0 NormalY=0 NormalZ=1 AngleXU=0 Radius=3
    g6: Circle CenterX=23.851 CenterY=-67.6202 CenterZ=0 NormalX=0 NormalY=0 NormalZ=1 AngleXU=0 Radius=2
    g7: Circle CenterX=23.851 CenterY=-67.6202 CenterZ=0 NormalX=0 NormalY=0 NormalZ=1 AngleXU=0 Radius=3
  constraints (8):
    c: Block(g3)
    c: Block(g2)
    c: Block(g1)
    c: Block(g0)
    c: Block(g6)
    c: Block(g7)
    c: Block(g4)
    c: Block(g5)
FEATURE [Part::Extrusion] Extrude054
  Base = -> Sketch063
  Dir = (0,-1,2e-16)
  DirMode = 2
  FaceMakerClass = Part::FaceMakerBullseye
  LengthFwd = 6
  LengthRev = 0
  Placement = pos=(0,9,0) rot=(0,0,1;0rad)
  Solid = true
  Symmetric = false
FEATURE [Sketcher::SketchObject] Sketch064  label="topSketch017"
  FullyConstrained = true
  sketch-geometry (20):
    g0: LineSegment StartX=5.21097e-06 StartY=3 StartZ=0 EndX=5.21097e-06 EndY=19 EndZ=0
    g1: ArcOfCircle CenterX=19 CenterY=19 CenterZ=0 NormalX=0 NormalY=0 NormalZ=1 AngleXU=0 Radius=19 StartAngle=1.5708 EndAngle=3.14159
    g2: ArcOfCircle CenterX=19 CenterY=19 CenterZ=0 NormalX=0 NormalY=0 NormalZ=1 AngleXU=0 Radius=16 StartAngle=1.5708 EndAngle=3.14159
    g3: LineSegment StartX=114 StartY=35 StartZ=0 EndX=19 EndY=35 EndZ=0
    g4: LineSegment StartX=5.21097e-06 StartY=3 StartZ=0 EndX=5.21097e-06 EndY=0 EndZ=0
    g5: LineSegment StartX=3 StartY=0 StartZ=0 EndX=5.21097e-06 EndY=0 EndZ=0
    g6: LineSegment StartX=3 StartY=19 StartZ=0 EndX=3 EndY=0 EndZ=0
    g7: LineSegment StartX=19 StartY=38 StartZ=0 EndX=124 EndY=38 EndZ=0
    g8: Circle CenterX=119 CenterY=35 CenterZ=0 NormalX=0 NormalY=0 NormalZ=1 AngleXU=0 Radius=1
    g9: Circle CenterX=121 CenterY=35 CenterZ=0 NormalX=0 NormalY=0 NormalZ=1 AngleXU=0 Radius=1
    g10: Circle CenterX=121 CenterY=33 CenterZ=0 NormalX=0 NormalY=0 NormalZ=1 AngleXU=0 Radius=1
    g11: BSplineCurve PolesCount=3 KnotsCount=2 Degree=2 IsPeriodic=0
    g12: GeomPoint X=119 Y=35 Z=0
    g13: GeomPoint X=121 Y=33 Z=0
    g14: LineSegment StartX=119 StartY=35 StartZ=0 EndX=114 EndY=35 EndZ=0
    g15: ArcOfCircle CenterX=105 CenterY=19 CenterZ=0 NormalX=0 NormalY=0 NormalZ=1 AngleXU=0 Radius=19 StartAngle=5.7297 EndAngle=6.28319
    g16: ArcOfCircle CenterX=105 CenterY=19 CenterZ=0 NormalX=0 NormalY=0 NormalZ=1 AngleXU=0 Radius=16 StartAngle=5.60905 EndAngle=6.28319
    g17: LineSegment StartX=121 StartY=33 StartZ=0 EndX=121 EndY=19 EndZ=0
    g18: LineSegment StartX=124 StartY=38 StartZ=0 EndX=124 EndY=19 EndZ=0
    g19: LineSegment StartX=117.5 StartY=9.01251 StartZ=0 EndX=121.163 EndY=9.0125 EndZ=0
  constraints (46):
    c: Vertical(g0)
    c: Block(g0)
    c: Coincident(g1,g0)
    c: Block(g1)
    c: Coincident(g2,g1)
    c: Block(g2)
    c: Coincident(g3,g2)
    c: Horizontal(g3)
    c: Tangent(g3,g2)
    c: Coincident(g4,g0)
    c: Distance(g4) = 3
    c: Vertical(g4)
    c: Coincident(g5,g4)
    c: Horizontal(g5)
    c: Coincident(g6,g2)
    c: Coincident(g6,g5)
    c: Vertical(g6)
    c: Horizontal(g7)
    c: Distance(g7) = 105
    c: Coincident(g7,g1)
    c: Block(g3)
    c: Weight(g8) = 1
    c: Equal(g8,g9)
    c: Equal(g8,g10)
    c: InternalAlignment(g8,g11)
    c: InternalAlignment(g9,g11)
    c: InternalAlignment(g10,g11)
    c: InternalAlignment(g12,g11)
    c: InternalAlignment(g13,g11)
    c: Block(g11)
    c: Coincident(g14,g11)
    c: Coincident(g14,g3)
    c: Horizontal(g14)
    c: Block(g15)
    c: Coincident(g16,g15)
    c: Block(g16)
    c: Coincident(g17,g11)
    c: Coincident(g17,g16)
    c: Vertical(g17)
    c: Distance(g17) = 14
    c: Coincident(g18,g7)
    c: Coincident(g18,g15)
    c: Vertical(g18)
    c: Distance(g18) = 19
    c: Coincident(g19,g16)
    c: Coincident(g19,g15)
FEATURE [Sketcher::SketchObject] Sketch065
  FullyConstrained = true
  MapMode = 3
  Placement = pos=(0,0,0) rot=(1,0,0;1.5708rad)
  sketch-geometry (8):
    g0: Circle CenterX=80.351 CenterY=-67.6202 CenterZ=0 NormalX=0 NormalY=0 NormalZ=1 AngleXU=0 Radius=3
    g1: Circle CenterX=80.351 CenterY=-4.92017 CenterZ=0 NormalX=0 NormalY=0 NormalZ=1 AngleXU=0 Radius=3
    g2: Circle CenterX=23.851 CenterY=-4.92017 CenterZ=0 NormalX=0 NormalY=0 NormalZ=1 AngleXU=0 Radius=3
    g3: Circle CenterX=23.851 CenterY=-67.6202 CenterZ=0 NormalX=0 NormalY=0 NormalZ=1 AngleXU=0 Radius=3
    g4: Circle CenterX=23.851 CenterY=-67.6202 CenterZ=0 NormalX=0 NormalY=0 NormalZ=1 AngleXU=0 Radius=5
    g5: Circle CenterX=80.351 CenterY=-67.6202 CenterZ=0 NormalX=0 NormalY=0 NormalZ=1 AngleXU=0 Radius=5
    g6: Circle CenterX=23.851 CenterY=-4.92017 CenterZ=0 NormalX=0 NormalY=0 NormalZ=1 AngleXU=0 Radius=5
    g7: Circle CenterX=80.351 CenterY=-4.92017 CenterZ=0 NormalX=0 NormalY=0 NormalZ=1 AngleXU=0 Radius=5
  constraints (8):
    c: Block(g1)
    c: Block(g0)
    c: Block(g3)
    c: Block(g2)
    c: Block(g5)
    c: Block(g4)
    c: Block(g6)
    c: Block(g7)
FEATURE [Part::Extrusion] Extrude056
  Base = -> Sketch065
  Dir = (0,-1,2e-16)
  DirMode = 2
  FaceMakerClass = Part::FaceMakerBullseye
  LengthFwd = 2
  LengthRev = 0
  Solid = true
  Symmetric = false
FEATURE [Part::Extrusion] Extrude057  label="top025"
  Base = -> Sketch064
  Dir = (0,0,1)
  DirMode = 2
  FaceMakerClass = Part::FaceMakerBullseye
  LengthFwd = 72
  LengthRev = 0
  Solid = true
  Symmetric = false
FEATURE [Sketcher::SketchObject] Sketch066
  FullyConstrained = true
  MapMode = 3
  Placement = pos=(0,0,0) rot=(1,0,0;1.5708rad)
  Support = -> [Extrude057]
  sketch-geometry (8):
    g0: Circle CenterX=80.351 CenterY=-67.6202 CenterZ=0 NormalX=0 NormalY=0 NormalZ=1 AngleXU=0 Radius=3
    g1: Circle CenterX=80.351 CenterY=-4.92017 CenterZ=0 NormalX=0 NormalY=0 NormalZ=1 AngleXU=0 Radius=3
    g2: Circle CenterX=23.851 CenterY=-4.92017 CenterZ=0 NormalX=0 NormalY=0 NormalZ=1 AngleXU=0 Radius=3
    g3: Circle CenterX=23.851 CenterY=-67.6202 CenterZ=0 NormalX=0 NormalY=0 NormalZ=1 AngleXU=0 Radius=3
    g4: Circle CenterX=23.851 CenterY=-67.6202 CenterZ=0 NormalX=0 NormalY=0 NormalZ=1 AngleXU=0 Radius=5
    g5: Circle CenterX=80.351 CenterY=-67.6202 CenterZ=0 NormalX=0 NormalY=0 NormalZ=1 AngleXU=0 Radius=5
    g6: Circle CenterX=23.851 CenterY=-4.92017 CenterZ=0 NormalX=0 NormalY=0 NormalZ=1 AngleXU=0 Radius=5
    g7: Circle CenterX=80.351 CenterY=-4.92017 CenterZ=0 NormalX=0 NormalY=0 NormalZ=1 AngleXU=0 Radius=5
  constraints (8):
    c: Block(g1)
    c: Block(g0)
    c: Block(g3)
    c: Block(g2)
    c: Block(g5)
    c: Block(g4)
    c: Block(g6)
    c: Block(g7)
FEATURE [Part::Extrusion] Extrude055
  Base = -> Sketch066
  Dir = (0,-1,2e-16)
  DirMode = 2
  FaceMakerClass = Part::FaceMakerBullseye
  LengthFwd = 2
  LengthRev = 0
  Solid = true
  Symmetric = false
FEATURE [Part::Fillet] Fillet041
  Base = -> Extrude056
  Edges = 4 edges r=1.99: [Edge6,Edge12,Edge18,Edge24]
FEATURE [Part::Cut] Cut045
  Base = -> Extrude055
  Placement = pos=(0,6,0) rot=(0,0,1;0rad)
  Tool = -> Fillet041
FEATURE [Part::MultiFuse] Fusion095  label="pcbScrewPillars"
  Placement = pos=(-3.2,-1,72.3) rot=(0,0,1;0rad)
  Shapes = -> [Cut045,Extrude054]
FEATURE [Part::Feature] Face113
  shape: bbox 3.2 x 1.5 x 2e-07 mm, 1 faces, 0 solids (baked)
FEATURE [Part::Revolution] Revolve121  label="backCaseScrewRetainer002"
  Angle = 360
  Axis = (0,1,0)
  Base = (0,0,0)
  FaceMakerClass = Part::FaceMakerBullseye
  Placement = pos=(12.5,3,62) rot=(0,0,1;0rad)
  Solid = false
  Source = -> Face113
  Symmetric = false
FEATURE [Part::Feature] Face114
  shape: bbox 3.2 x 1.5 x 2e-07 mm, 1 faces, 0 solids (baked)
FEATURE [Part::Feature] Face115
  shape: bbox 3.2 x 1.5 x 2e-07 mm, 1 faces, 0 solids (baked)
FEATURE [Part::Feature] Face116
  shape: bbox 3.2 x 1.5 x 2e-07 mm, 1 faces, 0 solids (baked)
FEATURE [Part::Revolution] Revolve122  label="frontCaseScrewRetainer004"
  Angle = 360
  Axis = (0,1,0)
  Base = (0,0,0)
  FaceMakerClass = Part::FaceMakerBullseye
  Placement = pos=(89.5,3,68.5) rot=(0,0,1;0rad)
  Solid = false
  Source = -> Face115
  Symmetric = false
FEATURE [Part::Revolution] Revolve123  label="frontCaseScrewRetainer005"
  Angle = 360
  Axis = (0,1,0)
  Base = (0,0,0)
  FaceMakerClass = Part::FaceMakerBullseye
  Placement = pos=(89.5,3,3.5) rot=(0,0,1;0rad)
  Solid = false
  Source = -> Face116
  Symmetric = false
FEATURE [Part::Revolution] Revolve124  label="backCaseScrewRetainer003"
  Angle = 360
  Axis = (0,1,0)
  Base = (0,0,0)
  FaceMakerClass = Part::FaceMakerBullseye
  Placement = pos=(12.5,3,10) rot=(0,0,1;0rad)
  Solid = false
  Source = -> Face114
  Symmetric = false
FEATURE [Part::Feature] Face117
  shape: bbox 3.6 x 3.2 x 2e-07 mm, 1 faces, 0 solids (baked)
FEATURE [Part::Revolution] Revolve125  label="moreFrontCaseScrewRetainer004"
  Angle = 360
  Axis = (0,1,0)
  Base = (0,0,0)
  FaceMakerClass = Part::FaceMakerBullseye
  Placement = pos=(109.5,4.5,68.5) rot=(0,0,1;0rad)
  Solid = false
  Source = -> Face117
  Symmetric = false
FEATURE [Part::Feature] Face118
  shape: bbox 3.6 x 3.2 x 2e-07 mm, 1 faces, 0 solids (baked)
FEATURE [Part::Revolution] Revolve126  label="moreFrontCaseScrewRetainer005"
  Angle = 360
  Axis = (0,1,0)
  Base = (0,0,0)
  FaceMakerClass = Part::FaceMakerBullseye
  Placement = pos=(109.5,4.5,3.5) rot=(0,0,1;0rad)
  Solid = false
  Source = -> Face118
  Symmetric = false
FEATURE [Part::MultiFuse] Fusion096  label="screwRetainers001"
  Shapes = -> [Revolve126,Revolve125,Revolve124,Revolve123,Revolve122,Revolve121]
FEATURE [Part::Feature] Face119
  shape: bbox 10 x 16.5 x 2e-07 mm, 1 faces, 0 solids (baked)
FEATURE [Part::Revolution] Revolve130  label="plugHousing050"
  Angle = 360
  Axis = (0,1,0)
  Base = (0,0,0)
  FaceMakerClass = Part::FaceMakerBullseye
  Placement = pos=(0,0,36.15) rot=(0,0,1;0rad)
  Solid = false
  Source = -> Face119
  Symmetric = false
FEATURE [Part::Feature] Face120
  shape: bbox 10 x 16.5 x 2e-07 mm, 1 faces, 0 solids (baked)
FEATURE [Part::Feature] Face121
  shape: bbox 10 x 16.5 x 2e-07 mm, 1 faces, 0 solids (baked)
FEATURE [Part::Revolution] Revolve127  label="plugHousing047"
  Angle = 360
  Axis = (0,1,0)
  Base = (0,0,0)
  FaceMakerClass = Part::FaceMakerBullseye
  Placement = pos=(0,0,36.15) rot=(0,0,1;0rad)
  Solid = false
  Source = -> Face121
  Symmetric = false
FEATURE [Part::Feature] Face122
  shape: bbox 10 x 16.5 x 2e-07 mm, 1 faces, 0 solids (baked)
FEATURE [Part::Feature] Face123
  shape: bbox 10 x 16.5 x 2e-07 mm, 1 faces, 0 solids (baked)
FEATURE [Part::Revolution] Revolve128  label="plugHousing048"
  Angle = 360
  Axis = (0,1,0)
  Base = (0,0,0)
  FaceMakerClass = Part::FaceMakerBullseye
  Placement = pos=(0,0,36.15) rot=(0,0,1;0rad)
  Solid = false
  Source = -> Face123
  Symmetric = false
FEATURE [Part::MultiFuse] Fusion100  label="plugHousing054"
  Placement = pos=(0,0,0) rot=(0,0,1;1.5708rad)
  Shapes = -> [Revolve130,Revolve128]
FEATURE [Part::Feature] Face124
  shape: bbox 10 x 16.5 x 2e-07 mm, 1 faces, 0 solids (baked)
FEATURE [Part::Feature] Face125
  shape: bbox 10 x 16.5 x 2e-07 mm, 1 faces, 0 solids (baked)
FEATURE [Part::Revolution] Revolve129  label="plugHousing049"
  Angle = 360
  Axis = (0,1,0)
  Base = (0,0,0)
  FaceMakerClass = Part::FaceMakerBullseye
  Placement = pos=(0,0,36.15) rot=(0,0,1;0rad)
  Solid = false
  Source = -> Face125
  Symmetric = false
FEATURE [Part::Feature] Face126
  shape: bbox 10 x 16.5 x 2e-07 mm, 1 faces, 0 solids (baked)
FEATURE [Part::Revolution] Revolve131  label="plugHousing058"
  Angle = 360
  Axis = (0,1,0)
  Base = (0,0,0)
  FaceMakerClass = Part::FaceMakerBullseye
  Placement = pos=(0,0,36.15) rot=(0,0,1;0rad)
  Solid = false
  Source = -> Face120
  Symmetric = false
FEATURE [Part::MultiFuse] Fusion099  label="plugHousing053"
  Placement = pos=(0,0,0) rot=(0,0,1;1.5708rad)
  Shapes = -> [Revolve127,Revolve131]
FEATURE [Part::MultiFuse] Fusion102  label="plugHousing056"
  Placement = pos=(0,19,0) rot=(0,0,1;3.14159rad)
  Shapes = -> [Fusion100,Fusion099]
FEATURE [Part::Revolution] Revolve132  label="plugHousing059"
  Angle = 360
  Axis = (0,1,0)
  Base = (0,0,0)
  FaceMakerClass = Part::FaceMakerBullseye
  Placement = pos=(0,0,36.15) rot=(0,0,1;0rad)
  Solid = false
  Source = -> Face126
  Symmetric = false
FEATURE [Part::Revolution] Revolve133  label="plugHousing060"
  Angle = 360
  Axis = (0,1,0)
  Base = (0,0,0)
  FaceMakerClass = Part::FaceMakerBullseye
  Placement = pos=(0,0,36.15) rot=(0,0,1;0rad)
  Solid = false
  Source = -> Face122
  Symmetric = false
FEATURE [Part::MultiFuse] Fusion097  label="plugHousing051"
  Placement = pos=(0,0,0) rot=(0,0,1;1.5708rad)
  Shapes = -> [Revolve133,Revolve132]
FEATURE [Part::Revolution] Revolve134  label="plugHousing061"
  Angle = 360
  Axis = (0,1,0)
  Base = (0,0,0)
  FaceMakerClass = Part::FaceMakerBullseye
  Placement = pos=(0,0,36.15) rot=(0,0,1;0rad)
  Solid = false
  Source = -> Face124
  Symmetric = false
FEATURE [Part::MultiFuse] Fusion101  label="plugHousing055"
  Placement = pos=(0,0,0) rot=(0,0,1;1.5708rad)
  Shapes = -> [Revolve129,Revolve134]
FEATURE [Part::MultiFuse] Fusion098  label="plugHousing052"
  Placement = pos=(0,19,0) rot=(0,0,1;3.14159rad)
  Shapes = -> [Fusion097,Fusion101]
FEATURE [Part::MultiFuse] Fusion103  label="plugHousing057"
  Placement = pos=(122.621,0,-0.15) rot=(0,0,1;0rad)
  Shapes = -> [Fusion102,Fusion098]
FEATURE [Part::Box] Box028  label="Cube015"
  AttacherType = Attacher::AttachEngine3D
  Height = 28
  Length = 3
  Placement = pos=(110.7,19,22) rot=(0,0,1;0rad)
  Width = 15.7
FEATURE [Part::Cylinder] Cylinder044
  Angle = 360
  AttacherType = Attacher::AttachEngine3D
  Height = 20
  Placement = pos=(0,0,36.15) rot=(0,0,1;0rad)
  Radius = 10.3
FEATURE [Part::Cylinder] Cylinder045
  Angle = 360
  AttacherType = Attacher::AttachEngine3D
  Height = 10
  Placement = pos=(0,0,36.15) rot=(0,0,1;0rad)
  Radius = 4
FEATURE [Part::MultiFuse] Fusion104  label="removeToCreteHoleForPlugHousing040"
  Placement = pos=(70,19,36) rot=(0,1,0;1.5708rad)
  Shapes = -> [Cylinder044,Cylinder045]
FEATURE [Part::Cut] Cut046  label="plugHousingTab003"
  Base = -> Box028
  Tool = -> Fusion104
FEATURE [Part::MultiFuse] Fusion105  label="plugHousing062"
  Shapes = -> [Fusion103,Cut046]
FEATURE [Part::Fillet] Fillet042
  Base = -> Fusion105
  Edges = 1 edges r=2: [Edge25]
FEATURE [Part::Fillet] Fillet043  label="plugHousing063"
  Base = -> Fillet042
  Edges = 1 edges r=2: [Edge8]
  Placement = pos=(7,0,0) rot=(0,0,1;0rad)
FEATURE [Part::Feature] Face127
  shape: bbox 10 x 16.5 x 2e-07 mm, 1 faces, 0 solids (baked)
FEATURE [Part::Feature] Face128
  shape: bbox 10 x 16.5 x 2e-07 mm, 1 faces, 0 solids (baked)
FEATURE [Part::Revolution] Revolve137  label="plugHousing070"
  Angle = 360
  Axis = (0,1,0)
  Base = (0,0,0)
  FaceMakerClass = Part::FaceMakerBullseye
  Placement = pos=(0,0,36.15) rot=(0,0,1;0rad)
  Solid = false
  Source = -> Face127
  Symmetric = false
FEATURE [Part::Revolution] Revolve140  label="plugHousing073"
  Angle = 360
  Axis = (0,1,0)
  Base = (0,0,0)
  FaceMakerClass = Part::FaceMakerBullseye
  Placement = pos=(0,0,36.15) rot=(0,0,1;0rad)
  Solid = false
  Source = -> Face128
  Symmetric = false
FEATURE [Part::Feature] Face129
  shape: bbox 10 x 16.5 x 2e-07 mm, 1 faces, 0 solids (baked)
FEATURE [Part::Revolution] Revolve138  label="plugHousing071"
  Angle = 360
  Axis = (0,1,0)
  Base = (0,0,0)
  FaceMakerClass = Part::FaceMakerBullseye
  Placement = pos=(0,0,36.15) rot=(0,0,1;0rad)
  Solid = false
  Source = -> Face129
  Symmetric = false
FEATURE [Part::Feature] Face130
  shape: bbox 10 x 16.5 x 2e-07 mm, 1 faces, 0 solids (baked)
FEATURE [Part::Revolution] Revolve139  label="plugHousing072"
  Angle = 360
  Axis = (0,1,0)
  Base = (0,0,0)
  FaceMakerClass = Part::FaceMakerBullseye
  Placement = pos=(0,0,36.15) rot=(0,0,1;0rad)
  Solid = false
  Source = -> Face130
  Symmetric = false
FEATURE [Part::Feature] Face131
  shape: bbox 10 x 16.5 x 2e-07 mm, 1 faces, 0 solids (baked)
FEATURE [Part::Revolution] Revolve135  label="plugHousing068"
  Angle = 360
  Axis = (0,1,0)
  Base = (0,0,0)
  FaceMakerClass = Part::FaceMakerBullseye
  Placement = pos=(0,0,36.15) rot=(0,0,1;0rad)
  Solid = false
  Source = -> Face131
  Symmetric = false
FEATURE [Part::MultiFuse] Fusion112  label="plugHousing078"
  Placement = pos=(0,0,0) rot=(0,0,1;1.5708rad)
  Shapes = -> [Revolve135,Revolve139]
FEATURE [Part::Feature] Face132
  shape: bbox 10 x 16.5 x 2e-07 mm, 1 faces, 0 solids (baked)
FEATURE [Part::Revolution] Revolve141  label="plugHousing074"
  Angle = 360
  Axis = (0,1,0)
  Base = (0,0,0)
  FaceMakerClass = Part::FaceMakerBullseye
  Placement = pos=(0,0,36.15) rot=(0,0,1;0rad)
  Solid = false
  Source = -> Face132
  Symmetric = false
FEATURE [Part::MultiFuse] Fusion110  label="plugHousing076"
  Placement = pos=(0,0,0) rot=(0,0,1;1.5708rad)
  Shapes = -> [Revolve141,Revolve140]
FEATURE [Part::Feature] Face133
  shape: bbox 10 x 16.5 x 2e-07 mm, 1 faces, 0 solids (baked)
FEATURE [Part::Revolution] Revolve136  label="plugHousing069"
  Angle = 360
  Axis = (0,1,0)
  Base = (0,0,0)
  FaceMakerClass = Part::FaceMakerBullseye
  Placement = pos=(0,0,36.15) rot=(0,0,1;0rad)
  Solid = false
  Source = -> Face133
  Symmetric = false
FEATURE [Part::MultiFuse] Fusion106  label="plugHousing064"
  Placement = pos=(0,0,0) rot=(0,0,1;1.5708rad)
  Shapes = -> [Revolve138,Revolve136]
FEATURE [Part::MultiFuse] Fusion108  label="plugHousing066"
  Placement = pos=(0,19,0) rot=(0,0,1;3.14159rad)
  Shapes = -> [Fusion106,Fusion112]
FEATURE [Part::Feature] Face134
  shape: bbox 10 x 16.5 x 2e-07 mm, 1 faces, 0 solids (baked)
FEATURE [Part::Revolution] Revolve142  label="plugHousing075"
  Angle = 360
  Axis = (0,1,0)
  Base = (0,0,0)
  FaceMakerClass = Part::FaceMakerBullseye
  Placement = pos=(0,0,36.15) rot=(0,0,1;0rad)
  Solid = false
  Source = -> Face134
  Symmetric = false
FEATURE [Part::MultiFuse] Fusion107  label="plugHousing065"
  Placement = pos=(0,0,0) rot=(0,0,1;1.5708rad)
  Shapes = -> [Revolve137,Revolve142]
FEATURE [Part::MultiFuse] Fusion111  label="plugHousing077"
  Placement = pos=(0,19,0) rot=(0,0,1;3.14159rad)
  Shapes = -> [Fusion110,Fusion107]
FEATURE [Part::MultiFuse] Fusion109  label="plugHousing067"
  Placement = pos=(131.236,0,-0.15) rot=(0,0,1;0rad)
  Shapes = -> [Fusion108,Fusion111]
FEATURE [Part::MultiFuse] Fusion113  label="plugHousing079"
  Shapes = -> [Fillet043,Fusion109]
FEATURE [Part::Feature] Face135
  shape: bbox 3.5 x 17.8 x 2e-07 mm, 1 faces, 0 solids (baked)
FEATURE [Part::Revolution] Revolve143  label="removeToCreateScrewAndThreadedInsertHole049"
  Angle = 360
  Axis = (0,1,0)
  Base = (0,0,0)
  FaceMakerClass = Part::FaceMakerBullseye
  Placement = pos=(12.5,0,10) rot=(0,0,1;0rad)
  Solid = false
  Source = -> Face135
  Symmetric = false
FEATURE [Part::Feature] Face136
  shape: bbox 3.5 x 17.8 x 2e-07 mm, 1 faces, 0 solids (baked)
FEATURE [Part::Revolution] Revolve144  label="removeToCreateScrewAndThreadedInsertHole050"
  Angle = 360
  Axis = (0,1,0)
  Base = (0,0,0)
  FaceMakerClass = Part::FaceMakerBullseye
  Placement = pos=(12.5,0,62) rot=(0,0,1;0rad)
  Solid = false
  Source = -> Face136
  Symmetric = false
FEATURE [Part::Feature] Face137
  shape: bbox 3.5 x 17.8 x 2e-07 mm, 1 faces, 0 solids (baked)
FEATURE [Part::Revolution] Revolve145  label="removeToCreateScrewAndThreadedInsertHole051"
  Angle = 360
  Axis = (0,1,0)
  Base = (0,0,0)
  FaceMakerClass = Part::FaceMakerBullseye
  Placement = pos=(89.5,0,68.5) rot=(0,0,1;0rad)
  Solid = false
  Source = -> Face137
  Symmetric = false
FEATURE [Part::Feature] Face138
  shape: bbox 3.5 x 17.8 x 2e-07 mm, 1 faces, 0 solids (baked)
FEATURE [Part::Revolution] Revolve146  label="removeToCreateScrewAndThreadedInsertHole052"
  Angle = 360
  Axis = (0,1,0)
  Base = (0,0,0)
  FaceMakerClass = Part::FaceMakerBullseye
  Placement = pos=(89.5,0,3.5) rot=(0,0,1;0rad)
  Solid = false
  Source = -> Face138
  Symmetric = false
FEATURE [Part::Feature] Face139
  shape: bbox 3.5 x 17.8 x 2e-07 mm, 1 faces, 0 solids (baked)
FEATURE [Part::Revolution] Revolve147  label="removeToCreateScrewAndThreadedInsertHole053"
  Angle = 360
  Axis = (0,1,0)
  Base = (0,0,0)
  FaceMakerClass = Part::FaceMakerBullseye
  Placement = pos=(109.5,4.7,3.5) rot=(0,0,1;0rad)
  Solid = false
  Source = -> Face139
  Symmetric = false
FEATURE [Part::Feature] Face140
  shape: bbox 3.5 x 17.8 x 2e-07 mm, 1 faces, 0 solids (baked)
FEATURE [Part::Revolution] Revolve148  label="removeToCreateScrewAndThreadedInsertHole054"
  Angle = 360
  Axis = (0,1,0)
  Base = (0,0,0)
  FaceMakerClass = Part::FaceMakerBullseye
  Placement = pos=(109.5,4.7,68.5) rot=(0,0,1;0rad)
  Solid = false
  Source = -> Face140
  Symmetric = false
FEATURE [Part::MultiFuse] Fusion114  label="removeToCreateScrewAndThreadedInsertHole055"
  Shapes = -> [Revolve148,Revolve147,Revolve146,Revolve145,Revolve144,Revolve143]
FEATURE [Part::Cut] Cut047  label="casePillars004"
  Base = -> Cut037
  Tool = -> Fusion114
FEATURE [Part::Feature] Face141
  shape: bbox 3.5 x 17.8 x 2e-07 mm, 1 faces, 0 solids (baked)
FEATURE [Part::Feature] Face142
  shape: bbox 3.5 x 17.8 x 2e-07 mm, 1 faces, 0 solids (baked)
FEATURE [Part::Feature] Face143
  shape: bbox 3.5 x 17.8 x 2e-07 mm, 1 faces, 0 solids (baked)
FEATURE [Part::Revolution] Revolve149  label="removeToCreateScrewAndThreadedInsertHole057"
  Angle = 360
  Axis = (0,1,0)
  Base = (0,0,0)
  FaceMakerClass = Part::FaceMakerBullseye
  Placement = pos=(12.5,0,10) rot=(0,0,1;0rad)
  Solid = false
  Source = -> Face141
  Symmetric = false
FEATURE [Part::Feature] Face144
  shape: bbox 3.5 x 17.8 x 2e-07 mm, 1 faces, 0 solids (baked)
FEATURE [Part::Feature] Face145
  shape: bbox 3.5 x 17.8 x 2e-07 mm, 1 faces, 0 solids (baked)
FEATURE [Part::Feature] Face146
  shape: bbox 3.5 x 17.8 x 2e-07 mm, 1 faces, 0 solids (baked)
FEATURE [Part::Revolution] Revolve150  label="removeToCreateScrewAndThreadedInsertHole058"
  Angle = 360
  Axis = (0,1,0)
  Base = (0,0,0)
  FaceMakerClass = Part::FaceMakerBullseye
  Placement = pos=(12.5,0,62) rot=(0,0,1;0rad)
  Solid = false
  Source = -> Face146
  Symmetric = false
FEATURE [Part::Revolution] Revolve151  label="removeToCreateScrewAndThreadedInsertHole059"
  Angle = 360
  Axis = (0,1,0)
  Base = (0,0,0)
  FaceMakerClass = Part::FaceMakerBullseye
  Placement = pos=(89.5,0,68.5) rot=(0,0,1;0rad)
  Solid = false
  Source = -> Face143
  Symmetric = false
FEATURE [Part::Revolution] Revolve152  label="removeToCreateScrewAndThreadedInsertHole060"
  Angle = 360
  Axis = (0,1,0)
  Base = (0,0,0)
  FaceMakerClass = Part::FaceMakerBullseye
  Placement = pos=(89.5,0,3.5) rot=(0,0,1;0rad)
  Solid = false
  Source = -> Face142
  Symmetric = false
FEATURE [Part::Revolution] Revolve153  label="removeToCreateScrewAndThreadedInsertHole061"
  Angle = 360
  Axis = (0,1,0)
  Base = (0,0,0)
  FaceMakerClass = Part::FaceMakerBullseye
  Placement = pos=(109.5,4.7,3.5) rot=(0,0,1;0rad)
  Solid = false
  Source = -> Face145
  Symmetric = false
FEATURE [Part::Revolution] Revolve154  label="removeToCreateScrewAndThreadedInsertHole062"
  Angle = 360
  Axis = (0,1,0)
  Base = (0,0,0)
  FaceMakerClass = Part::FaceMakerBullseye
  Placement = pos=(109.5,4.7,68.5) rot=(0,0,1;0rad)
  Solid = false
  Source = -> Face144
  Symmetric = false
FEATURE [Part::MultiFuse] Fusion115  label="removeToCreateScrewAndThreadedInsertHole056"
  Shapes = -> [Revolve154,Revolve153,Revolve152,Revolve151,Revolve150,Revolve149]
FEATURE [Part::Feature] Face147
  shape: bbox 9.8 x 26.5 x 2e-07 mm, 1 faces, 0 solids (baked)
FEATURE [Part::Revolution] Revolve155
  Angle = 360
  Axis = (0,1,0)
  Base = (0,0,0)
  FaceMakerClass = Part::FaceMakerBullseye
  Placement = pos=(0,0,0) rot=(0,0,1;1.5708rad)
  Solid = false
  Source = -> Face147
  Symmetric = false
FEATURE [Part::Feature] Face148
  shape: bbox 9.8 x 26.5 x 2e-07 mm, 1 faces, 0 solids (baked)
FEATURE [Part::Revolution] Revolve156
  Angle = 360
  Axis = (0,1,0)
  Base = (0,0,0)
  FaceMakerClass = Part::FaceMakerBullseye
  Placement = pos=(0,0,0) rot=(0,0,1;1.5708rad)
  Solid = false
  Source = -> Face148
  Symmetric = false
FEATURE [Part::MultiFuse] Fusion116
  Placement = pos=(-18,19,36) rot=(0,0,1;0rad)
  Shapes = -> [Revolve156,Revolve155]
FEATURE [Part::Box] Box029  label="Cube016"
  AttacherType = Attacher::AttachEngine3D
  Height = 28
  Length = 3
  Placement = pos=(110.7,19,22) rot=(0,0,1;0rad)
  Width = 15.7
FEATURE [Part::Cylinder] Cylinder046
  Angle = 360
  AttacherType = Attacher::AttachEngine3D
  Height = 10
  Placement = pos=(0,0,36.15) rot=(0,0,1;0rad)
  Radius = 4
FEATURE [Part::Cylinder] Cylinder047
  Angle = 360
  AttacherType = Attacher::AttachEngine3D
  Height = 20
  Placement = pos=(0,0,36.15) rot=(0,0,1;0rad)
  Radius = 10.3
FEATURE [Part::MultiFuse] Fusion117  label="removeToCreteHoleForPlugHousing041"
  Placement = pos=(70,19,36) rot=(0,1,0;1.5708rad)
  Shapes = -> [Cylinder047,Cylinder046]
FEATURE [Part::Cut] Cut049  label="plugHousingTab004"
  Base = -> Box029
  Placement = pos=(-107.4,-14,0) rot=(0,0,1;0rad)
  Tool = -> Fusion117
FEATURE [Part::Box] Box030  label="Cube017"
  AttacherType = Attacher::AttachEngine3D
  Height = 28
  Length = 3
  Placement = pos=(110.7,19,22) rot=(0,0,1;0rad)
  Width = 15.7
FEATURE [Part::Cylinder] Cylinder048
  Angle = 360
  AttacherType = Attacher::AttachEngine3D
  Height = 10
  Placement = pos=(0,0,36.15) rot=(0,0,1;0rad)
  Radius = 4
FEATURE [Part::Cylinder] Cylinder049
  Angle = 360
  AttacherType = Attacher::AttachEngine3D
  Height = 20
  Placement = pos=(0,0,36.15) rot=(0,0,1;0rad)
  Radius = 10.3
FEATURE [Part::MultiFuse] Fusion118  label="removeToCreteHoleForPlugHousing042"
  Placement = pos=(70,19,36) rot=(0,1,0;1.5708rad)
  Shapes = -> [Cylinder049,Cylinder048]
FEATURE [Part::Cut] Cut050  label="plugHousingTab005"
  Base = -> Box030
  Placement = pos=(-107.4,-14,0) rot=(0,0,1;0rad)
  Tool = -> Fusion118
FEATURE [Part::MultiFuse] Fusion119
  Placement = pos=(9.6,23,0) rot=(0,0,1;3.14159rad)
  Shapes = -> [Cut049,Cut050]
FEATURE [Part::Box] Box031  label="Cube018"
  AttacherType = Attacher::AttachEngine3D
  Height = 10
  Length = 3
  Placement = pos=(3.3,4,12) rot=(0,0,1;0rad)
  Width = 10
FEATURE [Part::Fillet] Fillet044
  Base = -> Box031
  Edges = 1 edges r=2: [Edge11]
FEATURE [Part::Box] Box032  label="Cube019"
  AttacherType = Attacher::AttachEngine3D
  Height = 10
  Length = 3
  Placement = pos=(3.3,4,50) rot=(0,0,1;0rad)
  Width = 10
FEATURE [Part::Fillet] Fillet045
  Base = -> Box032
  Edges = 1 edges r=2: [Edge12]
FEATURE [Part::Box] Box033  label="Cube020"
  AttacherType = Attacher::AttachEngine3D
  Height = 28
  Length = 4
  Placement = pos=(5,0,22) rot=(0,0,1;0rad)
  Width = 10
FEATURE [Part::Fillet] Fillet046
  Base = -> Box033
  Edges = 1 edges r=1: [Edge7]
FEATURE [Part::Fillet] Fillet047
  Base = -> Fillet046
  Edges = 1 edges r=2: [Edge5]
FEATURE [Part::Fillet] Fillet048
  Base = -> Fillet047
  Edges = 1 edges r=2: [Edge2]
FEATURE [Part::Cylinder] Cylinder050
  Angle = 360
  AttacherType = Attacher::AttachEngine3D
  Height = 20
  Placement = pos=(0,0,36.15) rot=(0,0,1;0rad)
  Radius = 8.2
FEATURE [Part::Cylinder] Cylinder051
  Angle = 360
  AttacherType = Attacher::AttachEngine3D
  Height = 10
  Placement = pos=(0,0,36.15) rot=(0,0,1;0rad)
  Radius = 4
FEATURE [Part::MultiFuse] Fusion120  label="removeToCreteHoleForPlugHousing043"
  Placement = pos=(-42,19,36) rot=(0,1,0;1.5708rad)
  Shapes = -> [Cylinder050,Cylinder051]
FEATURE [Sketcher::SketchObject] Sketch067  label="topSketch018"
  FullyConstrained = true
  sketch-geometry (4):
    g0: LineSegment StartX=16.8446 StartY=31.512 StartZ=0 EndX=16.3251 EndY=34.4666 EndZ=0
    g1: ArcOfCircle CenterX=19 CenterY=19.2524 CenterZ=0 NormalX=0 NormalY=0 NormalZ=1 AngleXU=0 Radius=15.4476 StartAngle=1.74483 EndAngle=2.72717
    g2: ArcOfCircle CenterX=19 CenterY=19.2524 CenterZ=0 NormalX=0 NormalY=0 NormalZ=1 AngleXU=0 Radius=12.4476 StartAngle=1.74483 EndAngle=2.73189
    g3: LineSegment StartX=4.86004 StartY=25.4725 StartZ=0 EndX=7.58253 EndY=24.2107 EndZ=0
  constraints (7):
    c: Block(g0)
    c: Coincident(g1,g0)
    c: Coincident(g2,g0)
    c: Coincident(g3,g1)
    c: Coincident(g3,g2)
    c: Block(g1)
    c: Block(g2)
FEATURE [Part::Extrusion] Extrude058
  Base = -> Sketch067
  Dir = (0,0,1)
  DirMode = 2
  FaceMakerClass = Part::FaceMakerBullseye
  LengthFwd = 10
  LengthRev = 0
  Placement = pos=(0,0,31) rot=(0,0,1;0rad)
  Solid = true
  Symmetric = false
FEATURE [Part::Cut] Cut051
  Base = -> Extrude058
  Tool = -> Fusion120
FEATURE [Part::Fillet] Fillet049
  Base = -> Cut051
  Edges = 1 edges r=2: [Edge1]
FEATURE [Part::Fillet] Fillet050
  Base = -> Fillet049
  Edges = 1 edges r=2.5: [Edge1]
FEATURE [Part::Fillet] Fillet051
  Base = -> Fillet050
  Edges = 1 edges r=2.5: [Edge2]
FEATURE [Part::MultiFuse] Fusion121  label="wireHolder003"
  Shapes = -> [Fusion116,Fillet051]
FEATURE [Part::MultiFuse] Fusion122
  Shapes = -> [Fillet045,Fusion121]
FEATURE [Part::MultiFuse] Fusion123  label="wireHolder004"
  Shapes = -> [Fusion122,Fillet048]
FEATURE [Part::MultiFuse] Fusion124  label="wireHolder005"
  Shapes = -> [Fillet044,Fusion119,Fusion123]
FEATURE [Sketcher::SketchObject] Sketch068  label="topSketch019"
  FullyConstrained = true
  sketch-geometry (6):
    g0: LineSegment StartX=19 StartY=38 StartZ=0 EndX=117 EndY=38 EndZ=0
    g1: ArcOfCircle CenterX=19 CenterY=19 CenterZ=0 NormalX=0 NormalY=0 NormalZ=1 AngleXU=0 Radius=19 StartAngle=1.5708 EndAngle=3.14159
    g2: LineSegment StartX=117 StartY=38 StartZ=0 EndX=117 EndY=19 EndZ=0
    g3: LineSegment StartX=98 StartY=1.0161e-12 StartZ=0 EndX=5.22862e-06 EndY=1.0161e-12 EndZ=0
    g4: LineSegment StartX=5.22862e-06 StartY=19 StartZ=0 EndX=5.22862e-06 EndY=1.0161e-12 EndZ=0
    g5: ArcOfCircle CenterX=98 CenterY=19 CenterZ=0 NormalX=0 NormalY=0 NormalZ=1 AngleXU=0 Radius=19 StartAngle=4.71239 EndAngle=6.28319
  constraints (16):
    c: Horizontal(g0)
    c: Distance(g0) = 98
    c: Coincident(g1,g0)
    c: Block(g1)
    c: Coincident(g2,g0)
    c: Vertical(g2)
    c: Distance(g2) = 19
    c: Horizontal(g3)
    c: Coincident(g4,g1)
    c: Vertical(g4)
    c: Coincident(g3,g4)
    c: Block(g3)
    c: Coincident(g5,g2)
    c: Coincident(g5,g3)
    c: Block(g0)
    c: Block(g5)
FEATURE [Part::Extrusion] Extrude059  label="sideA002"
  Base = -> Sketch068
  Dir = (0,0,1)
  DirMode = 2
  FaceMakerClass = Part::FaceMakerBullseye
  LengthFwd = 3
  LengthRev = 0
  Placement = pos=(0,0,-2.7) rot=(0,0,1;0rad)
  Solid = true
  Symmetric = false
FEATURE [Sketcher::SketchObject] Sketch069  label="topSketch020"
  FullyConstrained = true
  sketch-geometry (6):
    g0: LineSegment StartX=19 StartY=38 StartZ=0 EndX=117 EndY=38 EndZ=0
    g1: ArcOfCircle CenterX=19 CenterY=19 CenterZ=0 NormalX=0 NormalY=0 NormalZ=1 AngleXU=0 Radius=19 StartAngle=1.5708 EndAngle=3.14159
    g2: LineSegment StartX=117 StartY=38 StartZ=0 EndX=117 EndY=19 EndZ=0
    g3: LineSegment StartX=98 StartY=1.0161e-12 StartZ=0 EndX=5.22862e-06 EndY=1.0161e-12 EndZ=0
    g4: LineSegment StartX=5.22862e-06 StartY=19 StartZ=0 EndX=5.22862e-06 EndY=1.0161e-12 EndZ=0
    g5: ArcOfCircle CenterX=98 CenterY=19 CenterZ=0 NormalX=0 NormalY=0 NormalZ=1 AngleXU=0 Radius=19 StartAngle=4.71239 EndAngle=6.28319
  constraints (16):
    c: Horizontal(g0)
    c: Distance(g0) = 98
    c: Coincident(g1,g0)
    c: Block(g1)
    c: Coincident(g2,g0)
    c: Vertical(g2)
    c: Distance(g2) = 19
    c: Horizontal(g3)
    c: Coincident(g4,g1)
    c: Vertical(g4)
    c: Coincident(g3,g4)
    c: Block(g3)
    c: Coincident(g5,g2)
    c: Coincident(g5,g3)
    c: Block(g0)
    c: Block(g5)
FEATURE [Part::Extrusion] Extrude060  label="sideB002"
  Base = -> Sketch069
  Dir = (0,0,1)
  DirMode = 2
  FaceMakerClass = Part::FaceMakerBullseye
  LengthFwd = 3
  LengthRev = 0
  Placement = pos=(0,0,71.7) rot=(0,0,1;0rad)
  Solid = true
  Symmetric = false
FEATURE [Part::MultiFuse] Fusion127  label="removeFromBottom001"
  Placement = pos=(2,0,0) rot=(0,0,1;0rad)
  Shapes = -> [Extrude059,Extrude060]
FEATURE [Part::Cylinder] Cylinder052
  Angle = 360
  AttacherType = Attacher::AttachEngine3D
  Height = 20
  Placement = pos=(0,0,36.15) rot=(0,0,1;0rad)
  Radius = 14
FEATURE [Part::Cylinder] Cylinder053
  Angle = 360
  AttacherType = Attacher::AttachEngine3D
  Height = 10
  Placement = pos=(0,0,36.15) rot=(0,0,1;0rad)
  Radius = 4
FEATURE [Part::MultiFuse] Fusion128  label="removeToCreteHoleForPlugHousing044"
  Placement = pos=(70,19,36) rot=(0,1,0;1.5708rad)
  Shapes = -> [Cylinder052,Cylinder053]
FEATURE [Part::Cut] Cut052  label="bottom011"
  Base = -> Extrude043
  Tool = -> Fusion128
FEATURE [Part::Cut] Cut054  label="bottom012"
  Base = -> Cut052
  Tool = -> Fusion115
FEATURE [Sketcher::SketchObject] Sketch070
  FullyConstrained = true
  Placement = pos=(117,19,0) rot=(0.57735,0.57735,0.57735;2.0944rad)
  sketch-geometry (48):
    g0: LineSegment StartX=-49.19 StartY=69.25 StartZ=0 EndX=-49.19 EndY=66.25 EndZ=0
    g1: LineSegment StartX=-49.19 StartY=63.5 StartZ=0 EndX=-49.19 EndY=60.5 EndZ=0
    g2: LineSegment StartX=-49.19 StartY=57.75 StartZ=0 EndX=-49.19 EndY=54.75 EndZ=0
    g3: LineSegment StartX=-49.19 StartY=52 StartZ=0 EndX=-49.19 EndY=49 EndZ=0
    g4: LineSegment StartX=-49.19 StartY=46.25 StartZ=0 EndX=-49.19 EndY=43.25 EndZ=0
    g5: LineSegment StartX=-49.19 StartY=40.5 StartZ=0 EndX=-49.19 EndY=37.5 EndZ=0
    g6: LineSegment StartX=-49.19 StartY=34.5 StartZ=0 EndX=-49.19 EndY=31.5 EndZ=0
    g7: LineSegment StartX=-49.19 StartY=28.75 StartZ=0 EndX=-49.19 EndY=25.75 EndZ=0
    g8: LineSegment StartX=-49.19 StartY=23 StartZ=0 EndX=-49.19 EndY=20 EndZ=0
    g9: LineSegment StartX=-49.19 StartY=17.25 StartZ=0 EndX=-49.19 EndY=14.25 EndZ=0
    g10: LineSegment StartX=-49.19 StartY=11.5 StartZ=0 EndX=-49.19 EndY=8.5 EndZ=0
    g11: LineSegment StartX=-49.19 StartY=5.75 StartZ=0 EndX=-49.19 EndY=2.75 EndZ=0
    g12: ArcOfCircle CenterX=-1.5 CenterY=67.75 CenterZ=0 NormalX=0 NormalY=0 NormalZ=1 AngleXU=0 Radius=1.5 StartAngle=4.71239 EndAngle=7.85398
    g13: ArcOfCircle CenterX=-1.5 CenterY=62 CenterZ=0 NormalX=0 NormalY=0 NormalZ=1 AngleXU=0 Radius=1.5 StartAngle=4.71239 EndAngle=7.85398
    g14: ArcOfCircle CenterX=-1.5 CenterY=56.25 CenterZ=0 NormalX=0 NormalY=0 NormalZ=1 AngleXU=0 Radius=1.5 StartAngle=4.71239 EndAngle=7.85398
    g15: ArcOfCircle CenterX=-11.49 CenterY=50.5 CenterZ=0 NormalX=0 NormalY=0 NormalZ=1 AngleXU=0 Radius=1.5 StartAngle=4.71239 EndAngle=7.85398
    g16: ArcOfCircle CenterX=-16.28 CenterY=44.75 CenterZ=0 NormalX=0 NormalY=0 NormalZ=1 AngleXU=0 Radius=1.5 StartAngle=4.71239 EndAngle=7.85398
    g17: ArcOfCircle CenterX=-18.2337 CenterY=39 CenterZ=0 NormalX=0 NormalY=0 NormalZ=1 AngleXU=0 Radius=1.5 StartAngle=4.71485 EndAngle=7.85398
    g18: ArcOfCircle CenterX=-16.2837 CenterY=27.25 CenterZ=0 NormalX=0 NormalY=0 NormalZ=1 AngleXU=0 Radius=1.5 StartAngle=4.71485 EndAngle=7.85398
    g19: ArcOfCircle CenterX=-18.2337 CenterY=33 CenterZ=0 NormalX=0 NormalY=0 NormalZ=1 AngleXU=0 Radius=1.5 StartAngle=4.71485 EndAngle=7.85398
    g20: ArcOfCircle CenterX=-11.49 CenterY=21.5 CenterZ=0 NormalX=0 NormalY=0 NormalZ=1 AngleXU=0 Radius=1.5 StartAngle=4.71239 EndAngle=7.85398
    g21: ArcOfCircle CenterX=-1.5 CenterY=4.25 CenterZ=0 NormalX=0 NormalY=0 NormalZ=1 AngleXU=0 Radius=1.5 StartAngle=4.71239 EndAngle=7.85398
    g22: ArcOfCircle CenterX=-1.5 CenterY=10 CenterZ=0 NormalX=0 NormalY=0 NormalZ=1 AngleXU=0 Radius=1.5 StartAngle=4.71239 EndAngle=7.85398
    g23: ArcOfCircle CenterX=-1.5 CenterY=15.75 CenterZ=0 NormalX=0 NormalY=0 NormalZ=1 AngleXU=0 Radius=1.5 StartAngle=4.71239 EndAngle=7.85398
    g24: LineSegment StartX=-49.19 StartY=69.25 StartZ=0 EndX=-1.5 EndY=69.25 EndZ=0
    g25: LineSegment StartX=-49.19 StartY=66.25 StartZ=0 EndX=-1.5 EndY=66.25 EndZ=0
    g26: LineSegment StartX=-49.19 StartY=63.5 StartZ=0 EndX=-1.5 EndY=63.5 EndZ=0
    g27: LineSegment StartX=-49.19 StartY=60.5 StartZ=0 EndX=-1.5 EndY=60.5 EndZ=0
    g28: LineSegment StartX=-49.19 StartY=57.75 StartZ=0 EndX=-1.5 EndY=57.75 EndZ=0
    g29: LineSegment StartX=-49.19 StartY=54.75 StartZ=0 EndX=-1.5 EndY=54.75 EndZ=0
    g30: LineSegment StartX=-49.19 StartY=52 StartZ=0 EndX=-11.49 EndY=52 EndZ=0
    g31: LineSegment StartX=-49.19 StartY=49 StartZ=0 EndX=-11.49 EndY=49 EndZ=0
    g32: LineSegment StartX=-49.19 StartY=46.25 StartZ=0 EndX=-16.28 EndY=46.25 EndZ=0
    g33: LineSegment StartX=-49.19 StartY=43.25 StartZ=0 EndX=-16.28 EndY=43.25 EndZ=0
    g34: LineSegment StartX=-49.19 StartY=40.5 StartZ=0 EndX=-18.2337 EndY=40.5 EndZ=0
    g35: LineSegment StartX=-49.19 StartY=37.5 StartZ=0 EndX=-18.23 EndY=37.5 EndZ=0
    g36: LineSegment StartX=-49.19 StartY=34.5 StartZ=0 EndX=-18.2337 EndY=34.5 EndZ=0
    g37: LineSegment StartX=-49.19 StartY=31.5 StartZ=0 EndX=-18.23 EndY=31.5 EndZ=0
    g38: LineSegment StartX=-49.19 StartY=28.75 StartZ=0 EndX=-16.2837 EndY=28.75 EndZ=0
    g39: LineSegment StartX=-49.19 StartY=25.75 StartZ=0 EndX=-16.28 EndY=25.75 EndZ=0
    g40: LineSegment StartX=-49.19 StartY=23 StartZ=0 EndX=-11.49 EndY=23 EndZ=0
    g41: LineSegment StartX=-49.19 StartY=20 StartZ=0 EndX=-11.49 EndY=20 EndZ=0
    g42: LineSegment StartX=-49.19 StartY=17.25 StartZ=0 EndX=-1.5 EndY=17.25 EndZ=0
    g43: LineSegment StartX=-49.19 StartY=14.25 StartZ=0 EndX=-1.5 EndY=14.25 EndZ=0
    g44: LineSegment StartX=-49.19 StartY=11.5 StartZ=0 EndX=-1.5 EndY=11.5 EndZ=0
    g45: LineSegment StartX=-49.19 StartY=8.5 StartZ=0 EndX=-1.5 EndY=8.5 EndZ=0
    g46: LineSegment StartX=-49.19 StartY=5.75 StartZ=0 EndX=-1.5 EndY=5.75 EndZ=0
    g47: LineSegment StartX=-49.19 StartY=2.75 StartZ=0 EndX=-1.5 EndY=2.75 EndZ=0
  constraints (120):
    c: Vertical(g0)
    c: Distance(g0) = 3
    c: Block(g0)
    c: Vertical(g1)
    c: Distance(g1) = 3
    c: Vertical(g2)
    c: Equal(g0,g2) = 3
    c: Block(g2)
    c: Vertical(g3)
    c: Equal(g1,g3) = 3
    c: Vertical(g4)
    c: Equal(g0,g4) = 3
    c: Block(g4)
    c: Vertical(g5)
    c: Equal(g1,g5) = 3
    c: Vertical(g6)
    c: Equal(g0,g6) = 3
    c: Block(g6)
    c: Vertical(g7)
    c: Equal(g1,g7) = 3
    c: Vertical(g8)
    c: Equal(g0,g8) = 3
    c: Block(g8)
    c: Vertical(g9)
    c: Equal(g1,g9) = 3
    c: Vertical(g10)
    c: Equal(g0,g10) = 3
    c: Block(g10)
    c: Vertical(g11)
    c: Equal(g1,g11) = 3
    c: Block(g12)
    c: Block(g13)
    c: Block(g14)
    c: Block(g15)
    c: Block(g16)
    c: Block(g17)
    c: Block(g18)
    c: Block(g19)
    c: Block(g20)
    c: Block(g21)
    c: Block(g22)
    c: Block(g23)
    c: Block(g11)
    c: Block(g9)
    c: Block(g7)
    c: Block(g5)
    c: Block(g3)
    c: Block(g1)
    c: Coincident(g24,g0)
    c: Coincident(g24,g12)
    c: Horizontal(g24)
    c: Coincident(g25,g0)
    c: Coincident(g25,g12)
    c: Horizontal(g25)
    c: Coincident(g26,g1)
    c: Coincident(g26,g13)
    c: Horizontal(g26)
    c: Coincident(g27,g1)
    c: Coincident(g27,g13)
    c: Horizontal(g27)
    c: Coincident(g28,g2)
    c: Coincident(g28,g14)
    c: Horizontal(g28)
    c: Coincident(g29,g2)
    c: Coincident(g29,g14)
    c: Horizontal(g29)
    c: Coincident(g30,g3)
    c: Coincident(g30,g15)
    c: Horizontal(g30)
    c: Coincident(g31,g3)
    c: Coincident(g31,g15)
    c: Horizontal(g31)
    c: Coincident(g32,g4)
    c: Coincident(g32,g16)
    c: Horizontal(g32)
    c: Coincident(g33,g4)
    c: Coincident(g33,g16)
    c: Horizontal(g33)
    c: Coincident(g34,g5)
    c: Coincident(g34,g17)
    c: Horizontal(g34)
    c: Coincident(g35,g5)
    c: Coincident(g35,g17)
    c: Horizontal(g35)
    c: Coincident(g36,g6)
    c: Coincident(g36,g19)
    c: Horizontal(g36)
    c: Coincident(g37,g6)
    c: Coincident(g37,g19)
    c: Horizontal(g37)
    c: Coincident(g38,g7)
    c: Coincident(g38,g18)
    c: Horizontal(g38)
    c: Coincident(g39,g7)
    c: Coincident(g39,g18)
    c: Horizontal(g39)
    c: Coincident(g40,g8)
    c: Coincident(g40,g20)
    c: Horizontal(g40)
    c: Coincident(g41,g8)
    c: Coincident(g41,g20)
    c: Horizontal(g41)
    c: Coincident(g42,g9)
    c: Coincident(g42,g23)
    c: Horizontal(g42)
    c: Coincident(g43,g9)
    c: Coincident(g43,g23)
    c: Horizontal(g43)
    c: Coincident(g44,g10)
    c: Coincident(g44,g22)
    c: Horizontal(g44)
    c: Coincident(g45,g10)
    c: Coincident(g45,g22)
    c: Horizontal(g45)
    c: Coincident(g46,g11)
    c: Coincident(g46,g21)
    c: Horizontal(g46)
    c: Coincident(g47,g11)
    c: Coincident(g47,g21)
    c: Horizontal(g47)
FEATURE [Part::Extrusion] Extrude061
  Base = -> Sketch070
  Dir = (1,0,0)
  DirMode = 2
  FaceMakerClass = Part::FaceMakerBullseye
  LengthFwd = 23
  LengthRev = 0
  Placement = pos=(-19,0,0) rot=(0,0,1;0rad)
  Solid = true
  Symmetric = false
FEATURE [Part::Fillet] Fillet052  label="removeToCreateVentalationHoles002"
  Base = -> Extrude061
  Edges = <same value as first occurrence — deduplicated (x6 in doc)>
  Placement = pos=(7,0.02,0) rot=(0,0,1;0rad)
FEATURE [Part::MultiFuse] Fusion130  label="bottom013"
  Shapes = -> [Cut054,Cut034]
FEATURE [Part::Cut] Cut055
  Base = -> Fusion130
  Tool = -> Fillet052
FEATURE [Part::Cylinder] Cylinder054
  Angle = 360
  AttacherType = Attacher::AttachEngine3D
  Height = 20
  Placement = pos=(0,0,36.15) rot=(0,0,1;0rad)
  Radius = 4
FEATURE [Sketcher::SketchObject] Sketch071  label="bottomSketch002"
  FullyConstrained = true
  sketch-geometry (32):
    g0: LineSegment StartX=3.3 StartY=-6.03275e-07 StartZ=0 EndX=98 EndY=-6.03275e-07 EndZ=0
    g1: ArcOfCircle CenterX=98 CenterY=19 CenterZ=0 NormalX=0 NormalY=0 NormalZ=1 AngleXU=0 Radius=19 StartAngle=4.71239 EndAngle=5.71103
    g2: LineSegment StartX=6.3 StartY=8 StartZ=0 EndX=3.3 EndY=8 EndZ=0
    g3: LineSegment StartX=3.3 StartY=8 StartZ=0 EndX=3.3 EndY=-6.03275e-07 EndZ=0
    g4: ArcOfCircle CenterX=8.3 CenterY=5 CenterZ=0 NormalX=0 NormalY=0 NormalZ=1 AngleXU=0 Radius=2 StartAngle=3.14159 EndAngle=4.71239
    g5: LineSegment StartX=6.3 StartY=8 StartZ=0 EndX=6.3 EndY=5 EndZ=0
    g6: ArcOfCircle CenterX=98 CenterY=19 CenterZ=0 NormalX=0 NormalY=0 NormalZ=1 AngleXU=0 Radius=12.7 StartAngle=4.71239 EndAngle=6.28319
    g7: LineSegment StartX=94.7 StartY=3 StartZ=0 EndX=8.3 EndY=3 EndZ=0
    g8-g12: Circle x5 (B-spline internal-alignment scaffolding for g13; pole/knot coordinates omitted)
    g13: BSplineCurve PolesCount=5 KnotsCount=3 Degree=3 IsPeriodic=0
    g14: GeomPoint X=98 Y=6.3 Z=0
    g15: GeomPoint X=96.3938 Y=4.71946 Z=0
    g16: GeomPoint X=94.7 Y=3 Z=0
    g17-g23: Circle x7 (B-spline internal-alignment scaffolding for g24; pole/knot coordinates omitted)
    g24: BSplineCurve PolesCount=7 KnotsCount=5 Degree=3 IsPeriodic=0
    g25-g29: GeomPoint x5 (B-spline internal-alignment scaffolding for g24; pole/knot coordinates omitted)
    g30: ArcOfCircle CenterX=98 CenterY=19 CenterZ=0 NormalX=0 NormalY=0 NormalZ=1 AngleXU=0 Radius=15.7 StartAngle=5.81226 EndAngle=6.28319
    g31: LineSegment StartX=110.7 StartY=19 StartZ=0 EndX=113.7 EndY=19 EndZ=0
  constraints (41):
    c: Horizontal(g0)
    c: Coincident(g1,g0)
    c: Block(g1)
    c: Horizontal(g2)
    c: Distance(g2) = 3
    c: Coincident(g3,g2)
    c: Vertical(g3)
    c: Coincident(g3,g0)
    c: Block(g4)
    c: Block(g2)
    c: Coincident(g5,g2)
    c: Coincident(g5,g4)
    c: Vertical(g5)
    c: Coincident(g6,g1)
    c: Block(g6)
    c: Coincident(g7,g4)
    c: Horizontal(g7)
    c: Block(g0)
    c: Block(g7)
    c: Block(g3)
    c: Coincident(g13,g6)
    c: Weight(g8) = 1
    c: Equal(g8, g9-g12) x4
    c: Coincident(g13,g7)
    c: InternalAlignment(g8-g12 -> g13) x5
    c: InternalAlignment(g14,g13)
    c: InternalAlignment(g15,g13)
    c: InternalAlignment(g16,g13)
    c: Block(g13)
    c: Weight(g17) = 1
    c: Equal(g17, g18-g23) x6
    c: Coincident(g24,g1)
    c: InternalAlignment(g17-g23 -> g24) x7
    c: InternalAlignment(g25-g29 -> g24) x5
    c: Block(g24)
    c: Coincident(g30,g24)
    c: Coincident(g31,g6)
    c: Coincident(g31,g30)
    c: Horizontal(g31)
    c: Block(g31)
    c: Block(g30)
FEATURE [Part::Extrusion] Extrude062  label="bottom014"
  Base = -> Sketch071
  Dir = (0,0,1)
  DirMode = 2
  FaceMakerClass = Part::FaceMakerBullseye
  LengthFwd = 71.4
  LengthRev = 0
  Placement = pos=(0,0,0.3) rot=(0,0,1;0rad)
  Solid = true
  Symmetric = false
FEATURE [Part::Fillet] Fillet054
  Base = -> Extrude062
  Edges = 1 edges r=2.4: [Edge17]
FEATURE [Part::Fillet] Fillet055  label="bottom015"
  Base = -> Fillet054
  Edges = 1 edges r=2.4: [Edge36]
FEATURE [Part::Cylinder] Cylinder055
  Angle = 360
  AttacherType = Attacher::AttachEngine3D
  Height = 10
  Placement = pos=(0,0,36.15) rot=(0,0,1;0rad)
  Radius = 4
FEATURE [Part::MultiFuse] Fusion131  label="removeToCreateHoleForPlugHousing002"
  Placement = pos=(70,19,36.15) rot=(0,1,0;1.5708rad)
  Shapes = -> [Cylinder054,Cylinder055]
FEATURE [Part::Cut] Cut056  label="Bottom001"
  Base = -> Fillet055
  Placement = pos=(9,0,0) rot=(0,0,1;0rad)
  Tool = -> Fusion131
FEATURE [Part::Cut] Cut057
  Base = -> Cut055
  Tool = -> Cut056
FEATURE [Sketcher::SketchObject] Sketch072  label="topSketch021"
  FullyConstrained = true
  sketch-geometry (4):
    g0: ArcOfCircle CenterX=105 CenterY=19 CenterZ=0 NormalX=0 NormalY=0 NormalZ=1 AngleXU=0 Radius=20.6155 StartAngle=5.54125 EndAngle=6.28319
    g1: ArcOfCircle CenterX=105 CenterY=19 CenterZ=0 NormalX=0 NormalY=0 NormalZ=1 AngleXU=0 Radius=13 StartAngle=5.54125 EndAngle=6.28319
    g2: LineSegment StartX=118 StartY=19 StartZ=0 EndX=125.616 EndY=19 EndZ=0
    g3: LineSegment StartX=114.583 StartY=10.2157 StartZ=0 EndX=120.197 EndY=5.06982 EndZ=0
  constraints (7):
    c: Block(g0)
    c: Block(g1)
    c: Coincident(g2,g1)
    c: Coincident(g2,g0)
    c: Horizontal(g2)
    c: Coincident(g3,g1)
    c: Coincident(g3,g0)
FEATURE [Part::Extrusion] Extrude063  label="bottomPlugHousingBit003"
  Base = -> Sketch072
  Dir = (0,0,1)
  DirMode = 2
  FaceMakerClass = Part::FaceMakerBullseye
  LengthFwd = 72
  LengthRev = 0
  Solid = true
  Symmetric = false
FEATURE [Part::Cylinder] Cylinder056
  Angle = 360
  AttacherType = Attacher::AttachEngine3D
  Height = 20
  Placement = pos=(0,0,36.15) rot=(0,0,1;0rad)
  Radius = 14.3
FEATURE [Part::Cylinder] Cylinder057
  Angle = 360
  AttacherType = Attacher::AttachEngine3D
  Height = 10
  Placement = pos=(0,0,36.15) rot=(0,0,1;0rad)
  Radius = 4
FEATURE [Part::Box] Box034  label="removeToCreteHoleForPlugHousing047"
  AttacherType = Attacher::AttachEngine3D
  Height = 28.6
  Length = 20
  Placement = pos=(106.15,0,21.7) rot=(0,0,1;0rad)
  Width = 19
FEATURE [Part::Cylinder] Cylinder058
  Angle = 360
  AttacherType = Attacher::AttachEngine3D
  Height = 20
  Placement = pos=(0,0,36.15) rot=(0,0,1;0rad)
  Radius = 14.3
FEATURE [Part::Cylinder] Cylinder059
  Angle = 360
  AttacherType = Attacher::AttachEngine3D
  Height = 10
  Placement = pos=(0,0,36.15) rot=(0,0,1;0rad)
  Radius = 4
FEATURE [Part::MultiFuse] Fusion134  label="removeToCreteHoleForPlugHousing046"
  Placement = pos=(70,19,36) rot=(0,1,0;1.5708rad)
  Shapes = -> [Cylinder058,Cylinder059]
FEATURE [Part::Cylinder] Cylinder060
  Angle = 360
  AttacherType = Attacher::AttachEngine3D
  Height = 20
  Placement = pos=(0,0,36.15) rot=(0,0,1;0rad)
  Radius = 14
FEATURE [Part::Cylinder] Cylinder061
  Angle = 360
  AttacherType = Attacher::AttachEngine3D
  Height = 10
  Placement = pos=(0,0,36.15) rot=(0,0,1;0rad)
  Radius = 4
FEATURE [Part::MultiFuse] Fusion135  label="removeToCreteHoleForPlugHousing048"
  Placement = pos=(70,19,36) rot=(0,1,0;1.5708rad)
  Shapes = -> [Cylinder060,Cylinder061]
FEATURE [Part::Box] Box035  label="removeToCreteHoleForPlugHousing049"
  AttacherType = Attacher::AttachEngine3D
  Height = 28.6
  Length = 20
  Placement = pos=(106.15,0,21.7) rot=(0,0,1;0rad)
  Width = 19
FEATURE [Part::MultiFuse] Fusion133  label="removeToCreteHoleForPlugHousing045"
  Placement = pos=(0,0,-28.3) rot=(0,0,1;0rad)
  Shapes = -> [Box035,Fusion134]
FEATURE [Part::MultiFuse] Fusion138  label="removeToCreteHoleForPlugHousing051"
  Placement = pos=(70,19,36) rot=(0,1,0;1.5708rad)
  Shapes = -> [Cylinder056,Cylinder057]
FEATURE [Part::MultiFuse] Fusion137  label="removeToCreteHoleForPlugHousing050"
  Placement = pos=(0,0,28.3) rot=(0,0,1;0rad)
  Shapes = -> [Box034,Fusion138]
FEATURE [Part::MultiFuse] Fusion132  label="removeToCreatePlugHousingBottomBit002"
  Shapes = -> [Fusion133,Fusion137]
FEATURE [Part::MultiFuse] Fusion136  label="removeToCreatePlugHousingBottomBit003"
  Shapes = -> [Fusion135,Fusion132]
FEATURE [Part::Cut] Cut058  label="bottomPlugHousingBit002"
  Base = -> Extrude063
  Placement = pos=(-0.09,0,0) rot=(0,0,1;0rad)
  Tool = -> Fusion136
FEATURE [Sketcher::SketchObject] Sketch073  label="bottomSketch003"
  FullyConstrained = true
  sketch-geometry (45):
    g0: LineSegment StartX=6.29999 StartY=8 StartZ=0 EndX=3.29999 EndY=8 EndZ=0
    g1: LineSegment StartX=3.29999 StartY=8 StartZ=0 EndX=3.29999 EndY=-6.03275e-07 EndZ=0
    g2: ArcOfCircle CenterX=8.29999 CenterY=5 CenterZ=0 NormalX=0 NormalY=0 NormalZ=1 AngleXU=0 Radius=2 StartAngle=3.14159 EndAngle=4.71239
    g3: LineSegment StartX=6.29999 StartY=8 StartZ=0 EndX=6.29999 EndY=5 EndZ=0
    g4: ArcOfCircle CenterX=105 CenterY=19 CenterZ=0 NormalX=0 NormalY=0 NormalZ=1 AngleXU=0 Radius=12.7 StartAngle=4.71239 EndAngle=5.94289
    g5-g11: Circle x7 (B-spline internal-alignment scaffolding for g12; pole/knot coordinates omitted)
    g12: BSplineCurve PolesCount=7 KnotsCount=5 Degree=3 IsPeriodic=0
    g13-g17: GeomPoint x5 (B-spline internal-alignment scaffolding for g12; pole/knot coordinates omitted)
    g18: ArcOfCircle CenterX=105 CenterY=19 CenterZ=0 NormalX=0 NormalY=0 NormalZ=1 AngleXU=0 Radius=15.7 StartAngle=5.81226 EndAngle=6.28319
    g19: BSplineCurve PolesCount=5 KnotsCount=3 Degree=3 IsPeriodic=0
    g20: LineSegment StartX=8.29999 StartY=3 StartZ=0 EndX=101.7 EndY=3 EndZ=0
    g21: LineSegment StartX=3.29999 StartY=-6.03275e-07 StartZ=0 EndX=105 EndY=-6.03275e-07 EndZ=0
    g22: LineSegment StartX=120.974 StartY=8.71251 StartZ=0 EndX=122.332 EndY=7.83778 EndZ=0
    g23: LineSegment StartX=105 StartY=-6.03274e-07 StartZ=0 EndX=113 EndY=-6.03274e-07 EndZ=0
    g24: ArcOfCircle CenterX=105 CenterY=19 CenterZ=0 NormalX=0 NormalY=0 NormalZ=1 AngleXU=0 Radius=20.6155 StartAngle=5.11091 EndAngle=5.71103
    g25: ArcOfCircle CenterX=117.7 CenterY=19 CenterZ=0 NormalX=0 NormalY=0 NormalZ=1 AngleXU=0 Radius=3 StartAngle=1.2e-15 EndAngle=2.10468
    g26: Circle CenterX=116.345 CenterY=16.3232 CenterZ=0 NormalX=0 NormalY=0 NormalZ=1 AngleXU=0 Radius=1
    g27: Circle CenterX=117.24 CenterY=15.7584 CenterZ=0 NormalX=0 NormalY=0 NormalZ=1 AngleXU=0 Radius=1
    g28: Circle CenterX=116.972 CenterY=14.7612 CenterZ=0 NormalX=0 NormalY=0 NormalZ=1 AngleXU=0 Radius=1
    g29: BSplineCurve PolesCount=3 KnotsCount=2 Degree=2 IsPeriodic=0
    g30: GeomPoint X=116.345 Y=16.3232 Z=0
    g31: GeomPoint X=116.972 Y=14.7612 Z=0
    g32: Circle CenterX=115.828 CenterY=17.157 CenterZ=0 NormalX=0 NormalY=0 NormalZ=1 AngleXU=0 Radius=1
    g33: Circle CenterX=115.841 CenterY=16.639 CenterZ=0 NormalX=0 NormalY=0 NormalZ=1 AngleXU=0 Radius=1
    g34: Circle CenterX=116.345 CenterY=16.3232 CenterZ=0 NormalX=0 NormalY=0 NormalZ=1 AngleXU=0 Radius=1
    g35: BSplineCurve PolesCount=3 KnotsCount=2 Degree=2 IsPeriodic=0
    g36: GeomPoint X=115.828 Y=17.157 Z=0
    g37: GeomPoint X=116.345 Y=16.3232 Z=0
    g38: LineSegment StartX=115.828 StartY=17.157 StartZ=0 EndX=115.828 EndY=20.8307 EndZ=0
    g39: Circle CenterX=115.828 CenterY=20.8307 CenterZ=0 NormalX=0 NormalY=0 NormalZ=1 AngleXU=0 Radius=1
    g40: Circle CenterX=115.831 CenterY=21.3396 CenterZ=0 NormalX=0 NormalY=0 NormalZ=1 AngleXU=0 Radius=1
    g41: Circle CenterX=116.173 CenterY=21.5825 CenterZ=0 NormalX=0 NormalY=0 NormalZ=1 AngleXU=0 Radius=1
    g42: BSplineCurve PolesCount=3 KnotsCount=2 Degree=2 IsPeriodic=0
    g43: GeomPoint X=115.828 Y=20.8307 Z=0
    g44: GeomPoint X=116.173 Y=21.5825 Z=0
  constraints (70):
    c: Horizontal(g0)
    c: Distance(g0) = 3
    c: Coincident(g1,g0)
    c: Vertical(g1)
    c: Block(g2)
    c: Block(g0)
    c: Coincident(g3,g0)
    c: Coincident(g3,g2)
    c: Vertical(g3)
    c: Block(g1)
    c: Block(g4)
    c: Coincident(g19,g4)
    c: Block(g19)
    c: Equal(g5, g6-g11) x6
    c: InternalAlignment(g5-g11 -> g12) x7
    c: InternalAlignment(g13-g17 -> g12) x5
    c: Block(g12)
    c: Coincident(g18,g12)
    c: Block(g18)
    c: Coincident(g20,g2)
    c: Coincident(g20,g19)
    c: Horizontal(g20)
    c: Distance(g20) = 93.4
    c: Coincident(g21,g1)
    c: Horizontal(g21)
    c: Distance(g21) = 101.7
    c: Horizontal(g23)
    c: Distance(g23) = 8
    c: Coincident(g24,g23)
    c: Block(g23)
    c: Coincident(g22,g24)
    c: Block(g24)
    c: Block(g22)
    c: Distance(g22) = 1.61553
    c: Coincident(g25,g18)
    c: Block(g25)
    c: Weight(g26) = 1
    c: Equal(g26,g27)
    c: Equal(g26,g28)
    c: Coincident(g29,g4)
    c: InternalAlignment(g26,g29)
    c: InternalAlignment(g27,g29)
    c: InternalAlignment(g28,g29)
    c: InternalAlignment(g30,g29)
    c: InternalAlignment(g31,g29)
    c: Block(g29)
    c: Weight(g32) = 1
    c: Equal(g32,g33)
    c: Equal(g32,g34)
    c: Coincident(g35,g29)
    c: InternalAlignment(g32,g35)
    c: InternalAlignment(g33,g35)
    c: InternalAlignment(g34,g35)
    c: InternalAlignment(g36,g35)
    c: InternalAlignment(g37,g35)
    c: Block(g35)
    c: Coincident(g38,g35)
    c: Vertical(g38)
    c: Block(g38)
    c: Coincident(g42,g38)
    c: Weight(g39) = 1
    c: Equal(g39,g40)
    c: Equal(g39,g41)
    c: Coincident(g42,g25)
    c: InternalAlignment(g39,g42)
    c: InternalAlignment(g40,g42)
    c: InternalAlignment(g41,g42)
    c: InternalAlignment(g43,g42)
    c: InternalAlignment(g44,g42)
    c: Block(g42)
FEATURE [Part::Extrusion] Extrude064  label="bottom016"
  Base = -> Sketch073
  Dir = (0,0,1)
  DirMode = 2
  FaceMakerClass = Part::FaceMakerBullseye
  LengthFwd = 71.4
  LengthRev = 0
  Placement = pos=(0,0,0.3) rot=(0,0,1;0rad)
  Solid = true
  Symmetric = false
FEATURE [Part::Revolution] Revolve157  label="removeToCreateScrewAndThreadedInsertHole063"
  Angle = 360
  Axis = (0,1,0)
  Base = (0,0,0)
  FaceMakerClass = Part::FaceMakerBullseye
  Placement = pos=(12.5,0,10) rot=(0,0,1;0rad)
  Solid = false
  Source = -> Face141
  Symmetric = false
FEATURE [Sketcher::SketchObject] Sketch074
  FullyConstrained = true
  Placement = pos=(117,19,0) rot=(0.57735,0.57735,0.57735;2.0944rad)
  sketch-geometry (48):
    g0: LineSegment StartX=-49.19 StartY=69.25 StartZ=0 EndX=-49.19 EndY=66.25 EndZ=0
    g1: LineSegment StartX=-49.19 StartY=63.5 StartZ=0 EndX=-49.19 EndY=60.5 EndZ=0
    g2: LineSegment StartX=-49.19 StartY=57.75 StartZ=0 EndX=-49.19 EndY=54.75 EndZ=0
    g3: LineSegment StartX=-49.19 StartY=52 StartZ=0 EndX=-49.19 EndY=49 EndZ=0
    g4: LineSegment StartX=-49.19 StartY=46.25 StartZ=0 EndX=-49.19 EndY=43.25 EndZ=0
    g5: LineSegment StartX=-49.19 StartY=40.5 StartZ=0 EndX=-49.19 EndY=37.5 EndZ=0
    g6: LineSegment StartX=-49.19 StartY=34.5 StartZ=0 EndX=-49.19 EndY=31.5 EndZ=0
    g7: LineSegment StartX=-49.19 StartY=28.75 StartZ=0 EndX=-49.19 EndY=25.75 EndZ=0
    g8: LineSegment StartX=-49.19 StartY=23 StartZ=0 EndX=-49.19 EndY=20 EndZ=0
    g9: LineSegment StartX=-49.19 StartY=17.25 StartZ=0 EndX=-49.19 EndY=14.25 EndZ=0
    g10: LineSegment StartX=-49.19 StartY=11.5 StartZ=0 EndX=-49.19 EndY=8.5 EndZ=0
    g11: LineSegment StartX=-49.19 StartY=5.75 StartZ=0 EndX=-49.19 EndY=2.75 EndZ=0
    g12: ArcOfCircle CenterX=-1.5 CenterY=67.75 CenterZ=0 NormalX=0 NormalY=0 NormalZ=1 AngleXU=0 Radius=1.5 StartAngle=4.71239 EndAngle=7.85398
    g13: ArcOfCircle CenterX=-1.5 CenterY=62 CenterZ=0 NormalX=0 NormalY=0 NormalZ=1 AngleXU=0 Radius=1.5 StartAngle=4.71239 EndAngle=7.85398
    g14: ArcOfCircle CenterX=-1.5 CenterY=56.25 CenterZ=0 NormalX=0 NormalY=0 NormalZ=1 AngleXU=0 Radius=1.5 StartAngle=4.71239 EndAngle=7.85398
    g15: ArcOfCircle CenterX=-11.49 CenterY=50.5 CenterZ=0 NormalX=0 NormalY=0 NormalZ=1 AngleXU=0 Radius=1.5 StartAngle=4.71239 EndAngle=7.85398
    g16: ArcOfCircle CenterX=-16.28 CenterY=44.75 CenterZ=0 NormalX=0 NormalY=0 NormalZ=1 AngleXU=0 Radius=1.5 StartAngle=4.71239 EndAngle=7.85398
    g17: ArcOfCircle CenterX=-18.2337 CenterY=39 CenterZ=0 NormalX=0 NormalY=0 NormalZ=1 AngleXU=0 Radius=1.5 StartAngle=4.71485 EndAngle=7.85398
    g18: ArcOfCircle CenterX=-16.2837 CenterY=27.25 CenterZ=0 NormalX=0 NormalY=0 NormalZ=1 AngleXU=0 Radius=1.5 StartAngle=4.71485 EndAngle=7.85398
    g19: ArcOfCircle CenterX=-18.2337 CenterY=33 CenterZ=0 NormalX=0 NormalY=0 NormalZ=1 AngleXU=0 Radius=1.5 StartAngle=4.71485 EndAngle=7.85398
    g20: ArcOfCircle CenterX=-11.49 CenterY=21.5 CenterZ=0 NormalX=0 NormalY=0 NormalZ=1 AngleXU=0 Radius=1.5 StartAngle=4.71239 EndAngle=7.85398
    g21: ArcOfCircle CenterX=-1.5 CenterY=4.25 CenterZ=0 NormalX=0 NormalY=0 NormalZ=1 AngleXU=0 Radius=1.5 StartAngle=4.71239 EndAngle=7.85398
    g22: ArcOfCircle CenterX=-1.5 CenterY=10 CenterZ=0 NormalX=0 NormalY=0 NormalZ=1 AngleXU=0 Radius=1.5 StartAngle=4.71239 EndAngle=7.85398
    g23: ArcOfCircle CenterX=-1.5 CenterY=15.75 CenterZ=0 NormalX=0 NormalY=0 NormalZ=1 AngleXU=0 Radius=1.5 StartAngle=4.71239 EndAngle=7.85398
    g24: LineSegment StartX=-49.19 StartY=69.25 StartZ=0 EndX=-1.5 EndY=69.25 EndZ=0
    g25: LineSegment StartX=-49.19 StartY=66.25 StartZ=0 EndX=-1.5 EndY=66.25 EndZ=0
    g26: LineSegment StartX=-49.19 StartY=63.5 StartZ=0 EndX=-1.5 EndY=63.5 EndZ=0
    g27: LineSegment StartX=-49.19 StartY=60.5 StartZ=0 EndX=-1.5 EndY=60.5 EndZ=0
    g28: LineSegment StartX=-49.19 StartY=57.75 StartZ=0 EndX=-1.5 EndY=57.75 EndZ=0
    g29: LineSegment StartX=-49.19 StartY=54.75 StartZ=0 EndX=-1.5 EndY=54.75 EndZ=0
    g30: LineSegment StartX=-49.19 StartY=52 StartZ=0 EndX=-11.49 EndY=52 EndZ=0
    g31: LineSegment StartX=-49.19 StartY=49 StartZ=0 EndX=-11.49 EndY=49 EndZ=0
    g32: LineSegment StartX=-49.19 StartY=46.25 StartZ=0 EndX=-16.28 EndY=46.25 EndZ=0
    g33: LineSegment StartX=-49.19 StartY=43.25 StartZ=0 EndX=-16.28 EndY=43.25 EndZ=0
    g34: LineSegment StartX=-49.19 StartY=40.5 StartZ=0 EndX=-18.2337 EndY=40.5 EndZ=0
    g35: LineSegment StartX=-49.19 StartY=37.5 StartZ=0 EndX=-18.23 EndY=37.5 EndZ=0
    g36: LineSegment StartX=-49.19 StartY=34.5 StartZ=0 EndX=-18.2337 EndY=34.5 EndZ=0
    g37: LineSegment StartX=-49.19 StartY=31.5 StartZ=0 EndX=-18.23 EndY=31.5 EndZ=0
    g38: LineSegment StartX=-49.19 StartY=28.75 StartZ=0 EndX=-16.2837 EndY=28.75 EndZ=0
    g39: LineSegment StartX=-49.19 StartY=25.75 StartZ=0 EndX=-16.28 EndY=25.75 EndZ=0
    g40: LineSegment StartX=-49.19 StartY=23 StartZ=0 EndX=-11.49 EndY=23 EndZ=0
    g41: LineSegment StartX=-49.19 StartY=20 StartZ=0 EndX=-11.49 EndY=20 EndZ=0
    g42: LineSegment StartX=-49.19 StartY=17.25 StartZ=0 EndX=-1.5 EndY=17.25 EndZ=0
    g43: LineSegment StartX=-49.19 StartY=14.25 StartZ=0 EndX=-1.5 EndY=14.25 EndZ=0
    g44: LineSegment StartX=-49.19 StartY=11.5 StartZ=0 EndX=-1.5 EndY=11.5 EndZ=0
    g45: LineSegment StartX=-49.19 StartY=8.5 StartZ=0 EndX=-1.5 EndY=8.5 EndZ=0
    g46: LineSegment StartX=-49.19 StartY=5.75 StartZ=0 EndX=-1.5 EndY=5.75 EndZ=0
    g47: LineSegment StartX=-49.19 StartY=2.75 StartZ=0 EndX=-1.5 EndY=2.75 EndZ=0
  constraints (120):
    c: Vertical(g0)
    c: Distance(g0) = 3
    c: Block(g0)
    c: Vertical(g1)
    c: Distance(g1) = 3
    c: Vertical(g2)
    c: Equal(g0,g2) = 3
    c: Block(g2)
    c: Vertical(g3)
    c: Equal(g1,g3) = 3
    c: Vertical(g4)
    c: Equal(g0,g4) = 3
    c: Block(g4)
    c: Vertical(g5)
    c: Equal(g1,g5) = 3
    c: Vertical(g6)
    c: Equal(g0,g6) = 3
    c: Block(g6)
    c: Vertical(g7)
    c: Equal(g1,g7) = 3
    c: Vertical(g8)
    c: Equal(g0,g8) = 3
    c: Block(g8)
    c: Vertical(g9)
    c: Equal(g1,g9) = 3
    c: Vertical(g10)
    c: Equal(g0,g10) = 3
    c: Block(g10)
    c: Vertical(g11)
    c: Equal(g1,g11) = 3
    c: Block(g12)
    c: Block(g13)
    c: Block(g14)
    c: Block(g15)
    c: Block(g16)
    c: Block(g17)
    c: Block(g18)
    c: Block(g19)
    c: Block(g20)
    c: Block(g21)
    c: Block(g22)
    c: Block(g23)
    c: Block(g11)
    c: Block(g9)
    c: Block(g7)
    c: Block(g5)
    c: Block(g3)
    c: Block(g1)
    c: Coincident(g24,g0)
    c: Coincident(g24,g12)
    c: Horizontal(g24)
    c: Coincident(g25,g0)
    c: Coincident(g25,g12)
    c: Horizontal(g25)
    c: Coincident(g26,g1)
    c: Coincident(g26,g13)
    c: Horizontal(g26)
    c: Coincident(g27,g1)
    c: Coincident(g27,g13)
    c: Horizontal(g27)
    c: Coincident(g28,g2)
    c: Coincident(g28,g14)
    c: Horizontal(g28)
    c: Coincident(g29,g2)
    c: Coincident(g29,g14)
    c: Horizontal(g29)
    c: Coincident(g30,g3)
    c: Coincident(g30,g15)
    c: Horizontal(g30)
    c: Coincident(g31,g3)
    c: Coincident(g31,g15)
    c: Horizontal(g31)
    c: Coincident(g32,g4)
    c: Coincident(g32,g16)
    c: Horizontal(g32)
    c: Coincident(g33,g4)
    c: Coincident(g33,g16)
    c: Horizontal(g33)
    c: Coincident(g34,g5)
    c: Coincident(g34,g17)
    c: Horizontal(g34)
    c: Coincident(g35,g5)
    c: Coincident(g35,g17)
    c: Horizontal(g35)
    c: Coincident(g36,g6)
    c: Coincident(g36,g19)
    c: Horizontal(g36)
    c: Coincident(g37,g6)
    c: Coincident(g37,g19)
    c: Horizontal(g37)
    c: Coincident(g38,g7)
    c: Coincident(g38,g18)
    c: Horizontal(g38)
    c: Coincident(g39,g7)
    c: Coincident(g39,g18)
    c: Horizontal(g39)
    c: Coincident(g40,g8)
    c: Coincident(g40,g20)
    c: Horizontal(g40)
    c: Coincident(g41,g8)
    c: Coincident(g41,g20)
    c: Horizontal(g41)
    c: Coincident(g42,g9)
    c: Coincident(g42,g23)
    c: Horizontal(g42)
    c: Coincident(g43,g9)
    c: Coincident(g43,g23)
    c: Horizontal(g43)
    c: Coincident(g44,g10)
    c: Coincident(g44,g22)
    c: Horizontal(g44)
    c: Coincident(g45,g10)
    c: Coincident(g45,g22)
    c: Horizontal(g45)
    c: Coincident(g46,g11)
    c: Coincident(g46,g21)
    c: Horizontal(g46)
    c: Coincident(g47,g11)
    c: Coincident(g47,g21)
    c: Horizontal(g47)
FEATURE [Part::Extrusion] Extrude065
  Base = -> Sketch074
  Dir = (1,0,0)
  DirMode = 2
  FaceMakerClass = Part::FaceMakerBullseye
  LengthFwd = 23
  LengthRev = 0
  Placement = pos=(-19,0,0) rot=(0,0,1;0rad)
  Solid = true
  Symmetric = false
FEATURE [Part::Fillet] Fillet056  label="removeToCreateVentalationHoles003"
  Base = -> Extrude065
  Edges = <same value as first occurrence — deduplicated (x6 in doc)>
  Placement = pos=(7,0.02,0) rot=(0,0,1;0rad)
FEATURE [Part::Revolution] Revolve158  label="removeToCreateScrewAndThreadedInsertHole065"
  Angle = 360
  Axis = (0,1,0)
  Base = (0,0,0)
  FaceMakerClass = Part::FaceMakerBullseye
  Placement = pos=(12.5,0,62) rot=(0,0,1;0rad)
  Solid = false
  Source = -> Face146
  Symmetric = false
FEATURE [Part::Revolution] Revolve159  label="removeToCreateScrewAndThreadedInsertHole066"
  Angle = 360
  Axis = (0,1,0)
  Base = (0,0,0)
  FaceMakerClass = Part::FaceMakerBullseye
  Placement = pos=(89.5,0,68.5) rot=(0,0,1;0rad)
  Solid = false
  Source = -> Face143
  Symmetric = false
FEATURE [Part::Revolution] Revolve160  label="removeToCreateScrewAndThreadedInsertHole067"
  Angle = 360
  Axis = (0,1,0)
  Base = (0,0,0)
  FaceMakerClass = Part::FaceMakerBullseye
  Placement = pos=(89.5,0,3.5) rot=(0,0,1;0rad)
  Solid = false
  Source = -> Face142
  Symmetric = false
FEATURE [Part::Revolution] Revolve161  label="removeToCreateScrewAndThreadedInsertHole068"
  Angle = 360
  Axis = (0,1,0)
  Base = (0,0,0)
  FaceMakerClass = Part::FaceMakerBullseye
  Placement = pos=(109.5,4.7,3.5) rot=(0,0,1;0rad)
  Solid = false
  Source = -> Face145
  Symmetric = false
FEATURE [Part::Revolution] Revolve162  label="removeToCreateScrewAndThreadedInsertHole069"
  Angle = 360
  Axis = (0,1,0)
  Base = (0,0,0)
  FaceMakerClass = Part::FaceMakerBullseye
  Placement = pos=(109.5,4.7,68.5) rot=(0,0,1;0rad)
  Solid = false
  Source = -> Face144
  Symmetric = false
FEATURE [Part::MultiFuse] Fusion141  label="removeToCreateScrewAndThreadedInsertHole064"
  Shapes = -> [Revolve162,Revolve161,Revolve160,Revolve159,Revolve158,Revolve157]
FEATURE [Part::Cylinder] Cylinder062
  Angle = 360
  AttacherType = Attacher::AttachEngine3D
  Height = 20
  Placement = pos=(0,0,36.15) rot=(0,0,1;0rad)
  Radius = 14
FEATURE [Part::Cylinder] Cylinder063
  Angle = 360
  AttacherType = Attacher::AttachEngine3D
  Height = 10
  Placement = pos=(0,0,36.15) rot=(0,0,1;0rad)
  Radius = 4
FEATURE [Part::MultiFuse] Fusion139  label="removeToCreteHoleForPlugHousing052"
  Placement = pos=(70,19,36) rot=(0,1,0;1.5708rad)
  Shapes = -> [Cylinder062,Cylinder063]
FEATURE [Part::Cut] Cut060  label="bottom017"
  Base = -> Extrude064
  Tool = -> Fusion139
FEATURE [Part::Cut] Cut061  label="bottom019"
  Base = -> Cut060
  Tool = -> Fusion141
FEATURE [Part::MultiFuse] Fusion140  label="bottom018"
  Shapes = -> [Cut061,Cut058]
FEATURE [Part::Cut] Cut059  label="bottom020"
  Base = -> Fusion140
  Tool = -> Fillet056
FEATURE [Part::Box] Box036  label="Cube021"
  AttacherType = Attacher::AttachEngine3D
  Height = 80
  Length = 26
  Placement = pos=(0,-1,-5) rot=(0,0,1;0rad)
  Width = 11
FEATURE [Part::Cut] Cut062  label="removeFromBottom002"
  Base = -> Cut057
  Tool = -> Box036
FEATURE [Part::Cut] Cut063
  Base = -> Cut059
  Tool = -> Cut062
FEATURE [Part::Cut] Cut064  label="pcbStands"
  Base = -> Fusion095
  Tool = -> Fusion127
FEATURE [Sketcher::SketchObject] Sketch075  label="topSketch022"
  FullyConstrained = true
  sketch-geometry (6):
    g0: LineSegment StartX=19 StartY=38 StartZ=0 EndX=117 EndY=38 EndZ=0
    g1: ArcOfCircle CenterX=19 CenterY=19 CenterZ=0 NormalX=0 NormalY=0 NormalZ=1 AngleXU=0 Radius=19 StartAngle=1.5708 EndAngle=3.14159
    g2: LineSegment StartX=117 StartY=38 StartZ=0 EndX=117 EndY=19 EndZ=0
    g3: LineSegment StartX=98 StartY=1.0161e-12 StartZ=0 EndX=5.22862e-06 EndY=1.0161e-12 EndZ=0
    g4: LineSegment StartX=5.22862e-06 StartY=19 StartZ=0 EndX=5.22862e-06 EndY=1.0161e-12 EndZ=0
    g5: ArcOfCircle CenterX=98 CenterY=19 CenterZ=0 NormalX=0 NormalY=0 NormalZ=1 AngleXU=0 Radius=19 StartAngle=4.71239 EndAngle=6.28319
  constraints (16):
    c: Horizontal(g0)
    c: Distance(g0) = 98
    c: Coincident(g1,g0)
    c: Block(g1)
    c: Coincident(g2,g0)
    c: Vertical(g2)
    c: Distance(g2) = 19
    c: Horizontal(g3)
    c: Coincident(g4,g1)
    c: Vertical(g4)
    c: Coincident(g3,g4)
    c: Block(g3)
    c: Coincident(g5,g2)
    c: Coincident(g5,g3)
    c: Block(g0)
    c: Block(g5)
FEATURE [Part::Extrusion] Extrude067  label="sideB003"
  Base = -> Sketch075
  Dir = (0,0,1)
  DirMode = 2
  FaceMakerClass = Part::FaceMakerBullseye
  LengthFwd = 3
  LengthRev = 0
  Placement = pos=(0,0,71.7) rot=(0,0,1;0rad)
  Solid = true
  Symmetric = false
FEATURE [Sketcher::SketchObject] Sketch076  label="topSketch023"
  FullyConstrained = true
  sketch-geometry (6):
    g0: LineSegment StartX=19 StartY=38 StartZ=0 EndX=117 EndY=38 EndZ=0
    g1: ArcOfCircle CenterX=19 CenterY=19 CenterZ=0 NormalX=0 NormalY=0 NormalZ=1 AngleXU=0 Radius=19 StartAngle=1.5708 EndAngle=3.14159
    g2: LineSegment StartX=117 StartY=38 StartZ=0 EndX=117 EndY=19 EndZ=0
    g3: LineSegment StartX=98 StartY=1.0161e-12 StartZ=0 EndX=5.22862e-06 EndY=1.0161e-12 EndZ=0
    g4: LineSegment StartX=5.22862e-06 StartY=19 StartZ=0 EndX=5.22862e-06 EndY=1.0161e-12 EndZ=0
    g5: ArcOfCircle CenterX=98 CenterY=19 CenterZ=0 NormalX=0 NormalY=0 NormalZ=1 AngleXU=0 Radius=19 StartAngle=4.71239 EndAngle=6.28319
  constraints (16):
    c: Horizontal(g0)
    c: Distance(g0) = 98
    c: Coincident(g1,g0)
    c: Block(g1)
    c: Coincident(g2,g0)
    c: Vertical(g2)
    c: Distance(g2) = 19
    c: Horizontal(g3)
    c: Coincident(g4,g1)
    c: Vertical(g4)
    c: Coincident(g3,g4)
    c: Block(g3)
    c: Coincident(g5,g2)
    c: Coincident(g5,g3)
    c: Block(g0)
    c: Block(g5)
FEATURE [Part::Extrusion] Extrude066  label="sideA003"
  Base = -> Sketch076
  Dir = (0,0,1)
  DirMode = 2
  FaceMakerClass = Part::FaceMakerBullseye
  LengthFwd = 3
  LengthRev = 0
  Placement = pos=(0,0,-2.7) rot=(0,0,1;0rad)
  Solid = true
  Symmetric = false
FEATURE [Part::MultiFuse] Fusion142  label="removeFromBottom003"
  Placement = pos=(2,0,0) rot=(0,0,1;0rad)
  Shapes = -> [Extrude066,Extrude067]
FEATURE [Part::Cut] Cut065  label="screwRetainers002"
  Base = -> Fusion096
  Tool = -> Fusion142
FEATURE [Sketcher::SketchObject] Sketch077
  FullyConstrained = true
  Placement = pos=(117,19,0) rot=(0.57735,0.57735,0.57735;2.0944rad)
  sketch-geometry (8):
    g0: LineSegment StartX=-49.19 StartY=63.5 StartZ=0 EndX=-49.19 EndY=60.5 EndZ=0
    g1: LineSegment StartX=-49.19 StartY=11.5 StartZ=0 EndX=-49.19 EndY=8.5 EndZ=0
    g2: ArcOfCircle CenterX=-1.5 CenterY=62 CenterZ=0 NormalX=0 NormalY=0 NormalZ=1 AngleXU=0 Radius=1.5 StartAngle=4.71239 EndAngle=7.85398
    g3: ArcOfCircle CenterX=-1.5 CenterY=10 CenterZ=0 NormalX=0 NormalY=0 NormalZ=1 AngleXU=0 Radius=1.5 StartAngle=4.71239 EndAngle=7.85398
    g4: LineSegment StartX=-49.19 StartY=63.5 StartZ=0 EndX=-1.5 EndY=63.5 EndZ=0
    g5: LineSegment StartX=-49.19 StartY=60.5 StartZ=0 EndX=-1.5 EndY=60.5 EndZ=0
    g6: LineSegment StartX=-49.19 StartY=11.5 StartZ=0 EndX=-1.5 EndY=11.5 EndZ=0
    g7: LineSegment StartX=-49.19 StartY=8.5 StartZ=0 EndX=-1.5 EndY=8.5 EndZ=0
  constraints (19):
    c: Vertical(g0)
    c: Distance(g0) = 3
    c: Vertical(g1)
    c: Block(g1)
    c: Block(g2)
    c: Block(g3)
    c: Block(g0)
    c: Coincident(g4,g0)
    c: Coincident(g4,g2)
    c: Horizontal(g4)
    c: Coincident(g5,g0)
    c: Coincident(g5,g2)
    c: Horizontal(g5)
    c: Coincident(g6,g1)
    c: Coincident(g6,g3)
    c: Horizontal(g6)
    c: Coincident(g7,g1)
    c: Coincident(g7,g3)
    c: Horizontal(g7)
FEATURE [Part::Extrusion] Extrude068
  Base = -> Sketch077
  Dir = (1,0,0)
  DirMode = 2
  FaceMakerClass = Part::FaceMakerBullseye
  LengthFwd = 10
  LengthRev = 0
  Solid = true
  Symmetric = false
FEATURE [Part::Fillet] Fillet057  label="removeFromtMoreFrontCaseScrewRetainers002"
  Base = -> Extrude068
  Edges = 4 edges r=1.49: [Edge6,Edge11,Edge18,Edge23]
  Placement = pos=(-12,0,0) rot=(0,0,1;0rad)
FEATURE [Sketcher::SketchObject] Sketch078
  FullyConstrained = true
  Placement = pos=(117,19,0) rot=(0.57735,0.57735,0.57735;2.0944rad)
  sketch-geometry (8):
    g0: LineSegment StartX=-49.19 StartY=69.25 StartZ=0 EndX=-49.19 EndY=66.25 EndZ=0
    g1: LineSegment StartX=-49.19 StartY=5.75 StartZ=0 EndX=-49.19 EndY=2.75 EndZ=0
    g2: ArcOfCircle CenterX=-1.5 CenterY=67.75 CenterZ=0 NormalX=0 NormalY=0 NormalZ=1 AngleXU=0 Radius=1.5 StartAngle=4.71239 EndAngle=7.85398
    g3: ArcOfCircle CenterX=-1.5 CenterY=4.25 CenterZ=0 NormalX=0 NormalY=0 NormalZ=1 AngleXU=0 Radius=1.5 StartAngle=4.71239 EndAngle=7.85398
    g4: LineSegment StartX=-49.19 StartY=69.25 StartZ=0 EndX=-1.5 EndY=69.25 EndZ=0
    g5: LineSegment StartX=-49.19 StartY=66.25 StartZ=0 EndX=-1.5 EndY=66.25 EndZ=0
    g6: LineSegment StartX=-49.19 StartY=5.75 StartZ=0 EndX=-1.5 EndY=5.75 EndZ=0
    g7: LineSegment StartX=-49.19 StartY=2.75 StartZ=0 EndX=-1.5 EndY=2.75 EndZ=0
  constraints (19):
    c: Vertical(g0)
    c: Distance(g0) = 3
    c: Block(g0)
    c: Vertical(g1)
    c: Block(g2)
    c: Block(g3)
    c: Block(g1)
    c: Coincident(g4,g0)
    c: Coincident(g4,g2)
    c: Horizontal(g4)
    c: Coincident(g5,g0)
    c: Coincident(g5,g2)
    c: Horizontal(g5)
    c: Coincident(g6,g1)
    c: Coincident(g6,g3)
    c: Horizontal(g6)
    c: Coincident(g7,g1)
    c: Coincident(g7,g3)
    c: Horizontal(g7)
FEATURE [Part::Extrusion] Extrude069
  Base = -> Sketch078
  Dir = (1,0,0)
  DirMode = 2
  FaceMakerClass = Part::FaceMakerBullseye
  LengthFwd = 10
  LengthRev = 0
  Solid = true
  Symmetric = false
FEATURE [Part::Fillet] Fillet058  label="removeFromtMoreFrontCaseScrewRetainers003"
  Base = -> Extrude069
  Edges = 4 edges r=1.49: [Edge6,Edge11,Edge18,Edge23]
  Placement = pos=(-4,0,0) rot=(0,0,1;0rad)
FEATURE [Part::Cut] Cut066
  Base = -> Cut065
  Tool = -> Fillet058
FEATURE [Part::Cut] Cut067  label="screwPillars"
  Base = -> Cut066
  Tool = -> Fillet057
FEATURE [Part::MultiFuse] Fusion143  label="bottom021"
  Shapes = -> [Cut031,Cut063]
FEATURE [Part::Cylinder] Cylinder
  Angle = 360
  AttacherType = Attacher::AttachEngine3D
  Height = 10
  Placement = pos=(20.65,12,4.68) rot=(1,0,0;1.5708rad)
  Radius = 2
FEATURE [Part::Cylinder] Cylinder064
  Angle = 360
  AttacherType = Attacher::AttachEngine3D
  Height = 10
  Placement = pos=(20.65,12,67.38) rot=(1,0,0;1.5708rad)
  Radius = 2
FEATURE [Part::Cylinder] Cylinder065
  Angle = 360
  AttacherType = Attacher::AttachEngine3D
  Height = 10
  Placement = pos=(77.15,12,67.38) rot=(1,0,0;1.5708rad)
  Radius = 2
FEATURE [Part::Cylinder] Cylinder066
  Angle = 360
  AttacherType = Attacher::AttachEngine3D
  Height = 10
  Placement = pos=(77.15,12,4.68) rot=(1,0,0;1.5708rad)
  Radius = 2
FEATURE [Part::MultiFuse] Fusion144  label="removeFromThreadedInsertHousing"
  Shapes = -> [Cylinder065,Cylinder064,Cylinder,Cylinder066]
FEATURE [Part::Cut] Cut068  label="pcbStands001"
  Base = -> Cut064
  Tool = -> Fusion144
FEATURE [Part::MultiFuse] Fusion145
  Shapes = -> [Cut068,Fusion143]
FEATURE [Part::MultiFuse] Fusion146
  Shapes = -> [Fusion145]
FEATURE [Part::MultiFuse] Fusion147  label="bottom022"
  Shapes = -> [Cut067,Fusion146]
FEATURE [Part::MultiFuse] Fusion148  label="casePillars005"
  Shapes = -> [Cut047,Fusion092]
